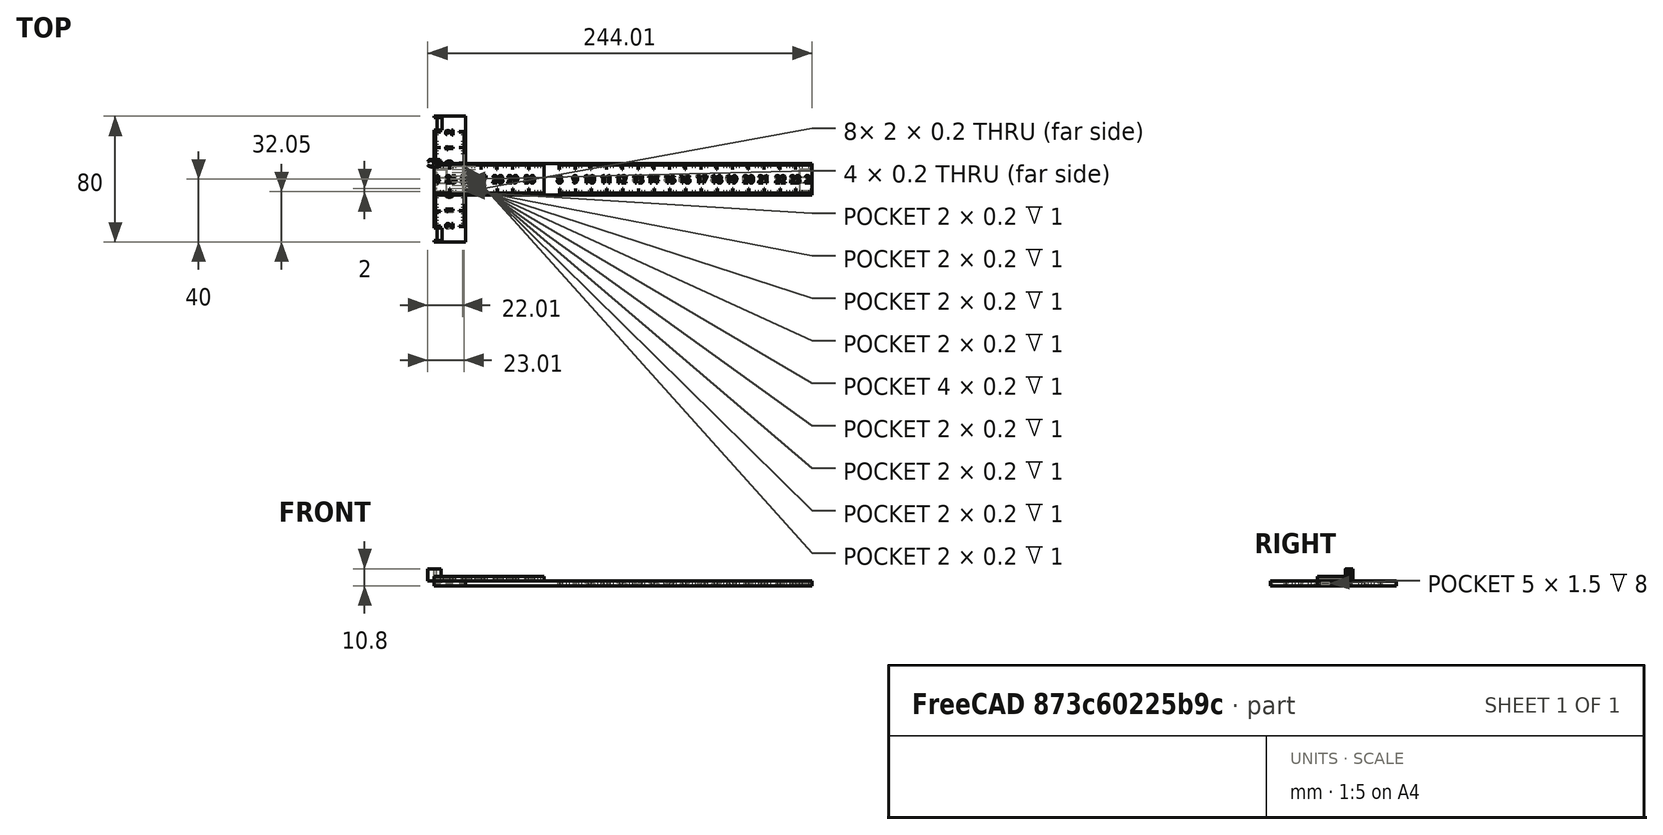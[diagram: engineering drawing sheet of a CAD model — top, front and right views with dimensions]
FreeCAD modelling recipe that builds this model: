
FCSTD DOCUMENT  (FreeCAD 0.20R26155 (Git))
Label: pocket text 30cm 2 sided Bow T Square
License: Creative Commons Attribution
LicenseURL: http://creativecommons.org/licenses/by/4.0/
objects: PartDesign::Pocket×22, Sketcher::SketchObject×20, Part::Part2DObjectPython×6, PartDesign::Pad×4, PartDesign::Body×4, Mesh::Feature×4, PartDesign::Plane×3, Spreadsheet::Sheet×1, PartDesign::Fillet×1
note: 87 computed .brp shape members not serialized (recipe doc carries the construction recipe); baked Part::Feature solids carry a one-line shape summary decoded from their .brp

FEATURE [Sketcher::SketchObject] Sketch  label="ruler"
  FullyConstrained = true
  MapMode = 5
  Support = -> [XY_Plane]
  expr: Constraints[11] = Spreadsheet.longL
  sketch-geometry (8):
    g0: LineSegment StartX=0 StartY=-50 StartZ=0 EndX=20 EndY=-50 EndZ=0
    g1: LineSegment StartX=20 StartY=-50 StartZ=0 EndX=20 EndY=-20 EndZ=0
    g2: LineSegment StartX=20 StartY=-20 StartZ=0 EndX=240 EndY=-20 EndZ=0
    g3: LineSegment StartX=240 StartY=-20 StartZ=0 EndX=240 EndY=0 EndZ=0
    g4: LineSegment StartX=0 StartY=30 StartZ=0 EndX=20 EndY=30 EndZ=0
    g5: LineSegment StartX=20 StartY=30 StartZ=0 EndX=20 EndY=0 EndZ=0
    g6: LineSegment StartX=20 StartY=0 StartZ=0 EndX=240 EndY=0 EndZ=0
    g7: LineSegment StartX=0 StartY=-50 StartZ=0 EndX=0 EndY=30 EndZ=0
  constraints (24):
    c: PointOnObject(g0,g-2)
    c: Horizontal(g0)
    c: Coincident(g0,g1)
    c: Vertical(g1)
    c: Coincident(g1,g2)
    c: Horizontal(g2)
    c: Coincident(g2,g3)
    c: PointOnObject(g3,g-1)
    c: Vertical(g3)
    c: Equal(g3,g0)
    c: DistanceY(g3,g3) = 20
    c: DistanceX(g-1,g3) = 240
    c: DistanceY(g0,g-1) = 50
    c: PointOnObject(g4,g-2)
    c: Horizontal(g4)
    c: Coincident(g4,g5)
    c: Vertical(g5)
    c: Coincident(g5,g6)
    c: Coincident(g6,g3)
    c: Horizontal(g6)
    c: Equal(g4,g0)
    c: Coincident(g7,g0)
    c: Coincident(g7,g4)
    c: DistanceY(g5,g5) = 30
FEATURE [PartDesign::Pad] Pad
  Direction = (1,1,1)
  Length = 3
  Length2 = 100
  Profile = -> Sketch
  Reversed = true
  Type = 0
FEATURE [Sketcher::SketchObject] Sketch001  label="hz cm"
  FullyConstrained = false
  MapMode = 5
  Support = -> [XY_Plane]
  expr: Constraints[9] = Spreadsheet.reticleCmWidth
  expr: Constraints[8] = Spreadsheet.reticleCmHeight
  sketch-geometry (171):
    g0: LineSegment StartX=239.9 StartY=-20 StartZ=0 EndX=239.7 EndY=-20 EndZ=0
    g1: LineSegment StartX=239.7 StartY=-20 StartZ=0 EndX=239.7 EndY=-16 EndZ=0
    g2: LineSegment StartX=239.7 StartY=-16 StartZ=0 EndX=239.9 EndY=-16 EndZ=0
    g3: LineSegment StartX=239.9 StartY=-16 StartZ=0 EndX=239.9 EndY=-20 EndZ=0
    g4: LineSegment StartX=-7.75171 StartY=-20 StartZ=0 EndX=225.791 EndY=-20 EndZ=0
    g5: LineSegment StartX=229.9 StartY=-20 StartZ=0 EndX=229.7 EndY=-20 EndZ=0
    g6: LineSegment StartX=229.7 StartY=-20 StartZ=0 EndX=229.7 EndY=-16 EndZ=0
    g7: LineSegment StartX=229.7 StartY=-16 StartZ=0 EndX=229.9 EndY=-16 EndZ=0
    g8: LineSegment StartX=229.9 StartY=-16 StartZ=0 EndX=229.9 EndY=-20 EndZ=0
    g9: LineSegment StartX=239.9 StartY=-20 StartZ=0 EndX=229.9 EndY=-20 EndZ=0
    g10: LineSegment StartX=219.9 StartY=-20 StartZ=0 EndX=219.7 EndY=-20 EndZ=0
    g11: LineSegment StartX=219.7 StartY=-20 StartZ=0 EndX=219.7 EndY=-16 EndZ=0
    g12: LineSegment StartX=219.7 StartY=-16 StartZ=0 EndX=219.9 EndY=-16 EndZ=0
    g13: LineSegment StartX=219.9 StartY=-16 StartZ=0 EndX=219.9 EndY=-20 EndZ=0
    g14: LineSegment StartX=229.9 StartY=-20 StartZ=0 EndX=219.9 EndY=-20 EndZ=0
    g15: LineSegment StartX=209.9 StartY=-20 StartZ=0 EndX=209.7 EndY=-20 EndZ=0
    g16: LineSegment StartX=209.7 StartY=-20 StartZ=0 EndX=209.7 EndY=-16 EndZ=0
    g17: LineSegment StartX=209.7 StartY=-16 StartZ=0 EndX=209.9 EndY=-16 EndZ=0
    g18: LineSegment StartX=209.9 StartY=-16 StartZ=0 EndX=209.9 EndY=-20 EndZ=0
    g19: LineSegment StartX=219.9 StartY=-20 StartZ=0 EndX=209.9 EndY=-20 EndZ=0
    g20: LineSegment StartX=199.9 StartY=-20 StartZ=0 EndX=199.7 EndY=-20 EndZ=0
    g21: LineSegment StartX=199.7 StartY=-20 StartZ=0 EndX=199.7 EndY=-16 EndZ=0
    g22: LineSegment StartX=199.7 StartY=-16 StartZ=0 EndX=199.9 EndY=-16 EndZ=0
    g23: LineSegment StartX=199.9 StartY=-16 StartZ=0 EndX=199.9 EndY=-20 EndZ=0
    g24: LineSegment StartX=209.9 StartY=-20 StartZ=0 EndX=199.9 EndY=-20 EndZ=0
    g25: LineSegment StartX=189.9 StartY=-20 StartZ=0 EndX=189.7 EndY=-20 EndZ=0
    g26: LineSegment StartX=189.7 StartY=-20 StartZ=0 EndX=189.7 EndY=-16 EndZ=0
    g27: LineSegment StartX=189.7 StartY=-16 StartZ=0 EndX=189.9 EndY=-16 EndZ=0
    g28: LineSegment StartX=189.9 StartY=-16 StartZ=0 EndX=189.9 EndY=-20 EndZ=0
    g29: LineSegment StartX=199.9 StartY=-20 StartZ=0 EndX=189.9 EndY=-20 EndZ=0
    g30: LineSegment StartX=179.9 StartY=-20 StartZ=0 EndX=179.7 EndY=-20 EndZ=0
    g31: LineSegment StartX=179.7 StartY=-20 StartZ=0 EndX=179.7 EndY=-16 EndZ=0
    g32: LineSegment StartX=179.7 StartY=-16 StartZ=0 EndX=179.9 EndY=-16 EndZ=0
    g33: LineSegment StartX=179.9 StartY=-16 StartZ=0 EndX=179.9 EndY=-20 EndZ=0
    g34: LineSegment StartX=189.9 StartY=-20 StartZ=0 EndX=179.9 EndY=-20 EndZ=0
    g35: LineSegment StartX=169.9 StartY=-20 StartZ=0 EndX=169.7 EndY=-20 EndZ=0
    g36: LineSegment StartX=169.7 StartY=-20 StartZ=0 EndX=169.7 EndY=-16 EndZ=0
    g37: LineSegment StartX=169.7 StartY=-16 StartZ=0 EndX=169.9 EndY=-16 EndZ=0
    g38: LineSegment StartX=169.9 StartY=-16 StartZ=0 EndX=169.9 EndY=-20 EndZ=0
    g39: LineSegment StartX=179.9 StartY=-20 StartZ=0 EndX=169.9 EndY=-20 EndZ=0
    g40: LineSegment StartX=159.9 StartY=-20 StartZ=0 EndX=159.7 EndY=-20 EndZ=0
    g41: LineSegment StartX=159.7 StartY=-20 StartZ=0 EndX=159.7 EndY=-16 EndZ=0
    g42: LineSegment StartX=159.7 StartY=-16 StartZ=0 EndX=159.9 EndY=-16 EndZ=0
    g43: LineSegment StartX=159.9 StartY=-16 StartZ=0 EndX=159.9 EndY=-20 EndZ=0
    g44: LineSegment StartX=169.9 StartY=-20 StartZ=0 EndX=159.9 EndY=-20 EndZ=0
    g45: LineSegment StartX=149.9 StartY=-20 StartZ=0 EndX=149.7 EndY=-20 EndZ=0
    g46: LineSegment StartX=149.7 StartY=-20 StartZ=0 EndX=149.7 EndY=-16 EndZ=0
    g47: LineSegment StartX=149.7 StartY=-16 StartZ=0 EndX=149.9 EndY=-16 EndZ=0
    g48: LineSegment StartX=149.9 StartY=-16 StartZ=0 EndX=149.9 EndY=-20 EndZ=0
    g49: LineSegment StartX=159.9 StartY=-20 StartZ=0 EndX=149.9 EndY=-20 EndZ=0
    g50: LineSegment StartX=139.9 StartY=-20 StartZ=0 EndX=139.7 EndY=-20 EndZ=0
    g51: LineSegment StartX=139.7 StartY=-20 StartZ=0 EndX=139.7 EndY=-16 EndZ=0
    g52: LineSegment StartX=139.7 StartY=-16 StartZ=0 EndX=139.9 EndY=-16 EndZ=0
    g53: LineSegment StartX=139.9 StartY=-16 StartZ=0 EndX=139.9 EndY=-20 EndZ=0
    g54: LineSegment StartX=149.9 StartY=-20 StartZ=0 EndX=139.9 EndY=-20 EndZ=0
    g55: LineSegment StartX=129.9 StartY=-20 StartZ=0 EndX=129.7 EndY=-20 EndZ=0
    g56: LineSegment StartX=129.7 StartY=-20 StartZ=0 EndX=129.7 EndY=-16 EndZ=0
    g57: LineSegment StartX=129.7 StartY=-16 StartZ=0 EndX=129.9 EndY=-16 EndZ=0
    g58: LineSegment StartX=129.9 StartY=-16 StartZ=0 EndX=129.9 EndY=-20 EndZ=0
    g59: LineSegment StartX=139.9 StartY=-20 StartZ=0 EndX=129.9 EndY=-20 EndZ=0
    g60: LineSegment StartX=119.9 StartY=-20 StartZ=0 EndX=119.7 EndY=-20 EndZ=0
    g61: LineSegment StartX=119.7 StartY=-20 StartZ=0 EndX=119.7 EndY=-16 EndZ=0
    g62: LineSegment StartX=119.7 StartY=-16 StartZ=0 EndX=119.9 EndY=-16 EndZ=0
    g63: LineSegment StartX=119.9 StartY=-16 StartZ=0 EndX=119.9 EndY=-20 EndZ=0
    g64: LineSegment StartX=129.9 StartY=-20 StartZ=0 EndX=119.9 EndY=-20 EndZ=0
    g65: LineSegment StartX=109.9 StartY=-20 StartZ=0 EndX=109.7 EndY=-20 EndZ=0
    g66: LineSegment StartX=109.7 StartY=-20 StartZ=0 EndX=109.7 EndY=-16 EndZ=0
    g67: LineSegment StartX=109.7 StartY=-16 StartZ=0 EndX=109.9 EndY=-16 EndZ=0
    g68: LineSegment StartX=109.9 StartY=-16 StartZ=0 EndX=109.9 EndY=-20 EndZ=0
    g69: LineSegment StartX=119.9 StartY=-20 StartZ=0 EndX=109.9 EndY=-20 EndZ=0
    g70: LineSegment StartX=99.9 StartY=-20 StartZ=0 EndX=99.7 EndY=-20 EndZ=0
    g71: LineSegment StartX=99.7 StartY=-20 StartZ=0 EndX=99.7 EndY=-16 EndZ=0
    g72: LineSegment StartX=99.7 StartY=-16 StartZ=0 EndX=99.9 EndY=-16 EndZ=0
    g73: LineSegment StartX=99.9 StartY=-16 StartZ=0 EndX=99.9 EndY=-20 EndZ=0
    g74: LineSegment StartX=109.9 StartY=-20 StartZ=0 EndX=99.9 EndY=-20 EndZ=0
    g75: LineSegment StartX=89.9 StartY=-20 StartZ=0 EndX=89.7 EndY=-20 EndZ=0
    g76: LineSegment StartX=89.7 StartY=-20 StartZ=0 EndX=89.7 EndY=-16 EndZ=0
    g77: LineSegment StartX=89.7 StartY=-16 StartZ=0 EndX=89.9 EndY=-16 EndZ=0
    g78: LineSegment StartX=89.9 StartY=-16 StartZ=0 EndX=89.9 EndY=-20 EndZ=0
    g79: LineSegment StartX=99.9 StartY=-20 StartZ=0 EndX=89.9 EndY=-20 EndZ=0
    g80: LineSegment StartX=79.9 StartY=-20 StartZ=0 EndX=79.7 EndY=-20 EndZ=0
    g81: LineSegment StartX=79.7 StartY=-20 StartZ=0 EndX=79.7 EndY=-16 EndZ=0
    g82: LineSegment StartX=79.7 StartY=-16 StartZ=0 EndX=79.9 EndY=-16 EndZ=0
    g83: LineSegment StartX=79.9 StartY=-16 StartZ=0 EndX=79.9 EndY=-20 EndZ=0
    g84: LineSegment StartX=89.9 StartY=-20 StartZ=0 EndX=79.9 EndY=-20 EndZ=0
    g85: LineSegment StartX=79.9 StartY=-20 StartZ=0 EndX=69.9 EndY=-20 EndZ=0
    g86: LineSegment StartX=239.7 StartY=-4 StartZ=0 EndX=239.9 EndY=-4 EndZ=0
    g87: LineSegment StartX=239.9 StartY=-4 StartZ=0 EndX=239.9 EndY=0 EndZ=0
    g88: LineSegment StartX=239.9 StartY=0 StartZ=0 EndX=239.7 EndY=0 EndZ=0
    g89: LineSegment StartX=239.7 StartY=0 StartZ=0 EndX=239.7 EndY=-4 EndZ=0
    g90: LineSegment StartX=229.7 StartY=-4 StartZ=0 EndX=229.5 EndY=-4 EndZ=0
    g91: LineSegment StartX=229.5 StartY=-4 StartZ=0 EndX=229.5 EndY=1.3e-15 EndZ=0
    g92: LineSegment StartX=229.5 StartY=1.3e-15 StartZ=0 EndX=229.7 EndY=1.3e-15 EndZ=0
    g93: LineSegment StartX=229.7 StartY=1.3e-15 StartZ=0 EndX=229.7 EndY=-4 EndZ=0
    g94: LineSegment StartX=239.7 StartY=-4 StartZ=0 EndX=229.7 EndY=-4 EndZ=0
    g95: LineSegment StartX=219.7 StartY=-4 StartZ=0 EndX=219.5 EndY=-4 EndZ=0
    g96: LineSegment StartX=219.5 StartY=-4 StartZ=0 EndX=219.5 EndY=2.2e-15 EndZ=0
    g97: LineSegment StartX=219.5 StartY=2.2e-15 StartZ=0 EndX=219.7 EndY=2.2e-15 EndZ=0
    g98: LineSegment StartX=219.7 StartY=2.2e-15 StartZ=0 EndX=219.7 EndY=-4 EndZ=0
    g99: LineSegment StartX=229.7 StartY=-4 StartZ=0 EndX=219.7 EndY=-4 EndZ=0
    g100: LineSegment StartX=209.7 StartY=-4 StartZ=0 EndX=209.5 EndY=-4 EndZ=0
    g101: LineSegment StartX=209.5 StartY=-4 StartZ=0 EndX=209.5 EndY=3.6e-15 EndZ=0
    g102: LineSegment StartX=209.5 StartY=3.6e-15 StartZ=0 EndX=209.7 EndY=3.6e-15 EndZ=0
    g103: LineSegment StartX=209.7 StartY=3.6e-15 StartZ=0 EndX=209.7 EndY=-4 EndZ=0
    g104: LineSegment StartX=219.7 StartY=-4 StartZ=0 EndX=209.7 EndY=-4 EndZ=0
    g105: LineSegment StartX=199.7 StartY=-4 StartZ=0 EndX=199.5 EndY=-4 EndZ=0
    g106: LineSegment StartX=199.5 StartY=-4 StartZ=0 EndX=199.5 EndY=4.9e-15 EndZ=0
    g107: LineSegment StartX=199.5 StartY=4.9e-15 StartZ=0 EndX=199.7 EndY=4.9e-15 EndZ=0
    g108: LineSegment StartX=199.7 StartY=4.9e-15 StartZ=0 EndX=199.7 EndY=-4 EndZ=0
    g109: LineSegment StartX=209.7 StartY=-4 StartZ=0 EndX=199.7 EndY=-4 EndZ=0
    g110: LineSegment StartX=189.7 StartY=-4 StartZ=0 EndX=189.5 EndY=-4 EndZ=0
    g111: LineSegment StartX=189.5 StartY=-4 StartZ=0 EndX=189.5 EndY=6.2e-15 EndZ=0
    g112: LineSegment StartX=189.5 StartY=6.2e-15 StartZ=0 EndX=189.7 EndY=6.2e-15 EndZ=0
    g113: LineSegment StartX=189.7 StartY=6.2e-15 StartZ=0 EndX=189.7 EndY=-4 EndZ=0
    g114: LineSegment StartX=199.7 StartY=-4 StartZ=0 EndX=189.7 EndY=-4 EndZ=0
    g115: LineSegment StartX=179.7 StartY=-4 StartZ=0 EndX=179.5 EndY=-4 EndZ=0
    g116: LineSegment StartX=179.5 StartY=-4 StartZ=0 EndX=179.5 EndY=7.5e-15 EndZ=0
    g117: LineSegment StartX=179.5 StartY=7.5e-15 StartZ=0 EndX=179.7 EndY=7.5e-15 EndZ=0
    g118: LineSegment StartX=179.7 StartY=7.5e-15 StartZ=0 EndX=179.7 EndY=-4 EndZ=0
    g119: LineSegment StartX=189.7 StartY=-4 StartZ=0 EndX=179.7 EndY=-4 EndZ=0
    g120: LineSegment StartX=169.7 StartY=-4 StartZ=0 EndX=169.5 EndY=-4 EndZ=0
    g121: LineSegment StartX=169.5 StartY=-4 StartZ=0 EndX=169.5 EndY=8.4e-15 EndZ=0
    g122: LineSegment StartX=169.5 StartY=8.4e-15 StartZ=0 EndX=169.7 EndY=8.4e-15 EndZ=0
    g123: LineSegment StartX=169.7 StartY=8.4e-15 StartZ=0 EndX=169.7 EndY=-4 EndZ=0
    g124: LineSegment StartX=179.7 StartY=-4 StartZ=0 EndX=169.7 EndY=-4 EndZ=0
    g125: LineSegment StartX=159.7 StartY=-4 StartZ=0 EndX=159.5 EndY=-4 EndZ=0
    g126: LineSegment StartX=159.5 StartY=-4 StartZ=0 EndX=159.5 EndY=9.8e-15 EndZ=0
    g127: LineSegment StartX=159.5 StartY=9.8e-15 StartZ=0 EndX=159.7 EndY=9.8e-15 EndZ=0
    g128: LineSegment StartX=159.7 StartY=9.8e-15 StartZ=0 EndX=159.7 EndY=-4 EndZ=0
    g129: LineSegment StartX=169.7 StartY=-4 StartZ=0 EndX=159.7 EndY=-4 EndZ=0
    g130: LineSegment StartX=149.7 StartY=-4 StartZ=0 EndX=149.5 EndY=-4 EndZ=0
    g131: LineSegment StartX=149.5 StartY=-4 StartZ=0 EndX=149.5 EndY=1.11e-14 EndZ=0
    g132: LineSegment StartX=149.5 StartY=1.11e-14 StartZ=0 EndX=149.7 EndY=1.11e-14 EndZ=0
    g133: LineSegment StartX=149.7 StartY=1.11e-14 StartZ=0 EndX=149.7 EndY=-4 EndZ=0
    g134: LineSegment StartX=159.7 StartY=-4 StartZ=0 EndX=149.7 EndY=-4 EndZ=0
    g135: LineSegment StartX=139.7 StartY=-4 StartZ=0 EndX=139.5 EndY=-4 EndZ=0
    g136: LineSegment StartX=139.5 StartY=-4 StartZ=0 EndX=139.5 EndY=1.24e-14 EndZ=0
    g137: LineSegment StartX=139.5 StartY=1.24e-14 StartZ=0 EndX=139.7 EndY=1.24e-14 EndZ=0
    g138: LineSegment StartX=139.7 StartY=1.24e-14 StartZ=0 EndX=139.7 EndY=-4 EndZ=0
    g139: LineSegment StartX=149.7 StartY=-4 StartZ=0 EndX=139.7 EndY=-4 EndZ=0
    g140: LineSegment StartX=129.7 StartY=-4 StartZ=0 EndX=129.5 EndY=-4 EndZ=0
    g141: LineSegment StartX=129.5 StartY=-4 StartZ=0 EndX=129.5 EndY=1.33e-14 EndZ=0
    g142: LineSegment StartX=129.5 StartY=1.33e-14 StartZ=0 EndX=129.7 EndY=1.33e-14 EndZ=0
    g143: LineSegment StartX=129.7 StartY=1.33e-14 StartZ=0 EndX=129.7 EndY=-4 EndZ=0
    g144: LineSegment StartX=139.7 StartY=-4 StartZ=0 EndX=129.7 EndY=-4 EndZ=0
    g145: LineSegment StartX=119.7 StartY=-4 StartZ=0 EndX=119.5 EndY=-4 EndZ=0
    g146: LineSegment StartX=119.5 StartY=-4 StartZ=0 EndX=119.5 EndY=1.47e-14 EndZ=0
    g147: LineSegment StartX=119.5 StartY=1.47e-14 StartZ=0 EndX=119.7 EndY=1.47e-14 EndZ=0
    g148: LineSegment StartX=119.7 StartY=1.47e-14 StartZ=0 EndX=119.7 EndY=-4 EndZ=0
    g149: LineSegment StartX=129.7 StartY=-4 StartZ=0 EndX=119.7 EndY=-4 EndZ=0
    g150: LineSegment StartX=109.7 StartY=-4 StartZ=0 EndX=109.5 EndY=-4 EndZ=0
    g151: LineSegment StartX=109.5 StartY=-4 StartZ=0 EndX=109.5 EndY=1.6e-14 EndZ=0
    g152: LineSegment StartX=109.5 StartY=1.6e-14 StartZ=0 EndX=109.7 EndY=1.6e-14 EndZ=0
    g153: LineSegment StartX=109.7 StartY=1.6e-14 StartZ=0 EndX=109.7 EndY=-4 EndZ=0
    g154: LineSegment StartX=119.7 StartY=-4 StartZ=0 EndX=109.7 EndY=-4 EndZ=0
    g155: LineSegment StartX=99.7 StartY=-4 StartZ=0 EndX=99.5 EndY=-4 EndZ=0
    g156: LineSegment StartX=99.5 StartY=-4 StartZ=0 EndX=99.5 EndY=1.69e-14 EndZ=0
    g157: LineSegment StartX=99.5 StartY=1.69e-14 StartZ=0 EndX=99.7 EndY=1.69e-14 EndZ=0
    g158: LineSegment StartX=99.7 StartY=1.69e-14 StartZ=0 EndX=99.7 EndY=-4 EndZ=0
    g159: LineSegment StartX=109.7 StartY=-4 StartZ=0 EndX=99.7 EndY=-4 EndZ=0
    g160: LineSegment StartX=89.7 StartY=-4 StartZ=0 EndX=89.5 EndY=-4 EndZ=0
    g161: LineSegment StartX=89.5 StartY=-4 StartZ=0 EndX=89.5 EndY=1.82e-14 EndZ=0
    g162: LineSegment StartX=89.5 StartY=1.82e-14 StartZ=0 EndX=89.7 EndY=1.82e-14 EndZ=0
    g163: LineSegment StartX=89.7 StartY=1.82e-14 StartZ=0 EndX=89.7 EndY=-4 EndZ=0
    g164: LineSegment StartX=99.7 StartY=-4 StartZ=0 EndX=89.7 EndY=-4 EndZ=0
    g165: LineSegment StartX=79.7 StartY=-4 StartZ=0 EndX=79.5 EndY=-4 EndZ=0
    g166: LineSegment StartX=79.5 StartY=-4 StartZ=0 EndX=79.5 EndY=1.95e-14 EndZ=0
    g167: LineSegment StartX=79.5 StartY=1.95e-14 StartZ=0 EndX=79.7 EndY=1.95e-14 EndZ=0
    g168: LineSegment StartX=79.7 StartY=1.95e-14 StartZ=0 EndX=79.7 EndY=-4 EndZ=0
    g169: LineSegment StartX=89.7 StartY=-4 StartZ=0 EndX=79.7 EndY=-4 EndZ=0
    g170: LineSegment StartX=79.7 StartY=-4 StartZ=0 EndX=69.7 EndY=-4 EndZ=0
  constraints (480):
    c: Coincident(g0,g1)
    c: Coincident(g1,g2)
    c: Coincident(g2,g3)
    c: Coincident(g3,g0)
    c: Horizontal(g0)
    c: Horizontal(g2)
    c: Vertical(g1)
    c: Vertical(g3)
    c: DistanceY(g3,g3) = 4
    c: DistanceX(g2,g2) = 0.2
    c: Horizontal(g4)
    c: DistanceY(g4,g-1) = 20
    c: PointOnObject(g0,g4)
    c: Coincident(g5,g6)
    c: Coincident(g6,g7)
    c: Coincident(g7,g8)
    c: Coincident(g8,g5)
    c: Horizontal(g5)
    c: Horizontal(g7)
    c: Vertical(g6)
    c: Vertical(g8)
    c: Equal(g3,g8) = 4
    c: Equal(g2,g7) = 0.35
    c: Coincident(g0,g9)
    c: Coincident(g5,g9)
    c: Distance(g9) = 10
    c: Angle(g9) = 3.14159
    c: Coincident(g10,g11)
    c: Coincident(g11,g12)
    c: Coincident(g12,g13)
    c: Coincident(g13,g10)
    c: Horizontal(g10)
    c: Horizontal(g12)
    c: Vertical(g11)
    c: Vertical(g13)
    c: Equal(g3,g13) = 4
    c: Equal(g2,g12) = 0.35
    c: Coincident(g5,g14)
    c: Coincident(g10,g14)
    c: Equal(g9,g14)
    c: Parallel(g14,g9)
    c: Coincident(g15,g16)
    c: Coincident(g16,g17)
    c: Coincident(g17,g18)
    c: Coincident(g18,g15)
    c: Horizontal(g15)
    c: Horizontal(g17)
    c: Vertical(g16)
    c: Vertical(g18)
    c: Equal(g3,g18) = 4
    c: Equal(g2,g17) = 0.35
    c: Coincident(g10,g19)
    c: Coincident(g15,g19)
    c: Equal(g9,g19)
    c: Parallel(g19,g9)
    c: Coincident(g20,g21)
    c: Coincident(g21,g22)
    c: Coincident(g22,g23)
    c: Coincident(g23,g20)
    c: Horizontal(g20)
    c: Horizontal(g22)
    c: Vertical(g21)
    c: Vertical(g23)
    c: Equal(g3,g23) = 4
    c: Equal(g2,g22) = 0.35
    c: Coincident(g15,g24)
    c: Coincident(g20,g24)
    c: Equal(g9,g24)
    c: Parallel(g24,g9)
    c: Coincident(g25,g26)
    c: Coincident(g26,g27)
    c: Coincident(g27,g28)
    c: Coincident(g28,g25)
    c: Horizontal(g25)
    c: Horizontal(g27)
    c: Vertical(g26)
    c: Vertical(g28)
    c: Equal(g3,g28) = 4
    c: Equal(g2,g27) = 0.35
    c: Coincident(g20,g29)
    c: Coincident(g25,g29)
    c: Equal(g9,g29)
    c: Parallel(g29,g9)
    c: Coincident(g30,g31)
    c: Coincident(g31,g32)
    c: Coincident(g32,g33)
    c: Coincident(g33,g30)
    c: Horizontal(g30)
    c: Horizontal(g32)
    c: Vertical(g31)
    c: Vertical(g33)
    c: Equal(g3,g33) = 4
    c: Equal(g2,g32) = 0.35
    c: Coincident(g25,g34)
    c: Coincident(g30,g34)
    c: Equal(g9,g34)
    c: Parallel(g34,g9)
    c: Coincident(g35,g36)
    c: Coincident(g36,g37)
    c: Coincident(g37,g38)
    c: Coincident(g38,g35)
    c: Horizontal(g35)
    c: Horizontal(g37)
    c: Vertical(g36)
    c: Vertical(g38)
    c: Equal(g3,g38) = 4
    c: Equal(g2,g37) = 0.35
    c: Coincident(g30,g39)
    c: Coincident(g35,g39)
    c: Equal(g9,g39)
    c: Parallel(g39,g9)
    c: Coincident(g40,g41)
    c: Coincident(g41,g42)
    c: Coincident(g42,g43)
    c: Coincident(g43,g40)
    c: Horizontal(g40)
    c: Horizontal(g42)
    c: Vertical(g41)
    c: Vertical(g43)
    c: Equal(g3,g43) = 4
    c: Equal(g2,g42) = 0.35
    c: Coincident(g35,g44)
    c: Coincident(g40,g44)
    c: Equal(g9,g44)
    c: Parallel(g44,g9)
    c: Coincident(g45,g46)
    c: Coincident(g46,g47)
    c: Coincident(g47,g48)
    c: Coincident(g48,g45)
    c: Horizontal(g45)
    c: Horizontal(g47)
    c: Vertical(g46)
    c: Vertical(g48)
    c: Equal(g3,g48) = 4
    c: Equal(g2,g47) = 0.35
    c: Coincident(g40,g49)
    c: Coincident(g45,g49)
    c: Equal(g9,g49)
    c: Parallel(g49,g9)
    c: Coincident(g50,g51)
    c: Coincident(g51,g52)
    c: Coincident(g52,g53)
    c: Coincident(g53,g50)
    c: Horizontal(g50)
    c: Horizontal(g52)
    c: Vertical(g51)
    c: Vertical(g53)
    c: Equal(g3,g53) = 4
    c: Equal(g2,g52) = 0.35
    c: Coincident(g45,g54)
    c: Coincident(g50,g54)
    c: Equal(g9,g54)
    c: Parallel(g54,g9)
    c: Coincident(g55,g56)
    c: Coincident(g56,g57)
    c: Coincident(g57,g58)
    c: Coincident(g58,g55)
    c: Horizontal(g55)
    c: Horizontal(g57)
    c: Vertical(g56)
    c: Vertical(g58)
    c: Equal(g3,g58) = 4
    c: Equal(g2,g57) = 0.35
    c: Coincident(g50,g59)
    c: Coincident(g55,g59)
    c: Equal(g9,g59)
    c: Parallel(g59,g9)
    c: Coincident(g60,g61)
    c: Coincident(g61,g62)
    c: Coincident(g62,g63)
    c: Coincident(g63,g60)
    c: Horizontal(g60)
    c: Horizontal(g62)
    c: Vertical(g61)
    c: Vertical(g63)
    c: Equal(g3,g63) = 4
    c: Equal(g2,g62) = 0.35
    c: Coincident(g55,g64)
    c: Coincident(g60,g64)
    c: Equal(g9,g64)
    c: Parallel(g64,g9)
    c: Coincident(g65,g66)
    c: Coincident(g66,g67)
    c: Coincident(g67,g68)
    c: Coincident(g68,g65)
    c: Horizontal(g65)
    c: Horizontal(g67)
    c: Vertical(g66)
    c: Vertical(g68)
    c: Equal(g3,g68) = 4
    c: Equal(g2,g67) = 0.35
    c: Coincident(g60,g69)
    c: Coincident(g65,g69)
    c: Equal(g9,g69)
    c: Parallel(g69,g9)
    c: Coincident(g70,g71)
    c: Coincident(g71,g72)
    c: Coincident(g72,g73)
    c: Coincident(g73,g70)
    c: Horizontal(g70)
    c: Horizontal(g72)
    c: Vertical(g71)
    c: Vertical(g73)
    c: Equal(g3,g73) = 4
    c: Equal(g2,g72) = 0.35
    c: Coincident(g65,g74)
    c: Coincident(g70,g74)
    c: Equal(g9,g74)
    c: Parallel(g74,g9)
    c: Coincident(g75,g76)
    c: Coincident(g76,g77)
    c: Coincident(g77,g78)
    c: Coincident(g78,g75)
    c: Horizontal(g75)
    c: Horizontal(g77)
    c: Vertical(g76)
    c: Vertical(g78)
    c: Equal(g3,g78) = 4
    c: Equal(g2,g77) = 0.35
    c: Coincident(g70,g79)
    c: Coincident(g75,g79)
    c: Equal(g9,g79)
    c: Parallel(g79,g9)
    c: Coincident(g80,g81)
    c: Coincident(g81,g82)
    c: Coincident(g82,g83)
    c: Coincident(g83,g80)
    c: Horizontal(g80)
    c: Horizontal(g82)
    c: Vertical(g81)
    c: Vertical(g83)
    c: Equal(g3,g83) = 4
    c: Equal(g2,g82) = 0.35
    c: Coincident(g75,g84)
    c: Coincident(g80,g84)
    c: Equal(g9,g84)
    c: Parallel(g84,g9)
    c: Coincident(g80,g85)
    c: Equal(g9,g85)
    c: Parallel(g85,g9)
    c: Coincident(g86,g87)
    c: Coincident(g87,g88)
    c: Coincident(g88,g89)
    c: Coincident(g89,g86)
    c: Horizontal(g86)
    c: Horizontal(g88)
    c: Vertical(g87)
    c: Vertical(g89)
    c: Equal(g3,g89) = 4
    c: Equal(g2,g88) = 0.35
    c: Coincident(g90,g91)
    c: Coincident(g91,g92)
    c: Coincident(g92,g93)
    c: Coincident(g93,g90)
    c: Horizontal(g90)
    c: Horizontal(g92)
    c: Vertical(g91)
    c: Vertical(g93)
    c: Equal(g3,g93) = 4
    c: Equal(g2,g92) = 0.35
    c: Coincident(g86,g94)
    c: Coincident(g90,g94)
    c: Equal(g9,g94)
    c: Parallel(g94,g9)
    c: Coincident(g95,g96)
    c: Coincident(g96,g97)
    c: Coincident(g97,g98)
    c: Coincident(g98,g95)
    c: Horizontal(g95)
    c: Horizontal(g97)
    c: Vertical(g96)
    c: Vertical(g98)
    c: Equal(g3,g98) = 4
    c: Equal(g2,g97) = 0.35
    c: Coincident(g90,g99)
    c: Coincident(g95,g99)
    c: Equal(g9,g99)
    c: Parallel(g99,g9)
    c: Coincident(g100,g101)
    c: Coincident(g101,g102)
    c: Coincident(g102,g103)
    c: Coincident(g103,g100)
    c: Horizontal(g100)
    c: Horizontal(g102)
    c: Vertical(g101)
    c: Vertical(g103)
    c: Equal(g3,g103) = 4
    c: Equal(g2,g102) = 0.35
    c: Coincident(g95,g104)
    c: Coincident(g100,g104)
    c: Equal(g9,g104)
    c: Parallel(g104,g9)
    c: Coincident(g105,g106)
    c: Coincident(g106,g107)
    c: Coincident(g107,g108)
    c: Coincident(g108,g105)
    c: Horizontal(g105)
    c: Horizontal(g107)
    c: Vertical(g106)
    c: Vertical(g108)
    c: Equal(g3,g108) = 4
    c: Equal(g2,g107) = 0.35
    c: Coincident(g100,g109)
    c: Coincident(g105,g109)
    c: Equal(g9,g109)
    c: Parallel(g109,g9)
    c: Coincident(g110,g111)
    c: Coincident(g111,g112)
    c: Coincident(g112,g113)
    c: Coincident(g113,g110)
    c: Horizontal(g110)
    c: Horizontal(g112)
    c: Vertical(g111)
    c: Vertical(g113)
    c: Equal(g3,g113) = 4
    c: Equal(g2,g112) = 0.35
    c: Coincident(g105,g114)
    c: Coincident(g110,g114)
    c: Equal(g9,g114)
    c: Parallel(g114,g9)
    c: Coincident(g115,g116)
    c: Coincident(g116,g117)
    c: Coincident(g117,g118)
    c: Coincident(g118,g115)
    c: Horizontal(g115)
    c: Horizontal(g117)
    c: Vertical(g116)
    c: Vertical(g118)
    c: Equal(g3,g118) = 4
    c: Equal(g2,g117) = 0.35
    c: Coincident(g110,g119)
    c: Coincident(g115,g119)
    c: Equal(g9,g119)
    c: Parallel(g119,g9)
    c: Coincident(g120,g121)
    c: Coincident(g121,g122)
    c: Coincident(g122,g123)
    c: Coincident(g123,g120)
    c: Horizontal(g120)
    c: Horizontal(g122)
    c: Vertical(g121)
    c: Vertical(g123)
    c: Equal(g3,g123) = 4
    c: Equal(g2,g122) = 0.35
    c: Coincident(g115,g124)
    c: Coincident(g120,g124)
    c: Equal(g9,g124)
    c: Parallel(g124,g9)
    c: Coincident(g125,g126)
    c: Coincident(g126,g127)
    c: Coincident(g127,g128)
    c: Coincident(g128,g125)
    c: Horizontal(g125)
    c: Horizontal(g127)
    c: Vertical(g126)
    c: Vertical(g128)
    c: Equal(g3,g128) = 4
    c: Equal(g2,g127) = 0.35
    c: Coincident(g120,g129)
    c: Coincident(g125,g129)
    c: Equal(g9,g129)
    c: Parallel(g129,g9)
    c: Coincident(g130,g131)
    c: Coincident(g131,g132)
    c: Coincident(g132,g133)
    c: Coincident(g133,g130)
    c: Horizontal(g130)
    c: Horizontal(g132)
    c: Vertical(g131)
    c: Vertical(g133)
    c: Equal(g3,g133) = 4
    c: Equal(g2,g132) = 0.35
    c: Coincident(g125,g134)
    c: Coincident(g130,g134)
    c: Equal(g9,g134)
    c: Parallel(g134,g9)
    c: Coincident(g135,g136)
    c: Coincident(g136,g137)
    c: Coincident(g137,g138)
    c: Coincident(g138,g135)
    c: Horizontal(g135)
    c: Horizontal(g137)
    c: Vertical(g136)
    c: Vertical(g138)
    c: Equal(g3,g138) = 4
    c: Equal(g2,g137) = 0.35
    c: Coincident(g130,g139)
    c: Coincident(g135,g139)
    c: Equal(g9,g139)
    c: Parallel(g139,g9)
    c: Coincident(g140,g141)
    c: Coincident(g141,g142)
    c: Coincident(g142,g143)
    c: Coincident(g143,g140)
    c: Horizontal(g140)
    c: Horizontal(g142)
    c: Vertical(g141)
    c: Vertical(g143)
    c: Equal(g3,g143) = 4
    c: Equal(g2,g142) = 0.35
    c: Coincident(g135,g144)
    c: Coincident(g140,g144)
    c: Equal(g9,g144)
    c: Parallel(g144,g9)
    c: Coincident(g145,g146)
    c: Coincident(g146,g147)
    c: Coincident(g147,g148)
    c: Coincident(g148,g145)
    c: Horizontal(g145)
    c: Horizontal(g147)
    c: Vertical(g146)
    c: Vertical(g148)
    c: Equal(g3,g148) = 4
    c: Equal(g2,g147) = 0.35
    c: Coincident(g140,g149)
    c: Coincident(g145,g149)
    c: Equal(g9,g149)
    c: Parallel(g149,g9)
    c: Coincident(g150,g151)
    c: Coincident(g151,g152)
    c: Coincident(g152,g153)
    c: Coincident(g153,g150)
    c: Horizontal(g150)
    c: Horizontal(g152)
    c: Vertical(g151)
    c: Vertical(g153)
    c: Equal(g3,g153) = 4
    c: Equal(g2,g152) = 0.35
    c: Coincident(g145,g154)
    c: Coincident(g150,g154)
    c: Equal(g9,g154)
    c: Parallel(g154,g9)
    c: Coincident(g155,g156)
    c: Coincident(g156,g157)
    c: Coincident(g157,g158)
    c: Coincident(g158,g155)
    c: Horizontal(g155)
    c: Horizontal(g157)
    c: Vertical(g156)
    c: Vertical(g158)
    c: Equal(g3,g158) = 4
    c: Equal(g2,g157) = 0.35
    c: Coincident(g150,g159)
    c: Coincident(g155,g159)
    c: Equal(g9,g159)
    c: Parallel(g159,g9)
    c: Coincident(g160,g161)
    c: Coincident(g161,g162)
    c: Coincident(g162,g163)
    c: Coincident(g163,g160)
    c: Horizontal(g160)
    c: Horizontal(g162)
    c: Vertical(g161)
    c: Vertical(g163)
    c: Equal(g3,g163) = 4
    c: Equal(g2,g162) = 0.35
    c: Coincident(g155,g164)
    c: Coincident(g160,g164)
    c: Equal(g9,g164)
    c: Parallel(g164,g9)
    c: Coincident(g165,g166)
    c: Coincident(g166,g167)
    c: Coincident(g167,g168)
    c: Coincident(g168,g165)
    c: Horizontal(g165)
    c: Horizontal(g167)
    c: Vertical(g166)
    c: Vertical(g168)
    c: Equal(g3,g168) = 4
    c: Equal(g2,g167) = 0.35
    c: Coincident(g160,g169)
    c: Coincident(g165,g169)
    c: Equal(g9,g169)
    c: Parallel(g169,g9)
    c: Coincident(g165,g170)
    c: Equal(g9,g170)
    c: Parallel(g170,g9)
    c: DistanceY(g-1,g87) = 0
    c: Vertical(g86,g2)
    c: DistanceX(g-1,g167) = 79.7
FEATURE [Spreadsheet::Sheet] Spreadsheet
  cells = A4=reticleCmWidth; B4(reticleCmWidth)=0.2; A5=reticleCmHeight; B5(reticleCmHeight)=4; A8=longL; B8(longL)=240; A9=shortL; B9(shortL)=120; A11=rulerThickness; B11=2; A13=clipWidth; B13(clipWidth)=3; A14=clipHeight; B14(clipHeight)=8; A15=clipIndent; B15(clipIndent)=2
FEATURE [PartDesign::Pocket] Pocket
  BaseFeature = -> Pad
  Length = 1
  Length2 = 100
  Profile = -> Sketch001
  Type = 0
FEATURE [Sketcher::SketchObject] Sketch002  label="vt cm"
  FullyConstrained = true
  MapMode = 5
  Support = -> [XY_Plane]
  expr: Constraints[7] = Spreadsheet.reticleCmHeight
  expr: Constraints[9] = Spreadsheet.reticleCmWidth
  sketch-geometry (57):
    g0: LineSegment StartX=-25 StartY=-20 StartZ=0 EndX=275 EndY=-20 EndZ=0
    g1: LineSegment StartX=0 StartY=-20.1 StartZ=0 EndX=4 EndY=-20.1 EndZ=0
    g2: LineSegment StartX=4 StartY=-20.1 StartZ=0 EndX=4 EndY=-19.9 EndZ=0
    g3: LineSegment StartX=4 StartY=-19.9 StartZ=0 EndX=0 EndY=-19.9 EndZ=0
    g4: LineSegment StartX=0 StartY=-19.9 StartZ=0 EndX=0 EndY=-20.1 EndZ=0
    g5: LineSegment StartX=16 StartY=-20.1 StartZ=0 EndX=20 EndY=-20.1 EndZ=0
    g6: LineSegment StartX=20 StartY=-20.1 StartZ=0 EndX=20 EndY=-19.9 EndZ=0
    g7: LineSegment StartX=20 StartY=-19.9 StartZ=0 EndX=16 EndY=-19.9 EndZ=0
    g8: LineSegment StartX=16 StartY=-19.9 StartZ=0 EndX=16 EndY=-20.1 EndZ=0
    g9: LineSegment StartX=0 StartY=-30.3 StartZ=0 EndX=4 EndY=-30.3 EndZ=0
    g10: LineSegment StartX=4 StartY=-30.3 StartZ=0 EndX=4 EndY=-30.5 EndZ=0
    g11: LineSegment StartX=4 StartY=-30.5 StartZ=0 EndX=0 EndY=-30.5 EndZ=0
    g12: LineSegment StartX=0 StartY=-30.5 StartZ=0 EndX=0 EndY=-30.3 EndZ=0
    g13: LineSegment StartX=16 StartY=-30.3 StartZ=0 EndX=20 EndY=-30.3 EndZ=0
    g14: LineSegment StartX=20 StartY=-30.3 StartZ=0 EndX=20 EndY=-30.1 EndZ=0
    g15: LineSegment StartX=20 StartY=-30.1 StartZ=0 EndX=16 EndY=-30.1 EndZ=0
    g16: LineSegment StartX=16 StartY=-30.1 StartZ=0 EndX=16 EndY=-30.3 EndZ=0
    g17: LineSegment StartX=0 StartY=-40.1 StartZ=0 EndX=4 EndY=-40.1 EndZ=0
    g18: LineSegment StartX=4 StartY=-40.1 StartZ=0 EndX=4 EndY=-39.9 EndZ=0
    g19: LineSegment StartX=4 StartY=-39.9 StartZ=0 EndX=0 EndY=-39.9 EndZ=0
    g20: LineSegment StartX=0 StartY=-39.9 StartZ=0 EndX=0 EndY=-40.1 EndZ=0
    g21: LineSegment StartX=16 StartY=-40.1 StartZ=0 EndX=20 EndY=-40.1 EndZ=0
    g22: LineSegment StartX=20 StartY=-40.1 StartZ=0 EndX=20 EndY=-39.9 EndZ=0
    g23: LineSegment StartX=20 StartY=-39.9 StartZ=0 EndX=16 EndY=-39.9 EndZ=0
    g24: LineSegment StartX=16 StartY=-39.9 StartZ=0 EndX=16 EndY=-40.1 EndZ=0
    g25: LineSegment StartX=16 StartY=10.1 StartZ=0 EndX=20 EndY=10.1 EndZ=0
    g26: LineSegment StartX=20 StartY=10.1 StartZ=0 EndX=20 EndY=9.9 EndZ=0
    g27: LineSegment StartX=20 StartY=9.9 StartZ=0 EndX=16 EndY=9.9 EndZ=0
    g28: LineSegment StartX=16 StartY=9.9 StartZ=0 EndX=16 EndY=10.1 EndZ=0
    g29: LineSegment StartX=0 StartY=-0.1 StartZ=0 EndX=4 EndY=-0.1 EndZ=0
    g30: LineSegment StartX=4 StartY=-0.1 StartZ=0 EndX=4 EndY=0.1 EndZ=0
    g31: LineSegment StartX=4 StartY=0.1 StartZ=0 EndX=0 EndY=0.1 EndZ=0
    g32: LineSegment StartX=0 StartY=0.1 StartZ=0 EndX=0 EndY=-0.1 EndZ=0
    g33: LineSegment StartX=16 StartY=-0.1 StartZ=0 EndX=20 EndY=-0.1 EndZ=0
    g34: LineSegment StartX=20 StartY=-0.1 StartZ=0 EndX=20 EndY=0.1 EndZ=0
    g35: LineSegment StartX=20 StartY=0.1 StartZ=0 EndX=16 EndY=0.1 EndZ=0
    g36: LineSegment StartX=16 StartY=0.1 StartZ=0 EndX=16 EndY=-0.1 EndZ=0
    g37: LineSegment StartX=0 StartY=-9.9 StartZ=0 EndX=4 EndY=-9.9 EndZ=0
    g38: LineSegment StartX=4 StartY=-9.9 StartZ=0 EndX=4 EndY=-10.1 EndZ=0
    g39: LineSegment StartX=4 StartY=-10.1 StartZ=0 EndX=0 EndY=-10.1 EndZ=0
    g40: LineSegment StartX=0 StartY=-10.1 StartZ=0 EndX=0 EndY=-9.9 EndZ=0
    g41: LineSegment StartX=16 StartY=-9.9 StartZ=0 EndX=20 EndY=-9.9 EndZ=0
    g42: LineSegment StartX=20 StartY=-9.9 StartZ=0 EndX=20 EndY=-10.1 EndZ=0
    g43: LineSegment StartX=20 StartY=-10.1 StartZ=0 EndX=16 EndY=-10.1 EndZ=0
    g44: LineSegment StartX=16 StartY=-10.1 StartZ=0 EndX=16 EndY=-9.9 EndZ=0
    g45: LineSegment StartX=16 StartY=20.1 StartZ=0 EndX=20 EndY=20.1 EndZ=0
    g46: LineSegment StartX=20 StartY=20.1 StartZ=0 EndX=20 EndY=19.9 EndZ=0
    g47: LineSegment StartX=20 StartY=19.9 StartZ=0 EndX=16 EndY=19.9 EndZ=0
    g48: LineSegment StartX=16 StartY=19.9 StartZ=0 EndX=16 EndY=20.1 EndZ=0
    g49: LineSegment StartX=0 StartY=9.9 StartZ=0 EndX=4 EndY=9.9 EndZ=0
    g50: LineSegment StartX=4 StartY=9.9 StartZ=0 EndX=4 EndY=10.1 EndZ=0
    g51: LineSegment StartX=4 StartY=10.1 StartZ=0 EndX=0 EndY=10.1 EndZ=0
    g52: LineSegment StartX=0 StartY=10.1 StartZ=0 EndX=0 EndY=9.9 EndZ=0
    g53: LineSegment StartX=0 StartY=19.9 StartZ=0 EndX=4 EndY=19.9 EndZ=0
    g54: LineSegment StartX=4 StartY=19.9 StartZ=0 EndX=4 EndY=20.1 EndZ=0
    g55: LineSegment StartX=4 StartY=20.1 StartZ=0 EndX=0 EndY=20.1 EndZ=0
    g56: LineSegment StartX=0 StartY=20.1 StartZ=0 EndX=0 EndY=19.9 EndZ=0
  constraints (171):
    c: Horizontal(g0)
    c: DistanceY(g0,g-1) = 20
    c: Coincident(g1,g2)
    c: Coincident(g2,g3)
    c: Horizontal(g1)
    c: Horizontal(g3)
    c: PointOnObject(g1,g-2)
    c: DistanceX(g3,g3) = 4
    c: Symmetric(g2,g1,g0)
    c: DistanceY(g2,g2) = 0.2
    c: Vertical(g1,g3)
    c: Coincident(g4,g3)
    c: Coincident(g4,g1)
    c: DistanceX(g0,g-1) = 25
    c: DistanceX(g0,g0) = 300
    c: Coincident(g5,g6)
    c: Coincident(g6,g7)
    c: Horizontal(g5)
    c: Horizontal(g7)
    c: Equal(g3,g7) = 4
    c: Equal(g2,g6) = 0.2
    c: Vertical(g5,g7)
    c: Coincident(g8,g7)
    c: Coincident(g8,g5)
    c: DistanceX(g3,g6) = 20
    c: Horizontal(g1,g5)
    c: Vertical(g6)
    c: Coincident(g9,g10)
    c: Coincident(g10,g11)
    c: Horizontal(g9)
    c: Horizontal(g11)
    c: Equal(g3,g11) = 4
    c: Equal(g2,g10) = 0.2
    c: Vertical(g9,g11)
    c: Coincident(g12,g11)
    c: Coincident(g12,g9)
    c: Coincident(g13,g14)
    c: Coincident(g14,g15)
    c: Horizontal(g13)
    c: Horizontal(g15)
    c: Equal(g11,g15) = 4
    c: Equal(g10,g14) = 0.2
    c: Vertical(g13,g15)
    c: Coincident(g16,g15)
    c: Coincident(g16,g13)
    c: DistanceX(g11,g14) = 20
    c: Horizontal(g9,g13)
    c: Vertical(g14)
    c: Vertical(g9,g1)
    c: Vertical(g10)
    c: DistanceY(g15,g5) = 10
    c: Coincident(g17,g18)
    c: Coincident(g18,g19)
    c: Horizontal(g17)
    c: Horizontal(g19)
    c: Equal(g3,g19) = 4
    c: Equal(g2,g18) = 0.2
    c: Vertical(g17,g19)
    c: Coincident(g20,g19)
    c: Coincident(g20,g17)
    c: Coincident(g21,g22)
    c: Coincident(g22,g23)
    c: Horizontal(g21)
    c: Horizontal(g23)
    c: Equal(g19,g23) = 4
    c: Equal(g18,g22) = 0.2
    c: Vertical(g21,g23)
    c: Coincident(g24,g23)
    c: Coincident(g24,g21)
    c: DistanceX(g19,g22) = 20
    c: Horizontal(g17,g21)
    c: Vertical(g22)
    c: Vertical(g17,g11)
    c: DistanceY(g21,g15) = 10
    c: Vertical(g18)
    c: Coincident(g25,g26)
    c: Coincident(g26,g27)
    c: Horizontal(g25)
    c: Horizontal(g27)
    c: Vertical(g25,g27)
    c: Coincident(g28,g27)
    c: Coincident(g28,g25)
    c: Vertical(g26)
    c: Coincident(g29,g30)
    c: Coincident(g30,g31)
    c: Horizontal(g29)
    c: Horizontal(g31)
    c: Vertical(g29,g31)
    c: Coincident(g32,g31)
    c: Coincident(g32,g29)
    c: Coincident(g33,g34)
    c: Coincident(g34,g35)
    c: Horizontal(g33)
    c: Horizontal(g35)
    c: Equal(g31,g35) = 4
    c: Equal(g30,g34) = 0.2
    c: Vertical(g33,g35)
    c: Coincident(g36,g35)
    c: Coincident(g36,g33)
    c: DistanceX(g31,g34) = 20
    c: Horizontal(g29,g33)
    c: Vertical(g34)
    c: Coincident(g37,g38)
    c: Coincident(g38,g39)
    c: Horizontal(g37)
    c: Horizontal(g39)
    c: Equal(g31,g39) = 4
    c: Equal(g30,g38) = 0.2
    c: Vertical(g37,g39)
    c: Coincident(g40,g39)
    c: Coincident(g40,g37)
    c: Coincident(g41,g42)
    c: Coincident(g42,g43)
    c: Horizontal(g41)
    c: Horizontal(g43)
    c: Equal(g39,g43) = 4
    c: Equal(g38,g42) = 0.2
    c: Vertical(g41,g43)
    c: Coincident(g44,g43)
    c: Coincident(g44,g41)
    c: DistanceX(g39,g42) = 20
    c: Horizontal(g37,g41)
    c: Vertical(g42)
    c: Vertical(g37,g29)
    c: Vertical(g38)
    c: DistanceY(g43,g33) = 10
    c: DistanceY(g33,g27) = 10
    c: Vertical(g30)
    c: Vertical(g3,g39)
    c: Equal(g7,g43)
    c: Equal(g8,g44)
    c: DistanceY(g5,g43) = 10
    c: Coincident(g45,g46)
    c: Coincident(g46,g47)
    c: Horizontal(g45)
    c: Horizontal(g47)
    c: Vertical(g45,g47)
    c: Coincident(g48,g47)
    c: Coincident(g48,g45)
    c: Vertical(g46)
    c: DistanceY(g27,g47) = 10
    c: Coincident(g49,g50)
    c: Coincident(g50,g51)
    c: Horizontal(g49)
    c: Horizontal(g51)
    c: Vertical(g49,g51)
    c: Coincident(g52,g51)
    c: Coincident(g52,g49)
    c: Vertical(g50)
    c: PointOnObject(g52,g-2)
    c: Horizontal(g49,g27)
    c: Equal(g30,g50)
    c: Equal(g36,g28)
    c: Vertical(g34,g26)
    c: Vertical(g46,g25)
    c: Equal(g28,g48)
    c: Vertical(g47,g25)
    c: Vertical(g30,g49)
    c: Vertical(g35,g27)
    c: Coincident(g53,g54)
    c: Coincident(g54,g55)
    c: Horizontal(g53)
    c: Horizontal(g55)
    c: Vertical(g53,g55)
    c: Coincident(g56,g55)
    c: Coincident(g56,g53)
    c: Vertical(g54)
    c: PointOnObject(g56,g-2)
    c: Equal(g50,g54)
    c: Vertical(g50,g53)
    c: Horizontal(g45,g54)
FEATURE [PartDesign::Pocket] Pocket001
  BaseFeature = -> Pocket
  Length = 1
  Length2 = 100
  Profile = -> Sketch002
  Type = 0
FEATURE [Sketcher::SketchObject] Sketch003  label="hz mm"
  FullyConstrained = true
  MapMode = 5
  Support = -> [XY_Plane]
  expr: Constraints[13] = Spreadsheet.reticleCmHeight / 2
  expr: Constraints[14] = Spreadsheet.reticleCmWidth
  sketch-geometry (513):
    g0: LineSegment StartX=-30 StartY=-20 StartZ=0 EndX=270 EndY=-20 EndZ=0
    g1: LineSegment StartX=238 StartY=0 StartZ=0 EndX=237.8 EndY=0 EndZ=0
    g2: LineSegment StartX=237.8 StartY=0 StartZ=0 EndX=237.8 EndY=-2 EndZ=0
    g3: LineSegment StartX=237.8 StartY=-2 StartZ=0 EndX=238 EndY=-2 EndZ=0
    g4: LineSegment StartX=238 StartY=-2 StartZ=0 EndX=238 EndY=0 EndZ=0
    g5: LineSegment StartX=236 StartY=0 StartZ=0 EndX=235.8 EndY=0 EndZ=0
    g6: LineSegment StartX=235.8 StartY=0 StartZ=0 EndX=235.8 EndY=-2 EndZ=0
    g7: LineSegment StartX=235.8 StartY=-2 StartZ=0 EndX=236 EndY=-2 EndZ=0
    g8: LineSegment StartX=236 StartY=-2 StartZ=0 EndX=236 EndY=0 EndZ=0
    g9: LineSegment StartX=234 StartY=0 StartZ=0 EndX=233.8 EndY=0 EndZ=0
    g10: LineSegment StartX=233.8 StartY=0 StartZ=0 EndX=233.8 EndY=-2 EndZ=0
    g11: LineSegment StartX=233.8 StartY=-2 StartZ=0 EndX=234 EndY=-2 EndZ=0
    g12: LineSegment StartX=234 StartY=-2 StartZ=0 EndX=234 EndY=0 EndZ=0
    g13: LineSegment StartX=231.8 StartY=0 StartZ=0 EndX=232 EndY=0 EndZ=0
    g14: LineSegment StartX=232 StartY=0 StartZ=0 EndX=232 EndY=-2 EndZ=0
    g15: LineSegment StartX=232 StartY=-2 StartZ=0 EndX=231.8 EndY=-2 EndZ=0
    g16: LineSegment StartX=231.8 StartY=-2 StartZ=0 EndX=231.8 EndY=0 EndZ=0
    g17: LineSegment StartX=227.8 StartY=0 StartZ=0 EndX=228 EndY=0 EndZ=0
    g18: LineSegment StartX=228 StartY=0 StartZ=0 EndX=228 EndY=-2 EndZ=0
    g19: LineSegment StartX=228 StartY=-2 StartZ=0 EndX=227.8 EndY=-2 EndZ=0
    g20: LineSegment StartX=227.8 StartY=-2 StartZ=0 EndX=227.8 EndY=0 EndZ=0
    g21: LineSegment StartX=226 StartY=0 StartZ=0 EndX=225.8 EndY=0 EndZ=0
    g22: LineSegment StartX=225.8 StartY=0 StartZ=0 EndX=225.8 EndY=-2 EndZ=0
    g23: LineSegment StartX=225.8 StartY=-2 StartZ=0 EndX=226 EndY=-2 EndZ=0
    g24: LineSegment StartX=226 StartY=-2 StartZ=0 EndX=226 EndY=0 EndZ=0
    g25: LineSegment StartX=224 StartY=0 StartZ=0 EndX=223.8 EndY=0 EndZ=0
    g26: LineSegment StartX=223.8 StartY=0 StartZ=0 EndX=223.8 EndY=-2 EndZ=0
    g27: LineSegment StartX=223.8 StartY=-2 StartZ=0 EndX=224 EndY=-2 EndZ=0
    g28: LineSegment StartX=224 StartY=-2 StartZ=0 EndX=224 EndY=0 EndZ=0
    g29: LineSegment StartX=221.8 StartY=0 StartZ=0 EndX=222 EndY=0 EndZ=0
    g30: LineSegment StartX=222 StartY=0 StartZ=0 EndX=222 EndY=-2 EndZ=0
    g31: LineSegment StartX=222 StartY=-2 StartZ=0 EndX=221.8 EndY=-2 EndZ=0
    g32: LineSegment StartX=221.8 StartY=-2 StartZ=0 EndX=221.8 EndY=0 EndZ=0
    g33: LineSegment StartX=218 StartY=0 StartZ=0 EndX=217.8 EndY=0 EndZ=0
    g34: LineSegment StartX=217.8 StartY=0 StartZ=0 EndX=217.8 EndY=-2 EndZ=0
    g35: LineSegment StartX=217.8 StartY=-2 StartZ=0 EndX=218 EndY=-2 EndZ=0
    g36: LineSegment StartX=218 StartY=-2 StartZ=0 EndX=218 EndY=0 EndZ=0
    g37: LineSegment StartX=216 StartY=0 StartZ=0 EndX=215.8 EndY=0 EndZ=0
    g38: LineSegment StartX=215.8 StartY=0 StartZ=0 EndX=215.8 EndY=-2 EndZ=0
    g39: LineSegment StartX=215.8 StartY=-2 StartZ=0 EndX=216 EndY=-2 EndZ=0
    g40: LineSegment StartX=216 StartY=-2 StartZ=0 EndX=216 EndY=0 EndZ=0
    g41: LineSegment StartX=214 StartY=0 StartZ=0 EndX=213.8 EndY=0 EndZ=0
    g42: LineSegment StartX=213.8 StartY=0 StartZ=0 EndX=213.8 EndY=-2 EndZ=0
    g43: LineSegment StartX=213.8 StartY=-2 StartZ=0 EndX=214 EndY=-2 EndZ=0
    g44: LineSegment StartX=214 StartY=-2 StartZ=0 EndX=214 EndY=0 EndZ=0
    g45: LineSegment StartX=211.8 StartY=0 StartZ=0 EndX=212 EndY=0 EndZ=0
    g46: LineSegment StartX=212 StartY=0 StartZ=0 EndX=212 EndY=-2 EndZ=0
    g47: LineSegment StartX=212 StartY=-2 StartZ=0 EndX=211.8 EndY=-2 EndZ=0
    g48: LineSegment StartX=211.8 StartY=-2 StartZ=0 EndX=211.8 EndY=0 EndZ=0
    g49: LineSegment StartX=208 StartY=0 StartZ=0 EndX=207.8 EndY=0 EndZ=0
    g50: LineSegment StartX=207.8 StartY=0 StartZ=0 EndX=207.8 EndY=-2 EndZ=0
    g51: LineSegment StartX=207.8 StartY=-2 StartZ=0 EndX=208 EndY=-2 EndZ=0
    g52: LineSegment StartX=208 StartY=-2 StartZ=0 EndX=208 EndY=0 EndZ=0
    g53: LineSegment StartX=206 StartY=0 StartZ=0 EndX=205.8 EndY=0 EndZ=0
    g54: LineSegment StartX=205.8 StartY=0 StartZ=0 EndX=205.8 EndY=-2 EndZ=0
    g55: LineSegment StartX=205.8 StartY=-2 StartZ=0 EndX=206 EndY=-2 EndZ=0
    g56: LineSegment StartX=206 StartY=-2 StartZ=0 EndX=206 EndY=0 EndZ=0
    g57: LineSegment StartX=204 StartY=0 StartZ=0 EndX=203.8 EndY=0 EndZ=0
    g58: LineSegment StartX=203.8 StartY=0 StartZ=0 EndX=203.8 EndY=-2 EndZ=0
    g59: LineSegment StartX=203.8 StartY=-2 StartZ=0 EndX=204 EndY=-2 EndZ=0
    g60: LineSegment StartX=204 StartY=-2 StartZ=0 EndX=204 EndY=0 EndZ=0
    g61: LineSegment StartX=201.8 StartY=0 StartZ=0 EndX=202 EndY=0 EndZ=0
    g62: LineSegment StartX=202 StartY=0 StartZ=0 EndX=202 EndY=-2 EndZ=0
    g63: LineSegment StartX=202 StartY=-2 StartZ=0 EndX=201.8 EndY=-2 EndZ=0
    g64: LineSegment StartX=201.8 StartY=-2 StartZ=0 EndX=201.8 EndY=0 EndZ=0
    g65: LineSegment StartX=197.8 StartY=0 StartZ=0 EndX=198 EndY=0 EndZ=0
    g66: LineSegment StartX=198 StartY=0 StartZ=0 EndX=198 EndY=-2 EndZ=0
    g67: LineSegment StartX=198 StartY=-2 StartZ=0 EndX=197.8 EndY=-2 EndZ=0
    g68: LineSegment StartX=197.8 StartY=-2 StartZ=0 EndX=197.8 EndY=0 EndZ=0
    g69: LineSegment StartX=196 StartY=0 StartZ=0 EndX=195.8 EndY=0 EndZ=0
    g70: LineSegment StartX=195.8 StartY=0 StartZ=0 EndX=195.8 EndY=-2 EndZ=0
    g71: LineSegment StartX=195.8 StartY=-2 StartZ=0 EndX=196 EndY=-2 EndZ=0
    g72: LineSegment StartX=196 StartY=-2 StartZ=0 EndX=196 EndY=0 EndZ=0
    g73: LineSegment StartX=194 StartY=0 StartZ=0 EndX=193.8 EndY=0 EndZ=0
    g74: LineSegment StartX=193.8 StartY=0 StartZ=0 EndX=193.8 EndY=-2 EndZ=0
    g75: LineSegment StartX=193.8 StartY=-2 StartZ=0 EndX=194 EndY=-2 EndZ=0
    g76: LineSegment StartX=194 StartY=-2 StartZ=0 EndX=194 EndY=0 EndZ=0
    g77: LineSegment StartX=191.8 StartY=0 StartZ=0 EndX=192 EndY=0 EndZ=0
    g78: LineSegment StartX=192 StartY=0 StartZ=0 EndX=192 EndY=-2 EndZ=0
    g79: LineSegment StartX=192 StartY=-2 StartZ=0 EndX=191.8 EndY=-2 EndZ=0
    g80: LineSegment StartX=191.8 StartY=-2 StartZ=0 EndX=191.8 EndY=0 EndZ=0
    g81: LineSegment StartX=188 StartY=0 StartZ=0 EndX=187.8 EndY=0 EndZ=0
    g82: LineSegment StartX=187.8 StartY=0 StartZ=0 EndX=187.8 EndY=-2 EndZ=0
    g83: LineSegment StartX=187.8 StartY=-2 StartZ=0 EndX=188 EndY=-2 EndZ=0
    g84: LineSegment StartX=188 StartY=-2 StartZ=0 EndX=188 EndY=0 EndZ=0
    g85: LineSegment StartX=186 StartY=0 StartZ=0 EndX=185.8 EndY=0 EndZ=0
    g86: LineSegment StartX=185.8 StartY=0 StartZ=0 EndX=185.8 EndY=-2 EndZ=0
    g87: LineSegment StartX=185.8 StartY=-2 StartZ=0 EndX=186 EndY=-2 EndZ=0
    g88: LineSegment StartX=186 StartY=-2 StartZ=0 EndX=186 EndY=0 EndZ=0
    g89: LineSegment StartX=184 StartY=0 StartZ=0 EndX=183.8 EndY=0 EndZ=0
    g90: LineSegment StartX=183.8 StartY=0 StartZ=0 EndX=183.8 EndY=-2 EndZ=0
    g91: LineSegment StartX=183.8 StartY=-2 StartZ=0 EndX=184 EndY=-2 EndZ=0
    g92: LineSegment StartX=184 StartY=-2 StartZ=0 EndX=184 EndY=0 EndZ=0
    g93: LineSegment StartX=181.8 StartY=0 StartZ=0 EndX=182 EndY=0 EndZ=0
    g94: LineSegment StartX=182 StartY=0 StartZ=0 EndX=182 EndY=-2 EndZ=0
    g95: LineSegment StartX=182 StartY=-2 StartZ=0 EndX=181.8 EndY=-2 EndZ=0
    g96: LineSegment StartX=181.8 StartY=-2 StartZ=0 EndX=181.8 EndY=0 EndZ=0
    g97: LineSegment StartX=177.8 StartY=0 StartZ=0 EndX=178 EndY=0 EndZ=0
    g98: LineSegment StartX=178 StartY=0 StartZ=0 EndX=178 EndY=-2 EndZ=0
    g99: LineSegment StartX=178 StartY=-2 StartZ=0 EndX=177.8 EndY=-2 EndZ=0
    g100: LineSegment StartX=177.8 StartY=-2 StartZ=0 EndX=177.8 EndY=0 EndZ=0
    g101: LineSegment StartX=176 StartY=0 StartZ=0 EndX=175.8 EndY=0 EndZ=0
    g102: LineSegment StartX=175.8 StartY=0 StartZ=0 EndX=175.8 EndY=-2 EndZ=0
    g103: LineSegment StartX=175.8 StartY=-2 StartZ=0 EndX=176 EndY=-2 EndZ=0
    g104: LineSegment StartX=176 StartY=-2 StartZ=0 EndX=176 EndY=0 EndZ=0
    g105: LineSegment StartX=174 StartY=0 StartZ=0 EndX=173.8 EndY=0 EndZ=0
    g106: LineSegment StartX=173.8 StartY=0 StartZ=0 EndX=173.8 EndY=-2 EndZ=0
    g107: LineSegment StartX=173.8 StartY=-2 StartZ=0 EndX=174 EndY=-2 EndZ=0
    g108: LineSegment StartX=174 StartY=-2 StartZ=0 EndX=174 EndY=0 EndZ=0
    g109: LineSegment StartX=171.8 StartY=0 StartZ=0 EndX=172 EndY=0 EndZ=0
    g110: LineSegment StartX=172 StartY=0 StartZ=0 EndX=172 EndY=-2 EndZ=0
    g111: LineSegment StartX=172 StartY=-2 StartZ=0 EndX=171.8 EndY=-2 EndZ=0
    g112: LineSegment StartX=171.8 StartY=-2 StartZ=0 EndX=171.8 EndY=0 EndZ=0
    g113: LineSegment StartX=167.8 StartY=0 StartZ=0 EndX=168 EndY=0 EndZ=0
    g114: LineSegment StartX=168 StartY=0 StartZ=0 EndX=168 EndY=-2 EndZ=0
    g115: LineSegment StartX=168 StartY=-2 StartZ=0 EndX=167.8 EndY=-2 EndZ=0
    g116: LineSegment StartX=167.8 StartY=-2 StartZ=0 EndX=167.8 EndY=0 EndZ=0
    g117: LineSegment StartX=166 StartY=0 StartZ=0 EndX=165.8 EndY=0 EndZ=0
    g118: LineSegment StartX=165.8 StartY=0 StartZ=0 EndX=165.8 EndY=-2 EndZ=0
    g119: LineSegment StartX=165.8 StartY=-2 StartZ=0 EndX=166 EndY=-2 EndZ=0
    g120: LineSegment StartX=166 StartY=-2 StartZ=0 EndX=166 EndY=0 EndZ=0
    g121: LineSegment StartX=164 StartY=0 StartZ=0 EndX=163.8 EndY=0 EndZ=0
    g122: LineSegment StartX=163.8 StartY=0 StartZ=0 EndX=163.8 EndY=-2 EndZ=0
    g123: LineSegment StartX=163.8 StartY=-2 StartZ=0 EndX=164 EndY=-2 EndZ=0
    g124: LineSegment StartX=164 StartY=-2 StartZ=0 EndX=164 EndY=0 EndZ=0
    g125: LineSegment StartX=161.8 StartY=0 StartZ=0 EndX=162 EndY=0 EndZ=0
    g126: LineSegment StartX=162 StartY=0 StartZ=0 EndX=162 EndY=-2 EndZ=0
    g127: LineSegment StartX=162 StartY=-2 StartZ=0 EndX=161.8 EndY=-2 EndZ=0
    g128: LineSegment StartX=161.8 StartY=-2 StartZ=0 EndX=161.8 EndY=0 EndZ=0
    g129: LineSegment StartX=158 StartY=0 StartZ=0 EndX=157.8 EndY=0 EndZ=0
    g130: LineSegment StartX=157.8 StartY=0 StartZ=0 EndX=157.8 EndY=-2 EndZ=0
    g131: LineSegment StartX=157.8 StartY=-2 StartZ=0 EndX=158 EndY=-2 EndZ=0
    g132: LineSegment StartX=158 StartY=-2 StartZ=0 EndX=158 EndY=0 EndZ=0
    g133: LineSegment StartX=156 StartY=0 StartZ=0 EndX=155.8 EndY=0 EndZ=0
    g134: LineSegment StartX=155.8 StartY=0 StartZ=0 EndX=155.8 EndY=-2 EndZ=0
    g135: LineSegment StartX=155.8 StartY=-2 StartZ=0 EndX=156 EndY=-2 EndZ=0
    g136: LineSegment StartX=156 StartY=-2 StartZ=0 EndX=156 EndY=0 EndZ=0
    g137: LineSegment StartX=154 StartY=0 StartZ=0 EndX=153.8 EndY=0 EndZ=0
    g138: LineSegment StartX=153.8 StartY=0 StartZ=0 EndX=153.8 EndY=-2 EndZ=0
    g139: LineSegment StartX=153.8 StartY=-2 StartZ=0 EndX=154 EndY=-2 EndZ=0
    g140: LineSegment StartX=154 StartY=-2 StartZ=0 EndX=154 EndY=0 EndZ=0
    g141: LineSegment StartX=151.8 StartY=0 StartZ=0 EndX=152 EndY=0 EndZ=0
    g142: LineSegment StartX=152 StartY=0 StartZ=0 EndX=152 EndY=-2 EndZ=0
    g143: LineSegment StartX=152 StartY=-2 StartZ=0 EndX=151.8 EndY=-2 EndZ=0
    g144: LineSegment StartX=151.8 StartY=-2 StartZ=0 EndX=151.8 EndY=0 EndZ=0
    g145: LineSegment StartX=148 StartY=0 StartZ=0 EndX=147.8 EndY=0 EndZ=0
    g146: LineSegment StartX=147.8 StartY=0 StartZ=0 EndX=147.8 EndY=-2 EndZ=0
    g147: LineSegment StartX=147.8 StartY=-2 StartZ=0 EndX=148 EndY=-2 EndZ=0
    g148: LineSegment StartX=148 StartY=-2 StartZ=0 EndX=148 EndY=0 EndZ=0
    g149: LineSegment StartX=146 StartY=0 StartZ=0 EndX=145.8 EndY=0 EndZ=0
    g150: LineSegment StartX=145.8 StartY=0 StartZ=0 EndX=145.8 EndY=-2 EndZ=0
    g151: LineSegment StartX=145.8 StartY=-2 StartZ=0 EndX=146 EndY=-2 EndZ=0
    g152: LineSegment StartX=146 StartY=-2 StartZ=0 EndX=146 EndY=0 EndZ=0
    g153: LineSegment StartX=144 StartY=0 StartZ=0 EndX=143.8 EndY=0 EndZ=0
    g154: LineSegment StartX=143.8 StartY=0 StartZ=0 EndX=143.8 EndY=-2 EndZ=0
    g155: LineSegment StartX=143.8 StartY=-2 StartZ=0 EndX=144 EndY=-2 EndZ=0
    g156: LineSegment StartX=144 StartY=-2 StartZ=0 EndX=144 EndY=0 EndZ=0
    g157: LineSegment StartX=141.8 StartY=0 StartZ=0 EndX=142 EndY=0 EndZ=0
    g158: LineSegment StartX=142 StartY=0 StartZ=0 EndX=142 EndY=-2 EndZ=0
    g159: LineSegment StartX=142 StartY=-2 StartZ=0 EndX=141.8 EndY=-2 EndZ=0
    g160: LineSegment StartX=141.8 StartY=-2 StartZ=0 EndX=141.8 EndY=0 EndZ=0
    g161: LineSegment StartX=137.8 StartY=0 StartZ=0 EndX=138 EndY=0 EndZ=0
    g162: LineSegment StartX=138 StartY=0 StartZ=0 EndX=138 EndY=-2 EndZ=0
    g163: LineSegment StartX=138 StartY=-2 StartZ=0 EndX=137.8 EndY=-2 EndZ=0
    g164: LineSegment StartX=137.8 StartY=-2 StartZ=0 EndX=137.8 EndY=0 EndZ=0
    g165: LineSegment StartX=136 StartY=0 StartZ=0 EndX=135.8 EndY=0 EndZ=0
    g166: LineSegment StartX=135.8 StartY=0 StartZ=0 EndX=135.8 EndY=-2 EndZ=0
    g167: LineSegment StartX=135.8 StartY=-2 StartZ=0 EndX=136 EndY=-2 EndZ=0
    g168: LineSegment StartX=136 StartY=-2 StartZ=0 EndX=136 EndY=0 EndZ=0
    g169: LineSegment StartX=134 StartY=0 StartZ=0 EndX=133.8 EndY=0 EndZ=0
    g170: LineSegment StartX=133.8 StartY=0 StartZ=0 EndX=133.8 EndY=-2 EndZ=0
    g171: LineSegment StartX=133.8 StartY=-2 StartZ=0 EndX=134 EndY=-2 EndZ=0
    g172: LineSegment StartX=134 StartY=-2 StartZ=0 EndX=134 EndY=0 EndZ=0
    g173: LineSegment StartX=131.8 StartY=0 StartZ=0 EndX=132 EndY=0 EndZ=0
    g174: LineSegment StartX=132 StartY=0 StartZ=0 EndX=132 EndY=-2 EndZ=0
    g175: LineSegment StartX=132 StartY=-2 StartZ=0 EndX=131.8 EndY=-2 EndZ=0
    g176: LineSegment StartX=131.8 StartY=-2 StartZ=0 EndX=131.8 EndY=0 EndZ=0
    g177: LineSegment StartX=128 StartY=0 StartZ=0 EndX=127.8 EndY=0 EndZ=0
    g178: LineSegment StartX=127.8 StartY=0 StartZ=0 EndX=127.8 EndY=-2 EndZ=0
    g179: LineSegment StartX=127.8 StartY=-2 StartZ=0 EndX=128 EndY=-2 EndZ=0
    g180: LineSegment StartX=128 StartY=-2 StartZ=0 EndX=128 EndY=0 EndZ=0
    g181: LineSegment StartX=126 StartY=0 StartZ=0 EndX=125.8 EndY=0 EndZ=0
    g182: LineSegment StartX=125.8 StartY=0 StartZ=0 EndX=125.8 EndY=-2 EndZ=0
    g183: LineSegment StartX=125.8 StartY=-2 StartZ=0 EndX=126 EndY=-2 EndZ=0
    g184: LineSegment StartX=126 StartY=-2 StartZ=0 EndX=126 EndY=0 EndZ=0
    g185: LineSegment StartX=124 StartY=0 StartZ=0 EndX=123.8 EndY=0 EndZ=0
    g186: LineSegment StartX=123.8 StartY=0 StartZ=0 EndX=123.8 EndY=-2 EndZ=0
    g187: LineSegment StartX=123.8 StartY=-2 StartZ=0 EndX=124 EndY=-2 EndZ=0
    g188: LineSegment StartX=124 StartY=-2 StartZ=0 EndX=124 EndY=0 EndZ=0
    g189: LineSegment StartX=122 StartY=0 StartZ=0 EndX=121.8 EndY=0 EndZ=0
    g190: LineSegment StartX=121.8 StartY=0 StartZ=0 EndX=121.8 EndY=-2 EndZ=0
    g191: LineSegment StartX=121.8 StartY=-2 StartZ=0 EndX=122 EndY=-2 EndZ=0
    g192: LineSegment StartX=122 StartY=-2 StartZ=0 EndX=122 EndY=0 EndZ=0
    g193: LineSegment StartX=118 StartY=0 StartZ=0 EndX=117.8 EndY=0 EndZ=0
    g194: LineSegment StartX=117.8 StartY=0 StartZ=0 EndX=117.8 EndY=-2 EndZ=0
    g195: LineSegment StartX=117.8 StartY=-2 StartZ=0 EndX=118 EndY=-2 EndZ=0
    g196: LineSegment StartX=118 StartY=-2 StartZ=0 EndX=118 EndY=0 EndZ=0
    g197: LineSegment StartX=116 StartY=0 StartZ=0 EndX=115.8 EndY=0 EndZ=0
    g198: LineSegment StartX=115.8 StartY=0 StartZ=0 EndX=115.8 EndY=-2 EndZ=0
    g199: LineSegment StartX=115.8 StartY=-2 StartZ=0 EndX=116 EndY=-2 EndZ=0
    g200: LineSegment StartX=116 StartY=-2 StartZ=0 EndX=116 EndY=0 EndZ=0
    g201: LineSegment StartX=114 StartY=0 StartZ=0 EndX=113.8 EndY=0 EndZ=0
    g202: LineSegment StartX=113.8 StartY=0 StartZ=0 EndX=113.8 EndY=-2 EndZ=0
    g203: LineSegment StartX=113.8 StartY=-2 StartZ=0 EndX=114 EndY=-2 EndZ=0
    g204: LineSegment StartX=114 StartY=-2 StartZ=0 EndX=114 EndY=0 EndZ=0
    g205: LineSegment StartX=112 StartY=0 StartZ=0 EndX=111.8 EndY=0 EndZ=0
    g206: LineSegment StartX=111.8 StartY=0 StartZ=0 EndX=111.8 EndY=-2 EndZ=0
    g207: LineSegment StartX=111.8 StartY=-2 StartZ=0 EndX=112 EndY=-2 EndZ=0
    g208: LineSegment StartX=112 StartY=-2 StartZ=0 EndX=112 EndY=0 EndZ=0
    g209: LineSegment StartX=107.8 StartY=0 StartZ=0 EndX=107.6 EndY=0 EndZ=0
    g210: LineSegment StartX=107.6 StartY=0 StartZ=0 EndX=107.6 EndY=-2 EndZ=0
    g211: LineSegment StartX=107.6 StartY=-2 StartZ=0 EndX=107.8 EndY=-2 EndZ=0
    g212: LineSegment StartX=107.8 StartY=-2 StartZ=0 EndX=107.8 EndY=0 EndZ=0
    g213: LineSegment StartX=106 StartY=0 StartZ=0 EndX=105.8 EndY=0 EndZ=0
    g214: LineSegment StartX=105.8 StartY=0 StartZ=0 EndX=105.8 EndY=-2 EndZ=0
    g215: LineSegment StartX=105.8 StartY=-2 StartZ=0 EndX=106 EndY=-2 EndZ=0
    g216: LineSegment StartX=106 StartY=-2 StartZ=0 EndX=106 EndY=0 EndZ=0
    g217: LineSegment StartX=104 StartY=0 StartZ=0 EndX=103.8 EndY=0 EndZ=0
    g218: LineSegment StartX=103.8 StartY=0 StartZ=0 EndX=103.8 EndY=-2 EndZ=0
    g219: LineSegment StartX=103.8 StartY=-2 StartZ=0 EndX=104 EndY=-2 EndZ=0
    g220: LineSegment StartX=104 StartY=-2 StartZ=0 EndX=104 EndY=0 EndZ=0
    g221: LineSegment StartX=101.8 StartY=0 StartZ=0 EndX=102 EndY=0 EndZ=0
    g222: LineSegment StartX=102 StartY=0 StartZ=0 EndX=102 EndY=-2 EndZ=0
    g223: LineSegment StartX=102 StartY=-2 StartZ=0 EndX=101.8 EndY=-2 EndZ=0
    g224: LineSegment StartX=101.8 StartY=-2 StartZ=0 EndX=101.8 EndY=0 EndZ=0
    g225: LineSegment StartX=98 StartY=0 StartZ=0 EndX=97.8 EndY=0 EndZ=0
    g226: LineSegment StartX=97.8 StartY=0 StartZ=0 EndX=97.8 EndY=-2 EndZ=0
    g227: LineSegment StartX=97.8 StartY=-2 StartZ=0 EndX=98 EndY=-2 EndZ=0
    g228: LineSegment StartX=98 StartY=-2 StartZ=0 EndX=98 EndY=0 EndZ=0
    g229: LineSegment StartX=96 StartY=0 StartZ=0 EndX=95.8 EndY=0 EndZ=0
    g230: LineSegment StartX=95.8 StartY=0 StartZ=0 EndX=95.8 EndY=-2 EndZ=0
    g231: LineSegment StartX=95.8 StartY=-2 StartZ=0 EndX=96 EndY=-2 EndZ=0
    g232: LineSegment StartX=96 StartY=-2 StartZ=0 EndX=96 EndY=0 EndZ=0
    g233: LineSegment StartX=94 StartY=0 StartZ=0 EndX=93.8 EndY=0 EndZ=0
    g234: LineSegment StartX=93.8 StartY=0 StartZ=0 EndX=93.8 EndY=-2 EndZ=0
    g235: LineSegment StartX=93.8 StartY=-2 StartZ=0 EndX=94 EndY=-2 EndZ=0
    g236: LineSegment StartX=94 StartY=-2 StartZ=0 EndX=94 EndY=0 EndZ=0
    g237: LineSegment StartX=92 StartY=0 StartZ=0 EndX=91.8 EndY=0 EndZ=0
    g238: LineSegment StartX=91.8 StartY=0 StartZ=0 EndX=91.8 EndY=-2 EndZ=0
    g239: LineSegment StartX=91.8 StartY=-2 StartZ=0 EndX=92 EndY=-2 EndZ=0
    g240: LineSegment StartX=92 StartY=-2 StartZ=0 EndX=92 EndY=0 EndZ=0
    g241: LineSegment StartX=88 StartY=0 StartZ=0 EndX=87.8 EndY=0 EndZ=0
    g242: LineSegment StartX=87.8 StartY=0 StartZ=0 EndX=87.8 EndY=-2 EndZ=0
    g243: LineSegment StartX=87.8 StartY=-2 StartZ=0 EndX=88 EndY=-2 EndZ=0
    g244: LineSegment StartX=88 StartY=-2 StartZ=0 EndX=88 EndY=0 EndZ=0
    g245: LineSegment StartX=86 StartY=0 StartZ=0 EndX=85.8 EndY=0 EndZ=0
    g246: LineSegment StartX=85.8 StartY=0 StartZ=0 EndX=85.8 EndY=-2 EndZ=0
    g247: LineSegment StartX=85.8 StartY=-2 StartZ=0 EndX=86 EndY=-2 EndZ=0
    g248: LineSegment StartX=86 StartY=-2 StartZ=0 EndX=86 EndY=0 EndZ=0
    g249: LineSegment StartX=84 StartY=0 StartZ=0 EndX=83.8 EndY=0 EndZ=0
    g250: LineSegment StartX=83.8 StartY=0 StartZ=0 EndX=83.8 EndY=-2 EndZ=0
    g251: LineSegment StartX=83.8 StartY=-2 StartZ=0 EndX=84 EndY=-2 EndZ=0
    g252: LineSegment StartX=84 StartY=-2 StartZ=0 EndX=84 EndY=0 EndZ=0
    g253: LineSegment StartX=81.6 StartY=0 StartZ=0 EndX=81.8 EndY=0 EndZ=0
    g254: LineSegment StartX=81.8 StartY=0 StartZ=0 EndX=81.8 EndY=-2 EndZ=0
    g255: LineSegment StartX=81.8 StartY=-2 StartZ=0 EndX=81.6 EndY=-2 EndZ=0
    g256: LineSegment StartX=81.6 StartY=-2 StartZ=0 EndX=81.6 EndY=0 EndZ=0
    g257: LineSegment StartX=238 StartY=-18 StartZ=0 EndX=237.8 EndY=-18 EndZ=0
    g258: LineSegment StartX=237.8 StartY=-18 StartZ=0 EndX=237.8 EndY=-20 EndZ=0
    g259: LineSegment StartX=237.8 StartY=-20 StartZ=0 EndX=238 EndY=-20 EndZ=0
    g260: LineSegment StartX=238 StartY=-20 StartZ=0 EndX=238 EndY=-18 EndZ=0
    g261: LineSegment StartX=236 StartY=-18 StartZ=0 EndX=235.8 EndY=-18 EndZ=0
    g262: LineSegment StartX=235.8 StartY=-18 StartZ=0 EndX=235.8 EndY=-20 EndZ=0
    g263: LineSegment StartX=235.8 StartY=-20 StartZ=0 EndX=236 EndY=-20 EndZ=0
    g264: LineSegment StartX=236 StartY=-20 StartZ=0 EndX=236 EndY=-18 EndZ=0
    g265: LineSegment StartX=234 StartY=-18 StartZ=0 EndX=233.8 EndY=-18 EndZ=0
    g266: LineSegment StartX=233.8 StartY=-18 StartZ=0 EndX=233.8 EndY=-20 EndZ=0
    g267: LineSegment StartX=233.8 StartY=-20 StartZ=0 EndX=234 EndY=-20 EndZ=0
    g268: LineSegment StartX=234 StartY=-20 StartZ=0 EndX=234 EndY=-18 EndZ=0
    g269: LineSegment StartX=231.8 StartY=-18 StartZ=0 EndX=232 EndY=-18 EndZ=0
    g270: LineSegment StartX=232 StartY=-18 StartZ=0 EndX=232 EndY=-20 EndZ=0
    g271: LineSegment StartX=232 StartY=-20 StartZ=0 EndX=231.8 EndY=-20 EndZ=0
    g272: LineSegment StartX=231.8 StartY=-20 StartZ=0 EndX=231.8 EndY=-18 EndZ=0
    g273: LineSegment StartX=227.8 StartY=-18 StartZ=0 EndX=228 EndY=-18 EndZ=0
    g274: LineSegment StartX=228 StartY=-18 StartZ=0 EndX=228 EndY=-20 EndZ=0
    g275: LineSegment StartX=228 StartY=-20 StartZ=0 EndX=227.8 EndY=-20 EndZ=0
    g276: LineSegment StartX=227.8 StartY=-20 StartZ=0 EndX=227.8 EndY=-18 EndZ=0
    g277: LineSegment StartX=226 StartY=-18 StartZ=0 EndX=225.8 EndY=-18 EndZ=0
    g278: LineSegment StartX=225.8 StartY=-18 StartZ=0 EndX=225.8 EndY=-20 EndZ=0
    g279: LineSegment StartX=225.8 StartY=-20 StartZ=0 EndX=226 EndY=-20 EndZ=0
    g280: LineSegment StartX=226 StartY=-20 StartZ=0 EndX=226 EndY=-18 EndZ=0
    g281: LineSegment StartX=224 StartY=-18 StartZ=0 EndX=223.8 EndY=-18 EndZ=0
    g282: LineSegment StartX=223.8 StartY=-18 StartZ=0 EndX=223.8 EndY=-20 EndZ=0
    g283: LineSegment StartX=223.8 StartY=-20 StartZ=0 EndX=224 EndY=-20 EndZ=0
    g284: LineSegment StartX=224 StartY=-20 StartZ=0 EndX=224 EndY=-18 EndZ=0
    g285: LineSegment StartX=221.8 StartY=-18 StartZ=0 EndX=222 EndY=-18 EndZ=0
    g286: LineSegment StartX=222 StartY=-18 StartZ=0 EndX=222 EndY=-20 EndZ=0
    g287: LineSegment StartX=222 StartY=-20 StartZ=0 EndX=221.8 EndY=-20 EndZ=0
    g288: LineSegment StartX=221.8 StartY=-20 StartZ=0 EndX=221.8 EndY=-18 EndZ=0
    g289: LineSegment StartX=218 StartY=-18 StartZ=0 EndX=217.8 EndY=-18 EndZ=0
    g290: LineSegment StartX=217.8 StartY=-18 StartZ=0 EndX=217.8 EndY=-20 EndZ=0
    g291: LineSegment StartX=217.8 StartY=-20 StartZ=0 EndX=218 EndY=-20 EndZ=0
    g292: LineSegment StartX=218 StartY=-20 StartZ=0 EndX=218 EndY=-18 EndZ=0
    g293: LineSegment StartX=216 StartY=-18 StartZ=0 EndX=215.8 EndY=-18 EndZ=0
    g294: LineSegment StartX=215.8 StartY=-18 StartZ=0 EndX=215.8 EndY=-20 EndZ=0
    g295: LineSegment StartX=215.8 StartY=-20 StartZ=0 EndX=216 EndY=-20 EndZ=0
    g296: LineSegment StartX=216 StartY=-20 StartZ=0 EndX=216 EndY=-18 EndZ=0
    g297: LineSegment StartX=214 StartY=-18 StartZ=0 EndX=213.8 EndY=-18 EndZ=0
    g298: LineSegment StartX=213.8 StartY=-18 StartZ=0 EndX=213.8 EndY=-20 EndZ=0
    g299: LineSegment StartX=213.8 StartY=-20 StartZ=0 EndX=214 EndY=-20 EndZ=0
    g300: LineSegment StartX=214 StartY=-20 StartZ=0 EndX=214 EndY=-18 EndZ=0
    g301: LineSegment StartX=211.8 StartY=-18 StartZ=0 EndX=212 EndY=-18 EndZ=0
    g302: LineSegment StartX=212 StartY=-18 StartZ=0 EndX=212 EndY=-20 EndZ=0
    g303: LineSegment StartX=212 StartY=-20 StartZ=0 EndX=211.8 EndY=-20 EndZ=0
    g304: LineSegment StartX=211.8 StartY=-20 StartZ=0 EndX=211.8 EndY=-18 EndZ=0
    g305: LineSegment StartX=208 StartY=-18 StartZ=0 EndX=207.8 EndY=-18 EndZ=0
    g306: LineSegment StartX=207.8 StartY=-18 StartZ=0 EndX=207.8 EndY=-20 EndZ=0
    g307: LineSegment StartX=207.8 StartY=-20 StartZ=0 EndX=208 EndY=-20 EndZ=0
    g308: LineSegment StartX=208 StartY=-20 StartZ=0 EndX=208 EndY=-18 EndZ=0
    g309: LineSegment StartX=206 StartY=-18 StartZ=0 EndX=205.8 EndY=-18 EndZ=0
    g310: LineSegment StartX=205.8 StartY=-18 StartZ=0 EndX=205.8 EndY=-20 EndZ=0
    g311: LineSegment StartX=205.8 StartY=-20 StartZ=0 EndX=206 EndY=-20 EndZ=0
    g312: LineSegment StartX=206 StartY=-20 StartZ=0 EndX=206 EndY=-18 EndZ=0
    g313: LineSegment StartX=204 StartY=-18 StartZ=0 EndX=203.8 EndY=-18 EndZ=0
    g314: LineSegment StartX=203.8 StartY=-18 StartZ=0 EndX=203.8 EndY=-20 EndZ=0
    g315: LineSegment StartX=203.8 StartY=-20 StartZ=0 EndX=204 EndY=-20 EndZ=0
    g316: LineSegment StartX=204 StartY=-20 StartZ=0 EndX=204 EndY=-18 EndZ=0
    g317: LineSegment StartX=201.8 StartY=-18 StartZ=0 EndX=202 EndY=-18 EndZ=0
    g318: LineSegment StartX=202 StartY=-18 StartZ=0 EndX=202 EndY=-20 EndZ=0
    g319: LineSegment StartX=202 StartY=-20 StartZ=0 EndX=201.8 EndY=-20 EndZ=0
    g320: LineSegment StartX=201.8 StartY=-20 StartZ=0 EndX=201.8 EndY=-18 EndZ=0
    g321: LineSegment StartX=197.8 StartY=-18 StartZ=0 EndX=198 EndY=-18 EndZ=0
    g322: LineSegment StartX=198 StartY=-18 StartZ=0 EndX=198 EndY=-20 EndZ=0
    g323: LineSegment StartX=198 StartY=-20 StartZ=0 EndX=197.8 EndY=-20 EndZ=0
    g324: LineSegment StartX=197.8 StartY=-20 StartZ=0 EndX=197.8 EndY=-18 EndZ=0
    g325: LineSegment StartX=196 StartY=-18 StartZ=0 EndX=195.8 EndY=-18 EndZ=0
    g326: LineSegment StartX=195.8 StartY=-18 StartZ=0 EndX=195.8 EndY=-20 EndZ=0
    g327: LineSegment StartX=195.8 StartY=-20 StartZ=0 EndX=196 EndY=-20 EndZ=0
    g328: LineSegment StartX=196 StartY=-20 StartZ=0 EndX=196 EndY=-18 EndZ=0
    g329: LineSegment StartX=194 StartY=-18 StartZ=0 EndX=193.8 EndY=-18 EndZ=0
    g330: LineSegment StartX=193.8 StartY=-18 StartZ=0 EndX=193.8 EndY=-20 EndZ=0
    g331: LineSegment StartX=193.8 StartY=-20 StartZ=0 EndX=194 EndY=-20 EndZ=0
    g332: LineSegment StartX=194 StartY=-20 StartZ=0 EndX=194 EndY=-18 EndZ=0
    g333: LineSegment StartX=191.8 StartY=-18 StartZ=0 EndX=192 EndY=-18 EndZ=0
    g334: LineSegment StartX=192 StartY=-18 StartZ=0 EndX=192 EndY=-20 EndZ=0
    g335: LineSegment StartX=192 StartY=-20 StartZ=0 EndX=191.8 EndY=-20 EndZ=0
    g336: LineSegment StartX=191.8 StartY=-20 StartZ=0 EndX=191.8 EndY=-18 EndZ=0
    g337: LineSegment StartX=188 StartY=-18 StartZ=0 EndX=187.8 EndY=-18 EndZ=0
    g338: LineSegment StartX=187.8 StartY=-18 StartZ=0 EndX=187.8 EndY=-20 EndZ=0
    g339: LineSegment StartX=187.8 StartY=-20 StartZ=0 EndX=188 EndY=-20 EndZ=0
    g340: LineSegment StartX=188 StartY=-20 StartZ=0 EndX=188 EndY=-18 EndZ=0
    g341: LineSegment StartX=186 StartY=-18 StartZ=0 EndX=185.8 EndY=-18 EndZ=0
    g342: LineSegment StartX=185.8 StartY=-18 StartZ=0 EndX=185.8 EndY=-20 EndZ=0
    g343: LineSegment StartX=185.8 StartY=-20 StartZ=0 EndX=186 EndY=-20 EndZ=0
    g344: LineSegment StartX=186 StartY=-20 StartZ=0 EndX=186 EndY=-18 EndZ=0
    g345: LineSegment StartX=184 StartY=-18 StartZ=0 EndX=183.8 EndY=-18 EndZ=0
    g346: LineSegment StartX=183.8 StartY=-18 StartZ=0 EndX=183.8 EndY=-20 EndZ=0
    g347: LineSegment StartX=183.8 StartY=-20 StartZ=0 EndX=184 EndY=-20 EndZ=0
    g348: LineSegment StartX=184 StartY=-20 StartZ=0 EndX=184 EndY=-18 EndZ=0
    g349: LineSegment StartX=181.8 StartY=-18 StartZ=0 EndX=182 EndY=-18 EndZ=0
    g350: LineSegment StartX=182 StartY=-18 StartZ=0 EndX=182 EndY=-20 EndZ=0
    g351: LineSegment StartX=182 StartY=-20 StartZ=0 EndX=181.8 EndY=-20 EndZ=0
    g352: LineSegment StartX=181.8 StartY=-20 StartZ=0 EndX=181.8 EndY=-18 EndZ=0
    g353: LineSegment StartX=177.8 StartY=-18 StartZ=0 EndX=178 EndY=-18 EndZ=0
    g354: LineSegment StartX=178 StartY=-18 StartZ=0 EndX=178 EndY=-20 EndZ=0
    g355: LineSegment StartX=178 StartY=-20 StartZ=0 EndX=177.8 EndY=-20 EndZ=0
    g356: LineSegment StartX=177.8 StartY=-20 StartZ=0 EndX=177.8 EndY=-18 EndZ=0
    g357: LineSegment StartX=176 StartY=-18 StartZ=0 EndX=175.8 EndY=-18 EndZ=0
    g358: LineSegment StartX=175.8 StartY=-18 StartZ=0 EndX=175.8 EndY=-20 EndZ=0
    g359: LineSegment StartX=175.8 StartY=-20 StartZ=0 EndX=176 EndY=-20 EndZ=0
    g360: LineSegment StartX=176 StartY=-20 StartZ=0 EndX=176 EndY=-18 EndZ=0
    g361: LineSegment StartX=174 StartY=-18 StartZ=0 EndX=173.8 EndY=-18 EndZ=0
    g362: LineSegment StartX=173.8 StartY=-18 StartZ=0 EndX=173.8 EndY=-20 EndZ=0
    g363: LineSegment StartX=173.8 StartY=-20 StartZ=0 EndX=174 EndY=-20 EndZ=0
    g364: LineSegment StartX=174 StartY=-20 StartZ=0 EndX=174 EndY=-18 EndZ=0
    g365: LineSegment StartX=171.8 StartY=-18 StartZ=0 EndX=172 EndY=-18 EndZ=0
    g366: LineSegment StartX=172 StartY=-18 StartZ=0 EndX=172 EndY=-20 EndZ=0
    g367: LineSegment StartX=172 StartY=-20 StartZ=0 EndX=171.8 EndY=-20 EndZ=0
    g368: LineSegment StartX=171.8 StartY=-20 StartZ=0 EndX=171.8 EndY=-18 EndZ=0
    g369: LineSegment StartX=167.8 StartY=-18 StartZ=0 EndX=168 EndY=-18 EndZ=0
    g370: LineSegment StartX=168 StartY=-18 StartZ=0 EndX=168 EndY=-20 EndZ=0
    g371: LineSegment StartX=168 StartY=-20 StartZ=0 EndX=167.8 EndY=-20 EndZ=0
    g372: LineSegment StartX=167.8 StartY=-20 StartZ=0 EndX=167.8 EndY=-18 EndZ=0
    g373: LineSegment StartX=166 StartY=-18 StartZ=0 EndX=165.8 EndY=-18 EndZ=0
    g374: LineSegment StartX=165.8 StartY=-18 StartZ=0 EndX=165.8 EndY=-20 EndZ=0
    g375: LineSegment StartX=165.8 StartY=-20 StartZ=0 EndX=166 EndY=-20 EndZ=0
    g376: LineSegment StartX=166 StartY=-20 StartZ=0 EndX=166 EndY=-18 EndZ=0
    g377: LineSegment StartX=164 StartY=-18 StartZ=0 EndX=163.8 EndY=-18 EndZ=0
    g378: LineSegment StartX=163.8 StartY=-18 StartZ=0 EndX=163.8 EndY=-20 EndZ=0
    g379: LineSegment StartX=163.8 StartY=-20 StartZ=0 EndX=164 EndY=-20 EndZ=0
    g380: LineSegment StartX=164 StartY=-20 StartZ=0 EndX=164 EndY=-18 EndZ=0
    g381: LineSegment StartX=161.8 StartY=-18 StartZ=0 EndX=162 EndY=-18 EndZ=0
    g382: LineSegment StartX=162 StartY=-18 StartZ=0 EndX=162 EndY=-20 EndZ=0
    g383: LineSegment StartX=162 StartY=-20 StartZ=0 EndX=161.8 EndY=-20 EndZ=0
    g384: LineSegment StartX=161.8 StartY=-20 StartZ=0 EndX=161.8 EndY=-18 EndZ=0
    g385: LineSegment StartX=158 StartY=-18 StartZ=0 EndX=157.8 EndY=-18 EndZ=0
    g386: LineSegment StartX=157.8 StartY=-18 StartZ=0 EndX=157.8 EndY=-20 EndZ=0
    g387: LineSegment StartX=157.8 StartY=-20 StartZ=0 EndX=158 EndY=-20 EndZ=0
    g388: LineSegment StartX=158 StartY=-20 StartZ=0 EndX=158 EndY=-18 EndZ=0
    g389: LineSegment StartX=156 StartY=-18 StartZ=0 EndX=155.8 EndY=-18 EndZ=0
    g390: LineSegment StartX=155.8 StartY=-18 StartZ=0 EndX=155.8 EndY=-20 EndZ=0
    g391: LineSegment StartX=155.8 StartY=-20 StartZ=0 EndX=156 EndY=-20 EndZ=0
    g392: LineSegment StartX=156 StartY=-20 StartZ=0 EndX=156 EndY=-18 EndZ=0
    g393: LineSegment StartX=154 StartY=-18 StartZ=0 EndX=153.8 EndY=-18 EndZ=0
    g394: LineSegment StartX=153.8 StartY=-18 StartZ=0 EndX=153.8 EndY=-20 EndZ=0
    g395: LineSegment StartX=153.8 StartY=-20 StartZ=0 EndX=154 EndY=-20 EndZ=0
    g396: LineSegment StartX=154 StartY=-20 StartZ=0 EndX=154 EndY=-18 EndZ=0
    g397: LineSegment StartX=151.8 StartY=-18 StartZ=0 EndX=152 EndY=-18 EndZ=0
    g398: LineSegment StartX=152 StartY=-18 StartZ=0 EndX=152 EndY=-20 EndZ=0
    g399: LineSegment StartX=152 StartY=-20 StartZ=0 EndX=151.8 EndY=-20 EndZ=0
    ... +113 more geometry lines
  constraints (1540):
    c: Horizontal(g0)
    c: DistanceY(g0,g-1) = 20
    c: DistanceX(g0,g0) = 300
    c: DistanceX(g0,g-1) = 30
    c: Coincident(g1,g2)
    c: Coincident(g2,g3)
    c: Coincident(g3,g4)
    c: Coincident(g4,g1)
    c: Horizontal(g1)
    c: Horizontal(g3)
    c: Vertical(g2)
    c: Vertical(g4)
    c: PointOnObject(g1,g-1)
    c: DistanceY(g4,g4) = 2
    c: DistanceX(g3,g3) = 0.2
    c: Coincident(g5,g6)
    c: Coincident(g6,g7)
    c: Coincident(g7,g8)
    c: Coincident(g8,g5)
    c: Horizontal(g5)
    c: Horizontal(g7)
    c: Vertical(g6)
    c: Vertical(g8)
    c: Equal(g4,g8) = 2
    c: Equal(g3,g7) = 0.2
    c: Coincident(g9,g10)
    c: Coincident(g10,g11)
    c: Coincident(g11,g12)
    c: Coincident(g12,g9)
    c: Horizontal(g9)
    c: Horizontal(g11)
    c: Vertical(g10)
    c: Vertical(g12)
    c: Equal(g8,g12) = 2
    c: Equal(g7,g11) = 0.2
    c: DistanceX(g9,g5) = 2
    c: Coincident(g13,g14)
    c: Coincident(g14,g15)
    c: Coincident(g15,g16)
    c: Coincident(g16,g13)
    c: Horizontal(g13)
    c: Horizontal(g15)
    c: Vertical(g14)
    c: Vertical(g16)
    c: Equal(g11,g15)
    c: Equal(g10,g14)
    c: Horizontal(g1,g5)
    c: Horizontal(g5,g9)
    c: Horizontal(g9,g13)
    c: Coincident(g17,g18)
    c: Coincident(g18,g19)
    c: Coincident(g19,g20)
    c: Coincident(g20,g17)
    c: Horizontal(g17)
    c: Horizontal(g19)
    c: Vertical(g18)
    c: Vertical(g20)
    c: Equal(g4,g20) = 2
    c: Equal(g3,g19) = 0.2
    c: Coincident(g21,g22)
    c: Coincident(g22,g23)
    c: Coincident(g23,g24)
    c: Coincident(g24,g21)
    c: Horizontal(g21)
    c: Horizontal(g23)
    c: Vertical(g22)
    c: Vertical(g24)
    c: Equal(g20,g24) = 2
    c: Equal(g19,g23) = 0.2
    c: Coincident(g25,g26)
    c: Coincident(g26,g27)
    c: Coincident(g27,g28)
    c: Coincident(g28,g25)
    c: Horizontal(g25)
    c: Horizontal(g27)
    c: Vertical(g26)
    c: Vertical(g28)
    c: Equal(g24,g28) = 2
    c: Equal(g23,g27) = 0.2
    c: DistanceX(g25,g21) = 2
    c: Coincident(g29,g30)
    c: Coincident(g30,g31)
    c: Coincident(g31,g32)
    c: Coincident(g32,g29)
    c: Horizontal(g29)
    c: Horizontal(g31)
    c: Vertical(g30)
    c: Vertical(g32)
    c: Equal(g27,g31)
    c: Equal(g26,g30)
    c: Horizontal(g17,g21)
    c: Horizontal(g21,g25)
    c: Horizontal(g25,g29)
    c: PointOnObject(g17,g-1)
    c: Coincident(g33,g34)
    c: Coincident(g34,g35)
    c: Coincident(g35,g36)
    c: Coincident(g36,g33)
    c: Horizontal(g33)
    c: Horizontal(g35)
    c: Vertical(g34)
    c: Vertical(g36)
    c: Coincident(g37,g38)
    c: Coincident(g38,g39)
    c: Coincident(g39,g40)
    c: Coincident(g40,g37)
    c: Horizontal(g37)
    c: Horizontal(g39)
    c: Vertical(g38)
    c: Vertical(g40)
    c: Equal(g36,g40) = 2
    c: Equal(g35,g39) = 0.2
    c: Coincident(g41,g42)
    c: Coincident(g42,g43)
    c: Coincident(g43,g44)
    c: Coincident(g44,g41)
    c: Horizontal(g41)
    c: Horizontal(g43)
    c: Vertical(g42)
    c: Vertical(g44)
    c: Equal(g40,g44) = 2
    c: Equal(g39,g43) = 0.2
    c: DistanceX(g41,g37) = 2
    c: Coincident(g45,g46)
    c: Coincident(g46,g47)
    c: Coincident(g47,g48)
    c: Coincident(g48,g45)
    c: Horizontal(g45)
    c: Horizontal(g47)
    c: Vertical(g46)
    c: Vertical(g48)
    c: Equal(g43,g47)
    c: Equal(g42,g46)
    c: Horizontal(g33,g37)
    c: Horizontal(g37,g41)
    c: Horizontal(g41,g45)
    c: PointOnObject(g33,g-1)
    c: Coincident(g49,g50)
    c: Coincident(g50,g51)
    c: Coincident(g51,g52)
    c: Coincident(g52,g49)
    c: Horizontal(g49)
    c: Horizontal(g51)
    c: Vertical(g50)
    c: Vertical(g52)
    c: Equal(g4,g52) = 2
    c: Equal(g3,g51) = 0.2
    c: Coincident(g53,g54)
    c: Coincident(g54,g55)
    c: Coincident(g55,g56)
    c: Coincident(g56,g53)
    c: Horizontal(g53)
    c: Horizontal(g55)
    c: Vertical(g54)
    c: Vertical(g56)
    c: Equal(g52,g56) = 2
    c: Equal(g51,g55) = 0.2
    c: Coincident(g57,g58)
    c: Coincident(g58,g59)
    c: Coincident(g59,g60)
    c: Coincident(g60,g57)
    c: Horizontal(g57)
    c: Horizontal(g59)
    c: Vertical(g58)
    c: Vertical(g60)
    c: Equal(g56,g60) = 2
    c: Equal(g55,g59) = 0.2
    c: DistanceX(g57,g53) = 2
    c: Coincident(g61,g62)
    c: Coincident(g62,g63)
    c: Coincident(g63,g64)
    c: Coincident(g64,g61)
    c: Horizontal(g61)
    c: Horizontal(g63)
    c: Vertical(g62)
    c: Vertical(g64)
    c: Equal(g59,g63)
    c: Equal(g58,g62)
    c: Horizontal(g49,g53)
    c: Horizontal(g53,g57)
    c: Horizontal(g57,g61)
    c: Coincident(g65,g66)
    c: Coincident(g66,g67)
    c: Coincident(g67,g68)
    c: Coincident(g68,g65)
    c: Horizontal(g65)
    c: Horizontal(g67)
    c: Vertical(g66)
    c: Vertical(g68)
    c: Equal(g52,g68) = 2
    c: Equal(g51,g67) = 0.2
    c: Coincident(g69,g70)
    c: Coincident(g70,g71)
    c: Coincident(g71,g72)
    c: Coincident(g72,g69)
    c: Horizontal(g69)
    c: Horizontal(g71)
    c: Vertical(g70)
    c: Vertical(g72)
    c: Equal(g68,g72) = 2
    c: Equal(g67,g71) = 0.2
    c: Coincident(g73,g74)
    c: Coincident(g74,g75)
    c: Coincident(g75,g76)
    c: Coincident(g76,g73)
    c: Horizontal(g73)
    c: Horizontal(g75)
    c: Vertical(g74)
    c: Vertical(g76)
    c: Equal(g72,g76) = 2
    c: Equal(g71,g75) = 0.2
    c: DistanceX(g73,g69) = 2
    c: Coincident(g77,g78)
    c: Coincident(g78,g79)
    c: Coincident(g79,g80)
    c: Coincident(g80,g77)
    c: Horizontal(g77)
    c: Horizontal(g79)
    c: Vertical(g78)
    c: Vertical(g80)
    c: Equal(g75,g79)
    c: Equal(g74,g78)
    c: Horizontal(g65,g69)
    c: Horizontal(g69,g73)
    c: Horizontal(g73,g77)
    c: Coincident(g81,g82)
    c: Coincident(g82,g83)
    c: Coincident(g83,g84)
    c: Coincident(g84,g81)
    c: Horizontal(g81)
    c: Horizontal(g83)
    c: Vertical(g82)
    c: Vertical(g84)
    c: Coincident(g85,g86)
    c: Coincident(g86,g87)
    c: Coincident(g87,g88)
    c: Coincident(g88,g85)
    c: Horizontal(g85)
    c: Horizontal(g87)
    c: Vertical(g86)
    c: Vertical(g88)
    c: Equal(g84,g88) = 2
    c: Equal(g83,g87) = 0.2
    c: Coincident(g89,g90)
    c: Coincident(g90,g91)
    c: Coincident(g91,g92)
    c: Coincident(g92,g89)
    c: Horizontal(g89)
    c: Horizontal(g91)
    c: Vertical(g90)
    c: Vertical(g92)
    c: Equal(g88,g92) = 2
    c: Equal(g87,g91) = 0.2
    c: DistanceX(g89,g85) = 2
    c: Coincident(g93,g94)
    c: Coincident(g94,g95)
    c: Coincident(g95,g96)
    c: Coincident(g96,g93)
    c: Horizontal(g93)
    c: Horizontal(g95)
    c: Vertical(g94)
    c: Vertical(g96)
    c: Equal(g91,g95)
    c: Equal(g90,g94)
    c: Horizontal(g81,g85)
    c: Horizontal(g85,g89)
    c: Horizontal(g89,g93)
    c: PointOnObject(g49,g-1)
    c: PointOnObject(g65,g-1)
    c: DistanceX(g53,g49) = 2
    c: DistanceX(g69,g65) = 2
    c: PointOnObject(g81,g-1)
    c: DistanceX(g37,g33) = 2
    c: DistanceX(g21,g17) = 2
    c: DistanceX(g5,g1) = 2
    c: Coincident(g97,g98)
    c: Coincident(g98,g99)
    c: Coincident(g99,g100)
    c: Coincident(g100,g97)
    c: Horizontal(g97)
    c: Horizontal(g99)
    c: Vertical(g98)
    c: Vertical(g100)
    c: Equal(g4,g100) = 2
    c: Equal(g3,g99) = 0.2
    c: Coincident(g101,g102)
    c: Coincident(g102,g103)
    c: Coincident(g103,g104)
    c: Coincident(g104,g101)
    c: Horizontal(g101)
    c: Horizontal(g103)
    c: Vertical(g102)
    c: Vertical(g104)
    c: Equal(g100,g104) = 2
    c: Equal(g99,g103) = 0.2
    c: Coincident(g105,g106)
    c: Coincident(g106,g107)
    c: Coincident(g107,g108)
    c: Coincident(g108,g105)
    c: Horizontal(g105)
    c: Horizontal(g107)
    c: Vertical(g106)
    c: Vertical(g108)
    c: Equal(g104,g108) = 2
    c: Equal(g103,g107) = 0.2
    c: DistanceX(g105,g101) = 2
    c: Coincident(g109,g110)
    c: Coincident(g110,g111)
    c: Coincident(g111,g112)
    c: Coincident(g112,g109)
    c: Horizontal(g109)
    c: Horizontal(g111)
    c: Vertical(g110)
    c: Vertical(g112)
    c: Equal(g107,g111)
    c: Equal(g106,g110)
    c: Horizontal(g97,g101)
    c: Horizontal(g101,g105)
    c: Horizontal(g105,g109)
    c: Coincident(g113,g114)
    c: Coincident(g114,g115)
    c: Coincident(g115,g116)
    c: Coincident(g116,g113)
    c: Horizontal(g113)
    c: Horizontal(g115)
    c: Vertical(g114)
    c: Vertical(g116)
    c: Equal(g100,g116) = 2
    c: Equal(g99,g115) = 0.2
    c: Coincident(g117,g118)
    c: Coincident(g118,g119)
    c: Coincident(g119,g120)
    c: Coincident(g120,g117)
    c: Horizontal(g117)
    c: Horizontal(g119)
    c: Vertical(g118)
    c: Vertical(g120)
    c: Equal(g116,g120) = 2
    c: Equal(g115,g119) = 0.2
    c: Coincident(g121,g122)
    c: Coincident(g122,g123)
    c: Coincident(g123,g124)
    c: Coincident(g124,g121)
    c: Horizontal(g121)
    c: Horizontal(g123)
    c: Vertical(g122)
    c: Vertical(g124)
    c: Equal(g120,g124) = 2
    c: Equal(g119,g123) = 0.2
    c: DistanceX(g121,g117) = 2
    c: Coincident(g125,g126)
    c: Coincident(g126,g127)
    c: Coincident(g127,g128)
    c: Coincident(g128,g125)
    c: Horizontal(g125)
    c: Horizontal(g127)
    c: Vertical(g126)
    c: Vertical(g128)
    c: Equal(g123,g127)
    c: Equal(g122,g126)
    c: Horizontal(g113,g117)
    c: Horizontal(g117,g121)
    c: Horizontal(g121,g125)
    c: Coincident(g129,g130)
    c: Coincident(g130,g131)
    c: Coincident(g131,g132)
    c: Coincident(g132,g129)
    c: Horizontal(g129)
    c: Horizontal(g131)
    c: Vertical(g130)
    c: Vertical(g132)
    c: Coincident(g133,g134)
    c: Coincident(g134,g135)
    c: Coincident(g135,g136)
    c: Coincident(g136,g133)
    c: Horizontal(g133)
    c: Horizontal(g135)
    c: Vertical(g134)
    c: Vertical(g136)
    c: Equal(g132,g136) = 2
    c: Equal(g131,g135) = 0.2
    c: Coincident(g137,g138)
    c: Coincident(g138,g139)
    c: Coincident(g139,g140)
    c: Coincident(g140,g137)
    c: Horizontal(g137)
    c: Horizontal(g139)
    c: Vertical(g138)
    c: Vertical(g140)
    c: Equal(g136,g140) = 2
    c: Equal(g135,g139) = 0.2
    c: DistanceX(g137,g133) = 2
    c: Coincident(g141,g142)
    c: Coincident(g142,g143)
    c: Coincident(g143,g144)
    c: Coincident(g144,g141)
    c: Horizontal(g141)
    c: Horizontal(g143)
    c: Vertical(g142)
    c: Vertical(g144)
    c: Equal(g139,g143)
    c: Equal(g138,g142)
    c: Horizontal(g129,g133)
    c: Horizontal(g133,g137)
    c: Horizontal(g137,g141)
    c: Coincident(g145,g146)
    c: Coincident(g146,g147)
    c: Coincident(g147,g148)
    c: Coincident(g148,g145)
    c: Horizontal(g145)
    c: Horizontal(g147)
    c: Vertical(g146)
    c: Vertical(g148)
    c: Equal(g100,g148) = 2
    c: Equal(g99,g147) = 0.2
    c: Coincident(g149,g150)
    c: Coincident(g150,g151)
    c: Coincident(g151,g152)
    c: Coincident(g152,g149)
    c: Horizontal(g149)
    c: Horizontal(g151)
    c: Vertical(g150)
    c: Vertical(g152)
    c: Equal(g148,g152) = 2
    c: Equal(g147,g151) = 0.2
    c: Coincident(g153,g154)
    c: Coincident(g154,g155)
    c: Coincident(g155,g156)
    c: Coincident(g156,g153)
    c: Horizontal(g153)
    c: Horizontal(g155)
    c: Vertical(g154)
    c: Vertical(g156)
    c: Equal(g152,g156) = 2
    c: Equal(g151,g155) = 0.2
    c: DistanceX(g153,g149) = 2
    c: Coincident(g157,g158)
    c: Coincident(g158,g159)
    c: Coincident(g159,g160)
    c: Coincident(g160,g157)
    c: Horizontal(g157)
    c: Horizontal(g159)
    c: Vertical(g158)
    c: Vertical(g160)
    c: Equal(g155,g159)
    c: Equal(g154,g158)
    c: Horizontal(g145,g149)
    c: Horizontal(g149,g153)
    c: Horizontal(g153,g157)
    c: Coincident(g161,g162)
    c: Coincident(g162,g163)
    c: Coincident(g163,g164)
    c: Coincident(g164,g161)
    c: Horizontal(g161)
    c: Horizontal(g163)
    c: Vertical(g162)
    c: Vertical(g164)
    c: Equal(g148,g164) = 2
    c: Equal(g147,g163) = 0.2
    c: Coincident(g165,g166)
    c: Coincident(g166,g167)
    c: Coincident(g167,g168)
    c: Coincident(g168,g165)
    c: Horizontal(g165)
    c: Horizontal(g167)
    c: Vertical(g166)
    c: Vertical(g168)
    c: Equal(g164,g168) = 2
    c: Equal(g163,g167) = 0.2
    c: Coincident(g169,g170)
    c: Coincident(g170,g171)
    c: Coincident(g171,g172)
    c: Coincident(g172,g169)
    c: Horizontal(g169)
    c: Horizontal(g171)
    c: Vertical(g170)
    c: Vertical(g172)
    c: Equal(g168,g172) = 2
    c: Equal(g167,g171) = 0.2
    c: DistanceX(g169,g165) = 2
    c: Coincident(g173,g174)
    c: Coincident(g174,g175)
    c: Coincident(g175,g176)
    c: Coincident(g176,g173)
    c: Horizontal(g173)
    c: Horizontal(g175)
    c: Vertical(g174)
    c: Vertical(g176)
    c: Equal(g171,g175)
    c: Equal(g170,g174)
    c: Horizontal(g161,g165)
    c: Horizontal(g165,g169)
    c: Horizontal(g169,g173)
    c: Coincident(g177,g178)
    c: Coincident(g178,g179)
    c: Coincident(g179,g180)
    c: Coincident(g180,g177)
    c: Horizontal(g177)
    c: Horizontal(g179)
    c: Vertical(g178)
    c: Vertical(g180)
    c: Coincident(g181,g182)
    c: Coincident(g182,g183)
    c: Coincident(g183,g184)
    c: Coincident(g184,g181)
    c: Horizontal(g181)
    c: Horizontal(g183)
    c: Vertical(g182)
    c: Vertical(g184)
    c: Equal(g180,g184) = 2
    c: Equal(g179,g183) = 0.2
    c: Coincident(g185,g186)
    c: Coincident(g186,g187)
    c: Coincident(g187,g188)
    c: Coincident(g188,g185)
    c: Horizontal(g185)
    c: Horizontal(g187)
    c: Vertical(g186)
    c: Vertical(g188)
    c: Equal(g184,g188) = 2
    c: Equal(g183,g187) = 0.2
    c: DistanceX(g185,g181) = 2
    c: Coincident(g189,g190)
    c: Coincident(g190,g191)
    c: Coincident(g191,g192)
    c: Coincident(g192,g189)
    c: Horizontal(g189)
    c: Horizontal(g191)
    c: Vertical(g190)
    c: Vertical(g192)
    c: Equal(g187,g191)
    c: Equal(g186,g190)
    c: Horizontal(g177,g181)
    c: Horizontal(g181,g185)
    c: Horizontal(g185,g189)
    c: DistanceX(g149,g145) = 2
    c: DistanceX(g165,g161) = 2
    c: DistanceX(g133,g129) = 2
    c: DistanceX(g117,g113) = 2
    c: DistanceX(g17,g13) = 4
    c: DistanceX(g13,g9) = 2
    c: DistanceX(g33,g29) = 4
    c: DistanceX(g49,g45) = 4
    c: DistanceX(g45,g41) = 2
    c: DistanceX(g61,g57) = 2
    c: DistanceX(g65,g61) = 4
    c: DistanceX(g77,g73) = 2
    c: DistanceX(g85,g81) = 2
    c: DistanceX(g81,g77) = 4
    c: DistanceX(g93,g89) = 2
    c: PointOnObject(g97,g-1)
    c: DistanceX(g97,g93) = 4
    c: DistanceX(g101,g97) = 2
    c: DistanceX(g109,g105) = 2
    c: DistanceX(g113,g109) = 4
    c: PointOnObject(g113,g-1)
    c: PointOnObject(g129,g-1)
    c: DistanceX(g125,g121) = 2
    c: DistanceX(g129,g125) = 4
    c: PointOnObject(g145,g-1)
    c: DistanceX(g141,g137) = 2
    c: DistanceX(g145,g141) = 4
    c: PointOnObject(g161,g-1)
    c: DistanceX(g157,g153) = 2
    c: DistanceX(g161,g157) = 4
    c: PointOnObject(g177,g-1)
    c: DistanceX(g173,g169) = 2
    c: DistanceX(g177,g173) = 4
    c: DistanceX(g181,g177) = 2
    c: DistanceX(g29,g25) = 2
    c: DistanceX(g189,g185) = 2
    c: Equal(g31,g35)
    c: Equal(g30,g36)
    c: Equal(g79,g83)
    c: Equal(g78,g84)
    c: Equal(g126,g132)
    c: Equal(g127,g131)
    c: Equal(g175,g179)
    c: Equal(g174,g180)
    c: Coincident(g193,g194)
    c: Coincident(g194,g195)
    c: Coincident(g195,g196)
    c: Coincident(g196,g193)
    c: Horizontal(g193)
    c: Horizontal(g195)
    c: Vertical(g194)
    c: Vertical(g196)
    c: Coincident(g197,g198)
    c: Coincident(g198,g199)
    c: Coincident(g199,g200)
    c: Coincident(g200,g197)
    c: Horizontal(g197)
    c: Horizontal(g199)
    c: Vertical(g198)
    c: Vertical(g200)
    c: Equal(g196,g200) = 2
    c: Equal(g195,g199) = 0.2
    c: Coincident(g201,g202)
    c: Coincident(g202,g203)
    c: Coincident(g203,g204)
    c: Coincident(g204,g201)
    c: Horizontal(g201)
    c: Horizontal(g203)
    c: Vertical(g202)
    c: Vertical(g204)
    c: Equal(g200,g204) = 2
    c: Equal(g199,g203) = 0.2
    c: DistanceX(g201,g197) = 2
    c: Coincident(g205,g206)
    c: Coincident(g206,g207)
    c: Coincident(g207,g208)
    c: Coincident(g208,g205)
    c: Horizontal(g205)
    c: Horizontal(g207)
    c: Vertical(g206)
    c: Vertical(g208)
    c: Equal(g203,g207)
    c: Equal(g202,g206)
    c: Horizontal(g193,g197)
    c: Horizontal(g197,g201)
    c: Horizontal(g201,g205)
    c: DistanceX(g197,g193) = 2
    c: DistanceX(g205,g201) = 2
    c: Equal(g191,g195)
    c: Equal(g192,g196)
    c: DistanceX(g193,g189) = 4
    c: Horizontal(g193,g189)
    c: Coincident(g209,g210)
    c: Coincident(g210,g211)
    c: Coincident(g211,g212)
    c: Coincident(g212,g209)
    c: Horizontal(g209)
    c: Horizontal(g211)
    c: Vertical(g210)
    c: Vertical(g212)
    c: Coincident(g213,g214)
    c: Coincident(g214,g215)
    c: Coincident(g215,g216)
    c: Coincident(g216,g213)
    c: Horizontal(g213)
    c: Horizontal(g215)
    c: Vertical(g214)
    c: Vertical(g216)
    c: Equal(g212,g216) = 2
    c: Equal(g211,g215) = 0.2
    c: Coincident(g217,g218)
    c: Coincident(g218,g219)
    c: Coincident(g219,g220)
    c: Coincident(g220,g217)
    c: Horizontal(g217)
    c: Horizontal(g219)
    c: Vertical(g218)
    c: Vertical(g220)
    c: Equal(g216,g220) = 2
    c: Equal(g215,g219) = 0.2
    c: DistanceX(g217,g213) = 2
    c: Coincident(g221,g222)
    c: Coincident(g222,g223)
    c: Coincident(g223,g224)
    c: Coincident(g224,g221)
    c: Horizontal(g221)
    c: Horizontal(g223)
    c: Vertical(g222)
    c: Vertical(g224)
    c: Equal(g219,g223)
    c: Equal(g218,g222)
    c: Horizontal(g209,g213)
    c: Horizontal(g213,g217)
    c: Horizontal(g217,g221)
    c: Coincident(g225,g226)
    c: Coincident(g226,g227)
    c: Coincident(g227,g228)
    c: Coincident(g228,g225)
    c: Horizontal(g225)
    c: Horizontal(g227)
    c: Vertical(g226)
    c: Vertical(g228)
    c: Coincident(g229,g230)
    c: Coincident(g230,g231)
    c: Coincident(g231,g232)
    c: Coincident(g232,g229)
    c: Horizontal(g229)
    c: Horizontal(g231)
    c: Vertical(g230)
    c: Vertical(g232)
    c: Equal(g228,g232) = 2
    c: Equal(g227,g231) = 0.2
    c: Coincident(g233,g234)
    c: Coincident(g234,g235)
    c: Coincident(g235,g236)
    c: Coincident(g236,g233)
    c: Horizontal(g233)
    c: Horizontal(g235)
    c: Vertical(g234)
    c: Vertical(g236)
    c: Equal(g232,g236) = 2
    c: Equal(g231,g235) = 0.2
    c: DistanceX(g233,g229) = 2
    c: Coincident(g237,g238)
    c: Coincident(g238,g239)
    c: Coincident(g239,g240)
    c: Coincident(g240,g237)
    c: Horizontal(g237)
    c: Horizontal(g239)
    c: Vertical(g238)
    c: Vertical(g240)
    c: Equal(g235,g239)
    c: Equal(g234,g238)
    c: Horizontal(g225,g229)
    c: Horizontal(g229,g233)
    c: Horizontal(g233,g237)
    c: DistanceX(g213,g209) = 2
    c: DistanceX(g221,g217) = 2
    c: DistanceX(g225,g221) = 4
    c: DistanceX(g229,g225) = 2
    c: DistanceX(g237,g233) = 2
    c: Equal(g223,g227)
    c: Equal(g222,g228)
    c: Coincident(g241,g242)
    c: Coincident(g242,g243)
    c: Coincident(g243,g244)
    c: Coincident(g244,g241)
    c: Horizontal(g241)
    c: Horizontal(g243)
    c: Vertical(g242)
    c: Vertical(g244)
    c: Coincident(g245,g246)
    c: Coincident(g246,g247)
    c: Coincident(g247,g248)
    c: Coincident(g248,g245)
    c: Horizontal(g245)
    c: Horizontal(g247)
    c: Vertical(g246)
    c: Vertical(g248)
    c: Equal(g244,g248) = 2
    c: Equal(g243,g247) = 0.2
    c: Coincident(g249,g250)
    c: Coincident(g250,g251)
    c: Coincident(g251,g252)
    c: Coincident(g252,g249)
    c: Horizontal(g249)
    c: Horizontal(g251)
    c: Vertical(g250)
    c: Vertical(g252)
    c: Equal(g248,g252) = 2
    c: Equal(g247,g251) = 0.2
    c: DistanceX(g249,g245) = 2
    c: Coincident(g253,g254)
    c: Coincident(g254,g255)
    c: Coincident(g255,g256)
    c: Coincident(g256,g253)
    c: Horizontal(g253)
    c: Horizontal(g255)
    c: Vertical(g254)
    c: Vertical(g256)
    c: Equal(g251,g255)
    c: Equal(g250,g254)
    c: Horizontal(g241,g245)
    c: Horizontal(g245,g249)
    c: Horizontal(g249,g253)
    c: DistanceX(g245,g241) = 2
    c: DistanceX(g253,g249) = 2
    c: Equal(g239,g243)
    c: Equal(g240,g244)
    c: DistanceX(g241,g237) = 4
    c: Horizontal(g241,g237)
    c: Horizontal(g221,g225)
    c: Equal(g208,g210)
    c: Equal(g207,g211)
    c: Horizontal(g209,g205)
    c: DistanceX(g209,g205) = 4
    c: DistanceX(g-1,g254) = 81.8
    c: Coincident(g257,g258)
    c: Coincident(g258,g259)
    c: Coincident(g259,g260)
    c: Coincident(g260,g257)
    c: Horizontal(g257)
    c: Horizontal(g259)
    c: Vertical(g258)
    c: Vertical(g260)
    c: Equal(g4,g260) = 2
    c: Equal(g3,g259) = 0.2
    c: Coincident(g261,g262)
    c: Coincident(g262,g263)
    c: Coincident(g263,g264)
    c: Coincident(g264,g261)
    c: Horizontal(g261)
    c: Horizontal(g263)
    c: Vertical(g262)
    c: Vertical(g264)
    c: Equal(g260,g264) = 2
    c: Equal(g259,g263) = 0.2
    c: Coincident(g265,g266)
    c: Coincident(g266,g267)
    c: Coincident(g267,g268)
    c: Coincident(g268,g265)
    c: Horizontal(g265)
    c: Horizontal(g267)
    c: Vertical(g266)
    c: Vertical(g268)
    c: Equal(g264,g268) = 2
    c: Equal(g263,g267) = 0.2
    c: DistanceX(g265,g261) = 2
    c: Coincident(g269,g270)
    c: Coincident(g270,g271)
    c: Coincident(g271,g272)
    c: Coincident(g272,g269)
    c: Horizontal(g269)
    c: Horizontal(g271)
    c: Vertical(g270)
    c: Vertical(g272)
    c: Equal(g267,g271)
    c: Equal(g266,g270)
    c: Horizontal(g257,g261)
    c: Horizontal(g261,g265)
    c: Horizontal(g265,g269)
    c: Coincident(g273,g274)
    c: Coincident(g274,g275)
    c: Coincident(g275,g276)
    c: Coincident(g276,g273)
    c: Horizontal(g273)
    c: Horizontal(g275)
    c: Vertical(g274)
    c: Vertical(g276)
    c: Equal(g260,g276) = 2
    c: Equal(g259,g275) = 0.2
    c: Coincident(g277,g278)
    c: Coincident(g278,g279)
    c: Coincident(g279,g280)
    c: Coincident(g280,g277)
    c: Horizontal(g277)
    c: Horizontal(g279)
    c: Vertical(g278)
    c: Vertical(g280)
    c: Equal(g276,g280) = 2
    c: Equal(g275,g279) = 0.2
    c: Coincident(g281,g282)
    c: Coincident(g282,g283)
    c: Coincident(g283,g284)
    c: Coincident(g284,g281)
    c: Horizontal(g281)
    c: Horizontal(g283)
    c: Vertical(g282)
    c: Vertical(g284)
    c: Equal(g280,g284) = 2
    c: Equal(g279,g283) = 0.2
    c: DistanceX(g281,g277) = 2
    c: Coincident(g285,g286)
    c: Coincident(g286,g287)
    c: Coincident(g287,g288)
    c: Coincident(g288,g285)
    c: Horizontal(g285)
    c: Horizontal(g287)
    c: Vertical(g286)
    c: Vertical(g288)
    c: Equal(g283,g287)
    c: Equal(g282,g286)
    c: Horizontal(g273,g277)
    c: Horizontal(g277,g281)
    c: Horizontal(g281,g285)
    c: Coincident(g289,g290)
    c: Coincident(g290,g291)
    c: Coincident(g291,g292)
    c: Coincident(g292,g289)
    c: Horizontal(g289)
    c: Horizontal(g291)
    c: Vertical(g290)
    c: Vertical(g292)
    c: Coincident(g293,g294)
    c: Coincident(g294,g295)
    c: Coincident(g295,g296)
    c: Coincident(g296,g293)
    c: Horizontal(g293)
    c: Horizontal(g295)
    c: Vertical(g294)
    c: Vertical(g296)
    c: Equal(g292,g296) = 2
    c: Equal(g291,g295) = 0.2
    c: Coincident(g297,g298)
    c: Coincident(g298,g299)
    c: Coincident(g299,g300)
    c: Coincident(g300,g297)
    c: Horizontal(g297)
    c: Horizontal(g299)
    c: Vertical(g298)
    c: Vertical(g300)
    c: Equal(g296,g300) = 2
    c: Equal(g295,g299) = 0.2
    c: DistanceX(g297,g293) = 2
    c: Coincident(g301,g302)
    c: Coincident(g302,g303)
    c: Coincident(g303,g304)
    c: Coincident(g304,g301)
    c: Horizontal(g301)
    c: Horizontal(g303)
    c: Vertical(g302)
    c: Vertical(g304)
    c: Equal(g299,g303)
    c: Equal(g298,g302)
    c: Horizontal(g289,g293)
    c: Horizontal(g293,g297)
    c: Horizontal(g297,g301)
    c: Coincident(g305,g306)
    c: Coincident(g306,g307)
    c: Coincident(g307,g308)
    c: Coincident(g308,g305)
    c: Horizontal(g305)
    c: Horizontal(g307)
    c: Vertical(g306)
    c: Vertical(g308)
    c: Equal(g260,g308) = 2
    c: Equal(g259,g307) = 0.2
    c: Coincident(g309,g310)
    c: Coincident(g310,g311)
    c: Coincident(g311,g312)
    c: Coincident(g312,g309)
    c: Horizontal(g309)
    c: Horizontal(g311)
    c: Vertical(g310)
    c: Vertical(g312)
    c: Equal(g308,g312) = 2
    c: Equal(g307,g311) = 0.2
    c: Coincident(g313,g314)
    c: Coincident(g314,g315)
    c: Coincident(g315,g316)
    c: Coincident(g316,g313)
    c: Horizontal(g313)
    c: Horizontal(g315)
    c: Vertical(g314)
    c: Vertical(g316)
    c: Equal(g312,g316) = 2
    c: Equal(g311,g315) = 0.2
    c: DistanceX(g313,g309) = 2
    c: Coincident(g317,g318)
    c: Coincident(g318,g319)
    c: Coincident(g319,g320)
    c: Coincident(g320,g317)
    c: Horizontal(g317)
    c: Horizontal(g319)
    c: Vertical(g318)
    c: Vertical(g320)
    c: Equal(g315,g319)
    c: Equal(g314,g318)
    c: Horizontal(g305,g309)
    c: Horizontal(g309,g313)
    c: Horizontal(g313,g317)
    c: Coincident(g321,g322)
    c: Coincident(g322,g323)
    c: Coincident(g323,g324)
    c: Coincident(g324,g321)
    c: Horizontal(g321)
    c: Horizontal(g323)
    c: Vertical(g322)
    c: Vertical(g324)
    c: Equal(g308,g324) = 2
    c: Equal(g307,g323) = 0.2
    c: Coincident(g325,g326)
    c: Coincident(g326,g327)
    c: Coincident(g327,g328)
    c: Coincident(g328,g325)
    c: Horizontal(g325)
    c: Horizontal(g327)
    c: Vertical(g326)
    c: Vertical(g328)
    c: Equal(g324,g328) = 2
    c: Equal(g323,g327) = 0.2
    c: Coincident(g329,g330)
    c: Coincident(g330,g331)
    c: Coincident(g331,g332)
    c: Coincident(g332,g329)
    c: Horizontal(g329)
    c: Horizontal(g331)
    c: Vertical(g330)
    c: Vertical(g332)
    c: Equal(g328,g332) = 2
    c: Equal(g327,g331) = 0.2
    c: DistanceX(g329,g325) = 2
    c: Coincident(g333,g334)
    c: Coincident(g334,g335)
    c: Coincident(g335,g336)
    c: Coincident(g336,g333)
    c: Horizontal(g333)
    c: Horizontal(g335)
    c: Vertical(g334)
    c: Vertical(g336)
    c: Equal(g331,g335)
    c: Equal(g330,g334)
    c: Horizontal(g321,g325)
    c: Horizontal(g325,g329)
    c: Horizontal(g329,g333)
    c: Coincident(g337,g338)
    c: Coincident(g338,g339)
    c: Coincident(g339,g340)
    c: Coincident(g340,g337)
    c: Horizontal(g337)
    c: Horizontal(g339)
    c: Vertical(g338)
    c: Vertical(g340)
    c: Coincident(g341,g342)
    c: Coincident(g342,g343)
    c: Coincident(g343,g344)
    c: Coincident(g344,g341)
    c: Horizontal(g341)
    c: Horizontal(g343)
    c: Vertical(g342)
    c: Vertical(g344)
    c: Equal(g340,g344) = 2
    c: Equal(g339,g343) = 0.2
    c: Coincident(g345,g346)
    c: Coincident(g346,g347)
    c: Coincident(g347,g348)
    c: Coincident(g348,g345)
    c: Horizontal(g345)
    c: Horizontal(g347)
    c: Vertical(g346)
    c: Vertical(g348)
    c: Equal(g344,g348) = 2
    c: Equal(g343,g347) = 0.2
    c: DistanceX(g345,g341) = 2
    c: Coincident(g349,g350)
    c: Coincident(g350,g351)
    c: Coincident(g351,g352)
    c: Coincident(g352,g349)
    c: Horizontal(g349)
    c: Horizontal(g351)
    c: Vertical(g350)
    c: Vertical(g352)
    c: Equal(g347,g351)
    c: Equal(g346,g350)
    c: Horizontal(g337,g341)
    c: Horizontal(g341,g345)
    c: Horizontal(g345,g349)
    c: DistanceX(g309,g305) = 2
    c: DistanceX(g325,g321) = 2
    c: DistanceX(g293,g289) = 2
    c: DistanceX(g277,g273) = 2
    c: DistanceX(g261,g257) = 2
    c: Coincident(g353,g354)
    c: Coincident(g354,g355)
    c: Coincident(g355,g356)
    c: Coincident(g356,g353)
    c: Horizontal(g353)
    c: Horizontal(g355)
    c: Vertical(g354)
    c: Vertical(g356)
    c: Equal(g260,g356) = 2
    c: Equal(g259,g355) = 0.2
    c: Coincident(g357,g358)
    c: Coincident(g358,g359)
    c: Coincident(g359,g360)
    c: Coincident(g360,g357)
    c: Horizontal(g357)
    c: Horizontal(g359)
    c: Vertical(g358)
    c: Vertical(g360)
    c: Equal(g356,g360) = 2
    c: Equal(g355,g359) = 0.2
    c: Coincident(g361,g362)
    c: Coincident(g362,g363)
    c: Coincident(g363,g364)
    c: Coincident(g364,g361)
    c: Horizontal(g361)
    c: Horizontal(g363)
    c: Vertical(g362)
    c: Vertical(g364)
    c: Equal(g360,g364) = 2
    c: Equal(g359,g363) = 0.2
    c: DistanceX(g361,g357) = 2
    c: Coincident(g365,g366)
    c: Coincident(g366,g367)
    c: Coincident(g367,g368)
    c: Coincident(g368,g365)
    c: Horizontal(g365)
    c: Horizontal(g367)
    c: Vertical(g366)
    c: Vertical(g368)
    c: Equal(g363,g367)
    c: Equal(g362,g366)
    c: Horizontal(g353,g357)
    c: Horizontal(g357,g361)
    c: Horizontal(g361,g365)
    c: Coincident(g369,g370)
    c: Coincident(g370,g371)
    c: Coincident(g371,g372)
    c: Coincident(g372,g369)
    c: Horizontal(g369)
    c: Horizontal(g371)
    c: Vertical(g370)
    c: Vertical(g372)
    c: Equal(g356,g372) = 2
    c: Equal(g355,g371) = 0.2
    c: Coincident(g373,g374)
    c: Coincident(g374,g375)
    c: Coincident(g375,g376)
    c: Coincident(g376,g373)
    c: Horizontal(g373)
    c: Horizontal(g375)
    c: Vertical(g374)
    c: Vertical(g376)
    c: Equal(g372,g376) = 2
    c: Equal(g371,g375) = 0.2
    c: Coincident(g377,g378)
    c: Coincident(g378,g379)
    c: Coincident(g379,g380)
    c: Coincident(g380,g377)
    c: Horizontal(g377)
    c: Horizontal(g379)
    c: Vertical(g378)
    c: Vertical(g380)
    c: Equal(g376,g380) = 2
    c: Equal(g375,g379) = 0.2
    c: DistanceX(g377,g373) = 2
    c: Coincident(g381,g382)
    c: Coincident(g382,g383)
    c: Coincident(g383,g384)
    c: Coincident(g384,g381)
    c: Horizontal(g381)
    c: Horizontal(g383)
    c: Vertical(g382)
    c: Vertical(g384)
    c: Equal(g379,g383)
    c: Equal(g378,g382)
    c: Horizontal(g369,g373)
    c: Horizontal(g373,g377)
    c: Horizontal(g377,g381)
    c: Coincident(g385,g386)
    c: Coincident(g386,g387)
    c: Coincident(g387,g388)
    c: Coincident(g388,g385)
    c: Horizontal(g385)
    c: Horizontal(g387)
    c: Vertical(g386)
    c: Vertical(g388)
    c: Coincident(g389,g390)
    c: Coincident(g390,g391)
    c: Coincident(g391,g392)
    c: Coincident(g392,g389)
    c: Horizontal(g389)
    c: Horizontal(g391)
    c: Vertical(g390)
    c: Vertical(g392)
    c: Equal(g388,g392) = 2
    c: Equal(g387,g391) = 0.2
    c: Coincident(g393,g394)
    c: Coincident(g394,g395)
    c: Coincident(g395,g396)
    c: Coincident(g396,g393)
    c: Horizontal(g393)
    c: Horizontal(g395)
    c: Vertical(g394)
    c: Vertical(g396)
    c: Equal(g392,g396) = 2
    c: Equal(g391,g395) = 0.2
    c: DistanceX(g393,g389) = 2
    c: Coincident(g397,g398)
    c: Coincident(g398,g399)
    c: Coincident(g399,g400)
    c: Coincident(g400,g397)
    c: Horizontal(g397)
    c: Horizontal(g399)
    c: Vertical(g398)
    c: Vertical(g400)
    c: Equal(g395,g399)
    c: Equal(g394,g398)
    c: Horizontal(g385,g389)
    c: Horizontal(g389,g393)
    c: Horizontal(g393,g397)
    c: Coincident(g401,g402)
    c: Coincident(g402,g403)
    c: Coincident(g403,g404)
    c: Coincident(g404,g401)
    c: Horizontal(g401)
    c: Horizontal(g403)
    c: Vertical(g402)
    c: Vertical(g404)
    c: Equal(g356,g404) = 2
    c: Equal(g355,g403) = 0.2
    c: Coincident(g405,g406)
    c: Coincident(g406,g407)
    c: Coincident(g407,g408)
    c: Coincident(g408,g405)
    c: Horizontal(g405)
    c: Horizontal(g407)
    c: Vertical(g406)
    c: Vertical(g408)
    c: Equal(g404,g408) = 2
    c: Equal(g403,g407) = 0.2
    c: Coincident(g409,g410)
    c: Coincident(g410,g411)
    c: Coincident(g411,g412)
    c: Coincident(g412,g409)
    c: Horizontal(g409)
    c: Horizontal(g411)
    c: Vertical(g410)
    c: Vertical(g412)
    c: Equal(g408,g412) = 2
    c: Equal(g407,g411) = 0.2
    c: DistanceX(g409,g405) = 2
    c: Coincident(g413,g414)
    c: Coincident(g414,g415)
    c: Coincident(g415,g416)
    c: Coincident(g416,g413)
    c: Horizontal(g413)
    c: Horizontal(g415)
    c: Vertical(g414)
    c: Vertical(g416)
    c: Equal(g411,g415)
    c: Equal(g410,g414)
    c: Horizontal(g401,g405)
    c: Horizontal(g405,g409)
    c: Horizontal(g409,g413)
    c: Coincident(g417,g418)
    c: Coincident(g418,g419)
    c: Coincident(g419,g420)
    c: Coincident(g420,g417)
    c: Horizontal(g417)
    c: Horizontal(g419)
    c: Vertical(g418)
    c: Vertical(g420)
    c: Equal(g404,g420) = 2
    c: Equal(g403,g419) = 0.2
    c: Coincident(g421,g422)
    c: Coincident(g422,g423)
    c: Coincident(g423,g424)
    c: Coincident(g424,g421)
    c: Horizontal(g421)
    c: Horizontal(g423)
    c: Vertical(g422)
    c: Vertical(g424)
    c: Equal(g420,g424) = 2
    c: Equal(g419,g423) = 0.2
    c: Coincident(g425,g426)
    c: Coincident(g426,g427)
    c: Coincident(g427,g428)
    c: Coincident(g428,g425)
    c: Horizontal(g425)
    c: Horizontal(g427)
    c: Vertical(g426)
    c: Vertical(g428)
    c: Equal(g424,g428) = 2
    c: Equal(g423,g427) = 0.2
    c: DistanceX(g425,g421) = 2
    c: Coincident(g429,g430)
    c: Coincident(g430,g431)
    c: Coincident(g431,g432)
    c: Coincident(g432,g429)
    c: Horizontal(g429)
    c: Horizontal(g431)
    c: Vertical(g430)
    c: Vertical(g432)
    c: Equal(g427,g431)
    c: Equal(g426,g430)
    c: Horizontal(g417,g421)
    c: Horizontal(g421,g425)
    c: Horizontal(g425,g429)
    c: Coincident(g433,g434)
    c: Coincident(g434,g435)
    c: Coincident(g435,g436)
    c: Coincident(g436,g433)
    c: Horizontal(g433)
    c: Horizontal(g435)
    c: Vertical(g434)
    c: Vertical(g436)
    c: Coincident(g437,g438)
    c: Coincident(g438,g439)
    c: Coincident(g439,g440)
    c: Coincident(g440,g437)
    c: Horizontal(g437)
    c: Horizontal(g439)
    c: Vertical(g438)
    c: Vertical(g440)
    c: Equal(g436,g440) = 2
    c: Equal(g435,g439) = 0.2
    c: Coincident(g441,g442)
    c: Coincident(g442,g443)
    c: Coincident(g443,g444)
    c: Coincident(g444,g441)
    c: Horizontal(g441)
    c: Horizontal(g443)
    c: Vertical(g442)
    c: Vertical(g444)
    c: Equal(g440,g444) = 2
    c: Equal(g439,g443) = 0.2
    c: DistanceX(g441,g437) = 2
    c: Coincident(g445,g446)
    c: Coincident(g446,g447)
    c: Coincident(g447,g448)
    c: Coincident(g448,g445)
    c: Horizontal(g445)
    c: Horizontal(g447)
    c: Vertical(g446)
    c: Vertical(g448)
    c: Equal(g443,g447)
    c: Equal(g442,g446)
    c: Horizontal(g433,g437)
    c: Horizontal(g437,g441)
    c: Horizontal(g441,g445)
    c: DistanceX(g405,g401) = 2
    c: DistanceX(g421,g417) = 2
    c: DistanceX(g389,g385) = 2
    c: DistanceX(g373,g369) = 2
    c: DistanceX(g273,g269) = 4
    c: DistanceX(g269,g265) = 2
    c: DistanceX(g289,g285) = 4
    c: DistanceX(g305,g301) = 4
    c: DistanceX(g301,g297) = 2
    c: DistanceX(g317,g313) = 2
    c: DistanceX(g321,g317) = 4
    c: DistanceX(g333,g329) = 2
    c: DistanceX(g341,g337) = 2
    c: DistanceX(g337,g333) = 4
    c: DistanceX(g349,g345) = 2
    c: DistanceX(g353,g349) = 4
    c: DistanceX(g357,g353) = 2
    c: DistanceX(g365,g361) = 2
    c: DistanceX(g369,g365) = 4
    c: DistanceX(g381,g377) = 2
    c: DistanceX(g385,g381) = 4
    c: DistanceX(g397,g393) = 2
    c: DistanceX(g401,g397) = 4
    c: DistanceX(g413,g409) = 2
    c: DistanceX(g417,g413) = 4
    c: DistanceX(g429,g425) = 2
    c: DistanceX(g433,g429) = 4
    c: DistanceX(g437,g433) = 2
    c: DistanceX(g285,g281) = 2
    c: DistanceX(g445,g441) = 2
    c: Equal(g287,g291)
    c: Equal(g286,g292)
    c: Equal(g335,g339)
    c: Equal(g334,g340)
    c: Equal(g382,g388)
    c: Equal(g383,g387)
    c: Equal(g431,g435)
    c: Equal(g430,g436)
    c: Coincident(g449,g450)
    c: Coincident(g450,g451)
    c: Coincident(g451,g452)
    c: Coincident(g452,g449)
    c: Horizontal(g449)
    c: Horizontal(g451)
    c: Vertical(g450)
    c: Vertical(g452)
    c: Coincident(g453,g454)
    c: Coincident(g454,g455)
    c: Coincident(g455,g456)
    c: Coincident(g456,g453)
    c: Horizontal(g453)
    c: Horizontal(g455)
    c: Vertical(g454)
    c: Vertical(g456)
    c: Equal(g452,g456) = 2
    c: Equal(g451,g455) = 0.2
    c: Coincident(g457,g458)
    c: Coincident(g458,g459)
    c: Coincident(g459,g460)
    c: Coincident(g460,g457)
    c: Horizontal(g457)
    c: Horizontal(g459)
    c: Vertical(g458)
    c: Vertical(g460)
    c: Equal(g456,g460) = 2
    c: Equal(g455,g459) = 0.2
    c: DistanceX(g457,g453) = 2
    c: Coincident(g461,g462)
    c: Coincident(g462,g463)
    c: Coincident(g463,g464)
    c: Coincident(g464,g461)
    c: Horizontal(g461)
    c: Horizontal(g463)
    c: Vertical(g462)
    c: Vertical(g464)
    c: Equal(g459,g463)
    c: Equal(g458,g462)
    c: Horizontal(g449,g453)
    c: Horizontal(g453,g457)
    c: Horizontal(g457,g461)
    c: DistanceX(g453,g449) = 2
    c: DistanceX(g461,g457) = 2
    c: Equal(g447,g451)
    c: Equal(g448,g452)
    c: DistanceX(g449,g445) = 4
    c: Horizontal(g449,g445)
    c: Coincident(g465,g466)
    c: Coincident(g466,g467)
    c: Coincident(g467,g468)
    c: Coincident(g468,g465)
    c: Horizontal(g465)
    c: Horizontal(g467)
    c: Vertical(g466)
    c: Vertical(g468)
    c: Coincident(g469,g470)
    c: Coincident(g470,g471)
    c: Coincident(g471,g472)
    c: Coincident(g472,g469)
    c: Horizontal(g469)
    c: Horizontal(g471)
    c: Vertical(g470)
    c: Vertical(g472)
    c: Equal(g468,g472) = 2
    c: Equal(g467,g471) = 0.2
    c: Coincident(g473,g474)
    c: Coincident(g474,g475)
    c: Coincident(g475,g476)
    c: Coincident(g476,g473)
    c: Horizontal(g473)
    c: Horizontal(g475)
    c: Vertical(g474)
    c: Vertical(g476)
    c: Equal(g472,g476) = 2
    c: Equal(g471,g475) = 0.2
    c: DistanceX(g473,g469) = 2
    c: Coincident(g477,g478)
    c: Coincident(g478,g479)
    c: Coincident(g479,g480)
    c: Coincident(g480,g477)
    c: Horizontal(g477)
    c: Horizontal(g479)
    c: Vertical(g478)
    c: Vertical(g480)
    c: Equal(g475,g479)
    c: Equal(g474,g478)
    c: Horizontal(g465,g469)
    c: Horizontal(g469,g473)
    c: Horizontal(g473,g477)
    c: Coincident(g481,g482)
    c: Coincident(g482,g483)
    c: Coincident(g483,g484)
    c: Coincident(g484,g481)
    c: Horizontal(g481)
    c: Horizontal(g483)
    c: Vertical(g482)
    c: Vertical(g484)
    c: Coincident(g485,g486)
    c: Coincident(g486,g487)
    c: Coincident(g487,g488)
    c: Coincident(g488,g485)
    c: Horizontal(g485)
    c: Horizontal(g487)
    c: Vertical(g486)
    c: Vertical(g488)
    c: Equal(g484,g488) = 2
    c: Equal(g483,g487) = 0.2
    c: Coincident(g489,g490)
    c: Coincident(g490,g491)
    c: Coincident(g491,g492)
    c: Coincident(g492,g489)
    c: Horizontal(g489)
    c: Horizontal(g491)
    c: Vertical(g490)
    c: Vertical(g492)
    c: Equal(g488,g492) = 2
    c: Equal(g487,g491) = 0.2
    c: DistanceX(g489,g485) = 2
    c: Coincident(g493,g494)
    c: Coincident(g494,g495)
    c: Coincident(g495,g496)
    c: Coincident(g496,g493)
    c: Horizontal(g493)
    c: Horizontal(g495)
    c: Vertical(g494)
    c: Vertical(g496)
    c: Equal(g491,g495)
    c: Equal(g490,g494)
    c: Horizontal(g481,g485)
    c: Horizontal(g485,g489)
    c: Horizontal(g489,g493)
    c: DistanceX(g469,g465) = 2
    c: DistanceX(g477,g473) = 2
    c: DistanceX(g481,g477) = 4
    c: DistanceX(g485,g481) = 2
    c: DistanceX(g493,g489) = 2
    c: Equal(g479,g483)
    c: Equal(g478,g484)
    c: Coincident(g497,g498)
    c: Coincident(g498,g499)
    c: Coincident(g499,g500)
    c: Coincident(g500,g497)
    c: Horizontal(g497)
    c: Horizontal(g499)
    c: Vertical(g498)
    c: Vertical(g500)
    c: Coincident(g501,g502)
    c: Coincident(g502,g503)
    c: Coincident(g503,g504)
    c: Coincident(g504,g501)
    c: Horizontal(g501)
    c: Horizontal(g503)
    c: Vertical(g502)
    c: Vertical(g504)
    c: Equal(g500,g504) = 2
    c: Equal(g499,g503) = 0.2
    c: Coincident(g505,g506)
    c: Coincident(g506,g507)
    c: Coincident(g507,g508)
    c: Coincident(g508,g505)
    c: Horizontal(g505)
    c: Horizontal(g507)
    c: Vertical(g506)
    c: Vertical(g508)
    c: Equal(g504,g508) = 2
    c: Equal(g503,g507) = 0.2
    c: DistanceX(g505,g501) = 2
    c: Coincident(g509,g510)
    c: Coincident(g510,g511)
    c: Coincident(g511,g512)
    c: Coincident(g512,g509)
    c: Horizontal(g509)
    c: Horizontal(g511)
    c: Vertical(g510)
    c: Vertical(g512)
    c: Equal(g507,g511)
    c: Equal(g506,g510)
    c: Horizontal(g497,g501)
    c: Horizontal(g501,g505)
    c: Horizontal(g505,g509)
    c: DistanceX(g501,g497) = 2
    c: DistanceX(g509,g505) = 2
    c: Equal(g495,g499)
    c: Equal(g496,g500)
    c: DistanceX(g497,g493) = 4
    c: Horizontal(g497,g493)
    c: Horizontal(g477,g481)
    c: Equal(g464,g466)
    c: Equal(g463,g467)
    c: Horizontal(g465,g461)
    c: DistanceX(g465,g461) = 4
    c: PointOnObject(g512,g0)
    c: PointOnObject(g431,g0)
    c: PointOnObject(g415,g0)
    c: PointOnObject(g399,g0)
    c: PointOnObject(g383,g0)
    c: PointOnObject(g367,g0)
    c: PointOnObject(g351,g0)
    c: PointOnObject(g335,g0)
    c: PointOnObject(g319,g0)
    c: PointOnObject(g303,g0)
    c: PointOnObject(g287,g0)
    c: PointOnObject(g271,g0)
    c: Vertical(g255,g509)
FEATURE [PartDesign::Pocket] Pocket002
  BaseFeature = -> Pocket001
  Length = 1
  Length2 = 100
  Profile = -> Sketch003
  Type = 0
FEATURE [Sketcher::SketchObject] Sketch004  label="vt mm"
  FullyConstrained = true
  MapMode = 5
  Support = -> [XY_Plane]
  expr: Constraints[8] = Spreadsheet.reticleCmWidth
  expr: Constraints[9] = Spreadsheet.reticleCmHeight / 2
  sketch-geometry (192):
    g0: LineSegment StartX=0 StartY=1.95 StartZ=0 EndX=2 EndY=1.95 EndZ=0
    g1: LineSegment StartX=2 StartY=1.95 StartZ=0 EndX=2 EndY=2.15 EndZ=0
    g2: LineSegment StartX=2 StartY=2.15 StartZ=0 EndX=0 EndY=2.15 EndZ=0
    g3: LineSegment StartX=0 StartY=2.15 StartZ=0 EndX=0 EndY=1.95 EndZ=0
    g4: LineSegment StartX=0 StartY=3.95 StartZ=0 EndX=2 EndY=3.95 EndZ=0
    g5: LineSegment StartX=2 StartY=3.95 StartZ=0 EndX=2 EndY=4.15 EndZ=0
    g6: LineSegment StartX=2 StartY=4.15 StartZ=0 EndX=0 EndY=4.15 EndZ=0
    g7: LineSegment StartX=0 StartY=4.15 StartZ=0 EndX=0 EndY=3.95 EndZ=0
    g8: LineSegment StartX=0 StartY=6.15 StartZ=0 EndX=2 EndY=6.15 EndZ=0
    g9: LineSegment StartX=2 StartY=6.15 StartZ=0 EndX=2 EndY=5.95 EndZ=0
    g10: LineSegment StartX=2 StartY=5.95 StartZ=0 EndX=0 EndY=5.95 EndZ=0
    g11: LineSegment StartX=0 StartY=5.95 StartZ=0 EndX=0 EndY=6.15 EndZ=0
    g12: LineSegment StartX=0 StartY=7.95 StartZ=0 EndX=2 EndY=7.95 EndZ=0
    g13: LineSegment StartX=2 StartY=7.95 StartZ=0 EndX=2 EndY=8.15 EndZ=0
    g14: LineSegment StartX=2 StartY=8.15 StartZ=0 EndX=0 EndY=8.15 EndZ=0
    g15: LineSegment StartX=0 StartY=8.15 StartZ=0 EndX=0 EndY=7.95 EndZ=0
    g16: LineSegment StartX=18 StartY=1.95 StartZ=0 EndX=20 EndY=1.95 EndZ=0
    g17: LineSegment StartX=20 StartY=1.95 StartZ=0 EndX=20 EndY=2.15 EndZ=0
    g18: LineSegment StartX=20 StartY=2.15 StartZ=0 EndX=18 EndY=2.15 EndZ=0
    g19: LineSegment StartX=18 StartY=2.15 StartZ=0 EndX=18 EndY=1.95 EndZ=0
    g20: LineSegment StartX=18 StartY=3.95 StartZ=0 EndX=20 EndY=3.95 EndZ=0
    g21: LineSegment StartX=20 StartY=3.95 StartZ=0 EndX=20 EndY=4.15 EndZ=0
    g22: LineSegment StartX=20 StartY=4.15 StartZ=0 EndX=18 EndY=4.15 EndZ=0
    g23: LineSegment StartX=18 StartY=4.15 StartZ=0 EndX=18 EndY=3.95 EndZ=0
    g24: LineSegment StartX=18 StartY=6.15 StartZ=0 EndX=20 EndY=6.15 EndZ=0
    g25: LineSegment StartX=20 StartY=6.15 StartZ=0 EndX=20 EndY=5.95 EndZ=0
    g26: LineSegment StartX=20 StartY=5.95 StartZ=0 EndX=18 EndY=5.95 EndZ=0
    g27: LineSegment StartX=18 StartY=5.95 StartZ=0 EndX=18 EndY=6.15 EndZ=0
    g28: LineSegment StartX=18 StartY=7.95 StartZ=0 EndX=20 EndY=7.95 EndZ=0
    g29: LineSegment StartX=20 StartY=7.95 StartZ=0 EndX=20 EndY=8.15 EndZ=0
    g30: LineSegment StartX=20 StartY=8.15 StartZ=0 EndX=18 EndY=8.15 EndZ=0
    g31: LineSegment StartX=18 StartY=8.15 StartZ=0 EndX=18 EndY=7.95 EndZ=0
    g32: LineSegment StartX=0 StartY=-8.05 StartZ=0 EndX=2 EndY=-8.05 EndZ=0
    g33: LineSegment StartX=2 StartY=-8.05 StartZ=0 EndX=2 EndY=-7.85 EndZ=0
    g34: LineSegment StartX=2 StartY=-7.85 StartZ=0 EndX=0 EndY=-7.85 EndZ=0
    g35: LineSegment StartX=0 StartY=-7.85 StartZ=0 EndX=0 EndY=-8.05 EndZ=0
    g36: LineSegment StartX=0 StartY=-6.05 StartZ=0 EndX=2 EndY=-6.05 EndZ=0
    g37: LineSegment StartX=2 StartY=-6.05 StartZ=0 EndX=2 EndY=-5.85 EndZ=0
    g38: LineSegment StartX=2 StartY=-5.85 StartZ=0 EndX=0 EndY=-5.85 EndZ=0
    g39: LineSegment StartX=0 StartY=-5.85 StartZ=0 EndX=0 EndY=-6.05 EndZ=0
    g40: LineSegment StartX=0 StartY=-3.85 StartZ=0 EndX=2 EndY=-3.85 EndZ=0
    g41: LineSegment StartX=2 StartY=-3.85 StartZ=0 EndX=2 EndY=-4.05 EndZ=0
    g42: LineSegment StartX=2 StartY=-4.05 StartZ=0 EndX=0 EndY=-4.05 EndZ=0
    g43: LineSegment StartX=0 StartY=-4.05 StartZ=0 EndX=0 EndY=-3.85 EndZ=0
    g44: LineSegment StartX=0 StartY=-2.05 StartZ=0 EndX=2 EndY=-2.05 EndZ=0
    g45: LineSegment StartX=2 StartY=-2.05 StartZ=0 EndX=2 EndY=-1.85 EndZ=0
    g46: LineSegment StartX=2 StartY=-1.85 StartZ=0 EndX=0 EndY=-1.85 EndZ=0
    g47: LineSegment StartX=0 StartY=-1.85 StartZ=0 EndX=0 EndY=-2.05 EndZ=0
    g48: LineSegment StartX=18 StartY=-8.05 StartZ=0 EndX=20 EndY=-8.05 EndZ=0
    g49: LineSegment StartX=20 StartY=-8.05 StartZ=0 EndX=20 EndY=-7.85 EndZ=0
    g50: LineSegment StartX=20 StartY=-7.85 StartZ=0 EndX=18 EndY=-7.85 EndZ=0
    g51: LineSegment StartX=18 StartY=-7.85 StartZ=0 EndX=18 EndY=-8.05 EndZ=0
    g52: LineSegment StartX=18 StartY=-6.05 StartZ=0 EndX=20 EndY=-6.05 EndZ=0
    g53: LineSegment StartX=20 StartY=-6.05 StartZ=0 EndX=20 EndY=-5.85 EndZ=0
    g54: LineSegment StartX=20 StartY=-5.85 StartZ=0 EndX=18 EndY=-5.85 EndZ=0
    g55: LineSegment StartX=18 StartY=-5.85 StartZ=0 EndX=18 EndY=-6.05 EndZ=0
    g56: LineSegment StartX=18 StartY=-3.85 StartZ=0 EndX=20 EndY=-3.85 EndZ=0
    g57: LineSegment StartX=20 StartY=-3.85 StartZ=0 EndX=20 EndY=-4.05 EndZ=0
    g58: LineSegment StartX=20 StartY=-4.05 StartZ=0 EndX=18 EndY=-4.05 EndZ=0
    g59: LineSegment StartX=18 StartY=-4.05 StartZ=0 EndX=18 EndY=-3.85 EndZ=0
    g60: LineSegment StartX=18 StartY=-2.05 StartZ=0 EndX=20 EndY=-2.05 EndZ=0
    g61: LineSegment StartX=20 StartY=-2.05 StartZ=0 EndX=20 EndY=-1.85 EndZ=0
    g62: LineSegment StartX=20 StartY=-1.85 StartZ=0 EndX=18 EndY=-1.85 EndZ=0
    g63: LineSegment StartX=18 StartY=-1.85 StartZ=0 EndX=18 EndY=-2.05 EndZ=0
    g64: LineSegment StartX=0 StartY=-18.05 StartZ=0 EndX=2 EndY=-18.05 EndZ=0
    g65: LineSegment StartX=2 StartY=-18.05 StartZ=0 EndX=2 EndY=-17.85 EndZ=0
    g66: LineSegment StartX=2 StartY=-17.85 StartZ=0 EndX=0 EndY=-17.85 EndZ=0
    g67: LineSegment StartX=0 StartY=-17.85 StartZ=0 EndX=0 EndY=-18.05 EndZ=0
    g68: LineSegment StartX=0 StartY=-16.05 StartZ=0 EndX=2 EndY=-16.05 EndZ=0
    g69: LineSegment StartX=2 StartY=-16.05 StartZ=0 EndX=2 EndY=-15.85 EndZ=0
    g70: LineSegment StartX=2 StartY=-15.85 StartZ=0 EndX=0 EndY=-15.85 EndZ=0
    g71: LineSegment StartX=0 StartY=-15.85 StartZ=0 EndX=0 EndY=-16.05 EndZ=0
    g72: LineSegment StartX=0 StartY=-13.85 StartZ=0 EndX=2 EndY=-13.85 EndZ=0
    g73: LineSegment StartX=2 StartY=-13.85 StartZ=0 EndX=2 EndY=-14.05 EndZ=0
    g74: LineSegment StartX=2 StartY=-14.05 StartZ=0 EndX=0 EndY=-14.05 EndZ=0
    g75: LineSegment StartX=0 StartY=-14.05 StartZ=0 EndX=0 EndY=-13.85 EndZ=0
    g76: LineSegment StartX=0 StartY=-12.05 StartZ=0 EndX=2 EndY=-12.05 EndZ=0
    g77: LineSegment StartX=2 StartY=-12.05 StartZ=0 EndX=2 EndY=-11.85 EndZ=0
    g78: LineSegment StartX=2 StartY=-11.85 StartZ=0 EndX=0 EndY=-11.85 EndZ=0
    g79: LineSegment StartX=0 StartY=-11.85 StartZ=0 EndX=0 EndY=-12.05 EndZ=0
    g80: LineSegment StartX=18 StartY=-18.05 StartZ=0 EndX=20 EndY=-18.05 EndZ=0
    g81: LineSegment StartX=20 StartY=-18.05 StartZ=0 EndX=20 EndY=-17.85 EndZ=0
    g82: LineSegment StartX=20 StartY=-17.85 StartZ=0 EndX=18 EndY=-17.85 EndZ=0
    g83: LineSegment StartX=18 StartY=-17.85 StartZ=0 EndX=18 EndY=-18.05 EndZ=0
    g84: LineSegment StartX=18 StartY=-16.05 StartZ=0 EndX=20 EndY=-16.05 EndZ=0
    g85: LineSegment StartX=20 StartY=-16.05 StartZ=0 EndX=20 EndY=-15.85 EndZ=0
    g86: LineSegment StartX=20 StartY=-15.85 StartZ=0 EndX=18 EndY=-15.85 EndZ=0
    g87: LineSegment StartX=18 StartY=-15.85 StartZ=0 EndX=18 EndY=-16.05 EndZ=0
    g88: LineSegment StartX=18 StartY=-13.85 StartZ=0 EndX=20 EndY=-13.85 EndZ=0
    g89: LineSegment StartX=20 StartY=-13.85 StartZ=0 EndX=20 EndY=-14.05 EndZ=0
    g90: LineSegment StartX=20 StartY=-14.05 StartZ=0 EndX=18 EndY=-14.05 EndZ=0
    g91: LineSegment StartX=18 StartY=-14.05 StartZ=0 EndX=18 EndY=-13.85 EndZ=0
    g92: LineSegment StartX=18 StartY=-12.05 StartZ=0 EndX=20 EndY=-12.05 EndZ=0
    g93: LineSegment StartX=20 StartY=-12.05 StartZ=0 EndX=20 EndY=-11.85 EndZ=0
    g94: LineSegment StartX=20 StartY=-11.85 StartZ=0 EndX=18 EndY=-11.85 EndZ=0
    g95: LineSegment StartX=18 StartY=-11.85 StartZ=0 EndX=18 EndY=-12.05 EndZ=0
    g96: LineSegment StartX=0 StartY=-28.05 StartZ=0 EndX=2 EndY=-28.05 EndZ=0
    g97: LineSegment StartX=2 StartY=-28.05 StartZ=0 EndX=2 EndY=-27.85 EndZ=0
    g98: LineSegment StartX=2 StartY=-27.85 StartZ=0 EndX=0 EndY=-27.85 EndZ=0
    g99: LineSegment StartX=0 StartY=-27.85 StartZ=0 EndX=0 EndY=-28.05 EndZ=0
    g100: LineSegment StartX=0 StartY=-26.05 StartZ=0 EndX=2 EndY=-26.05 EndZ=0
    g101: LineSegment StartX=2 StartY=-26.05 StartZ=0 EndX=2 EndY=-25.85 EndZ=0
    g102: LineSegment StartX=2 StartY=-25.85 StartZ=0 EndX=0 EndY=-25.85 EndZ=0
    g103: LineSegment StartX=0 StartY=-25.85 StartZ=0 EndX=0 EndY=-26.05 EndZ=0
    g104: LineSegment StartX=0 StartY=-23.85 StartZ=0 EndX=2 EndY=-23.85 EndZ=0
    g105: LineSegment StartX=2 StartY=-23.85 StartZ=0 EndX=2 EndY=-24.05 EndZ=0
    g106: LineSegment StartX=2 StartY=-24.05 StartZ=0 EndX=0 EndY=-24.05 EndZ=0
    g107: LineSegment StartX=0 StartY=-24.05 StartZ=0 EndX=0 EndY=-23.85 EndZ=0
    g108: LineSegment StartX=0 StartY=-22.05 StartZ=0 EndX=2 EndY=-22.05 EndZ=0
    g109: LineSegment StartX=2 StartY=-22.05 StartZ=0 EndX=2 EndY=-21.85 EndZ=0
    g110: LineSegment StartX=2 StartY=-21.85 StartZ=0 EndX=0 EndY=-21.85 EndZ=0
    g111: LineSegment StartX=0 StartY=-21.85 StartZ=0 EndX=0 EndY=-22.05 EndZ=0
    g112: LineSegment StartX=18 StartY=-28.05 StartZ=0 EndX=20 EndY=-28.05 EndZ=0
    g113: LineSegment StartX=20 StartY=-28.05 StartZ=0 EndX=20 EndY=-27.85 EndZ=0
    g114: LineSegment StartX=20 StartY=-27.85 StartZ=0 EndX=18 EndY=-27.85 EndZ=0
    g115: LineSegment StartX=18 StartY=-27.85 StartZ=0 EndX=18 EndY=-28.05 EndZ=0
    g116: LineSegment StartX=18 StartY=-26.05 StartZ=0 EndX=20 EndY=-26.05 EndZ=0
    g117: LineSegment StartX=20 StartY=-26.05 StartZ=0 EndX=20 EndY=-25.85 EndZ=0
    g118: LineSegment StartX=20 StartY=-25.85 StartZ=0 EndX=18 EndY=-25.85 EndZ=0
    g119: LineSegment StartX=18 StartY=-25.85 StartZ=0 EndX=18 EndY=-26.05 EndZ=0
    g120: LineSegment StartX=18 StartY=-23.85 StartZ=0 EndX=20 EndY=-23.85 EndZ=0
    g121: LineSegment StartX=20 StartY=-23.85 StartZ=0 EndX=20 EndY=-24.05 EndZ=0
    g122: LineSegment StartX=20 StartY=-24.05 StartZ=0 EndX=18 EndY=-24.05 EndZ=0
    g123: LineSegment StartX=18 StartY=-24.05 StartZ=0 EndX=18 EndY=-23.85 EndZ=0
    g124: LineSegment StartX=18 StartY=-22.05 StartZ=0 EndX=20 EndY=-22.05 EndZ=0
    g125: LineSegment StartX=20 StartY=-22.05 StartZ=0 EndX=20 EndY=-21.85 EndZ=0
    g126: LineSegment StartX=20 StartY=-21.85 StartZ=0 EndX=18 EndY=-21.85 EndZ=0
    g127: LineSegment StartX=18 StartY=-21.85 StartZ=0 EndX=18 EndY=-22.05 EndZ=0
    g128: LineSegment StartX=0 StartY=-38.05 StartZ=0 EndX=2 EndY=-38.05 EndZ=0
    g129: LineSegment StartX=2 StartY=-38.05 StartZ=0 EndX=2 EndY=-38.25 EndZ=0
    g130: LineSegment StartX=2 StartY=-38.25 StartZ=0 EndX=0 EndY=-38.25 EndZ=0
    g131: LineSegment StartX=0 StartY=-38.25 StartZ=0 EndX=0 EndY=-38.05 EndZ=0
    g132: LineSegment StartX=0 StartY=-36.05 StartZ=0 EndX=2 EndY=-36.05 EndZ=0
    g133: LineSegment StartX=2 StartY=-36.05 StartZ=0 EndX=2 EndY=-36.25 EndZ=0
    g134: LineSegment StartX=2 StartY=-36.25 StartZ=0 EndX=0 EndY=-36.25 EndZ=0
    g135: LineSegment StartX=0 StartY=-36.25 StartZ=0 EndX=0 EndY=-36.05 EndZ=0
    g136: LineSegment StartX=0 StartY=-34.25 StartZ=0 EndX=2 EndY=-34.25 EndZ=0
    g137: LineSegment StartX=2 StartY=-34.25 StartZ=0 EndX=2 EndY=-34.05 EndZ=0
    g138: LineSegment StartX=2 StartY=-34.05 StartZ=0 EndX=0 EndY=-34.05 EndZ=0
    g139: LineSegment StartX=0 StartY=-34.05 StartZ=0 EndX=0 EndY=-34.25 EndZ=0
    g140: LineSegment StartX=0 StartY=-32.05 StartZ=0 EndX=2 EndY=-32.05 EndZ=0
    g141: LineSegment StartX=2 StartY=-32.05 StartZ=0 EndX=2 EndY=-31.85 EndZ=0
    g142: LineSegment StartX=2 StartY=-31.85 StartZ=0 EndX=0 EndY=-31.85 EndZ=0
    g143: LineSegment StartX=0 StartY=-31.85 StartZ=0 EndX=0 EndY=-32.05 EndZ=0
    g144: LineSegment StartX=18 StartY=-38.05 StartZ=0 EndX=20 EndY=-38.05 EndZ=0
    g145: LineSegment StartX=20 StartY=-38.05 StartZ=0 EndX=20 EndY=-38.25 EndZ=0
    g146: LineSegment StartX=20 StartY=-38.25 StartZ=0 EndX=18 EndY=-38.25 EndZ=0
    g147: LineSegment StartX=18 StartY=-38.25 StartZ=0 EndX=18 EndY=-38.05 EndZ=0
    g148: LineSegment StartX=18 StartY=-36.05 StartZ=0 EndX=20 EndY=-36.05 EndZ=0
    g149: LineSegment StartX=20 StartY=-36.05 StartZ=0 EndX=20 EndY=-36.25 EndZ=0
    g150: LineSegment StartX=20 StartY=-36.25 StartZ=0 EndX=18 EndY=-36.25 EndZ=0
    g151: LineSegment StartX=18 StartY=-36.25 StartZ=0 EndX=18 EndY=-36.05 EndZ=0
    g152: LineSegment StartX=18 StartY=-34.25 StartZ=0 EndX=20 EndY=-34.25 EndZ=0
    g153: LineSegment StartX=20 StartY=-34.25 StartZ=0 EndX=20 EndY=-34.05 EndZ=0
    g154: LineSegment StartX=20 StartY=-34.05 StartZ=0 EndX=18 EndY=-34.05 EndZ=0
    g155: LineSegment StartX=18 StartY=-34.05 StartZ=0 EndX=18 EndY=-34.25 EndZ=0
    g156: LineSegment StartX=18 StartY=-32.05 StartZ=0 EndX=20 EndY=-32.05 EndZ=0
    g157: LineSegment StartX=20 StartY=-32.05 StartZ=0 EndX=20 EndY=-31.85 EndZ=0
    g158: LineSegment StartX=20 StartY=-31.85 StartZ=0 EndX=18 EndY=-31.85 EndZ=0
    g159: LineSegment StartX=18 StartY=-31.85 StartZ=0 EndX=18 EndY=-32.05 EndZ=0
    g160: LineSegment StartX=0 StartY=11.95 StartZ=0 EndX=2 EndY=11.95 EndZ=0
    g161: LineSegment StartX=2 StartY=11.95 StartZ=0 EndX=2 EndY=12.15 EndZ=0
    g162: LineSegment StartX=2 StartY=12.15 StartZ=0 EndX=0 EndY=12.15 EndZ=0
    g163: LineSegment StartX=0 StartY=12.15 StartZ=0 EndX=0 EndY=11.95 EndZ=0
    g164: LineSegment StartX=0 StartY=13.95 StartZ=0 EndX=2 EndY=13.95 EndZ=0
    g165: LineSegment StartX=2 StartY=13.95 StartZ=0 EndX=2 EndY=14.15 EndZ=0
    g166: LineSegment StartX=2 StartY=14.15 StartZ=0 EndX=0 EndY=14.15 EndZ=0
    g167: LineSegment StartX=0 StartY=14.15 StartZ=0 EndX=0 EndY=13.95 EndZ=0
    g168: LineSegment StartX=0 StartY=16.15 StartZ=0 EndX=2 EndY=16.15 EndZ=0
    g169: LineSegment StartX=2 StartY=16.15 StartZ=0 EndX=2 EndY=15.95 EndZ=0
    g170: LineSegment StartX=2 StartY=15.95 StartZ=0 EndX=0 EndY=15.95 EndZ=0
    g171: LineSegment StartX=0 StartY=15.95 StartZ=0 EndX=0 EndY=16.15 EndZ=0
    g172: LineSegment StartX=0 StartY=17.95 StartZ=0 EndX=2 EndY=17.95 EndZ=0
    g173: LineSegment StartX=2 StartY=17.95 StartZ=0 EndX=2 EndY=18.15 EndZ=0
    g174: LineSegment StartX=2 StartY=18.15 StartZ=0 EndX=0 EndY=18.15 EndZ=0
    g175: LineSegment StartX=0 StartY=18.15 StartZ=0 EndX=0 EndY=17.95 EndZ=0
    g176: LineSegment StartX=18 StartY=11.95 StartZ=0 EndX=20 EndY=11.95 EndZ=0
    g177: LineSegment StartX=20 StartY=11.95 StartZ=0 EndX=20 EndY=12.15 EndZ=0
    g178: LineSegment StartX=20 StartY=12.15 StartZ=0 EndX=18 EndY=12.15 EndZ=0
    g179: LineSegment StartX=18 StartY=12.15 StartZ=0 EndX=18 EndY=11.95 EndZ=0
    g180: LineSegment StartX=18 StartY=13.95 StartZ=0 EndX=20 EndY=13.95 EndZ=0
    g181: LineSegment StartX=20 StartY=13.95 StartZ=0 EndX=20 EndY=14.15 EndZ=0
    g182: LineSegment StartX=20 StartY=14.15 StartZ=0 EndX=18 EndY=14.15 EndZ=0
    g183: LineSegment StartX=18 StartY=14.15 StartZ=0 EndX=18 EndY=13.95 EndZ=0
    g184: LineSegment StartX=18 StartY=16.15 StartZ=0 EndX=20 EndY=16.15 EndZ=0
    g185: LineSegment StartX=20 StartY=16.15 StartZ=0 EndX=20 EndY=15.95 EndZ=0
    g186: LineSegment StartX=20 StartY=15.95 StartZ=0 EndX=18 EndY=15.95 EndZ=0
    g187: LineSegment StartX=18 StartY=15.95 StartZ=0 EndX=18 EndY=16.15 EndZ=0
    g188: LineSegment StartX=18 StartY=17.95 StartZ=0 EndX=20 EndY=17.95 EndZ=0
    g189: LineSegment StartX=20 StartY=17.95 StartZ=0 EndX=20 EndY=18.15 EndZ=0
    g190: LineSegment StartX=20 StartY=18.15 StartZ=0 EndX=18 EndY=18.15 EndZ=0
    g191: LineSegment StartX=18 StartY=18.15 StartZ=0 EndX=18 EndY=17.95 EndZ=0
  constraints (576):
    c: Coincident(g1,g2)
    c: Coincident(g2,g3)
    c: Coincident(g3,g0)
    c: Horizontal(g0)
    c: Horizontal(g2)
    c: Vertical(g1)
    c: Vertical(g3)
    c: PointOnObject(g0,g-2)
    c: DistanceY(g1,g1) = 0.2
    c: DistanceX(g0,g0) = 2
    c: Coincident(g4,g5)
    c: Coincident(g5,g6)
    c: Coincident(g6,g7)
    c: Coincident(g7,g4)
    c: Horizontal(g4)
    c: Horizontal(g6)
    c: Vertical(g5)
    c: Vertical(g7)
    c: PointOnObject(g4,g-2)
    c: Coincident(g8,g9)
    c: Coincident(g9,g10)
    c: Coincident(g10,g11)
    c: Coincident(g11,g8)
    c: Horizontal(g8)
    c: Horizontal(g10)
    c: Vertical(g9)
    c: Vertical(g11)
    c: PointOnObject(g8,g-2)
    c: Coincident(g12,g13)
    c: Coincident(g13,g14)
    c: Coincident(g14,g15)
    c: Coincident(g15,g12)
    c: Horizontal(g12)
    c: Horizontal(g14)
    c: Vertical(g13)
    c: Vertical(g15)
    c: PointOnObject(g12,g-2)
    c: Equal(g14,g10)
    c: Equal(g10,g4)
    c: Equal(g4,g0)
    c: Equal(g1,g5)
    c: Equal(g5,g9)
    c: Equal(g9,g13)
    c: DistanceY(g4,g9) = 2
    c: Coincident(g16,g17)
    c: Coincident(g17,g18)
    c: Coincident(g18,g19)
    c: Coincident(g19,g16)
    c: Horizontal(g16)
    c: Horizontal(g18)
    c: Vertical(g17)
    c: Vertical(g19)
    c: Equal(g1,g17) = 0.2
    c: Equal(g0,g16) = 2
    c: Coincident(g20,g21)
    c: Coincident(g21,g22)
    c: Coincident(g22,g23)
    c: Coincident(g23,g20)
    c: Horizontal(g20)
    c: Horizontal(g22)
    c: Vertical(g21)
    c: Vertical(g23)
    c: Coincident(g24,g25)
    c: Coincident(g25,g26)
    c: Coincident(g26,g27)
    c: Coincident(g27,g24)
    c: Horizontal(g24)
    c: Horizontal(g26)
    c: Vertical(g25)
    c: Vertical(g27)
    c: Coincident(g28,g29)
    c: Coincident(g29,g30)
    c: Coincident(g30,g31)
    c: Coincident(g31,g28)
    c: Horizontal(g28)
    c: Horizontal(g30)
    c: Vertical(g29)
    c: Vertical(g31)
    c: Equal(g30,g26)
    c: Equal(g26,g20)
    c: Equal(g20,g16)
    c: Equal(g17,g21)
    c: Equal(g21,g25)
    c: Equal(g25,g29)
    c: DistanceY(g16,g20) = 2
    c: DistanceY(g20,g25) = 2
    c: DistanceX(g14,g29) = 20
    c: Vertical(g28,g24)
    c: Vertical(g25,g21)
    c: Vertical(g20,g17)
    c: Horizontal(g12,g28)
    c: Coincident(g32,g33)
    c: Coincident(g33,g34)
    c: Coincident(g34,g35)
    c: Coincident(g35,g32)
    c: Horizontal(g32)
    c: Horizontal(g34)
    c: Vertical(g33)
    c: Vertical(g35)
    c: Equal(g1,g33) = 0.2
    c: Equal(g0,g32) = 2
    c: Coincident(g36,g37)
    c: Coincident(g37,g38)
    c: Coincident(g38,g39)
    c: Coincident(g39,g36)
    c: Horizontal(g36)
    c: Horizontal(g38)
    c: Vertical(g37)
    c: Vertical(g39)
    c: Coincident(g40,g41)
    c: Coincident(g41,g42)
    c: Coincident(g42,g43)
    c: Coincident(g43,g40)
    c: Horizontal(g40)
    c: Horizontal(g42)
    c: Vertical(g41)
    c: Vertical(g43)
    c: Coincident(g44,g45)
    c: Coincident(g45,g46)
    c: Coincident(g46,g47)
    c: Coincident(g47,g44)
    c: Horizontal(g44)
    c: Horizontal(g46)
    c: Vertical(g45)
    c: Vertical(g47)
    c: Equal(g46,g42)
    c: Equal(g42,g36)
    c: Equal(g36,g32)
    c: Equal(g33,g37)
    c: Equal(g37,g41)
    c: Equal(g41,g45)
    c: DistanceY(g32,g36) = 2
    c: DistanceY(g36,g41) = 2
    c: Coincident(g48,g49)
    c: Coincident(g49,g50)
    c: Coincident(g50,g51)
    c: Coincident(g51,g48)
    c: Horizontal(g48)
    c: Horizontal(g50)
    c: Vertical(g49)
    c: Vertical(g51)
    c: Equal(g33,g49) = 0.2
    c: Equal(g32,g48) = 2
    c: Coincident(g52,g53)
    c: Coincident(g53,g54)
    c: Coincident(g54,g55)
    c: Coincident(g55,g52)
    c: Horizontal(g52)
    c: Horizontal(g54)
    c: Vertical(g53)
    c: Vertical(g55)
    c: Coincident(g56,g57)
    c: Coincident(g57,g58)
    c: Coincident(g58,g59)
    c: Coincident(g59,g56)
    c: Horizontal(g56)
    c: Horizontal(g58)
    c: Vertical(g57)
    c: Vertical(g59)
    c: Coincident(g60,g61)
    c: Coincident(g61,g62)
    c: Coincident(g62,g63)
    c: Coincident(g63,g60)
    c: Horizontal(g60)
    c: Horizontal(g62)
    c: Vertical(g61)
    c: Vertical(g63)
    c: Equal(g62,g58)
    c: Equal(g58,g52)
    c: Equal(g52,g48)
    c: Equal(g49,g53)
    c: Equal(g53,g57)
    c: Equal(g57,g61)
    c: DistanceY(g48,g52) = 2
    c: DistanceY(g52,g57) = 2
    c: DistanceX(g46,g61) = 20
    c: Vertical(g60,g56)
    c: Vertical(g57,g53)
    c: Vertical(g52,g49)
    c: Horizontal(g44,g60)
    c: DistanceY(g0,g4) = 2
    c: DistanceY(g44,g0) = 4
    c: DistanceY(g41,g44) = 2
    c: Coincident(g1,g0)
    c: DistanceY(g58,g60) = 2
    c: DistanceY(g26,g28) = 2
    c: DistanceY(g9,g12) = 2
    c: Vertical(g0,g46)
    c: Vertical(g40,g44)
    c: Vertical(g38,g42)
    c: Vertical(g34,g36)
    c: Coincident(g65,g66)
    c: Coincident(g66,g67)
    c: Coincident(g67,g64)
    c: Horizontal(g64)
    c: Horizontal(g66)
    c: Vertical(g65)
    c: Vertical(g67)
    c: Equal(g1,g65) = 0.2
    c: Equal(g0,g64) = 2
    c: Coincident(g68,g69)
    c: Coincident(g69,g70)
    c: Coincident(g70,g71)
    c: Coincident(g71,g68)
    c: Horizontal(g68)
    c: Horizontal(g70)
    c: Vertical(g69)
    c: Vertical(g71)
    c: Coincident(g72,g73)
    c: Coincident(g73,g74)
    c: Coincident(g74,g75)
    c: Coincident(g75,g72)
    c: Horizontal(g72)
    c: Horizontal(g74)
    c: Vertical(g73)
    c: Vertical(g75)
    c: Coincident(g76,g77)
    c: Coincident(g77,g78)
    c: Coincident(g78,g79)
    c: Coincident(g79,g76)
    c: Horizontal(g76)
    c: Horizontal(g78)
    c: Vertical(g77)
    c: Vertical(g79)
    c: Equal(g78,g74)
    c: Equal(g74,g68)
    c: Equal(g68,g64)
    c: Equal(g65,g69)
    c: Equal(g69,g73)
    c: Equal(g73,g77)
    c: DistanceY(g68,g73) = 2
    c: Coincident(g80,g81)
    c: Coincident(g81,g82)
    c: Coincident(g82,g83)
    c: Coincident(g83,g80)
    c: Horizontal(g80)
    c: Horizontal(g82)
    c: Vertical(g81)
    c: Vertical(g83)
    c: Equal(g65,g81) = 0.2
    c: Equal(g64,g80) = 2
    c: Coincident(g84,g85)
    c: Coincident(g85,g86)
    c: Coincident(g86,g87)
    c: Coincident(g87,g84)
    c: Horizontal(g84)
    c: Horizontal(g86)
    c: Vertical(g85)
    c: Vertical(g87)
    c: Coincident(g88,g89)
    c: Coincident(g89,g90)
    c: Coincident(g90,g91)
    c: Coincident(g91,g88)
    c: Horizontal(g88)
    c: Horizontal(g90)
    c: Vertical(g89)
    c: Vertical(g91)
    c: Coincident(g92,g93)
    c: Coincident(g93,g94)
    c: Coincident(g94,g95)
    c: Coincident(g95,g92)
    c: Horizontal(g92)
    c: Horizontal(g94)
    c: Vertical(g93)
    c: Vertical(g95)
    c: Equal(g94,g90)
    c: Equal(g90,g84)
    c: Equal(g84,g80)
    c: Equal(g81,g85)
    c: Equal(g85,g89)
    c: Equal(g89,g93)
    c: DistanceY(g80,g84) = 2
    c: DistanceY(g84,g89) = 2
    c: DistanceX(g78,g93) = 20
    c: Vertical(g92,g88)
    c: Vertical(g89,g85)
    c: Vertical(g84,g81)
    c: Horizontal(g76,g92)
    c: Coincident(g96,g97)
    c: Coincident(g97,g98)
    c: Coincident(g98,g99)
    c: Coincident(g99,g96)
    c: Horizontal(g96)
    c: Horizontal(g98)
    c: Vertical(g97)
    c: Vertical(g99)
    c: Equal(g65,g97) = 0.2
    c: Equal(g64,g96) = 2
    c: Coincident(g100,g101)
    c: Coincident(g101,g102)
    c: Coincident(g102,g103)
    c: Coincident(g103,g100)
    c: Horizontal(g100)
    c: Horizontal(g102)
    c: Vertical(g101)
    c: Vertical(g103)
    c: Coincident(g104,g105)
    c: Coincident(g105,g106)
    c: Coincident(g106,g107)
    c: Coincident(g107,g104)
    c: Horizontal(g104)
    c: Horizontal(g106)
    c: Vertical(g105)
    c: Vertical(g107)
    c: Coincident(g108,g109)
    c: Coincident(g109,g110)
    c: Coincident(g110,g111)
    c: Coincident(g111,g108)
    c: Horizontal(g108)
    c: Horizontal(g110)
    c: Vertical(g109)
    c: Vertical(g111)
    c: Equal(g110,g106)
    c: Equal(g106,g100)
    c: Equal(g100,g96)
    c: Equal(g97,g101)
    c: Equal(g101,g105)
    c: Equal(g105,g109)
    c: DistanceY(g96,g100) = 2
    c: DistanceY(g100,g105) = 2
    c: Coincident(g112,g113)
    c: Coincident(g113,g114)
    c: Coincident(g114,g115)
    c: Coincident(g115,g112)
    c: Horizontal(g112)
    c: Horizontal(g114)
    c: Vertical(g113)
    c: Vertical(g115)
    c: Equal(g97,g113) = 0.2
    c: Equal(g96,g112) = 2
    c: Coincident(g116,g117)
    c: Coincident(g117,g118)
    c: Coincident(g118,g119)
    c: Coincident(g119,g116)
    c: Horizontal(g116)
    c: Horizontal(g118)
    c: Vertical(g117)
    c: Vertical(g119)
    c: Coincident(g120,g121)
    c: Coincident(g121,g122)
    c: Coincident(g122,g123)
    c: Coincident(g123,g120)
    c: Horizontal(g120)
    c: Horizontal(g122)
    c: Vertical(g121)
    c: Vertical(g123)
    c: Coincident(g124,g125)
    c: Coincident(g125,g126)
    c: Coincident(g126,g127)
    c: Coincident(g127,g124)
    c: Horizontal(g124)
    c: Horizontal(g126)
    c: Vertical(g125)
    c: Vertical(g127)
    c: Equal(g126,g122)
    c: Equal(g122,g116)
    c: Equal(g116,g112)
    c: Equal(g113,g117)
    c: Equal(g117,g121)
    c: Equal(g121,g125)
    c: DistanceY(g112,g116) = 2
    c: DistanceY(g116,g121) = 2
    c: DistanceX(g110,g125) = 20
    c: Vertical(g124,g120)
    c: Vertical(g121,g117)
    c: Vertical(g116,g113)
    c: Horizontal(g108,g124)
    c: DistanceY(g64,g68) = 2
    c: DistanceY(g108,g64) = 4
    c: DistanceY(g105,g108) = 2
    c: Coincident(g65,g64)
    c: DistanceY(g122,g124) = 2
    c: DistanceY(g90,g92) = 2
    c: DistanceY(g73,g76) = 2
    c: Vertical(g64,g110)
    c: Vertical(g104,g108)
    c: Vertical(g102,g106)
    c: Vertical(g98,g100)
    c: Vertical(g78,g32)
    c: DistanceY(g76,g32) = 4
    c: Vertical(g76,g72)
    c: Vertical(g70,g74)
    c: Vertical(g66,g68)
    c: Coincident(g129,g130)
    c: Coincident(g130,g131)
    c: Coincident(g131,g128)
    c: Horizontal(g128)
    c: Horizontal(g130)
    c: Vertical(g129)
    c: Vertical(g131)
    c: Coincident(g132,g133)
    c: Coincident(g133,g134)
    c: Coincident(g134,g135)
    c: Coincident(g135,g132)
    c: Horizontal(g132)
    c: Horizontal(g134)
    c: Vertical(g133)
    c: Vertical(g135)
    c: Coincident(g136,g137)
    c: Coincident(g137,g138)
    c: Coincident(g138,g139)
    c: Coincident(g139,g136)
    c: Horizontal(g136)
    c: Horizontal(g138)
    c: Vertical(g137)
    c: Vertical(g139)
    c: Coincident(g140,g141)
    c: Coincident(g141,g142)
    c: Coincident(g142,g143)
    c: Coincident(g143,g140)
    c: Horizontal(g140)
    c: Horizontal(g142)
    c: Vertical(g141)
    c: Vertical(g143)
    c: Equal(g142,g138)
    c: Equal(g138,g132)
    c: Equal(g132,g128)
    c: Equal(g129,g133)
    c: Equal(g133,g137)
    c: Equal(g137,g141)
    c: DistanceY(g132,g137) = 2
    c: Coincident(g144,g145)
    c: Coincident(g145,g146)
    c: Coincident(g146,g147)
    c: Coincident(g147,g144)
    c: Horizontal(g144)
    c: Horizontal(g146)
    c: Vertical(g145)
    c: Vertical(g147)
    c: Equal(g129,g145) = 0.2
    c: Equal(g128,g144) = 2
    c: Coincident(g148,g149)
    c: Coincident(g149,g150)
    c: Coincident(g150,g151)
    c: Coincident(g151,g148)
    c: Horizontal(g148)
    c: Horizontal(g150)
    c: Vertical(g149)
    c: Vertical(g151)
    c: Coincident(g152,g153)
    c: Coincident(g153,g154)
    c: Coincident(g154,g155)
    c: Coincident(g155,g152)
    c: Horizontal(g152)
    c: Horizontal(g154)
    c: Vertical(g153)
    c: Vertical(g155)
    c: Coincident(g156,g157)
    c: Coincident(g157,g158)
    c: Coincident(g158,g159)
    c: Coincident(g159,g156)
    c: Horizontal(g156)
    c: Horizontal(g158)
    c: Vertical(g157)
    c: Vertical(g159)
    c: Equal(g158,g154)
    c: Equal(g154,g148)
    c: Equal(g148,g144)
    c: Equal(g145,g149)
    c: Equal(g149,g153)
    c: Equal(g153,g157)
    c: DistanceY(g144,g148) = 2
    c: DistanceY(g148,g153) = 2
    c: DistanceX(g142,g157) = 20
    c: Vertical(g156,g152)
    c: Vertical(g153,g149)
    c: Vertical(g148,g145)
    c: Horizontal(g140,g156)
    c: DistanceY(g128,g132) = 2
    c: Coincident(g129,g128)
    c: DistanceY(g154,g156) = 2
    c: DistanceY(g137,g140) = 2
    c: Vertical(g140,g136)
    c: Vertical(g134,g138)
    c: Vertical(g130,g132)
    c: Vertical(g96,g142)
    c: DistanceY(g140,g96) = 4
    c: Equal(g97,g137)
    c: DistanceY(g0) = 1.95
    c: Equal(g114,g158)
    c: Coincident(g161,g162)
    c: Coincident(g162,g163)
    c: Coincident(g163,g160)
    c: Horizontal(g160)
    c: Horizontal(g162)
    c: Vertical(g161)
    c: Vertical(g163)
    c: Equal(g1,g161) = 0.2
    c: Equal(g0,g160) = 2
    c: Coincident(g164,g165)
    c: Coincident(g165,g166)
    c: Coincident(g166,g167)
    c: Coincident(g167,g164)
    c: Horizontal(g164)
    c: Horizontal(g166)
    c: Vertical(g165)
    c: Vertical(g167)
    c: Coincident(g168,g169)
    c: Coincident(g169,g170)
    c: Coincident(g170,g171)
    c: Coincident(g171,g168)
    c: Horizontal(g168)
    c: Horizontal(g170)
    c: Vertical(g169)
    c: Vertical(g171)
    c: Coincident(g172,g173)
    c: Coincident(g173,g174)
    c: Coincident(g174,g175)
    c: Coincident(g175,g172)
    c: Horizontal(g172)
    c: Horizontal(g174)
    c: Vertical(g173)
    c: Vertical(g175)
    c: Equal(g174,g170)
    c: Equal(g170,g164)
    c: Equal(g164,g160)
    c: Equal(g161,g165)
    c: Equal(g165,g169)
    c: Equal(g169,g173)
    c: DistanceY(g164,g169) = 2
    c: Coincident(g176,g177)
    c: Coincident(g177,g178)
    c: Coincident(g178,g179)
    c: Coincident(g179,g176)
    c: Horizontal(g176)
    c: Horizontal(g178)
    c: Vertical(g177)
    c: Vertical(g179)
    c: Equal(g161,g177) = 0.2
    c: Equal(g160,g176) = 2
    c: Coincident(g180,g181)
    c: Coincident(g181,g182)
    c: Coincident(g182,g183)
    c: Coincident(g183,g180)
    c: Horizontal(g180)
    c: Horizontal(g182)
    c: Vertical(g181)
    c: Vertical(g183)
    c: Coincident(g184,g185)
    c: Coincident(g185,g186)
    c: Coincident(g186,g187)
    c: Coincident(g187,g184)
    c: Horizontal(g184)
    c: Horizontal(g186)
    c: Vertical(g185)
    c: Vertical(g187)
    c: Coincident(g188,g189)
    c: Coincident(g189,g190)
    c: Coincident(g190,g191)
    c: Coincident(g191,g188)
    c: Horizontal(g188)
    c: Horizontal(g190)
    c: Vertical(g189)
    c: Vertical(g191)
    c: Equal(g190,g186)
    c: Equal(g186,g180)
    c: Equal(g180,g176)
    c: Equal(g177,g181)
    c: Equal(g181,g185)
    c: Equal(g185,g189)
    c: DistanceY(g176,g180) = 2
    c: DistanceY(g180,g185) = 2
    c: DistanceX(g174,g189) = 20
    c: Vertical(g188,g184)
    c: Vertical(g185,g181)
    c: Vertical(g180,g177)
    c: Horizontal(g172,g188)
    c: DistanceY(g160,g164) = 2
    c: Coincident(g161,g160)
    c: DistanceY(g186,g188) = 2
    c: DistanceY(g169,g172) = 2
    c: DistanceY(g28,g176) = 4
    c: PointOnObject(g172,g-2)
    c: PointOnObject(g160,g-2)
    c: Vertical(g164,g162)
    c: Vertical(g170,g166)
FEATURE [PartDesign::Pocket] Pocket003
  BaseFeature = -> Pocket002
  Length = 1
  Length2 = 100
  Profile = -> Sketch004
  Type = 0
FEATURE [Part::Part2DObjectPython] ShapeString  # Draft 2D object (typed FeaturePython)
  FontFile = <path> Squares/AdobeGothicStd-Bold.otf
  Placement = pos=(78,-12.5,0) rot=(0,0,1;0rad)
  Size = 4
  String = 8     9   10   11  12   13  14   15  16   17  18  19   20  21   22  23  2
  Tracking = 0
FEATURE [Part::Part2DObjectPython] ShapeString001  # Draft 2D object (typed FeaturePython)
  FontFile = <path> Squares/AdobeGothicStd-Bold.otf
  Placement = pos=(12,-51.5,0) rot=(0,0,1;1.5708rad)
  Size = 4
  String =         2     1     0     1     0     1     2  
  Tracking = 0
FEATURE [Sketcher::SketchObject] Sketch005
  FullyConstrained = false
  MapMode = 5
  Support = -> [XY_Plane001]
  sketch-geometry (12):
    g0: LineSegment StartX=1.45986 StartY=1.15 StartZ=0 EndX=1.45986 EndY=-1.15 EndZ=0
    g1: LineSegment StartX=1.45986 StartY=-1.15 StartZ=0 EndX=4.45986 EndY=-1.15 EndZ=0
    g2: LineSegment StartX=2.45546 StartY=-2.2306 StartZ=0 EndX=-2.07111 EndY=-2.2306 EndZ=0
    g3: LineSegment StartX=-2.16518 StartY=2.56591 StartZ=0 EndX=2.36139 EndY=2.56591 EndZ=0
    g4: ArcOfCircle CenterX=-2.16518 CenterY=0.61751 CenterZ=0 NormalX=0 NormalY=0 NormalZ=1 AngleXU=0 Radius=1.9484 StartAngle=1.5708 EndAngle=2.81098
    g5: ArcOfCircle CenterX=-2.07111 CenterY=0.172701 CenterZ=0 NormalX=0 NormalY=0 NormalZ=1 AngleXU=0 Radius=2.40331 StartAngle=3.7751 EndAngle=4.71239
    g6: ArcOfCircle CenterX=2.45546 CenterY=0.168658 CenterZ=0 NormalX=0 NormalY=0 NormalZ=1 AngleXU=0 Radius=2.39926 StartAngle=4.71239 EndAngle=5.70129
    g7: ArcOfCircle CenterX=2.36139 CenterY=0.302922 CenterZ=0 NormalX=0 NormalY=0 NormalZ=1 AngleXU=0 Radius=2.26299 StartAngle=0.383662 EndAngle=1.5708
    g8: ArcOfCircle CenterX=-1.96654 CenterY=-0.00298329 CenterZ=0 NormalX=0 NormalY=0 NormalZ=1 AngleXU=0 Radius=1.69596 StartAngle=3.96768 EndAngle=8.59348
    g9: LineSegment StartX=-3.10948 StartY=1.25 StartZ=0 EndX=-4.00807 EndY=1.25 EndZ=0
    g10: LineSegment StartX=-3.11598 StartY=-1.25 StartZ=0 EndX=-4.00807 EndY=-1.25 EndZ=0
    g11: LineSegment StartX=1.45986 StartY=1.15 StartZ=0 EndX=4.45986 EndY=1.15 EndZ=0
  constraints (25):
    c: Coincident(g0,g1)
    c: Horizontal(g1)
    c: Horizontal(g2)
    c: Horizontal(g3)
    c: Tangent(g3,g4) = 1.5708
    c: Tangent(g2,g5) = 1.5708
    c: Equal(g3,g2)
    c: DistanceY(g0,g0) = 2.3
    c: DistanceY(g5,g4) = 2.5
    c: Tangent(g2,g6) = 1.5708
    c: Tangent(g3,g7) = 1.5708
    c: Horizontal(g4,g8)
    c: Horizontal(g8,g5)
    c: Coincident(g9,g8)
    c: Coincident(g9,g4)
    c: Coincident(g10,g8)
    c: Coincident(g10,g5)
    c: Symmetric(g4,g5,g-1)
    c: Coincident(g11,g0)
    c: Horizontal(g11)
    c: Symmetric(g0,g0,g-1)
    c: Coincident(g11,g7)
    c: Coincident(g1,g6)
    c: Equal(g11,g1)
    c: DistanceX(g11,g11) = 3
FEATURE [Sketcher::SketchObject] Sketch006  label="clip mount"
  FullyConstrained = true
  MapMode = 5
  Support = -> [XY_Plane]
  expr: Constraints[9] = Spreadsheet.clipIndent + Spreadsheet.clipWidth
  expr: Constraints[10] = Spreadsheet.clipHeight
  sketch-geometry (8):
    g0: LineSegment StartX=0 StartY=-41 StartZ=0 EndX=5 EndY=-41 EndZ=0
    g1: LineSegment StartX=5 StartY=-41 StartZ=0 EndX=5 EndY=-49 EndZ=0
    g2: LineSegment StartX=5 StartY=-49 StartZ=0 EndX=0 EndY=-49 EndZ=0
    g3: LineSegment StartX=0 StartY=-49 StartZ=0 EndX=0 EndY=-41 EndZ=0
    g4: LineSegment StartX=0 StartY=29 StartZ=0 EndX=5 EndY=29 EndZ=0
    g5: LineSegment StartX=5 StartY=29 StartZ=0 EndX=5 EndY=21 EndZ=0
    g6: LineSegment StartX=5 StartY=21 StartZ=0 EndX=0 EndY=21 EndZ=0
    g7: LineSegment StartX=0 StartY=21 StartZ=0 EndX=0 EndY=29 EndZ=0
  constraints (24):
    c: Coincident(g0,g1)
    c: Coincident(g1,g2)
    c: Coincident(g2,g3)
    c: Coincident(g3,g0)
    c: Horizontal(g0)
    c: Horizontal(g2)
    c: Vertical(g1)
    c: Vertical(g3)
    c: PointOnObject(g0,g-2)
    c: DistanceX(g2,g2) = 5
    c: DistanceY(g1,g1) = 8
    c: DistanceY(g0,g-1) = 41
    c: Coincident(g4,g5)
    c: Coincident(g5,g6)
    c: Coincident(g6,g7)
    c: Coincident(g7,g4)
    c: Horizontal(g4)
    c: Horizontal(g6)
    c: Vertical(g5)
    c: Vertical(g7)
    c: PointOnObject(g4,g-2)
    c: Equal(g2,g4)
    c: Equal(g1,g5)
    c: DistanceY(g4,g-1) = -29
FEATURE [PartDesign::Pocket] Pocket004
  BaseFeature = -> Pocket003
  Length = 1
  Length2 = 100
  Profile = -> Sketch006
  Type = 0
FEATURE [PartDesign::Pad] Pad001  label="Clip"
  Direction = (1,1,1)
  Length = 7.8
  Length2 = 100
  Profile = -> Sketch005
  Type = 0
FEATURE [PartDesign::Body] Body001  label="String Clip"
  Group = -> [Sketch005,Pad001]
  Origin = -> Origin001
  Tip = -> Pad001
FEATURE [Sketcher::SketchObject] Sketch007
  FullyConstrained = true
  MapMode = 5
  Support = -> [XY_Plane]
  expr: Constraints[9] = Spreadsheet.clipIndent
  expr: Constraints[8] = Spreadsheet.clipHeight
  sketch-geometry (8):
    g0: LineSegment StartX=0 StartY=-41 StartZ=0 EndX=2 EndY=-41 EndZ=0
    g1: LineSegment StartX=2 StartY=-41 StartZ=0 EndX=2 EndY=-49 EndZ=0
    g2: LineSegment StartX=2 StartY=-49 StartZ=0 EndX=0 EndY=-49 EndZ=0
    g3: LineSegment StartX=0 StartY=-49 StartZ=0 EndX=0 EndY=-41 EndZ=0
    g4: LineSegment StartX=0 StartY=29 StartZ=0 EndX=2 EndY=29 EndZ=0
    g5: LineSegment StartX=2 StartY=29 StartZ=0 EndX=2 EndY=21 EndZ=0
    g6: LineSegment StartX=2 StartY=21 StartZ=0 EndX=0 EndY=21 EndZ=0
    g7: LineSegment StartX=0 StartY=21 StartZ=0 EndX=0 EndY=29 EndZ=0
  constraints (24):
    c: Coincident(g0,g1)
    c: Coincident(g1,g2)
    c: Coincident(g2,g3)
    c: Coincident(g3,g0)
    c: Horizontal(g0)
    c: Horizontal(g2)
    c: Vertical(g1)
    c: Vertical(g3)
    c: DistanceY(g3,g3) = 8
    c: DistanceX(g0,g0) = 2
    c: Coincident(g4,g5)
    c: Coincident(g5,g6)
    c: Coincident(g6,g7)
    c: Coincident(g7,g4)
    c: Horizontal(g4)
    c: Horizontal(g6)
    c: Vertical(g5)
    c: Vertical(g7)
    c: Equal(g4,g2)
    c: Equal(g3,g7)
    c: Vertical(g2,g4)
    c: PointOnObject(g0,g-2)
    c: DistanceY(g0,g-1) = 41
    c: DistanceY(g4,g-1) = -29
FEATURE [PartDesign::Pocket] Pocket005
  BaseFeature = -> Pocket004
  Length = 5
  Length2 = 100
  Profile = -> Sketch007
  Type = 1
FEATURE [PartDesign::Plane] DatumPlane
  AttachmentOffset = pos=(0,0,-3) rot=(0,0,1;0rad)
  Length = 294.12
  MapMode = 2
  Placement = pos=(0,0,-3) rot=(0,0,1;0rad)
  ResizeMode = 0
  Support = -> [XY_Plane]
  Width = 109.12
FEATURE [Sketcher::SketchObject] Sketch008  label="hz cm001"
  FullyConstrained = false
  MapMode = 5
  Placement = pos=(0,0,-3) rot=(0,0,1;0rad)
  Support = -> [DatumPlane]
  expr: Constraints[8] = Spreadsheet.reticleCmHeight
  expr: Constraints[9] = Spreadsheet.reticleCmWidth
  sketch-geometry (171):
    g0: LineSegment StartX=239.9 StartY=-20 StartZ=0 EndX=239.7 EndY=-20 EndZ=0
    g1: LineSegment StartX=239.7 StartY=-20 StartZ=0 EndX=239.7 EndY=-16 EndZ=0
    g2: LineSegment StartX=239.7 StartY=-16 StartZ=0 EndX=239.9 EndY=-16 EndZ=0
    g3: LineSegment StartX=239.9 StartY=-16 StartZ=0 EndX=239.9 EndY=-20 EndZ=0
    g4: LineSegment StartX=-7.75171 StartY=-20 StartZ=0 EndX=225.791 EndY=-20 EndZ=0
    g5: LineSegment StartX=229.9 StartY=-20 StartZ=0 EndX=229.7 EndY=-20 EndZ=0
    g6: LineSegment StartX=229.7 StartY=-20 StartZ=0 EndX=229.7 EndY=-16 EndZ=0
    g7: LineSegment StartX=229.7 StartY=-16 StartZ=0 EndX=229.9 EndY=-16 EndZ=0
    g8: LineSegment StartX=229.9 StartY=-16 StartZ=0 EndX=229.9 EndY=-20 EndZ=0
    g9: LineSegment StartX=239.9 StartY=-20 StartZ=0 EndX=229.9 EndY=-20 EndZ=0
    g10: LineSegment StartX=219.9 StartY=-20 StartZ=0 EndX=219.7 EndY=-20 EndZ=0
    g11: LineSegment StartX=219.7 StartY=-20 StartZ=0 EndX=219.7 EndY=-16 EndZ=0
    g12: LineSegment StartX=219.7 StartY=-16 StartZ=0 EndX=219.9 EndY=-16 EndZ=0
    g13: LineSegment StartX=219.9 StartY=-16 StartZ=0 EndX=219.9 EndY=-20 EndZ=0
    g14: LineSegment StartX=229.9 StartY=-20 StartZ=0 EndX=219.9 EndY=-20 EndZ=0
    g15: LineSegment StartX=209.9 StartY=-20 StartZ=0 EndX=209.7 EndY=-20 EndZ=0
    g16: LineSegment StartX=209.7 StartY=-20 StartZ=0 EndX=209.7 EndY=-16 EndZ=0
    g17: LineSegment StartX=209.7 StartY=-16 StartZ=0 EndX=209.9 EndY=-16 EndZ=0
    g18: LineSegment StartX=209.9 StartY=-16 StartZ=0 EndX=209.9 EndY=-20 EndZ=0
    g19: LineSegment StartX=219.9 StartY=-20 StartZ=0 EndX=209.9 EndY=-20 EndZ=0
    g20: LineSegment StartX=199.9 StartY=-20 StartZ=0 EndX=199.7 EndY=-20 EndZ=0
    g21: LineSegment StartX=199.7 StartY=-20 StartZ=0 EndX=199.7 EndY=-16 EndZ=0
    g22: LineSegment StartX=199.7 StartY=-16 StartZ=0 EndX=199.9 EndY=-16 EndZ=0
    g23: LineSegment StartX=199.9 StartY=-16 StartZ=0 EndX=199.9 EndY=-20 EndZ=0
    g24: LineSegment StartX=209.9 StartY=-20 StartZ=0 EndX=199.9 EndY=-20 EndZ=0
    g25: LineSegment StartX=189.9 StartY=-20 StartZ=0 EndX=189.7 EndY=-20 EndZ=0
    g26: LineSegment StartX=189.7 StartY=-20 StartZ=0 EndX=189.7 EndY=-16 EndZ=0
    g27: LineSegment StartX=189.7 StartY=-16 StartZ=0 EndX=189.9 EndY=-16 EndZ=0
    g28: LineSegment StartX=189.9 StartY=-16 StartZ=0 EndX=189.9 EndY=-20 EndZ=0
    g29: LineSegment StartX=199.9 StartY=-20 StartZ=0 EndX=189.9 EndY=-20 EndZ=0
    g30: LineSegment StartX=179.9 StartY=-20 StartZ=0 EndX=179.7 EndY=-20 EndZ=0
    g31: LineSegment StartX=179.7 StartY=-20 StartZ=0 EndX=179.7 EndY=-16 EndZ=0
    g32: LineSegment StartX=179.7 StartY=-16 StartZ=0 EndX=179.9 EndY=-16 EndZ=0
    g33: LineSegment StartX=179.9 StartY=-16 StartZ=0 EndX=179.9 EndY=-20 EndZ=0
    g34: LineSegment StartX=189.9 StartY=-20 StartZ=0 EndX=179.9 EndY=-20 EndZ=0
    g35: LineSegment StartX=169.9 StartY=-20 StartZ=0 EndX=169.7 EndY=-20 EndZ=0
    g36: LineSegment StartX=169.7 StartY=-20 StartZ=0 EndX=169.7 EndY=-16 EndZ=0
    g37: LineSegment StartX=169.7 StartY=-16 StartZ=0 EndX=169.9 EndY=-16 EndZ=0
    g38: LineSegment StartX=169.9 StartY=-16 StartZ=0 EndX=169.9 EndY=-20 EndZ=0
    g39: LineSegment StartX=179.9 StartY=-20 StartZ=0 EndX=169.9 EndY=-20 EndZ=0
    g40: LineSegment StartX=159.9 StartY=-20 StartZ=0 EndX=159.7 EndY=-20 EndZ=0
    g41: LineSegment StartX=159.7 StartY=-20 StartZ=0 EndX=159.7 EndY=-16 EndZ=0
    g42: LineSegment StartX=159.7 StartY=-16 StartZ=0 EndX=159.9 EndY=-16 EndZ=0
    g43: LineSegment StartX=159.9 StartY=-16 StartZ=0 EndX=159.9 EndY=-20 EndZ=0
    g44: LineSegment StartX=169.9 StartY=-20 StartZ=0 EndX=159.9 EndY=-20 EndZ=0
    g45: LineSegment StartX=149.9 StartY=-20 StartZ=0 EndX=149.7 EndY=-20 EndZ=0
    g46: LineSegment StartX=149.7 StartY=-20 StartZ=0 EndX=149.7 EndY=-16 EndZ=0
    g47: LineSegment StartX=149.7 StartY=-16 StartZ=0 EndX=149.9 EndY=-16 EndZ=0
    g48: LineSegment StartX=149.9 StartY=-16 StartZ=0 EndX=149.9 EndY=-20 EndZ=0
    g49: LineSegment StartX=159.9 StartY=-20 StartZ=0 EndX=149.9 EndY=-20 EndZ=0
    g50: LineSegment StartX=139.9 StartY=-20 StartZ=0 EndX=139.7 EndY=-20 EndZ=0
    g51: LineSegment StartX=139.7 StartY=-20 StartZ=0 EndX=139.7 EndY=-16 EndZ=0
    g52: LineSegment StartX=139.7 StartY=-16 StartZ=0 EndX=139.9 EndY=-16 EndZ=0
    g53: LineSegment StartX=139.9 StartY=-16 StartZ=0 EndX=139.9 EndY=-20 EndZ=0
    g54: LineSegment StartX=149.9 StartY=-20 StartZ=0 EndX=139.9 EndY=-20 EndZ=0
    g55: LineSegment StartX=129.9 StartY=-20 StartZ=0 EndX=129.7 EndY=-20 EndZ=0
    g56: LineSegment StartX=129.7 StartY=-20 StartZ=0 EndX=129.7 EndY=-16 EndZ=0
    g57: LineSegment StartX=129.7 StartY=-16 StartZ=0 EndX=129.9 EndY=-16 EndZ=0
    g58: LineSegment StartX=129.9 StartY=-16 StartZ=0 EndX=129.9 EndY=-20 EndZ=0
    g59: LineSegment StartX=139.9 StartY=-20 StartZ=0 EndX=129.9 EndY=-20 EndZ=0
    g60: LineSegment StartX=119.9 StartY=-20 StartZ=0 EndX=119.7 EndY=-20 EndZ=0
    g61: LineSegment StartX=119.7 StartY=-20 StartZ=0 EndX=119.7 EndY=-16 EndZ=0
    g62: LineSegment StartX=119.7 StartY=-16 StartZ=0 EndX=119.9 EndY=-16 EndZ=0
    g63: LineSegment StartX=119.9 StartY=-16 StartZ=0 EndX=119.9 EndY=-20 EndZ=0
    g64: LineSegment StartX=129.9 StartY=-20 StartZ=0 EndX=119.9 EndY=-20 EndZ=0
    g65: LineSegment StartX=109.9 StartY=-20 StartZ=0 EndX=109.7 EndY=-20 EndZ=0
    g66: LineSegment StartX=109.7 StartY=-20 StartZ=0 EndX=109.7 EndY=-16 EndZ=0
    g67: LineSegment StartX=109.7 StartY=-16 StartZ=0 EndX=109.9 EndY=-16 EndZ=0
    g68: LineSegment StartX=109.9 StartY=-16 StartZ=0 EndX=109.9 EndY=-20 EndZ=0
    g69: LineSegment StartX=119.9 StartY=-20 StartZ=0 EndX=109.9 EndY=-20 EndZ=0
    g70: LineSegment StartX=99.9 StartY=-20 StartZ=0 EndX=99.7 EndY=-20 EndZ=0
    g71: LineSegment StartX=99.7 StartY=-20 StartZ=0 EndX=99.7 EndY=-16 EndZ=0
    g72: LineSegment StartX=99.7 StartY=-16 StartZ=0 EndX=99.9 EndY=-16 EndZ=0
    g73: LineSegment StartX=99.9 StartY=-16 StartZ=0 EndX=99.9 EndY=-20 EndZ=0
    g74: LineSegment StartX=109.9 StartY=-20 StartZ=0 EndX=99.9 EndY=-20 EndZ=0
    g75: LineSegment StartX=89.9 StartY=-20 StartZ=0 EndX=89.7 EndY=-20 EndZ=0
    g76: LineSegment StartX=89.7 StartY=-20 StartZ=0 EndX=89.7 EndY=-16 EndZ=0
    g77: LineSegment StartX=89.7 StartY=-16 StartZ=0 EndX=89.9 EndY=-16 EndZ=0
    g78: LineSegment StartX=89.9 StartY=-16 StartZ=0 EndX=89.9 EndY=-20 EndZ=0
    g79: LineSegment StartX=99.9 StartY=-20 StartZ=0 EndX=89.9 EndY=-20 EndZ=0
    g80: LineSegment StartX=79.9 StartY=-20 StartZ=0 EndX=79.7 EndY=-20 EndZ=0
    g81: LineSegment StartX=79.7 StartY=-20 StartZ=0 EndX=79.7 EndY=-16 EndZ=0
    g82: LineSegment StartX=79.7 StartY=-16 StartZ=0 EndX=79.9 EndY=-16 EndZ=0
    g83: LineSegment StartX=79.9 StartY=-16 StartZ=0 EndX=79.9 EndY=-20 EndZ=0
    g84: LineSegment StartX=89.9 StartY=-20 StartZ=0 EndX=79.9 EndY=-20 EndZ=0
    g85: LineSegment StartX=79.9 StartY=-20 StartZ=0 EndX=69.9 EndY=-20 EndZ=0
    g86: LineSegment StartX=239.7 StartY=-4 StartZ=0 EndX=239.9 EndY=-4 EndZ=0
    g87: LineSegment StartX=239.9 StartY=-4 StartZ=0 EndX=239.9 EndY=0 EndZ=0
    g88: LineSegment StartX=239.9 StartY=0 StartZ=0 EndX=239.7 EndY=0 EndZ=0
    g89: LineSegment StartX=239.7 StartY=0 StartZ=0 EndX=239.7 EndY=-4 EndZ=0
    g90: LineSegment StartX=229.7 StartY=-4 StartZ=0 EndX=229.5 EndY=-4 EndZ=0
    g91: LineSegment StartX=229.5 StartY=-4 StartZ=0 EndX=229.5 EndY=1.3e-15 EndZ=0
    g92: LineSegment StartX=229.5 StartY=1.3e-15 StartZ=0 EndX=229.7 EndY=1.3e-15 EndZ=0
    g93: LineSegment StartX=229.7 StartY=1.3e-15 StartZ=0 EndX=229.7 EndY=-4 EndZ=0
    g94: LineSegment StartX=239.7 StartY=-4 StartZ=0 EndX=229.7 EndY=-4 EndZ=0
    g95: LineSegment StartX=219.7 StartY=-4 StartZ=0 EndX=219.5 EndY=-4 EndZ=0
    g96: LineSegment StartX=219.5 StartY=-4 StartZ=0 EndX=219.5 EndY=2.2e-15 EndZ=0
    g97: LineSegment StartX=219.5 StartY=2.2e-15 StartZ=0 EndX=219.7 EndY=2.2e-15 EndZ=0
    g98: LineSegment StartX=219.7 StartY=2.2e-15 StartZ=0 EndX=219.7 EndY=-4 EndZ=0
    g99: LineSegment StartX=229.7 StartY=-4 StartZ=0 EndX=219.7 EndY=-4 EndZ=0
    g100: LineSegment StartX=209.7 StartY=-4 StartZ=0 EndX=209.5 EndY=-4 EndZ=0
    g101: LineSegment StartX=209.5 StartY=-4 StartZ=0 EndX=209.5 EndY=3.6e-15 EndZ=0
    g102: LineSegment StartX=209.5 StartY=3.6e-15 StartZ=0 EndX=209.7 EndY=3.6e-15 EndZ=0
    g103: LineSegment StartX=209.7 StartY=3.6e-15 StartZ=0 EndX=209.7 EndY=-4 EndZ=0
    g104: LineSegment StartX=219.7 StartY=-4 StartZ=0 EndX=209.7 EndY=-4 EndZ=0
    g105: LineSegment StartX=199.7 StartY=-4 StartZ=0 EndX=199.5 EndY=-4 EndZ=0
    g106: LineSegment StartX=199.5 StartY=-4 StartZ=0 EndX=199.5 EndY=4.9e-15 EndZ=0
    g107: LineSegment StartX=199.5 StartY=4.9e-15 StartZ=0 EndX=199.7 EndY=4.9e-15 EndZ=0
    g108: LineSegment StartX=199.7 StartY=4.9e-15 StartZ=0 EndX=199.7 EndY=-4 EndZ=0
    g109: LineSegment StartX=209.7 StartY=-4 StartZ=0 EndX=199.7 EndY=-4 EndZ=0
    g110: LineSegment StartX=189.7 StartY=-4 StartZ=0 EndX=189.5 EndY=-4 EndZ=0
    g111: LineSegment StartX=189.5 StartY=-4 StartZ=0 EndX=189.5 EndY=6.2e-15 EndZ=0
    g112: LineSegment StartX=189.5 StartY=6.2e-15 StartZ=0 EndX=189.7 EndY=6.2e-15 EndZ=0
    g113: LineSegment StartX=189.7 StartY=6.2e-15 StartZ=0 EndX=189.7 EndY=-4 EndZ=0
    g114: LineSegment StartX=199.7 StartY=-4 StartZ=0 EndX=189.7 EndY=-4 EndZ=0
    g115: LineSegment StartX=179.7 StartY=-4 StartZ=0 EndX=179.5 EndY=-4 EndZ=0
    g116: LineSegment StartX=179.5 StartY=-4 StartZ=0 EndX=179.5 EndY=7.5e-15 EndZ=0
    g117: LineSegment StartX=179.5 StartY=7.5e-15 StartZ=0 EndX=179.7 EndY=7.5e-15 EndZ=0
    g118: LineSegment StartX=179.7 StartY=7.5e-15 StartZ=0 EndX=179.7 EndY=-4 EndZ=0
    g119: LineSegment StartX=189.7 StartY=-4 StartZ=0 EndX=179.7 EndY=-4 EndZ=0
    g120: LineSegment StartX=169.7 StartY=-4 StartZ=0 EndX=169.5 EndY=-4 EndZ=0
    g121: LineSegment StartX=169.5 StartY=-4 StartZ=0 EndX=169.5 EndY=8.4e-15 EndZ=0
    g122: LineSegment StartX=169.5 StartY=8.4e-15 StartZ=0 EndX=169.7 EndY=8.4e-15 EndZ=0
    g123: LineSegment StartX=169.7 StartY=8.4e-15 StartZ=0 EndX=169.7 EndY=-4 EndZ=0
    g124: LineSegment StartX=179.7 StartY=-4 StartZ=0 EndX=169.7 EndY=-4 EndZ=0
    g125: LineSegment StartX=159.7 StartY=-4 StartZ=0 EndX=159.5 EndY=-4 EndZ=0
    g126: LineSegment StartX=159.5 StartY=-4 StartZ=0 EndX=159.5 EndY=9.8e-15 EndZ=0
    g127: LineSegment StartX=159.5 StartY=9.8e-15 StartZ=0 EndX=159.7 EndY=9.8e-15 EndZ=0
    g128: LineSegment StartX=159.7 StartY=9.8e-15 StartZ=0 EndX=159.7 EndY=-4 EndZ=0
    g129: LineSegment StartX=169.7 StartY=-4 StartZ=0 EndX=159.7 EndY=-4 EndZ=0
    g130: LineSegment StartX=149.7 StartY=-4 StartZ=0 EndX=149.5 EndY=-4 EndZ=0
    g131: LineSegment StartX=149.5 StartY=-4 StartZ=0 EndX=149.5 EndY=1.11e-14 EndZ=0
    g132: LineSegment StartX=149.5 StartY=1.11e-14 StartZ=0 EndX=149.7 EndY=1.11e-14 EndZ=0
    g133: LineSegment StartX=149.7 StartY=1.11e-14 StartZ=0 EndX=149.7 EndY=-4 EndZ=0
    g134: LineSegment StartX=159.7 StartY=-4 StartZ=0 EndX=149.7 EndY=-4 EndZ=0
    g135: LineSegment StartX=139.7 StartY=-4 StartZ=0 EndX=139.5 EndY=-4 EndZ=0
    g136: LineSegment StartX=139.5 StartY=-4 StartZ=0 EndX=139.5 EndY=1.24e-14 EndZ=0
    g137: LineSegment StartX=139.5 StartY=1.24e-14 StartZ=0 EndX=139.7 EndY=1.24e-14 EndZ=0
    g138: LineSegment StartX=139.7 StartY=1.24e-14 StartZ=0 EndX=139.7 EndY=-4 EndZ=0
    g139: LineSegment StartX=149.7 StartY=-4 StartZ=0 EndX=139.7 EndY=-4 EndZ=0
    g140: LineSegment StartX=129.7 StartY=-4 StartZ=0 EndX=129.5 EndY=-4 EndZ=0
    g141: LineSegment StartX=129.5 StartY=-4 StartZ=0 EndX=129.5 EndY=1.33e-14 EndZ=0
    g142: LineSegment StartX=129.5 StartY=1.33e-14 StartZ=0 EndX=129.7 EndY=1.33e-14 EndZ=0
    g143: LineSegment StartX=129.7 StartY=1.33e-14 StartZ=0 EndX=129.7 EndY=-4 EndZ=0
    g144: LineSegment StartX=139.7 StartY=-4 StartZ=0 EndX=129.7 EndY=-4 EndZ=0
    g145: LineSegment StartX=119.7 StartY=-4 StartZ=0 EndX=119.5 EndY=-4 EndZ=0
    g146: LineSegment StartX=119.5 StartY=-4 StartZ=0 EndX=119.5 EndY=1.47e-14 EndZ=0
    g147: LineSegment StartX=119.5 StartY=1.47e-14 StartZ=0 EndX=119.7 EndY=1.47e-14 EndZ=0
    g148: LineSegment StartX=119.7 StartY=1.47e-14 StartZ=0 EndX=119.7 EndY=-4 EndZ=0
    g149: LineSegment StartX=129.7 StartY=-4 StartZ=0 EndX=119.7 EndY=-4 EndZ=0
    g150: LineSegment StartX=109.7 StartY=-4 StartZ=0 EndX=109.5 EndY=-4 EndZ=0
    g151: LineSegment StartX=109.5 StartY=-4 StartZ=0 EndX=109.5 EndY=1.6e-14 EndZ=0
    g152: LineSegment StartX=109.5 StartY=1.6e-14 StartZ=0 EndX=109.7 EndY=1.6e-14 EndZ=0
    g153: LineSegment StartX=109.7 StartY=1.6e-14 StartZ=0 EndX=109.7 EndY=-4 EndZ=0
    g154: LineSegment StartX=119.7 StartY=-4 StartZ=0 EndX=109.7 EndY=-4 EndZ=0
    g155: LineSegment StartX=99.7 StartY=-4 StartZ=0 EndX=99.5 EndY=-4 EndZ=0
    g156: LineSegment StartX=99.5 StartY=-4 StartZ=0 EndX=99.5 EndY=1.69e-14 EndZ=0
    g157: LineSegment StartX=99.5 StartY=1.69e-14 StartZ=0 EndX=99.7 EndY=1.69e-14 EndZ=0
    g158: LineSegment StartX=99.7 StartY=1.69e-14 StartZ=0 EndX=99.7 EndY=-4 EndZ=0
    g159: LineSegment StartX=109.7 StartY=-4 StartZ=0 EndX=99.7 EndY=-4 EndZ=0
    g160: LineSegment StartX=89.7 StartY=-4 StartZ=0 EndX=89.5 EndY=-4 EndZ=0
    g161: LineSegment StartX=89.5 StartY=-4 StartZ=0 EndX=89.5 EndY=1.82e-14 EndZ=0
    g162: LineSegment StartX=89.5 StartY=1.82e-14 StartZ=0 EndX=89.7 EndY=1.82e-14 EndZ=0
    g163: LineSegment StartX=89.7 StartY=1.82e-14 StartZ=0 EndX=89.7 EndY=-4 EndZ=0
    g164: LineSegment StartX=99.7 StartY=-4 StartZ=0 EndX=89.7 EndY=-4 EndZ=0
    g165: LineSegment StartX=79.7 StartY=-4 StartZ=0 EndX=79.5 EndY=-4 EndZ=0
    g166: LineSegment StartX=79.5 StartY=-4 StartZ=0 EndX=79.5 EndY=1.95e-14 EndZ=0
    g167: LineSegment StartX=79.5 StartY=1.95e-14 StartZ=0 EndX=79.7 EndY=1.95e-14 EndZ=0
    g168: LineSegment StartX=79.7 StartY=1.95e-14 StartZ=0 EndX=79.7 EndY=-4 EndZ=0
    g169: LineSegment StartX=89.7 StartY=-4 StartZ=0 EndX=79.7 EndY=-4 EndZ=0
    g170: LineSegment StartX=79.7 StartY=-4 StartZ=0 EndX=69.7 EndY=-4 EndZ=0
  constraints (480):
    c: Coincident(g0,g1)
    c: Coincident(g1,g2)
    c: Coincident(g2,g3)
    c: Coincident(g3,g0)
    c: Horizontal(g0)
    c: Horizontal(g2)
    c: Vertical(g1)
    c: Vertical(g3)
    c: DistanceY(g3,g3) = 4
    c: DistanceX(g2,g2) = 0.2
    c: Horizontal(g4)
    c: DistanceY(g4,g-1) = 20
    c: PointOnObject(g0,g4)
    c: Coincident(g5,g6)
    c: Coincident(g6,g7)
    c: Coincident(g7,g8)
    c: Coincident(g8,g5)
    c: Horizontal(g5)
    c: Horizontal(g7)
    c: Vertical(g6)
    c: Vertical(g8)
    c: Equal(g3,g8) = 4
    c: Equal(g2,g7) = 0.35
    c: Coincident(g0,g9)
    c: Coincident(g5,g9)
    c: Distance(g9) = 10
    c: Angle(g9) = 3.14159
    c: Coincident(g10,g11)
    c: Coincident(g11,g12)
    c: Coincident(g12,g13)
    c: Coincident(g13,g10)
    c: Horizontal(g10)
    c: Horizontal(g12)
    c: Vertical(g11)
    c: Vertical(g13)
    c: Equal(g3,g13) = 4
    c: Equal(g2,g12) = 0.35
    c: Coincident(g5,g14)
    c: Coincident(g10,g14)
    c: Equal(g9,g14)
    c: Parallel(g14,g9)
    c: Coincident(g15,g16)
    c: Coincident(g16,g17)
    c: Coincident(g17,g18)
    c: Coincident(g18,g15)
    c: Horizontal(g15)
    c: Horizontal(g17)
    c: Vertical(g16)
    c: Vertical(g18)
    c: Equal(g3,g18) = 4
    c: Equal(g2,g17) = 0.35
    c: Coincident(g10,g19)
    c: Coincident(g15,g19)
    c: Equal(g9,g19)
    c: Parallel(g19,g9)
    c: Coincident(g20,g21)
    c: Coincident(g21,g22)
    c: Coincident(g22,g23)
    c: Coincident(g23,g20)
    c: Horizontal(g20)
    c: Horizontal(g22)
    c: Vertical(g21)
    c: Vertical(g23)
    c: Equal(g3,g23) = 4
    c: Equal(g2,g22) = 0.35
    c: Coincident(g15,g24)
    c: Coincident(g20,g24)
    c: Equal(g9,g24)
    c: Parallel(g24,g9)
    c: Coincident(g25,g26)
    c: Coincident(g26,g27)
    c: Coincident(g27,g28)
    c: Coincident(g28,g25)
    c: Horizontal(g25)
    c: Horizontal(g27)
    c: Vertical(g26)
    c: Vertical(g28)
    c: Equal(g3,g28) = 4
    c: Equal(g2,g27) = 0.35
    c: Coincident(g20,g29)
    c: Coincident(g25,g29)
    c: Equal(g9,g29)
    c: Parallel(g29,g9)
    c: Coincident(g30,g31)
    c: Coincident(g31,g32)
    c: Coincident(g32,g33)
    c: Coincident(g33,g30)
    c: Horizontal(g30)
    c: Horizontal(g32)
    c: Vertical(g31)
    c: Vertical(g33)
    c: Equal(g3,g33) = 4
    c: Equal(g2,g32) = 0.35
    c: Coincident(g25,g34)
    c: Coincident(g30,g34)
    c: Equal(g9,g34)
    c: Parallel(g34,g9)
    c: Coincident(g35,g36)
    c: Coincident(g36,g37)
    c: Coincident(g37,g38)
    c: Coincident(g38,g35)
    c: Horizontal(g35)
    c: Horizontal(g37)
    c: Vertical(g36)
    c: Vertical(g38)
    c: Equal(g3,g38) = 4
    c: Equal(g2,g37) = 0.35
    c: Coincident(g30,g39)
    c: Coincident(g35,g39)
    c: Equal(g9,g39)
    c: Parallel(g39,g9)
    c: Coincident(g40,g41)
    c: Coincident(g41,g42)
    c: Coincident(g42,g43)
    c: Coincident(g43,g40)
    c: Horizontal(g40)
    c: Horizontal(g42)
    c: Vertical(g41)
    c: Vertical(g43)
    c: Equal(g3,g43) = 4
    c: Equal(g2,g42) = 0.35
    c: Coincident(g35,g44)
    c: Coincident(g40,g44)
    c: Equal(g9,g44)
    c: Parallel(g44,g9)
    c: Coincident(g45,g46)
    c: Coincident(g46,g47)
    c: Coincident(g47,g48)
    c: Coincident(g48,g45)
    c: Horizontal(g45)
    c: Horizontal(g47)
    c: Vertical(g46)
    c: Vertical(g48)
    c: Equal(g3,g48) = 4
    c: Equal(g2,g47) = 0.35
    c: Coincident(g40,g49)
    c: Coincident(g45,g49)
    c: Equal(g9,g49)
    c: Parallel(g49,g9)
    c: Coincident(g50,g51)
    c: Coincident(g51,g52)
    c: Coincident(g52,g53)
    c: Coincident(g53,g50)
    c: Horizontal(g50)
    c: Horizontal(g52)
    c: Vertical(g51)
    c: Vertical(g53)
    c: Equal(g3,g53) = 4
    c: Equal(g2,g52) = 0.35
    c: Coincident(g45,g54)
    c: Coincident(g50,g54)
    c: Equal(g9,g54)
    c: Parallel(g54,g9)
    c: Coincident(g55,g56)
    c: Coincident(g56,g57)
    c: Coincident(g57,g58)
    c: Coincident(g58,g55)
    c: Horizontal(g55)
    c: Horizontal(g57)
    c: Vertical(g56)
    c: Vertical(g58)
    c: Equal(g3,g58) = 4
    c: Equal(g2,g57) = 0.35
    c: Coincident(g50,g59)
    c: Coincident(g55,g59)
    c: Equal(g9,g59)
    c: Parallel(g59,g9)
    c: Coincident(g60,g61)
    c: Coincident(g61,g62)
    c: Coincident(g62,g63)
    c: Coincident(g63,g60)
    c: Horizontal(g60)
    c: Horizontal(g62)
    c: Vertical(g61)
    c: Vertical(g63)
    c: Equal(g3,g63) = 4
    c: Equal(g2,g62) = 0.35
    c: Coincident(g55,g64)
    c: Coincident(g60,g64)
    c: Equal(g9,g64)
    c: Parallel(g64,g9)
    c: Coincident(g65,g66)
    c: Coincident(g66,g67)
    c: Coincident(g67,g68)
    c: Coincident(g68,g65)
    c: Horizontal(g65)
    c: Horizontal(g67)
    c: Vertical(g66)
    c: Vertical(g68)
    c: Equal(g3,g68) = 4
    c: Equal(g2,g67) = 0.35
    c: Coincident(g60,g69)
    c: Coincident(g65,g69)
    c: Equal(g9,g69)
    c: Parallel(g69,g9)
    c: Coincident(g70,g71)
    c: Coincident(g71,g72)
    c: Coincident(g72,g73)
    c: Coincident(g73,g70)
    c: Horizontal(g70)
    c: Horizontal(g72)
    c: Vertical(g71)
    c: Vertical(g73)
    c: Equal(g3,g73) = 4
    c: Equal(g2,g72) = 0.35
    c: Coincident(g65,g74)
    c: Coincident(g70,g74)
    c: Equal(g9,g74)
    c: Parallel(g74,g9)
    c: Coincident(g75,g76)
    c: Coincident(g76,g77)
    c: Coincident(g77,g78)
    c: Coincident(g78,g75)
    c: Horizontal(g75)
    c: Horizontal(g77)
    c: Vertical(g76)
    c: Vertical(g78)
    c: Equal(g3,g78) = 4
    c: Equal(g2,g77) = 0.35
    c: Coincident(g70,g79)
    c: Coincident(g75,g79)
    c: Equal(g9,g79)
    c: Parallel(g79,g9)
    c: Coincident(g80,g81)
    c: Coincident(g81,g82)
    c: Coincident(g82,g83)
    c: Coincident(g83,g80)
    c: Horizontal(g80)
    c: Horizontal(g82)
    c: Vertical(g81)
    c: Vertical(g83)
    c: Equal(g3,g83) = 4
    c: Equal(g2,g82) = 0.35
    c: Coincident(g75,g84)
    c: Coincident(g80,g84)
    c: Equal(g9,g84)
    c: Parallel(g84,g9)
    c: Coincident(g80,g85)
    c: Equal(g9,g85)
    c: Parallel(g85,g9)
    c: Coincident(g86,g87)
    c: Coincident(g87,g88)
    c: Coincident(g88,g89)
    c: Coincident(g89,g86)
    c: Horizontal(g86)
    c: Horizontal(g88)
    c: Vertical(g87)
    c: Vertical(g89)
    c: Equal(g3,g89) = 4
    c: Equal(g2,g88) = 0.35
    c: Coincident(g90,g91)
    c: Coincident(g91,g92)
    c: Coincident(g92,g93)
    c: Coincident(g93,g90)
    c: Horizontal(g90)
    c: Horizontal(g92)
    c: Vertical(g91)
    c: Vertical(g93)
    c: Equal(g3,g93) = 4
    c: Equal(g2,g92) = 0.35
    c: Coincident(g86,g94)
    c: Coincident(g90,g94)
    c: Equal(g9,g94)
    c: Parallel(g94,g9)
    c: Coincident(g95,g96)
    c: Coincident(g96,g97)
    c: Coincident(g97,g98)
    c: Coincident(g98,g95)
    c: Horizontal(g95)
    c: Horizontal(g97)
    c: Vertical(g96)
    c: Vertical(g98)
    c: Equal(g3,g98) = 4
    c: Equal(g2,g97) = 0.35
    c: Coincident(g90,g99)
    c: Coincident(g95,g99)
    c: Equal(g9,g99)
    c: Parallel(g99,g9)
    c: Coincident(g100,g101)
    c: Coincident(g101,g102)
    c: Coincident(g102,g103)
    c: Coincident(g103,g100)
    c: Horizontal(g100)
    c: Horizontal(g102)
    c: Vertical(g101)
    c: Vertical(g103)
    c: Equal(g3,g103) = 4
    c: Equal(g2,g102) = 0.35
    c: Coincident(g95,g104)
    c: Coincident(g100,g104)
    c: Equal(g9,g104)
    c: Parallel(g104,g9)
    c: Coincident(g105,g106)
    c: Coincident(g106,g107)
    c: Coincident(g107,g108)
    c: Coincident(g108,g105)
    c: Horizontal(g105)
    c: Horizontal(g107)
    c: Vertical(g106)
    c: Vertical(g108)
    c: Equal(g3,g108) = 4
    c: Equal(g2,g107) = 0.35
    c: Coincident(g100,g109)
    c: Coincident(g105,g109)
    c: Equal(g9,g109)
    c: Parallel(g109,g9)
    c: Coincident(g110,g111)
    c: Coincident(g111,g112)
    c: Coincident(g112,g113)
    c: Coincident(g113,g110)
    c: Horizontal(g110)
    c: Horizontal(g112)
    c: Vertical(g111)
    c: Vertical(g113)
    c: Equal(g3,g113) = 4
    c: Equal(g2,g112) = 0.35
    c: Coincident(g105,g114)
    c: Coincident(g110,g114)
    c: Equal(g9,g114)
    c: Parallel(g114,g9)
    c: Coincident(g115,g116)
    c: Coincident(g116,g117)
    c: Coincident(g117,g118)
    c: Coincident(g118,g115)
    c: Horizontal(g115)
    c: Horizontal(g117)
    c: Vertical(g116)
    c: Vertical(g118)
    c: Equal(g3,g118) = 4
    c: Equal(g2,g117) = 0.35
    c: Coincident(g110,g119)
    c: Coincident(g115,g119)
    c: Equal(g9,g119)
    c: Parallel(g119,g9)
    c: Coincident(g120,g121)
    c: Coincident(g121,g122)
    c: Coincident(g122,g123)
    c: Coincident(g123,g120)
    c: Horizontal(g120)
    c: Horizontal(g122)
    c: Vertical(g121)
    c: Vertical(g123)
    c: Equal(g3,g123) = 4
    c: Equal(g2,g122) = 0.35
    c: Coincident(g115,g124)
    c: Coincident(g120,g124)
    c: Equal(g9,g124)
    c: Parallel(g124,g9)
    c: Coincident(g125,g126)
    c: Coincident(g126,g127)
    c: Coincident(g127,g128)
    c: Coincident(g128,g125)
    c: Horizontal(g125)
    c: Horizontal(g127)
    c: Vertical(g126)
    c: Vertical(g128)
    c: Equal(g3,g128) = 4
    c: Equal(g2,g127) = 0.35
    c: Coincident(g120,g129)
    c: Coincident(g125,g129)
    c: Equal(g9,g129)
    c: Parallel(g129,g9)
    c: Coincident(g130,g131)
    c: Coincident(g131,g132)
    c: Coincident(g132,g133)
    c: Coincident(g133,g130)
    c: Horizontal(g130)
    c: Horizontal(g132)
    c: Vertical(g131)
    c: Vertical(g133)
    c: Equal(g3,g133) = 4
    c: Equal(g2,g132) = 0.35
    c: Coincident(g125,g134)
    c: Coincident(g130,g134)
    c: Equal(g9,g134)
    c: Parallel(g134,g9)
    c: Coincident(g135,g136)
    c: Coincident(g136,g137)
    c: Coincident(g137,g138)
    c: Coincident(g138,g135)
    c: Horizontal(g135)
    c: Horizontal(g137)
    c: Vertical(g136)
    c: Vertical(g138)
    c: Equal(g3,g138) = 4
    c: Equal(g2,g137) = 0.35
    c: Coincident(g130,g139)
    c: Coincident(g135,g139)
    c: Equal(g9,g139)
    c: Parallel(g139,g9)
    c: Coincident(g140,g141)
    c: Coincident(g141,g142)
    c: Coincident(g142,g143)
    c: Coincident(g143,g140)
    c: Horizontal(g140)
    c: Horizontal(g142)
    c: Vertical(g141)
    c: Vertical(g143)
    c: Equal(g3,g143) = 4
    c: Equal(g2,g142) = 0.35
    c: Coincident(g135,g144)
    c: Coincident(g140,g144)
    c: Equal(g9,g144)
    c: Parallel(g144,g9)
    c: Coincident(g145,g146)
    c: Coincident(g146,g147)
    c: Coincident(g147,g148)
    c: Coincident(g148,g145)
    c: Horizontal(g145)
    c: Horizontal(g147)
    c: Vertical(g146)
    c: Vertical(g148)
    c: Equal(g3,g148) = 4
    c: Equal(g2,g147) = 0.35
    c: Coincident(g140,g149)
    c: Coincident(g145,g149)
    c: Equal(g9,g149)
    c: Parallel(g149,g9)
    c: Coincident(g150,g151)
    c: Coincident(g151,g152)
    c: Coincident(g152,g153)
    c: Coincident(g153,g150)
    c: Horizontal(g150)
    c: Horizontal(g152)
    c: Vertical(g151)
    c: Vertical(g153)
    c: Equal(g3,g153) = 4
    c: Equal(g2,g152) = 0.35
    c: Coincident(g145,g154)
    c: Coincident(g150,g154)
    c: Equal(g9,g154)
    c: Parallel(g154,g9)
    c: Coincident(g155,g156)
    c: Coincident(g156,g157)
    c: Coincident(g157,g158)
    c: Coincident(g158,g155)
    c: Horizontal(g155)
    c: Horizontal(g157)
    c: Vertical(g156)
    c: Vertical(g158)
    c: Equal(g3,g158) = 4
    c: Equal(g2,g157) = 0.35
    c: Coincident(g150,g159)
    c: Coincident(g155,g159)
    c: Equal(g9,g159)
    c: Parallel(g159,g9)
    c: Coincident(g160,g161)
    c: Coincident(g161,g162)
    c: Coincident(g162,g163)
    c: Coincident(g163,g160)
    c: Horizontal(g160)
    c: Horizontal(g162)
    c: Vertical(g161)
    c: Vertical(g163)
    c: Equal(g3,g163) = 4
    c: Equal(g2,g162) = 0.35
    c: Coincident(g155,g164)
    c: Coincident(g160,g164)
    c: Equal(g9,g164)
    c: Parallel(g164,g9)
    c: Coincident(g165,g166)
    c: Coincident(g166,g167)
    c: Coincident(g167,g168)
    c: Coincident(g168,g165)
    c: Horizontal(g165)
    c: Horizontal(g167)
    c: Vertical(g166)
    c: Vertical(g168)
    c: Equal(g3,g168) = 4
    c: Equal(g2,g167) = 0.35
    c: Coincident(g160,g169)
    c: Coincident(g165,g169)
    c: Equal(g9,g169)
    c: Parallel(g169,g9)
    c: Coincident(g165,g170)
    c: Equal(g9,g170)
    c: Parallel(g170,g9)
    c: DistanceY(g-1,g87) = 0
    c: Vertical(g86,g2)
    c: DistanceX(g-1,g167) = 79.7
FEATURE [PartDesign::Pocket] Pocket006
  BaseFeature = -> Pocket005
  Length = 1
  Length2 = 100
  Profile = -> Sketch008
  Reversed = true
  Type = 0
FEATURE [Sketcher::SketchObject] Sketch009  label="hz mm001"
  FullyConstrained = true
  MapMode = 5
  Placement = pos=(0,0,-3) rot=(0,0,1;0rad)
  Support = -> [DatumPlane]
  expr: Constraints[14] = Spreadsheet.reticleCmWidth
  expr: Constraints[13] = Spreadsheet.reticleCmHeight / 2
  sketch-geometry (513):
    g0: LineSegment StartX=-30 StartY=-20 StartZ=0 EndX=270 EndY=-20 EndZ=0
    g1: LineSegment StartX=238 StartY=0 StartZ=0 EndX=237.8 EndY=0 EndZ=0
    g2: LineSegment StartX=237.8 StartY=0 StartZ=0 EndX=237.8 EndY=-2 EndZ=0
    g3: LineSegment StartX=237.8 StartY=-2 StartZ=0 EndX=238 EndY=-2 EndZ=0
    g4: LineSegment StartX=238 StartY=-2 StartZ=0 EndX=238 EndY=0 EndZ=0
    g5: LineSegment StartX=236 StartY=0 StartZ=0 EndX=235.8 EndY=0 EndZ=0
    g6: LineSegment StartX=235.8 StartY=0 StartZ=0 EndX=235.8 EndY=-2 EndZ=0
    g7: LineSegment StartX=235.8 StartY=-2 StartZ=0 EndX=236 EndY=-2 EndZ=0
    g8: LineSegment StartX=236 StartY=-2 StartZ=0 EndX=236 EndY=0 EndZ=0
    g9: LineSegment StartX=234 StartY=0 StartZ=0 EndX=233.8 EndY=0 EndZ=0
    g10: LineSegment StartX=233.8 StartY=0 StartZ=0 EndX=233.8 EndY=-2 EndZ=0
    g11: LineSegment StartX=233.8 StartY=-2 StartZ=0 EndX=234 EndY=-2 EndZ=0
    g12: LineSegment StartX=234 StartY=-2 StartZ=0 EndX=234 EndY=0 EndZ=0
    g13: LineSegment StartX=231.8 StartY=0 StartZ=0 EndX=232 EndY=0 EndZ=0
    g14: LineSegment StartX=232 StartY=0 StartZ=0 EndX=232 EndY=-2 EndZ=0
    g15: LineSegment StartX=232 StartY=-2 StartZ=0 EndX=231.8 EndY=-2 EndZ=0
    g16: LineSegment StartX=231.8 StartY=-2 StartZ=0 EndX=231.8 EndY=0 EndZ=0
    g17: LineSegment StartX=227.8 StartY=0 StartZ=0 EndX=228 EndY=0 EndZ=0
    g18: LineSegment StartX=228 StartY=0 StartZ=0 EndX=228 EndY=-2 EndZ=0
    g19: LineSegment StartX=228 StartY=-2 StartZ=0 EndX=227.8 EndY=-2 EndZ=0
    g20: LineSegment StartX=227.8 StartY=-2 StartZ=0 EndX=227.8 EndY=0 EndZ=0
    g21: LineSegment StartX=226 StartY=0 StartZ=0 EndX=225.8 EndY=0 EndZ=0
    g22: LineSegment StartX=225.8 StartY=0 StartZ=0 EndX=225.8 EndY=-2 EndZ=0
    g23: LineSegment StartX=225.8 StartY=-2 StartZ=0 EndX=226 EndY=-2 EndZ=0
    g24: LineSegment StartX=226 StartY=-2 StartZ=0 EndX=226 EndY=0 EndZ=0
    g25: LineSegment StartX=224 StartY=0 StartZ=0 EndX=223.8 EndY=0 EndZ=0
    g26: LineSegment StartX=223.8 StartY=0 StartZ=0 EndX=223.8 EndY=-2 EndZ=0
    g27: LineSegment StartX=223.8 StartY=-2 StartZ=0 EndX=224 EndY=-2 EndZ=0
    g28: LineSegment StartX=224 StartY=-2 StartZ=0 EndX=224 EndY=0 EndZ=0
    g29: LineSegment StartX=221.8 StartY=0 StartZ=0 EndX=222 EndY=0 EndZ=0
    g30: LineSegment StartX=222 StartY=0 StartZ=0 EndX=222 EndY=-2 EndZ=0
    g31: LineSegment StartX=222 StartY=-2 StartZ=0 EndX=221.8 EndY=-2 EndZ=0
    g32: LineSegment StartX=221.8 StartY=-2 StartZ=0 EndX=221.8 EndY=0 EndZ=0
    g33: LineSegment StartX=218 StartY=0 StartZ=0 EndX=217.8 EndY=0 EndZ=0
    g34: LineSegment StartX=217.8 StartY=0 StartZ=0 EndX=217.8 EndY=-2 EndZ=0
    g35: LineSegment StartX=217.8 StartY=-2 StartZ=0 EndX=218 EndY=-2 EndZ=0
    g36: LineSegment StartX=218 StartY=-2 StartZ=0 EndX=218 EndY=0 EndZ=0
    g37: LineSegment StartX=216 StartY=0 StartZ=0 EndX=215.8 EndY=0 EndZ=0
    g38: LineSegment StartX=215.8 StartY=0 StartZ=0 EndX=215.8 EndY=-2 EndZ=0
    g39: LineSegment StartX=215.8 StartY=-2 StartZ=0 EndX=216 EndY=-2 EndZ=0
    g40: LineSegment StartX=216 StartY=-2 StartZ=0 EndX=216 EndY=0 EndZ=0
    g41: LineSegment StartX=214 StartY=0 StartZ=0 EndX=213.8 EndY=0 EndZ=0
    g42: LineSegment StartX=213.8 StartY=0 StartZ=0 EndX=213.8 EndY=-2 EndZ=0
    g43: LineSegment StartX=213.8 StartY=-2 StartZ=0 EndX=214 EndY=-2 EndZ=0
    g44: LineSegment StartX=214 StartY=-2 StartZ=0 EndX=214 EndY=0 EndZ=0
    g45: LineSegment StartX=211.8 StartY=0 StartZ=0 EndX=212 EndY=0 EndZ=0
    g46: LineSegment StartX=212 StartY=0 StartZ=0 EndX=212 EndY=-2 EndZ=0
    g47: LineSegment StartX=212 StartY=-2 StartZ=0 EndX=211.8 EndY=-2 EndZ=0
    g48: LineSegment StartX=211.8 StartY=-2 StartZ=0 EndX=211.8 EndY=0 EndZ=0
    g49: LineSegment StartX=208 StartY=0 StartZ=0 EndX=207.8 EndY=0 EndZ=0
    g50: LineSegment StartX=207.8 StartY=0 StartZ=0 EndX=207.8 EndY=-2 EndZ=0
    g51: LineSegment StartX=207.8 StartY=-2 StartZ=0 EndX=208 EndY=-2 EndZ=0
    g52: LineSegment StartX=208 StartY=-2 StartZ=0 EndX=208 EndY=0 EndZ=0
    g53: LineSegment StartX=206 StartY=0 StartZ=0 EndX=205.8 EndY=0 EndZ=0
    g54: LineSegment StartX=205.8 StartY=0 StartZ=0 EndX=205.8 EndY=-2 EndZ=0
    g55: LineSegment StartX=205.8 StartY=-2 StartZ=0 EndX=206 EndY=-2 EndZ=0
    g56: LineSegment StartX=206 StartY=-2 StartZ=0 EndX=206 EndY=0 EndZ=0
    g57: LineSegment StartX=204 StartY=0 StartZ=0 EndX=203.8 EndY=0 EndZ=0
    g58: LineSegment StartX=203.8 StartY=0 StartZ=0 EndX=203.8 EndY=-2 EndZ=0
    g59: LineSegment StartX=203.8 StartY=-2 StartZ=0 EndX=204 EndY=-2 EndZ=0
    g60: LineSegment StartX=204 StartY=-2 StartZ=0 EndX=204 EndY=0 EndZ=0
    g61: LineSegment StartX=201.8 StartY=0 StartZ=0 EndX=202 EndY=0 EndZ=0
    g62: LineSegment StartX=202 StartY=0 StartZ=0 EndX=202 EndY=-2 EndZ=0
    g63: LineSegment StartX=202 StartY=-2 StartZ=0 EndX=201.8 EndY=-2 EndZ=0
    g64: LineSegment StartX=201.8 StartY=-2 StartZ=0 EndX=201.8 EndY=0 EndZ=0
    g65: LineSegment StartX=197.8 StartY=0 StartZ=0 EndX=198 EndY=0 EndZ=0
    g66: LineSegment StartX=198 StartY=0 StartZ=0 EndX=198 EndY=-2 EndZ=0
    g67: LineSegment StartX=198 StartY=-2 StartZ=0 EndX=197.8 EndY=-2 EndZ=0
    g68: LineSegment StartX=197.8 StartY=-2 StartZ=0 EndX=197.8 EndY=0 EndZ=0
    g69: LineSegment StartX=196 StartY=0 StartZ=0 EndX=195.8 EndY=0 EndZ=0
    g70: LineSegment StartX=195.8 StartY=0 StartZ=0 EndX=195.8 EndY=-2 EndZ=0
    g71: LineSegment StartX=195.8 StartY=-2 StartZ=0 EndX=196 EndY=-2 EndZ=0
    g72: LineSegment StartX=196 StartY=-2 StartZ=0 EndX=196 EndY=0 EndZ=0
    g73: LineSegment StartX=194 StartY=0 StartZ=0 EndX=193.8 EndY=0 EndZ=0
    g74: LineSegment StartX=193.8 StartY=0 StartZ=0 EndX=193.8 EndY=-2 EndZ=0
    g75: LineSegment StartX=193.8 StartY=-2 StartZ=0 EndX=194 EndY=-2 EndZ=0
    g76: LineSegment StartX=194 StartY=-2 StartZ=0 EndX=194 EndY=0 EndZ=0
    g77: LineSegment StartX=191.8 StartY=0 StartZ=0 EndX=192 EndY=0 EndZ=0
    g78: LineSegment StartX=192 StartY=0 StartZ=0 EndX=192 EndY=-2 EndZ=0
    g79: LineSegment StartX=192 StartY=-2 StartZ=0 EndX=191.8 EndY=-2 EndZ=0
    g80: LineSegment StartX=191.8 StartY=-2 StartZ=0 EndX=191.8 EndY=0 EndZ=0
    g81: LineSegment StartX=188 StartY=0 StartZ=0 EndX=187.8 EndY=0 EndZ=0
    g82: LineSegment StartX=187.8 StartY=0 StartZ=0 EndX=187.8 EndY=-2 EndZ=0
    g83: LineSegment StartX=187.8 StartY=-2 StartZ=0 EndX=188 EndY=-2 EndZ=0
    g84: LineSegment StartX=188 StartY=-2 StartZ=0 EndX=188 EndY=0 EndZ=0
    g85: LineSegment StartX=186 StartY=0 StartZ=0 EndX=185.8 EndY=0 EndZ=0
    g86: LineSegment StartX=185.8 StartY=0 StartZ=0 EndX=185.8 EndY=-2 EndZ=0
    g87: LineSegment StartX=185.8 StartY=-2 StartZ=0 EndX=186 EndY=-2 EndZ=0
    g88: LineSegment StartX=186 StartY=-2 StartZ=0 EndX=186 EndY=0 EndZ=0
    g89: LineSegment StartX=184 StartY=0 StartZ=0 EndX=183.8 EndY=0 EndZ=0
    g90: LineSegment StartX=183.8 StartY=0 StartZ=0 EndX=183.8 EndY=-2 EndZ=0
    g91: LineSegment StartX=183.8 StartY=-2 StartZ=0 EndX=184 EndY=-2 EndZ=0
    g92: LineSegment StartX=184 StartY=-2 StartZ=0 EndX=184 EndY=0 EndZ=0
    g93: LineSegment StartX=181.8 StartY=0 StartZ=0 EndX=182 EndY=0 EndZ=0
    g94: LineSegment StartX=182 StartY=0 StartZ=0 EndX=182 EndY=-2 EndZ=0
    g95: LineSegment StartX=182 StartY=-2 StartZ=0 EndX=181.8 EndY=-2 EndZ=0
    g96: LineSegment StartX=181.8 StartY=-2 StartZ=0 EndX=181.8 EndY=0 EndZ=0
    g97: LineSegment StartX=177.8 StartY=0 StartZ=0 EndX=178 EndY=0 EndZ=0
    g98: LineSegment StartX=178 StartY=0 StartZ=0 EndX=178 EndY=-2 EndZ=0
    g99: LineSegment StartX=178 StartY=-2 StartZ=0 EndX=177.8 EndY=-2 EndZ=0
    g100: LineSegment StartX=177.8 StartY=-2 StartZ=0 EndX=177.8 EndY=0 EndZ=0
    g101: LineSegment StartX=176 StartY=0 StartZ=0 EndX=175.8 EndY=0 EndZ=0
    g102: LineSegment StartX=175.8 StartY=0 StartZ=0 EndX=175.8 EndY=-2 EndZ=0
    g103: LineSegment StartX=175.8 StartY=-2 StartZ=0 EndX=176 EndY=-2 EndZ=0
    g104: LineSegment StartX=176 StartY=-2 StartZ=0 EndX=176 EndY=0 EndZ=0
    g105: LineSegment StartX=174 StartY=0 StartZ=0 EndX=173.8 EndY=0 EndZ=0
    g106: LineSegment StartX=173.8 StartY=0 StartZ=0 EndX=173.8 EndY=-2 EndZ=0
    g107: LineSegment StartX=173.8 StartY=-2 StartZ=0 EndX=174 EndY=-2 EndZ=0
    g108: LineSegment StartX=174 StartY=-2 StartZ=0 EndX=174 EndY=0 EndZ=0
    g109: LineSegment StartX=171.8 StartY=0 StartZ=0 EndX=172 EndY=0 EndZ=0
    g110: LineSegment StartX=172 StartY=0 StartZ=0 EndX=172 EndY=-2 EndZ=0
    g111: LineSegment StartX=172 StartY=-2 StartZ=0 EndX=171.8 EndY=-2 EndZ=0
    g112: LineSegment StartX=171.8 StartY=-2 StartZ=0 EndX=171.8 EndY=0 EndZ=0
    g113: LineSegment StartX=167.8 StartY=0 StartZ=0 EndX=168 EndY=0 EndZ=0
    g114: LineSegment StartX=168 StartY=0 StartZ=0 EndX=168 EndY=-2 EndZ=0
    g115: LineSegment StartX=168 StartY=-2 StartZ=0 EndX=167.8 EndY=-2 EndZ=0
    g116: LineSegment StartX=167.8 StartY=-2 StartZ=0 EndX=167.8 EndY=0 EndZ=0
    g117: LineSegment StartX=166 StartY=0 StartZ=0 EndX=165.8 EndY=0 EndZ=0
    g118: LineSegment StartX=165.8 StartY=0 StartZ=0 EndX=165.8 EndY=-2 EndZ=0
    g119: LineSegment StartX=165.8 StartY=-2 StartZ=0 EndX=166 EndY=-2 EndZ=0
    g120: LineSegment StartX=166 StartY=-2 StartZ=0 EndX=166 EndY=0 EndZ=0
    g121: LineSegment StartX=164 StartY=0 StartZ=0 EndX=163.8 EndY=0 EndZ=0
    g122: LineSegment StartX=163.8 StartY=0 StartZ=0 EndX=163.8 EndY=-2 EndZ=0
    g123: LineSegment StartX=163.8 StartY=-2 StartZ=0 EndX=164 EndY=-2 EndZ=0
    g124: LineSegment StartX=164 StartY=-2 StartZ=0 EndX=164 EndY=0 EndZ=0
    g125: LineSegment StartX=161.8 StartY=0 StartZ=0 EndX=162 EndY=0 EndZ=0
    g126: LineSegment StartX=162 StartY=0 StartZ=0 EndX=162 EndY=-2 EndZ=0
    g127: LineSegment StartX=162 StartY=-2 StartZ=0 EndX=161.8 EndY=-2 EndZ=0
    g128: LineSegment StartX=161.8 StartY=-2 StartZ=0 EndX=161.8 EndY=0 EndZ=0
    g129: LineSegment StartX=158 StartY=0 StartZ=0 EndX=157.8 EndY=0 EndZ=0
    g130: LineSegment StartX=157.8 StartY=0 StartZ=0 EndX=157.8 EndY=-2 EndZ=0
    g131: LineSegment StartX=157.8 StartY=-2 StartZ=0 EndX=158 EndY=-2 EndZ=0
    g132: LineSegment StartX=158 StartY=-2 StartZ=0 EndX=158 EndY=0 EndZ=0
    g133: LineSegment StartX=156 StartY=0 StartZ=0 EndX=155.8 EndY=0 EndZ=0
    g134: LineSegment StartX=155.8 StartY=0 StartZ=0 EndX=155.8 EndY=-2 EndZ=0
    g135: LineSegment StartX=155.8 StartY=-2 StartZ=0 EndX=156 EndY=-2 EndZ=0
    g136: LineSegment StartX=156 StartY=-2 StartZ=0 EndX=156 EndY=0 EndZ=0
    g137: LineSegment StartX=154 StartY=0 StartZ=0 EndX=153.8 EndY=0 EndZ=0
    g138: LineSegment StartX=153.8 StartY=0 StartZ=0 EndX=153.8 EndY=-2 EndZ=0
    g139: LineSegment StartX=153.8 StartY=-2 StartZ=0 EndX=154 EndY=-2 EndZ=0
    g140: LineSegment StartX=154 StartY=-2 StartZ=0 EndX=154 EndY=0 EndZ=0
    g141: LineSegment StartX=151.8 StartY=0 StartZ=0 EndX=152 EndY=0 EndZ=0
    g142: LineSegment StartX=152 StartY=0 StartZ=0 EndX=152 EndY=-2 EndZ=0
    g143: LineSegment StartX=152 StartY=-2 StartZ=0 EndX=151.8 EndY=-2 EndZ=0
    g144: LineSegment StartX=151.8 StartY=-2 StartZ=0 EndX=151.8 EndY=0 EndZ=0
    g145: LineSegment StartX=148 StartY=0 StartZ=0 EndX=147.8 EndY=0 EndZ=0
    g146: LineSegment StartX=147.8 StartY=0 StartZ=0 EndX=147.8 EndY=-2 EndZ=0
    g147: LineSegment StartX=147.8 StartY=-2 StartZ=0 EndX=148 EndY=-2 EndZ=0
    g148: LineSegment StartX=148 StartY=-2 StartZ=0 EndX=148 EndY=0 EndZ=0
    g149: LineSegment StartX=146 StartY=0 StartZ=0 EndX=145.8 EndY=0 EndZ=0
    g150: LineSegment StartX=145.8 StartY=0 StartZ=0 EndX=145.8 EndY=-2 EndZ=0
    g151: LineSegment StartX=145.8 StartY=-2 StartZ=0 EndX=146 EndY=-2 EndZ=0
    g152: LineSegment StartX=146 StartY=-2 StartZ=0 EndX=146 EndY=0 EndZ=0
    g153: LineSegment StartX=144 StartY=0 StartZ=0 EndX=143.8 EndY=0 EndZ=0
    g154: LineSegment StartX=143.8 StartY=0 StartZ=0 EndX=143.8 EndY=-2 EndZ=0
    g155: LineSegment StartX=143.8 StartY=-2 StartZ=0 EndX=144 EndY=-2 EndZ=0
    g156: LineSegment StartX=144 StartY=-2 StartZ=0 EndX=144 EndY=0 EndZ=0
    g157: LineSegment StartX=141.8 StartY=0 StartZ=0 EndX=142 EndY=0 EndZ=0
    g158: LineSegment StartX=142 StartY=0 StartZ=0 EndX=142 EndY=-2 EndZ=0
    g159: LineSegment StartX=142 StartY=-2 StartZ=0 EndX=141.8 EndY=-2 EndZ=0
    g160: LineSegment StartX=141.8 StartY=-2 StartZ=0 EndX=141.8 EndY=0 EndZ=0
    g161: LineSegment StartX=137.8 StartY=0 StartZ=0 EndX=138 EndY=0 EndZ=0
    g162: LineSegment StartX=138 StartY=0 StartZ=0 EndX=138 EndY=-2 EndZ=0
    g163: LineSegment StartX=138 StartY=-2 StartZ=0 EndX=137.8 EndY=-2 EndZ=0
    g164: LineSegment StartX=137.8 StartY=-2 StartZ=0 EndX=137.8 EndY=0 EndZ=0
    g165: LineSegment StartX=136 StartY=0 StartZ=0 EndX=135.8 EndY=0 EndZ=0
    g166: LineSegment StartX=135.8 StartY=0 StartZ=0 EndX=135.8 EndY=-2 EndZ=0
    g167: LineSegment StartX=135.8 StartY=-2 StartZ=0 EndX=136 EndY=-2 EndZ=0
    g168: LineSegment StartX=136 StartY=-2 StartZ=0 EndX=136 EndY=0 EndZ=0
    g169: LineSegment StartX=134 StartY=0 StartZ=0 EndX=133.8 EndY=0 EndZ=0
    g170: LineSegment StartX=133.8 StartY=0 StartZ=0 EndX=133.8 EndY=-2 EndZ=0
    g171: LineSegment StartX=133.8 StartY=-2 StartZ=0 EndX=134 EndY=-2 EndZ=0
    g172: LineSegment StartX=134 StartY=-2 StartZ=0 EndX=134 EndY=0 EndZ=0
    g173: LineSegment StartX=131.8 StartY=0 StartZ=0 EndX=132 EndY=0 EndZ=0
    g174: LineSegment StartX=132 StartY=0 StartZ=0 EndX=132 EndY=-2 EndZ=0
    g175: LineSegment StartX=132 StartY=-2 StartZ=0 EndX=131.8 EndY=-2 EndZ=0
    g176: LineSegment StartX=131.8 StartY=-2 StartZ=0 EndX=131.8 EndY=0 EndZ=0
    g177: LineSegment StartX=128 StartY=0 StartZ=0 EndX=127.8 EndY=0 EndZ=0
    g178: LineSegment StartX=127.8 StartY=0 StartZ=0 EndX=127.8 EndY=-2 EndZ=0
    g179: LineSegment StartX=127.8 StartY=-2 StartZ=0 EndX=128 EndY=-2 EndZ=0
    g180: LineSegment StartX=128 StartY=-2 StartZ=0 EndX=128 EndY=0 EndZ=0
    g181: LineSegment StartX=126 StartY=0 StartZ=0 EndX=125.8 EndY=0 EndZ=0
    g182: LineSegment StartX=125.8 StartY=0 StartZ=0 EndX=125.8 EndY=-2 EndZ=0
    g183: LineSegment StartX=125.8 StartY=-2 StartZ=0 EndX=126 EndY=-2 EndZ=0
    g184: LineSegment StartX=126 StartY=-2 StartZ=0 EndX=126 EndY=0 EndZ=0
    g185: LineSegment StartX=124 StartY=0 StartZ=0 EndX=123.8 EndY=0 EndZ=0
    g186: LineSegment StartX=123.8 StartY=0 StartZ=0 EndX=123.8 EndY=-2 EndZ=0
    g187: LineSegment StartX=123.8 StartY=-2 StartZ=0 EndX=124 EndY=-2 EndZ=0
    g188: LineSegment StartX=124 StartY=-2 StartZ=0 EndX=124 EndY=0 EndZ=0
    g189: LineSegment StartX=122 StartY=0 StartZ=0 EndX=121.8 EndY=0 EndZ=0
    g190: LineSegment StartX=121.8 StartY=0 StartZ=0 EndX=121.8 EndY=-2 EndZ=0
    g191: LineSegment StartX=121.8 StartY=-2 StartZ=0 EndX=122 EndY=-2 EndZ=0
    g192: LineSegment StartX=122 StartY=-2 StartZ=0 EndX=122 EndY=0 EndZ=0
    g193: LineSegment StartX=118 StartY=0 StartZ=0 EndX=117.8 EndY=0 EndZ=0
    g194: LineSegment StartX=117.8 StartY=0 StartZ=0 EndX=117.8 EndY=-2 EndZ=0
    g195: LineSegment StartX=117.8 StartY=-2 StartZ=0 EndX=118 EndY=-2 EndZ=0
    g196: LineSegment StartX=118 StartY=-2 StartZ=0 EndX=118 EndY=0 EndZ=0
    g197: LineSegment StartX=116 StartY=0 StartZ=0 EndX=115.8 EndY=0 EndZ=0
    g198: LineSegment StartX=115.8 StartY=0 StartZ=0 EndX=115.8 EndY=-2 EndZ=0
    g199: LineSegment StartX=115.8 StartY=-2 StartZ=0 EndX=116 EndY=-2 EndZ=0
    g200: LineSegment StartX=116 StartY=-2 StartZ=0 EndX=116 EndY=0 EndZ=0
    g201: LineSegment StartX=114 StartY=0 StartZ=0 EndX=113.8 EndY=0 EndZ=0
    g202: LineSegment StartX=113.8 StartY=0 StartZ=0 EndX=113.8 EndY=-2 EndZ=0
    g203: LineSegment StartX=113.8 StartY=-2 StartZ=0 EndX=114 EndY=-2 EndZ=0
    g204: LineSegment StartX=114 StartY=-2 StartZ=0 EndX=114 EndY=0 EndZ=0
    g205: LineSegment StartX=112 StartY=0 StartZ=0 EndX=111.8 EndY=0 EndZ=0
    g206: LineSegment StartX=111.8 StartY=0 StartZ=0 EndX=111.8 EndY=-2 EndZ=0
    g207: LineSegment StartX=111.8 StartY=-2 StartZ=0 EndX=112 EndY=-2 EndZ=0
    g208: LineSegment StartX=112 StartY=-2 StartZ=0 EndX=112 EndY=0 EndZ=0
    g209: LineSegment StartX=107.8 StartY=0 StartZ=0 EndX=107.6 EndY=0 EndZ=0
    g210: LineSegment StartX=107.6 StartY=0 StartZ=0 EndX=107.6 EndY=-2 EndZ=0
    g211: LineSegment StartX=107.6 StartY=-2 StartZ=0 EndX=107.8 EndY=-2 EndZ=0
    g212: LineSegment StartX=107.8 StartY=-2 StartZ=0 EndX=107.8 EndY=0 EndZ=0
    g213: LineSegment StartX=106 StartY=0 StartZ=0 EndX=105.8 EndY=0 EndZ=0
    g214: LineSegment StartX=105.8 StartY=0 StartZ=0 EndX=105.8 EndY=-2 EndZ=0
    g215: LineSegment StartX=105.8 StartY=-2 StartZ=0 EndX=106 EndY=-2 EndZ=0
    g216: LineSegment StartX=106 StartY=-2 StartZ=0 EndX=106 EndY=0 EndZ=0
    g217: LineSegment StartX=104 StartY=0 StartZ=0 EndX=103.8 EndY=0 EndZ=0
    g218: LineSegment StartX=103.8 StartY=0 StartZ=0 EndX=103.8 EndY=-2 EndZ=0
    g219: LineSegment StartX=103.8 StartY=-2 StartZ=0 EndX=104 EndY=-2 EndZ=0
    g220: LineSegment StartX=104 StartY=-2 StartZ=0 EndX=104 EndY=0 EndZ=0
    g221: LineSegment StartX=101.8 StartY=0 StartZ=0 EndX=102 EndY=0 EndZ=0
    g222: LineSegment StartX=102 StartY=0 StartZ=0 EndX=102 EndY=-2 EndZ=0
    g223: LineSegment StartX=102 StartY=-2 StartZ=0 EndX=101.8 EndY=-2 EndZ=0
    g224: LineSegment StartX=101.8 StartY=-2 StartZ=0 EndX=101.8 EndY=0 EndZ=0
    g225: LineSegment StartX=98 StartY=0 StartZ=0 EndX=97.8 EndY=0 EndZ=0
    g226: LineSegment StartX=97.8 StartY=0 StartZ=0 EndX=97.8 EndY=-2 EndZ=0
    g227: LineSegment StartX=97.8 StartY=-2 StartZ=0 EndX=98 EndY=-2 EndZ=0
    g228: LineSegment StartX=98 StartY=-2 StartZ=0 EndX=98 EndY=0 EndZ=0
    g229: LineSegment StartX=96 StartY=0 StartZ=0 EndX=95.8 EndY=0 EndZ=0
    g230: LineSegment StartX=95.8 StartY=0 StartZ=0 EndX=95.8 EndY=-2 EndZ=0
    g231: LineSegment StartX=95.8 StartY=-2 StartZ=0 EndX=96 EndY=-2 EndZ=0
    g232: LineSegment StartX=96 StartY=-2 StartZ=0 EndX=96 EndY=0 EndZ=0
    g233: LineSegment StartX=94 StartY=0 StartZ=0 EndX=93.8 EndY=0 EndZ=0
    g234: LineSegment StartX=93.8 StartY=0 StartZ=0 EndX=93.8 EndY=-2 EndZ=0
    g235: LineSegment StartX=93.8 StartY=-2 StartZ=0 EndX=94 EndY=-2 EndZ=0
    g236: LineSegment StartX=94 StartY=-2 StartZ=0 EndX=94 EndY=0 EndZ=0
    g237: LineSegment StartX=92 StartY=0 StartZ=0 EndX=91.8 EndY=0 EndZ=0
    g238: LineSegment StartX=91.8 StartY=0 StartZ=0 EndX=91.8 EndY=-2 EndZ=0
    g239: LineSegment StartX=91.8 StartY=-2 StartZ=0 EndX=92 EndY=-2 EndZ=0
    g240: LineSegment StartX=92 StartY=-2 StartZ=0 EndX=92 EndY=0 EndZ=0
    g241: LineSegment StartX=88 StartY=0 StartZ=0 EndX=87.8 EndY=0 EndZ=0
    g242: LineSegment StartX=87.8 StartY=0 StartZ=0 EndX=87.8 EndY=-2 EndZ=0
    g243: LineSegment StartX=87.8 StartY=-2 StartZ=0 EndX=88 EndY=-2 EndZ=0
    g244: LineSegment StartX=88 StartY=-2 StartZ=0 EndX=88 EndY=0 EndZ=0
    g245: LineSegment StartX=86 StartY=0 StartZ=0 EndX=85.8 EndY=0 EndZ=0
    g246: LineSegment StartX=85.8 StartY=0 StartZ=0 EndX=85.8 EndY=-2 EndZ=0
    g247: LineSegment StartX=85.8 StartY=-2 StartZ=0 EndX=86 EndY=-2 EndZ=0
    g248: LineSegment StartX=86 StartY=-2 StartZ=0 EndX=86 EndY=0 EndZ=0
    g249: LineSegment StartX=84 StartY=0 StartZ=0 EndX=83.8 EndY=0 EndZ=0
    g250: LineSegment StartX=83.8 StartY=0 StartZ=0 EndX=83.8 EndY=-2 EndZ=0
    g251: LineSegment StartX=83.8 StartY=-2 StartZ=0 EndX=84 EndY=-2 EndZ=0
    g252: LineSegment StartX=84 StartY=-2 StartZ=0 EndX=84 EndY=0 EndZ=0
    g253: LineSegment StartX=81.6 StartY=0 StartZ=0 EndX=81.8 EndY=0 EndZ=0
    g254: LineSegment StartX=81.8 StartY=0 StartZ=0 EndX=81.8 EndY=-2 EndZ=0
    g255: LineSegment StartX=81.8 StartY=-2 StartZ=0 EndX=81.6 EndY=-2 EndZ=0
    g256: LineSegment StartX=81.6 StartY=-2 StartZ=0 EndX=81.6 EndY=0 EndZ=0
    g257: LineSegment StartX=238 StartY=-18 StartZ=0 EndX=237.8 EndY=-18 EndZ=0
    g258: LineSegment StartX=237.8 StartY=-18 StartZ=0 EndX=237.8 EndY=-20 EndZ=0
    g259: LineSegment StartX=237.8 StartY=-20 StartZ=0 EndX=238 EndY=-20 EndZ=0
    g260: LineSegment StartX=238 StartY=-20 StartZ=0 EndX=238 EndY=-18 EndZ=0
    g261: LineSegment StartX=236 StartY=-18 StartZ=0 EndX=235.8 EndY=-18 EndZ=0
    g262: LineSegment StartX=235.8 StartY=-18 StartZ=0 EndX=235.8 EndY=-20 EndZ=0
    g263: LineSegment StartX=235.8 StartY=-20 StartZ=0 EndX=236 EndY=-20 EndZ=0
    g264: LineSegment StartX=236 StartY=-20 StartZ=0 EndX=236 EndY=-18 EndZ=0
    g265: LineSegment StartX=234 StartY=-18 StartZ=0 EndX=233.8 EndY=-18 EndZ=0
    g266: LineSegment StartX=233.8 StartY=-18 StartZ=0 EndX=233.8 EndY=-20 EndZ=0
    g267: LineSegment StartX=233.8 StartY=-20 StartZ=0 EndX=234 EndY=-20 EndZ=0
    g268: LineSegment StartX=234 StartY=-20 StartZ=0 EndX=234 EndY=-18 EndZ=0
    g269: LineSegment StartX=231.8 StartY=-18 StartZ=0 EndX=232 EndY=-18 EndZ=0
    g270: LineSegment StartX=232 StartY=-18 StartZ=0 EndX=232 EndY=-20 EndZ=0
    g271: LineSegment StartX=232 StartY=-20 StartZ=0 EndX=231.8 EndY=-20 EndZ=0
    g272: LineSegment StartX=231.8 StartY=-20 StartZ=0 EndX=231.8 EndY=-18 EndZ=0
    g273: LineSegment StartX=227.8 StartY=-18 StartZ=0 EndX=228 EndY=-18 EndZ=0
    g274: LineSegment StartX=228 StartY=-18 StartZ=0 EndX=228 EndY=-20 EndZ=0
    g275: LineSegment StartX=228 StartY=-20 StartZ=0 EndX=227.8 EndY=-20 EndZ=0
    g276: LineSegment StartX=227.8 StartY=-20 StartZ=0 EndX=227.8 EndY=-18 EndZ=0
    g277: LineSegment StartX=226 StartY=-18 StartZ=0 EndX=225.8 EndY=-18 EndZ=0
    g278: LineSegment StartX=225.8 StartY=-18 StartZ=0 EndX=225.8 EndY=-20 EndZ=0
    g279: LineSegment StartX=225.8 StartY=-20 StartZ=0 EndX=226 EndY=-20 EndZ=0
    g280: LineSegment StartX=226 StartY=-20 StartZ=0 EndX=226 EndY=-18 EndZ=0
    g281: LineSegment StartX=224 StartY=-18 StartZ=0 EndX=223.8 EndY=-18 EndZ=0
    g282: LineSegment StartX=223.8 StartY=-18 StartZ=0 EndX=223.8 EndY=-20 EndZ=0
    g283: LineSegment StartX=223.8 StartY=-20 StartZ=0 EndX=224 EndY=-20 EndZ=0
    g284: LineSegment StartX=224 StartY=-20 StartZ=0 EndX=224 EndY=-18 EndZ=0
    g285: LineSegment StartX=221.8 StartY=-18 StartZ=0 EndX=222 EndY=-18 EndZ=0
    g286: LineSegment StartX=222 StartY=-18 StartZ=0 EndX=222 EndY=-20 EndZ=0
    g287: LineSegment StartX=222 StartY=-20 StartZ=0 EndX=221.8 EndY=-20 EndZ=0
    g288: LineSegment StartX=221.8 StartY=-20 StartZ=0 EndX=221.8 EndY=-18 EndZ=0
    g289: LineSegment StartX=218 StartY=-18 StartZ=0 EndX=217.8 EndY=-18 EndZ=0
    g290: LineSegment StartX=217.8 StartY=-18 StartZ=0 EndX=217.8 EndY=-20 EndZ=0
    g291: LineSegment StartX=217.8 StartY=-20 StartZ=0 EndX=218 EndY=-20 EndZ=0
    g292: LineSegment StartX=218 StartY=-20 StartZ=0 EndX=218 EndY=-18 EndZ=0
    g293: LineSegment StartX=216 StartY=-18 StartZ=0 EndX=215.8 EndY=-18 EndZ=0
    g294: LineSegment StartX=215.8 StartY=-18 StartZ=0 EndX=215.8 EndY=-20 EndZ=0
    g295: LineSegment StartX=215.8 StartY=-20 StartZ=0 EndX=216 EndY=-20 EndZ=0
    g296: LineSegment StartX=216 StartY=-20 StartZ=0 EndX=216 EndY=-18 EndZ=0
    g297: LineSegment StartX=214 StartY=-18 StartZ=0 EndX=213.8 EndY=-18 EndZ=0
    g298: LineSegment StartX=213.8 StartY=-18 StartZ=0 EndX=213.8 EndY=-20 EndZ=0
    g299: LineSegment StartX=213.8 StartY=-20 StartZ=0 EndX=214 EndY=-20 EndZ=0
    g300: LineSegment StartX=214 StartY=-20 StartZ=0 EndX=214 EndY=-18 EndZ=0
    g301: LineSegment StartX=211.8 StartY=-18 StartZ=0 EndX=212 EndY=-18 EndZ=0
    g302: LineSegment StartX=212 StartY=-18 StartZ=0 EndX=212 EndY=-20 EndZ=0
    g303: LineSegment StartX=212 StartY=-20 StartZ=0 EndX=211.8 EndY=-20 EndZ=0
    g304: LineSegment StartX=211.8 StartY=-20 StartZ=0 EndX=211.8 EndY=-18 EndZ=0
    g305: LineSegment StartX=208 StartY=-18 StartZ=0 EndX=207.8 EndY=-18 EndZ=0
    g306: LineSegment StartX=207.8 StartY=-18 StartZ=0 EndX=207.8 EndY=-20 EndZ=0
    g307: LineSegment StartX=207.8 StartY=-20 StartZ=0 EndX=208 EndY=-20 EndZ=0
    g308: LineSegment StartX=208 StartY=-20 StartZ=0 EndX=208 EndY=-18 EndZ=0
    g309: LineSegment StartX=206 StartY=-18 StartZ=0 EndX=205.8 EndY=-18 EndZ=0
    g310: LineSegment StartX=205.8 StartY=-18 StartZ=0 EndX=205.8 EndY=-20 EndZ=0
    g311: LineSegment StartX=205.8 StartY=-20 StartZ=0 EndX=206 EndY=-20 EndZ=0
    g312: LineSegment StartX=206 StartY=-20 StartZ=0 EndX=206 EndY=-18 EndZ=0
    g313: LineSegment StartX=204 StartY=-18 StartZ=0 EndX=203.8 EndY=-18 EndZ=0
    g314: LineSegment StartX=203.8 StartY=-18 StartZ=0 EndX=203.8 EndY=-20 EndZ=0
    g315: LineSegment StartX=203.8 StartY=-20 StartZ=0 EndX=204 EndY=-20 EndZ=0
    g316: LineSegment StartX=204 StartY=-20 StartZ=0 EndX=204 EndY=-18 EndZ=0
    g317: LineSegment StartX=201.8 StartY=-18 StartZ=0 EndX=202 EndY=-18 EndZ=0
    g318: LineSegment StartX=202 StartY=-18 StartZ=0 EndX=202 EndY=-20 EndZ=0
    g319: LineSegment StartX=202 StartY=-20 StartZ=0 EndX=201.8 EndY=-20 EndZ=0
    g320: LineSegment StartX=201.8 StartY=-20 StartZ=0 EndX=201.8 EndY=-18 EndZ=0
    g321: LineSegment StartX=197.8 StartY=-18 StartZ=0 EndX=198 EndY=-18 EndZ=0
    g322: LineSegment StartX=198 StartY=-18 StartZ=0 EndX=198 EndY=-20 EndZ=0
    g323: LineSegment StartX=198 StartY=-20 StartZ=0 EndX=197.8 EndY=-20 EndZ=0
    g324: LineSegment StartX=197.8 StartY=-20 StartZ=0 EndX=197.8 EndY=-18 EndZ=0
    g325: LineSegment StartX=196 StartY=-18 StartZ=0 EndX=195.8 EndY=-18 EndZ=0
    g326: LineSegment StartX=195.8 StartY=-18 StartZ=0 EndX=195.8 EndY=-20 EndZ=0
    g327: LineSegment StartX=195.8 StartY=-20 StartZ=0 EndX=196 EndY=-20 EndZ=0
    g328: LineSegment StartX=196 StartY=-20 StartZ=0 EndX=196 EndY=-18 EndZ=0
    g329: LineSegment StartX=194 StartY=-18 StartZ=0 EndX=193.8 EndY=-18 EndZ=0
    g330: LineSegment StartX=193.8 StartY=-18 StartZ=0 EndX=193.8 EndY=-20 EndZ=0
    g331: LineSegment StartX=193.8 StartY=-20 StartZ=0 EndX=194 EndY=-20 EndZ=0
    g332: LineSegment StartX=194 StartY=-20 StartZ=0 EndX=194 EndY=-18 EndZ=0
    g333: LineSegment StartX=191.8 StartY=-18 StartZ=0 EndX=192 EndY=-18 EndZ=0
    g334: LineSegment StartX=192 StartY=-18 StartZ=0 EndX=192 EndY=-20 EndZ=0
    g335: LineSegment StartX=192 StartY=-20 StartZ=0 EndX=191.8 EndY=-20 EndZ=0
    g336: LineSegment StartX=191.8 StartY=-20 StartZ=0 EndX=191.8 EndY=-18 EndZ=0
    g337: LineSegment StartX=188 StartY=-18 StartZ=0 EndX=187.8 EndY=-18 EndZ=0
    g338: LineSegment StartX=187.8 StartY=-18 StartZ=0 EndX=187.8 EndY=-20 EndZ=0
    g339: LineSegment StartX=187.8 StartY=-20 StartZ=0 EndX=188 EndY=-20 EndZ=0
    g340: LineSegment StartX=188 StartY=-20 StartZ=0 EndX=188 EndY=-18 EndZ=0
    g341: LineSegment StartX=186 StartY=-18 StartZ=0 EndX=185.8 EndY=-18 EndZ=0
    g342: LineSegment StartX=185.8 StartY=-18 StartZ=0 EndX=185.8 EndY=-20 EndZ=0
    g343: LineSegment StartX=185.8 StartY=-20 StartZ=0 EndX=186 EndY=-20 EndZ=0
    g344: LineSegment StartX=186 StartY=-20 StartZ=0 EndX=186 EndY=-18 EndZ=0
    g345: LineSegment StartX=184 StartY=-18 StartZ=0 EndX=183.8 EndY=-18 EndZ=0
    g346: LineSegment StartX=183.8 StartY=-18 StartZ=0 EndX=183.8 EndY=-20 EndZ=0
    g347: LineSegment StartX=183.8 StartY=-20 StartZ=0 EndX=184 EndY=-20 EndZ=0
    g348: LineSegment StartX=184 StartY=-20 StartZ=0 EndX=184 EndY=-18 EndZ=0
    g349: LineSegment StartX=181.8 StartY=-18 StartZ=0 EndX=182 EndY=-18 EndZ=0
    g350: LineSegment StartX=182 StartY=-18 StartZ=0 EndX=182 EndY=-20 EndZ=0
    g351: LineSegment StartX=182 StartY=-20 StartZ=0 EndX=181.8 EndY=-20 EndZ=0
    g352: LineSegment StartX=181.8 StartY=-20 StartZ=0 EndX=181.8 EndY=-18 EndZ=0
    g353: LineSegment StartX=177.8 StartY=-18 StartZ=0 EndX=178 EndY=-18 EndZ=0
    g354: LineSegment StartX=178 StartY=-18 StartZ=0 EndX=178 EndY=-20 EndZ=0
    g355: LineSegment StartX=178 StartY=-20 StartZ=0 EndX=177.8 EndY=-20 EndZ=0
    g356: LineSegment StartX=177.8 StartY=-20 StartZ=0 EndX=177.8 EndY=-18 EndZ=0
    g357: LineSegment StartX=176 StartY=-18 StartZ=0 EndX=175.8 EndY=-18 EndZ=0
    g358: LineSegment StartX=175.8 StartY=-18 StartZ=0 EndX=175.8 EndY=-20 EndZ=0
    g359: LineSegment StartX=175.8 StartY=-20 StartZ=0 EndX=176 EndY=-20 EndZ=0
    g360: LineSegment StartX=176 StartY=-20 StartZ=0 EndX=176 EndY=-18 EndZ=0
    g361: LineSegment StartX=174 StartY=-18 StartZ=0 EndX=173.8 EndY=-18 EndZ=0
    g362: LineSegment StartX=173.8 StartY=-18 StartZ=0 EndX=173.8 EndY=-20 EndZ=0
    g363: LineSegment StartX=173.8 StartY=-20 StartZ=0 EndX=174 EndY=-20 EndZ=0
    g364: LineSegment StartX=174 StartY=-20 StartZ=0 EndX=174 EndY=-18 EndZ=0
    g365: LineSegment StartX=171.8 StartY=-18 StartZ=0 EndX=172 EndY=-18 EndZ=0
    g366: LineSegment StartX=172 StartY=-18 StartZ=0 EndX=172 EndY=-20 EndZ=0
    g367: LineSegment StartX=172 StartY=-20 StartZ=0 EndX=171.8 EndY=-20 EndZ=0
    g368: LineSegment StartX=171.8 StartY=-20 StartZ=0 EndX=171.8 EndY=-18 EndZ=0
    g369: LineSegment StartX=167.8 StartY=-18 StartZ=0 EndX=168 EndY=-18 EndZ=0
    g370: LineSegment StartX=168 StartY=-18 StartZ=0 EndX=168 EndY=-20 EndZ=0
    g371: LineSegment StartX=168 StartY=-20 StartZ=0 EndX=167.8 EndY=-20 EndZ=0
    g372: LineSegment StartX=167.8 StartY=-20 StartZ=0 EndX=167.8 EndY=-18 EndZ=0
    g373: LineSegment StartX=166 StartY=-18 StartZ=0 EndX=165.8 EndY=-18 EndZ=0
    g374: LineSegment StartX=165.8 StartY=-18 StartZ=0 EndX=165.8 EndY=-20 EndZ=0
    g375: LineSegment StartX=165.8 StartY=-20 StartZ=0 EndX=166 EndY=-20 EndZ=0
    g376: LineSegment StartX=166 StartY=-20 StartZ=0 EndX=166 EndY=-18 EndZ=0
    g377: LineSegment StartX=164 StartY=-18 StartZ=0 EndX=163.8 EndY=-18 EndZ=0
    g378: LineSegment StartX=163.8 StartY=-18 StartZ=0 EndX=163.8 EndY=-20 EndZ=0
    g379: LineSegment StartX=163.8 StartY=-20 StartZ=0 EndX=164 EndY=-20 EndZ=0
    g380: LineSegment StartX=164 StartY=-20 StartZ=0 EndX=164 EndY=-18 EndZ=0
    g381: LineSegment StartX=161.8 StartY=-18 StartZ=0 EndX=162 EndY=-18 EndZ=0
    g382: LineSegment StartX=162 StartY=-18 StartZ=0 EndX=162 EndY=-20 EndZ=0
    g383: LineSegment StartX=162 StartY=-20 StartZ=0 EndX=161.8 EndY=-20 EndZ=0
    g384: LineSegment StartX=161.8 StartY=-20 StartZ=0 EndX=161.8 EndY=-18 EndZ=0
    g385: LineSegment StartX=158 StartY=-18 StartZ=0 EndX=157.8 EndY=-18 EndZ=0
    g386: LineSegment StartX=157.8 StartY=-18 StartZ=0 EndX=157.8 EndY=-20 EndZ=0
    g387: LineSegment StartX=157.8 StartY=-20 StartZ=0 EndX=158 EndY=-20 EndZ=0
    g388: LineSegment StartX=158 StartY=-20 StartZ=0 EndX=158 EndY=-18 EndZ=0
    g389: LineSegment StartX=156 StartY=-18 StartZ=0 EndX=155.8 EndY=-18 EndZ=0
    g390: LineSegment StartX=155.8 StartY=-18 StartZ=0 EndX=155.8 EndY=-20 EndZ=0
    g391: LineSegment StartX=155.8 StartY=-20 StartZ=0 EndX=156 EndY=-20 EndZ=0
    g392: LineSegment StartX=156 StartY=-20 StartZ=0 EndX=156 EndY=-18 EndZ=0
    g393: LineSegment StartX=154 StartY=-18 StartZ=0 EndX=153.8 EndY=-18 EndZ=0
    g394: LineSegment StartX=153.8 StartY=-18 StartZ=0 EndX=153.8 EndY=-20 EndZ=0
    g395: LineSegment StartX=153.8 StartY=-20 StartZ=0 EndX=154 EndY=-20 EndZ=0
    g396: LineSegment StartX=154 StartY=-20 StartZ=0 EndX=154 EndY=-18 EndZ=0
    g397: LineSegment StartX=151.8 StartY=-18 StartZ=0 EndX=152 EndY=-18 EndZ=0
    g398: LineSegment StartX=152 StartY=-18 StartZ=0 EndX=152 EndY=-20 EndZ=0
    g399: LineSegment StartX=152 StartY=-20 StartZ=0 EndX=151.8 EndY=-20 EndZ=0
    ... +113 more geometry lines
  constraints (1540):
    c: Horizontal(g0)
    c: DistanceY(g0,g-1) = 20
    c: DistanceX(g0,g0) = 300
    c: DistanceX(g0,g-1) = 30
    c: Coincident(g1,g2)
    c: Coincident(g2,g3)
    c: Coincident(g3,g4)
    c: Coincident(g4,g1)
    c: Horizontal(g1)
    c: Horizontal(g3)
    c: Vertical(g2)
    c: Vertical(g4)
    c: PointOnObject(g1,g-1)
    c: DistanceY(g4,g4) = 2
    c: DistanceX(g3,g3) = 0.2
    c: Coincident(g5,g6)
    c: Coincident(g6,g7)
    c: Coincident(g7,g8)
    c: Coincident(g8,g5)
    c: Horizontal(g5)
    c: Horizontal(g7)
    c: Vertical(g6)
    c: Vertical(g8)
    c: Equal(g4,g8) = 2
    c: Equal(g3,g7) = 0.2
    c: Coincident(g9,g10)
    c: Coincident(g10,g11)
    c: Coincident(g11,g12)
    c: Coincident(g12,g9)
    c: Horizontal(g9)
    c: Horizontal(g11)
    c: Vertical(g10)
    c: Vertical(g12)
    c: Equal(g8,g12) = 2
    c: Equal(g7,g11) = 0.2
    c: DistanceX(g9,g5) = 2
    c: Coincident(g13,g14)
    c: Coincident(g14,g15)
    c: Coincident(g15,g16)
    c: Coincident(g16,g13)
    c: Horizontal(g13)
    c: Horizontal(g15)
    c: Vertical(g14)
    c: Vertical(g16)
    c: Equal(g11,g15)
    c: Equal(g10,g14)
    c: Horizontal(g1,g5)
    c: Horizontal(g5,g9)
    c: Horizontal(g9,g13)
    c: Coincident(g17,g18)
    c: Coincident(g18,g19)
    c: Coincident(g19,g20)
    c: Coincident(g20,g17)
    c: Horizontal(g17)
    c: Horizontal(g19)
    c: Vertical(g18)
    c: Vertical(g20)
    c: Equal(g4,g20) = 2
    c: Equal(g3,g19) = 0.2
    c: Coincident(g21,g22)
    c: Coincident(g22,g23)
    c: Coincident(g23,g24)
    c: Coincident(g24,g21)
    c: Horizontal(g21)
    c: Horizontal(g23)
    c: Vertical(g22)
    c: Vertical(g24)
    c: Equal(g20,g24) = 2
    c: Equal(g19,g23) = 0.2
    c: Coincident(g25,g26)
    c: Coincident(g26,g27)
    c: Coincident(g27,g28)
    c: Coincident(g28,g25)
    c: Horizontal(g25)
    c: Horizontal(g27)
    c: Vertical(g26)
    c: Vertical(g28)
    c: Equal(g24,g28) = 2
    c: Equal(g23,g27) = 0.2
    c: DistanceX(g25,g21) = 2
    c: Coincident(g29,g30)
    c: Coincident(g30,g31)
    c: Coincident(g31,g32)
    c: Coincident(g32,g29)
    c: Horizontal(g29)
    c: Horizontal(g31)
    c: Vertical(g30)
    c: Vertical(g32)
    c: Equal(g27,g31)
    c: Equal(g26,g30)
    c: Horizontal(g17,g21)
    c: Horizontal(g21,g25)
    c: Horizontal(g25,g29)
    c: PointOnObject(g17,g-1)
    c: Coincident(g33,g34)
    c: Coincident(g34,g35)
    c: Coincident(g35,g36)
    c: Coincident(g36,g33)
    c: Horizontal(g33)
    c: Horizontal(g35)
    c: Vertical(g34)
    c: Vertical(g36)
    c: Coincident(g37,g38)
    c: Coincident(g38,g39)
    c: Coincident(g39,g40)
    c: Coincident(g40,g37)
    c: Horizontal(g37)
    c: Horizontal(g39)
    c: Vertical(g38)
    c: Vertical(g40)
    c: Equal(g36,g40) = 2
    c: Equal(g35,g39) = 0.2
    c: Coincident(g41,g42)
    c: Coincident(g42,g43)
    c: Coincident(g43,g44)
    c: Coincident(g44,g41)
    c: Horizontal(g41)
    c: Horizontal(g43)
    c: Vertical(g42)
    c: Vertical(g44)
    c: Equal(g40,g44) = 2
    c: Equal(g39,g43) = 0.2
    c: DistanceX(g41,g37) = 2
    c: Coincident(g45,g46)
    c: Coincident(g46,g47)
    c: Coincident(g47,g48)
    c: Coincident(g48,g45)
    c: Horizontal(g45)
    c: Horizontal(g47)
    c: Vertical(g46)
    c: Vertical(g48)
    c: Equal(g43,g47)
    c: Equal(g42,g46)
    c: Horizontal(g33,g37)
    c: Horizontal(g37,g41)
    c: Horizontal(g41,g45)
    c: PointOnObject(g33,g-1)
    c: Coincident(g49,g50)
    c: Coincident(g50,g51)
    c: Coincident(g51,g52)
    c: Coincident(g52,g49)
    c: Horizontal(g49)
    c: Horizontal(g51)
    c: Vertical(g50)
    c: Vertical(g52)
    c: Equal(g4,g52) = 2
    c: Equal(g3,g51) = 0.2
    c: Coincident(g53,g54)
    c: Coincident(g54,g55)
    c: Coincident(g55,g56)
    c: Coincident(g56,g53)
    c: Horizontal(g53)
    c: Horizontal(g55)
    c: Vertical(g54)
    c: Vertical(g56)
    c: Equal(g52,g56) = 2
    c: Equal(g51,g55) = 0.2
    c: Coincident(g57,g58)
    c: Coincident(g58,g59)
    c: Coincident(g59,g60)
    c: Coincident(g60,g57)
    c: Horizontal(g57)
    c: Horizontal(g59)
    c: Vertical(g58)
    c: Vertical(g60)
    c: Equal(g56,g60) = 2
    c: Equal(g55,g59) = 0.2
    c: DistanceX(g57,g53) = 2
    c: Coincident(g61,g62)
    c: Coincident(g62,g63)
    c: Coincident(g63,g64)
    c: Coincident(g64,g61)
    c: Horizontal(g61)
    c: Horizontal(g63)
    c: Vertical(g62)
    c: Vertical(g64)
    c: Equal(g59,g63)
    c: Equal(g58,g62)
    c: Horizontal(g49,g53)
    c: Horizontal(g53,g57)
    c: Horizontal(g57,g61)
    c: Coincident(g65,g66)
    c: Coincident(g66,g67)
    c: Coincident(g67,g68)
    c: Coincident(g68,g65)
    c: Horizontal(g65)
    c: Horizontal(g67)
    c: Vertical(g66)
    c: Vertical(g68)
    c: Equal(g52,g68) = 2
    c: Equal(g51,g67) = 0.2
    c: Coincident(g69,g70)
    c: Coincident(g70,g71)
    c: Coincident(g71,g72)
    c: Coincident(g72,g69)
    c: Horizontal(g69)
    c: Horizontal(g71)
    c: Vertical(g70)
    c: Vertical(g72)
    c: Equal(g68,g72) = 2
    c: Equal(g67,g71) = 0.2
    c: Coincident(g73,g74)
    c: Coincident(g74,g75)
    c: Coincident(g75,g76)
    c: Coincident(g76,g73)
    c: Horizontal(g73)
    c: Horizontal(g75)
    c: Vertical(g74)
    c: Vertical(g76)
    c: Equal(g72,g76) = 2
    c: Equal(g71,g75) = 0.2
    c: DistanceX(g73,g69) = 2
    c: Coincident(g77,g78)
    c: Coincident(g78,g79)
    c: Coincident(g79,g80)
    c: Coincident(g80,g77)
    c: Horizontal(g77)
    c: Horizontal(g79)
    c: Vertical(g78)
    c: Vertical(g80)
    c: Equal(g75,g79)
    c: Equal(g74,g78)
    c: Horizontal(g65,g69)
    c: Horizontal(g69,g73)
    c: Horizontal(g73,g77)
    c: Coincident(g81,g82)
    c: Coincident(g82,g83)
    c: Coincident(g83,g84)
    c: Coincident(g84,g81)
    c: Horizontal(g81)
    c: Horizontal(g83)
    c: Vertical(g82)
    c: Vertical(g84)
    c: Coincident(g85,g86)
    c: Coincident(g86,g87)
    c: Coincident(g87,g88)
    c: Coincident(g88,g85)
    c: Horizontal(g85)
    c: Horizontal(g87)
    c: Vertical(g86)
    c: Vertical(g88)
    c: Equal(g84,g88) = 2
    c: Equal(g83,g87) = 0.2
    c: Coincident(g89,g90)
    c: Coincident(g90,g91)
    c: Coincident(g91,g92)
    c: Coincident(g92,g89)
    c: Horizontal(g89)
    c: Horizontal(g91)
    c: Vertical(g90)
    c: Vertical(g92)
    c: Equal(g88,g92) = 2
    c: Equal(g87,g91) = 0.2
    c: DistanceX(g89,g85) = 2
    c: Coincident(g93,g94)
    c: Coincident(g94,g95)
    c: Coincident(g95,g96)
    c: Coincident(g96,g93)
    c: Horizontal(g93)
    c: Horizontal(g95)
    c: Vertical(g94)
    c: Vertical(g96)
    c: Equal(g91,g95)
    c: Equal(g90,g94)
    c: Horizontal(g81,g85)
    c: Horizontal(g85,g89)
    c: Horizontal(g89,g93)
    c: PointOnObject(g49,g-1)
    c: PointOnObject(g65,g-1)
    c: DistanceX(g53,g49) = 2
    c: DistanceX(g69,g65) = 2
    c: PointOnObject(g81,g-1)
    c: DistanceX(g37,g33) = 2
    c: DistanceX(g21,g17) = 2
    c: DistanceX(g5,g1) = 2
    c: Coincident(g97,g98)
    c: Coincident(g98,g99)
    c: Coincident(g99,g100)
    c: Coincident(g100,g97)
    c: Horizontal(g97)
    c: Horizontal(g99)
    c: Vertical(g98)
    c: Vertical(g100)
    c: Equal(g4,g100) = 2
    c: Equal(g3,g99) = 0.2
    c: Coincident(g101,g102)
    c: Coincident(g102,g103)
    c: Coincident(g103,g104)
    c: Coincident(g104,g101)
    c: Horizontal(g101)
    c: Horizontal(g103)
    c: Vertical(g102)
    c: Vertical(g104)
    c: Equal(g100,g104) = 2
    c: Equal(g99,g103) = 0.2
    c: Coincident(g105,g106)
    c: Coincident(g106,g107)
    c: Coincident(g107,g108)
    c: Coincident(g108,g105)
    c: Horizontal(g105)
    c: Horizontal(g107)
    c: Vertical(g106)
    c: Vertical(g108)
    c: Equal(g104,g108) = 2
    c: Equal(g103,g107) = 0.2
    c: DistanceX(g105,g101) = 2
    c: Coincident(g109,g110)
    c: Coincident(g110,g111)
    c: Coincident(g111,g112)
    c: Coincident(g112,g109)
    c: Horizontal(g109)
    c: Horizontal(g111)
    c: Vertical(g110)
    c: Vertical(g112)
    c: Equal(g107,g111)
    c: Equal(g106,g110)
    c: Horizontal(g97,g101)
    c: Horizontal(g101,g105)
    c: Horizontal(g105,g109)
    c: Coincident(g113,g114)
    c: Coincident(g114,g115)
    c: Coincident(g115,g116)
    c: Coincident(g116,g113)
    c: Horizontal(g113)
    c: Horizontal(g115)
    c: Vertical(g114)
    c: Vertical(g116)
    c: Equal(g100,g116) = 2
    c: Equal(g99,g115) = 0.2
    c: Coincident(g117,g118)
    c: Coincident(g118,g119)
    c: Coincident(g119,g120)
    c: Coincident(g120,g117)
    c: Horizontal(g117)
    c: Horizontal(g119)
    c: Vertical(g118)
    c: Vertical(g120)
    c: Equal(g116,g120) = 2
    c: Equal(g115,g119) = 0.2
    c: Coincident(g121,g122)
    c: Coincident(g122,g123)
    c: Coincident(g123,g124)
    c: Coincident(g124,g121)
    c: Horizontal(g121)
    c: Horizontal(g123)
    c: Vertical(g122)
    c: Vertical(g124)
    c: Equal(g120,g124) = 2
    c: Equal(g119,g123) = 0.2
    c: DistanceX(g121,g117) = 2
    c: Coincident(g125,g126)
    c: Coincident(g126,g127)
    c: Coincident(g127,g128)
    c: Coincident(g128,g125)
    c: Horizontal(g125)
    c: Horizontal(g127)
    c: Vertical(g126)
    c: Vertical(g128)
    c: Equal(g123,g127)
    c: Equal(g122,g126)
    c: Horizontal(g113,g117)
    c: Horizontal(g117,g121)
    c: Horizontal(g121,g125)
    c: Coincident(g129,g130)
    c: Coincident(g130,g131)
    c: Coincident(g131,g132)
    c: Coincident(g132,g129)
    c: Horizontal(g129)
    c: Horizontal(g131)
    c: Vertical(g130)
    c: Vertical(g132)
    c: Coincident(g133,g134)
    c: Coincident(g134,g135)
    c: Coincident(g135,g136)
    c: Coincident(g136,g133)
    c: Horizontal(g133)
    c: Horizontal(g135)
    c: Vertical(g134)
    c: Vertical(g136)
    c: Equal(g132,g136) = 2
    c: Equal(g131,g135) = 0.2
    c: Coincident(g137,g138)
    c: Coincident(g138,g139)
    c: Coincident(g139,g140)
    c: Coincident(g140,g137)
    c: Horizontal(g137)
    c: Horizontal(g139)
    c: Vertical(g138)
    c: Vertical(g140)
    c: Equal(g136,g140) = 2
    c: Equal(g135,g139) = 0.2
    c: DistanceX(g137,g133) = 2
    c: Coincident(g141,g142)
    c: Coincident(g142,g143)
    c: Coincident(g143,g144)
    c: Coincident(g144,g141)
    c: Horizontal(g141)
    c: Horizontal(g143)
    c: Vertical(g142)
    c: Vertical(g144)
    c: Equal(g139,g143)
    c: Equal(g138,g142)
    c: Horizontal(g129,g133)
    c: Horizontal(g133,g137)
    c: Horizontal(g137,g141)
    c: Coincident(g145,g146)
    c: Coincident(g146,g147)
    c: Coincident(g147,g148)
    c: Coincident(g148,g145)
    c: Horizontal(g145)
    c: Horizontal(g147)
    c: Vertical(g146)
    c: Vertical(g148)
    c: Equal(g100,g148) = 2
    c: Equal(g99,g147) = 0.2
    c: Coincident(g149,g150)
    c: Coincident(g150,g151)
    c: Coincident(g151,g152)
    c: Coincident(g152,g149)
    c: Horizontal(g149)
    c: Horizontal(g151)
    c: Vertical(g150)
    c: Vertical(g152)
    c: Equal(g148,g152) = 2
    c: Equal(g147,g151) = 0.2
    c: Coincident(g153,g154)
    c: Coincident(g154,g155)
    c: Coincident(g155,g156)
    c: Coincident(g156,g153)
    c: Horizontal(g153)
    c: Horizontal(g155)
    c: Vertical(g154)
    c: Vertical(g156)
    c: Equal(g152,g156) = 2
    c: Equal(g151,g155) = 0.2
    c: DistanceX(g153,g149) = 2
    c: Coincident(g157,g158)
    c: Coincident(g158,g159)
    c: Coincident(g159,g160)
    c: Coincident(g160,g157)
    c: Horizontal(g157)
    c: Horizontal(g159)
    c: Vertical(g158)
    c: Vertical(g160)
    c: Equal(g155,g159)
    c: Equal(g154,g158)
    c: Horizontal(g145,g149)
    c: Horizontal(g149,g153)
    c: Horizontal(g153,g157)
    c: Coincident(g161,g162)
    c: Coincident(g162,g163)
    c: Coincident(g163,g164)
    c: Coincident(g164,g161)
    c: Horizontal(g161)
    c: Horizontal(g163)
    c: Vertical(g162)
    c: Vertical(g164)
    c: Equal(g148,g164) = 2
    c: Equal(g147,g163) = 0.2
    c: Coincident(g165,g166)
    c: Coincident(g166,g167)
    c: Coincident(g167,g168)
    c: Coincident(g168,g165)
    c: Horizontal(g165)
    c: Horizontal(g167)
    c: Vertical(g166)
    c: Vertical(g168)
    c: Equal(g164,g168) = 2
    c: Equal(g163,g167) = 0.2
    c: Coincident(g169,g170)
    c: Coincident(g170,g171)
    c: Coincident(g171,g172)
    c: Coincident(g172,g169)
    c: Horizontal(g169)
    c: Horizontal(g171)
    c: Vertical(g170)
    c: Vertical(g172)
    c: Equal(g168,g172) = 2
    c: Equal(g167,g171) = 0.2
    c: DistanceX(g169,g165) = 2
    c: Coincident(g173,g174)
    c: Coincident(g174,g175)
    c: Coincident(g175,g176)
    c: Coincident(g176,g173)
    c: Horizontal(g173)
    c: Horizontal(g175)
    c: Vertical(g174)
    c: Vertical(g176)
    c: Equal(g171,g175)
    c: Equal(g170,g174)
    c: Horizontal(g161,g165)
    c: Horizontal(g165,g169)
    c: Horizontal(g169,g173)
    c: Coincident(g177,g178)
    c: Coincident(g178,g179)
    c: Coincident(g179,g180)
    c: Coincident(g180,g177)
    c: Horizontal(g177)
    c: Horizontal(g179)
    c: Vertical(g178)
    c: Vertical(g180)
    c: Coincident(g181,g182)
    c: Coincident(g182,g183)
    c: Coincident(g183,g184)
    c: Coincident(g184,g181)
    c: Horizontal(g181)
    c: Horizontal(g183)
    c: Vertical(g182)
    c: Vertical(g184)
    c: Equal(g180,g184) = 2
    c: Equal(g179,g183) = 0.2
    c: Coincident(g185,g186)
    c: Coincident(g186,g187)
    c: Coincident(g187,g188)
    c: Coincident(g188,g185)
    c: Horizontal(g185)
    c: Horizontal(g187)
    c: Vertical(g186)
    c: Vertical(g188)
    c: Equal(g184,g188) = 2
    c: Equal(g183,g187) = 0.2
    c: DistanceX(g185,g181) = 2
    c: Coincident(g189,g190)
    c: Coincident(g190,g191)
    c: Coincident(g191,g192)
    c: Coincident(g192,g189)
    c: Horizontal(g189)
    c: Horizontal(g191)
    c: Vertical(g190)
    c: Vertical(g192)
    c: Equal(g187,g191)
    c: Equal(g186,g190)
    c: Horizontal(g177,g181)
    c: Horizontal(g181,g185)
    c: Horizontal(g185,g189)
    c: DistanceX(g149,g145) = 2
    c: DistanceX(g165,g161) = 2
    c: DistanceX(g133,g129) = 2
    c: DistanceX(g117,g113) = 2
    c: DistanceX(g17,g13) = 4
    c: DistanceX(g13,g9) = 2
    c: DistanceX(g33,g29) = 4
    c: DistanceX(g49,g45) = 4
    c: DistanceX(g45,g41) = 2
    c: DistanceX(g61,g57) = 2
    c: DistanceX(g65,g61) = 4
    c: DistanceX(g77,g73) = 2
    c: DistanceX(g85,g81) = 2
    c: DistanceX(g81,g77) = 4
    c: DistanceX(g93,g89) = 2
    c: PointOnObject(g97,g-1)
    c: DistanceX(g97,g93) = 4
    c: DistanceX(g101,g97) = 2
    c: DistanceX(g109,g105) = 2
    c: DistanceX(g113,g109) = 4
    c: PointOnObject(g113,g-1)
    c: PointOnObject(g129,g-1)
    c: DistanceX(g125,g121) = 2
    c: DistanceX(g129,g125) = 4
    c: PointOnObject(g145,g-1)
    c: DistanceX(g141,g137) = 2
    c: DistanceX(g145,g141) = 4
    c: PointOnObject(g161,g-1)
    c: DistanceX(g157,g153) = 2
    c: DistanceX(g161,g157) = 4
    c: PointOnObject(g177,g-1)
    c: DistanceX(g173,g169) = 2
    c: DistanceX(g177,g173) = 4
    c: DistanceX(g181,g177) = 2
    c: DistanceX(g29,g25) = 2
    c: DistanceX(g189,g185) = 2
    c: Equal(g31,g35)
    c: Equal(g30,g36)
    c: Equal(g79,g83)
    c: Equal(g78,g84)
    c: Equal(g126,g132)
    c: Equal(g127,g131)
    c: Equal(g175,g179)
    c: Equal(g174,g180)
    c: Coincident(g193,g194)
    c: Coincident(g194,g195)
    c: Coincident(g195,g196)
    c: Coincident(g196,g193)
    c: Horizontal(g193)
    c: Horizontal(g195)
    c: Vertical(g194)
    c: Vertical(g196)
    c: Coincident(g197,g198)
    c: Coincident(g198,g199)
    c: Coincident(g199,g200)
    c: Coincident(g200,g197)
    c: Horizontal(g197)
    c: Horizontal(g199)
    c: Vertical(g198)
    c: Vertical(g200)
    c: Equal(g196,g200) = 2
    c: Equal(g195,g199) = 0.2
    c: Coincident(g201,g202)
    c: Coincident(g202,g203)
    c: Coincident(g203,g204)
    c: Coincident(g204,g201)
    c: Horizontal(g201)
    c: Horizontal(g203)
    c: Vertical(g202)
    c: Vertical(g204)
    c: Equal(g200,g204) = 2
    c: Equal(g199,g203) = 0.2
    c: DistanceX(g201,g197) = 2
    c: Coincident(g205,g206)
    c: Coincident(g206,g207)
    c: Coincident(g207,g208)
    c: Coincident(g208,g205)
    c: Horizontal(g205)
    c: Horizontal(g207)
    c: Vertical(g206)
    c: Vertical(g208)
    c: Equal(g203,g207)
    c: Equal(g202,g206)
    c: Horizontal(g193,g197)
    c: Horizontal(g197,g201)
    c: Horizontal(g201,g205)
    c: DistanceX(g197,g193) = 2
    c: DistanceX(g205,g201) = 2
    c: Equal(g191,g195)
    c: Equal(g192,g196)
    c: DistanceX(g193,g189) = 4
    c: Horizontal(g193,g189)
    c: Coincident(g209,g210)
    c: Coincident(g210,g211)
    c: Coincident(g211,g212)
    c: Coincident(g212,g209)
    c: Horizontal(g209)
    c: Horizontal(g211)
    c: Vertical(g210)
    c: Vertical(g212)
    c: Coincident(g213,g214)
    c: Coincident(g214,g215)
    c: Coincident(g215,g216)
    c: Coincident(g216,g213)
    c: Horizontal(g213)
    c: Horizontal(g215)
    c: Vertical(g214)
    c: Vertical(g216)
    c: Equal(g212,g216) = 2
    c: Equal(g211,g215) = 0.2
    c: Coincident(g217,g218)
    c: Coincident(g218,g219)
    c: Coincident(g219,g220)
    c: Coincident(g220,g217)
    c: Horizontal(g217)
    c: Horizontal(g219)
    c: Vertical(g218)
    c: Vertical(g220)
    c: Equal(g216,g220) = 2
    c: Equal(g215,g219) = 0.2
    c: DistanceX(g217,g213) = 2
    c: Coincident(g221,g222)
    c: Coincident(g222,g223)
    c: Coincident(g223,g224)
    c: Coincident(g224,g221)
    c: Horizontal(g221)
    c: Horizontal(g223)
    c: Vertical(g222)
    c: Vertical(g224)
    c: Equal(g219,g223)
    c: Equal(g218,g222)
    c: Horizontal(g209,g213)
    c: Horizontal(g213,g217)
    c: Horizontal(g217,g221)
    c: Coincident(g225,g226)
    c: Coincident(g226,g227)
    c: Coincident(g227,g228)
    c: Coincident(g228,g225)
    c: Horizontal(g225)
    c: Horizontal(g227)
    c: Vertical(g226)
    c: Vertical(g228)
    c: Coincident(g229,g230)
    c: Coincident(g230,g231)
    c: Coincident(g231,g232)
    c: Coincident(g232,g229)
    c: Horizontal(g229)
    c: Horizontal(g231)
    c: Vertical(g230)
    c: Vertical(g232)
    c: Equal(g228,g232) = 2
    c: Equal(g227,g231) = 0.2
    c: Coincident(g233,g234)
    c: Coincident(g234,g235)
    c: Coincident(g235,g236)
    c: Coincident(g236,g233)
    c: Horizontal(g233)
    c: Horizontal(g235)
    c: Vertical(g234)
    c: Vertical(g236)
    c: Equal(g232,g236) = 2
    c: Equal(g231,g235) = 0.2
    c: DistanceX(g233,g229) = 2
    c: Coincident(g237,g238)
    c: Coincident(g238,g239)
    c: Coincident(g239,g240)
    c: Coincident(g240,g237)
    c: Horizontal(g237)
    c: Horizontal(g239)
    c: Vertical(g238)
    c: Vertical(g240)
    c: Equal(g235,g239)
    c: Equal(g234,g238)
    c: Horizontal(g225,g229)
    c: Horizontal(g229,g233)
    c: Horizontal(g233,g237)
    c: DistanceX(g213,g209) = 2
    c: DistanceX(g221,g217) = 2
    c: DistanceX(g225,g221) = 4
    c: DistanceX(g229,g225) = 2
    c: DistanceX(g237,g233) = 2
    c: Equal(g223,g227)
    c: Equal(g222,g228)
    c: Coincident(g241,g242)
    c: Coincident(g242,g243)
    c: Coincident(g243,g244)
    c: Coincident(g244,g241)
    c: Horizontal(g241)
    c: Horizontal(g243)
    c: Vertical(g242)
    c: Vertical(g244)
    c: Coincident(g245,g246)
    c: Coincident(g246,g247)
    c: Coincident(g247,g248)
    c: Coincident(g248,g245)
    c: Horizontal(g245)
    c: Horizontal(g247)
    c: Vertical(g246)
    c: Vertical(g248)
    c: Equal(g244,g248) = 2
    c: Equal(g243,g247) = 0.2
    c: Coincident(g249,g250)
    c: Coincident(g250,g251)
    c: Coincident(g251,g252)
    c: Coincident(g252,g249)
    c: Horizontal(g249)
    c: Horizontal(g251)
    c: Vertical(g250)
    c: Vertical(g252)
    c: Equal(g248,g252) = 2
    c: Equal(g247,g251) = 0.2
    c: DistanceX(g249,g245) = 2
    c: Coincident(g253,g254)
    c: Coincident(g254,g255)
    c: Coincident(g255,g256)
    c: Coincident(g256,g253)
    c: Horizontal(g253)
    c: Horizontal(g255)
    c: Vertical(g254)
    c: Vertical(g256)
    c: Equal(g251,g255)
    c: Equal(g250,g254)
    c: Horizontal(g241,g245)
    c: Horizontal(g245,g249)
    c: Horizontal(g249,g253)
    c: DistanceX(g245,g241) = 2
    c: DistanceX(g253,g249) = 2
    c: Equal(g239,g243)
    c: Equal(g240,g244)
    c: DistanceX(g241,g237) = 4
    c: Horizontal(g241,g237)
    c: Horizontal(g221,g225)
    c: Equal(g208,g210)
    c: Equal(g207,g211)
    c: Horizontal(g209,g205)
    c: DistanceX(g209,g205) = 4
    c: DistanceX(g-1,g254) = 81.8
    c: Coincident(g257,g258)
    c: Coincident(g258,g259)
    c: Coincident(g259,g260)
    c: Coincident(g260,g257)
    c: Horizontal(g257)
    c: Horizontal(g259)
    c: Vertical(g258)
    c: Vertical(g260)
    c: Equal(g4,g260) = 2
    c: Equal(g3,g259) = 0.2
    c: Coincident(g261,g262)
    c: Coincident(g262,g263)
    c: Coincident(g263,g264)
    c: Coincident(g264,g261)
    c: Horizontal(g261)
    c: Horizontal(g263)
    c: Vertical(g262)
    c: Vertical(g264)
    c: Equal(g260,g264) = 2
    c: Equal(g259,g263) = 0.2
    c: Coincident(g265,g266)
    c: Coincident(g266,g267)
    c: Coincident(g267,g268)
    c: Coincident(g268,g265)
    c: Horizontal(g265)
    c: Horizontal(g267)
    c: Vertical(g266)
    c: Vertical(g268)
    c: Equal(g264,g268) = 2
    c: Equal(g263,g267) = 0.2
    c: DistanceX(g265,g261) = 2
    c: Coincident(g269,g270)
    c: Coincident(g270,g271)
    c: Coincident(g271,g272)
    c: Coincident(g272,g269)
    c: Horizontal(g269)
    c: Horizontal(g271)
    c: Vertical(g270)
    c: Vertical(g272)
    c: Equal(g267,g271)
    c: Equal(g266,g270)
    c: Horizontal(g257,g261)
    c: Horizontal(g261,g265)
    c: Horizontal(g265,g269)
    c: Coincident(g273,g274)
    c: Coincident(g274,g275)
    c: Coincident(g275,g276)
    c: Coincident(g276,g273)
    c: Horizontal(g273)
    c: Horizontal(g275)
    c: Vertical(g274)
    c: Vertical(g276)
    c: Equal(g260,g276) = 2
    c: Equal(g259,g275) = 0.2
    c: Coincident(g277,g278)
    c: Coincident(g278,g279)
    c: Coincident(g279,g280)
    c: Coincident(g280,g277)
    c: Horizontal(g277)
    c: Horizontal(g279)
    c: Vertical(g278)
    c: Vertical(g280)
    c: Equal(g276,g280) = 2
    c: Equal(g275,g279) = 0.2
    c: Coincident(g281,g282)
    c: Coincident(g282,g283)
    c: Coincident(g283,g284)
    c: Coincident(g284,g281)
    c: Horizontal(g281)
    c: Horizontal(g283)
    c: Vertical(g282)
    c: Vertical(g284)
    c: Equal(g280,g284) = 2
    c: Equal(g279,g283) = 0.2
    c: DistanceX(g281,g277) = 2
    c: Coincident(g285,g286)
    c: Coincident(g286,g287)
    c: Coincident(g287,g288)
    c: Coincident(g288,g285)
    c: Horizontal(g285)
    c: Horizontal(g287)
    c: Vertical(g286)
    c: Vertical(g288)
    c: Equal(g283,g287)
    c: Equal(g282,g286)
    c: Horizontal(g273,g277)
    c: Horizontal(g277,g281)
    c: Horizontal(g281,g285)
    c: Coincident(g289,g290)
    c: Coincident(g290,g291)
    c: Coincident(g291,g292)
    c: Coincident(g292,g289)
    c: Horizontal(g289)
    c: Horizontal(g291)
    c: Vertical(g290)
    c: Vertical(g292)
    c: Coincident(g293,g294)
    c: Coincident(g294,g295)
    c: Coincident(g295,g296)
    c: Coincident(g296,g293)
    c: Horizontal(g293)
    c: Horizontal(g295)
    c: Vertical(g294)
    c: Vertical(g296)
    c: Equal(g292,g296) = 2
    c: Equal(g291,g295) = 0.2
    c: Coincident(g297,g298)
    c: Coincident(g298,g299)
    c: Coincident(g299,g300)
    c: Coincident(g300,g297)
    c: Horizontal(g297)
    c: Horizontal(g299)
    c: Vertical(g298)
    c: Vertical(g300)
    c: Equal(g296,g300) = 2
    c: Equal(g295,g299) = 0.2
    c: DistanceX(g297,g293) = 2
    c: Coincident(g301,g302)
    c: Coincident(g302,g303)
    c: Coincident(g303,g304)
    c: Coincident(g304,g301)
    c: Horizontal(g301)
    c: Horizontal(g303)
    c: Vertical(g302)
    c: Vertical(g304)
    c: Equal(g299,g303)
    c: Equal(g298,g302)
    c: Horizontal(g289,g293)
    c: Horizontal(g293,g297)
    c: Horizontal(g297,g301)
    c: Coincident(g305,g306)
    c: Coincident(g306,g307)
    c: Coincident(g307,g308)
    c: Coincident(g308,g305)
    c: Horizontal(g305)
    c: Horizontal(g307)
    c: Vertical(g306)
    c: Vertical(g308)
    c: Equal(g260,g308) = 2
    c: Equal(g259,g307) = 0.2
    c: Coincident(g309,g310)
    c: Coincident(g310,g311)
    c: Coincident(g311,g312)
    c: Coincident(g312,g309)
    c: Horizontal(g309)
    c: Horizontal(g311)
    c: Vertical(g310)
    c: Vertical(g312)
    c: Equal(g308,g312) = 2
    c: Equal(g307,g311) = 0.2
    c: Coincident(g313,g314)
    c: Coincident(g314,g315)
    c: Coincident(g315,g316)
    c: Coincident(g316,g313)
    c: Horizontal(g313)
    c: Horizontal(g315)
    c: Vertical(g314)
    c: Vertical(g316)
    c: Equal(g312,g316) = 2
    c: Equal(g311,g315) = 0.2
    c: DistanceX(g313,g309) = 2
    c: Coincident(g317,g318)
    c: Coincident(g318,g319)
    c: Coincident(g319,g320)
    c: Coincident(g320,g317)
    c: Horizontal(g317)
    c: Horizontal(g319)
    c: Vertical(g318)
    c: Vertical(g320)
    c: Equal(g315,g319)
    c: Equal(g314,g318)
    c: Horizontal(g305,g309)
    c: Horizontal(g309,g313)
    c: Horizontal(g313,g317)
    c: Coincident(g321,g322)
    c: Coincident(g322,g323)
    c: Coincident(g323,g324)
    c: Coincident(g324,g321)
    c: Horizontal(g321)
    c: Horizontal(g323)
    c: Vertical(g322)
    c: Vertical(g324)
    c: Equal(g308,g324) = 2
    c: Equal(g307,g323) = 0.2
    c: Coincident(g325,g326)
    c: Coincident(g326,g327)
    c: Coincident(g327,g328)
    c: Coincident(g328,g325)
    c: Horizontal(g325)
    c: Horizontal(g327)
    c: Vertical(g326)
    c: Vertical(g328)
    c: Equal(g324,g328) = 2
    c: Equal(g323,g327) = 0.2
    c: Coincident(g329,g330)
    c: Coincident(g330,g331)
    c: Coincident(g331,g332)
    c: Coincident(g332,g329)
    c: Horizontal(g329)
    c: Horizontal(g331)
    c: Vertical(g330)
    c: Vertical(g332)
    c: Equal(g328,g332) = 2
    c: Equal(g327,g331) = 0.2
    c: DistanceX(g329,g325) = 2
    c: Coincident(g333,g334)
    c: Coincident(g334,g335)
    c: Coincident(g335,g336)
    c: Coincident(g336,g333)
    c: Horizontal(g333)
    c: Horizontal(g335)
    c: Vertical(g334)
    c: Vertical(g336)
    c: Equal(g331,g335)
    c: Equal(g330,g334)
    c: Horizontal(g321,g325)
    c: Horizontal(g325,g329)
    c: Horizontal(g329,g333)
    c: Coincident(g337,g338)
    c: Coincident(g338,g339)
    c: Coincident(g339,g340)
    c: Coincident(g340,g337)
    c: Horizontal(g337)
    c: Horizontal(g339)
    c: Vertical(g338)
    c: Vertical(g340)
    c: Coincident(g341,g342)
    c: Coincident(g342,g343)
    c: Coincident(g343,g344)
    c: Coincident(g344,g341)
    c: Horizontal(g341)
    c: Horizontal(g343)
    c: Vertical(g342)
    c: Vertical(g344)
    c: Equal(g340,g344) = 2
    c: Equal(g339,g343) = 0.2
    c: Coincident(g345,g346)
    c: Coincident(g346,g347)
    c: Coincident(g347,g348)
    c: Coincident(g348,g345)
    c: Horizontal(g345)
    c: Horizontal(g347)
    c: Vertical(g346)
    c: Vertical(g348)
    c: Equal(g344,g348) = 2
    c: Equal(g343,g347) = 0.2
    c: DistanceX(g345,g341) = 2
    c: Coincident(g349,g350)
    c: Coincident(g350,g351)
    c: Coincident(g351,g352)
    c: Coincident(g352,g349)
    c: Horizontal(g349)
    c: Horizontal(g351)
    c: Vertical(g350)
    c: Vertical(g352)
    c: Equal(g347,g351)
    c: Equal(g346,g350)
    c: Horizontal(g337,g341)
    c: Horizontal(g341,g345)
    c: Horizontal(g345,g349)
    c: DistanceX(g309,g305) = 2
    c: DistanceX(g325,g321) = 2
    c: DistanceX(g293,g289) = 2
    c: DistanceX(g277,g273) = 2
    c: DistanceX(g261,g257) = 2
    c: Coincident(g353,g354)
    c: Coincident(g354,g355)
    c: Coincident(g355,g356)
    c: Coincident(g356,g353)
    c: Horizontal(g353)
    c: Horizontal(g355)
    c: Vertical(g354)
    c: Vertical(g356)
    c: Equal(g260,g356) = 2
    c: Equal(g259,g355) = 0.2
    c: Coincident(g357,g358)
    c: Coincident(g358,g359)
    c: Coincident(g359,g360)
    c: Coincident(g360,g357)
    c: Horizontal(g357)
    c: Horizontal(g359)
    c: Vertical(g358)
    c: Vertical(g360)
    c: Equal(g356,g360) = 2
    c: Equal(g355,g359) = 0.2
    c: Coincident(g361,g362)
    c: Coincident(g362,g363)
    c: Coincident(g363,g364)
    c: Coincident(g364,g361)
    c: Horizontal(g361)
    c: Horizontal(g363)
    c: Vertical(g362)
    c: Vertical(g364)
    c: Equal(g360,g364) = 2
    c: Equal(g359,g363) = 0.2
    c: DistanceX(g361,g357) = 2
    c: Coincident(g365,g366)
    c: Coincident(g366,g367)
    c: Coincident(g367,g368)
    c: Coincident(g368,g365)
    c: Horizontal(g365)
    c: Horizontal(g367)
    c: Vertical(g366)
    c: Vertical(g368)
    c: Equal(g363,g367)
    c: Equal(g362,g366)
    c: Horizontal(g353,g357)
    c: Horizontal(g357,g361)
    c: Horizontal(g361,g365)
    c: Coincident(g369,g370)
    c: Coincident(g370,g371)
    c: Coincident(g371,g372)
    c: Coincident(g372,g369)
    c: Horizontal(g369)
    c: Horizontal(g371)
    c: Vertical(g370)
    c: Vertical(g372)
    c: Equal(g356,g372) = 2
    c: Equal(g355,g371) = 0.2
    c: Coincident(g373,g374)
    c: Coincident(g374,g375)
    c: Coincident(g375,g376)
    c: Coincident(g376,g373)
    c: Horizontal(g373)
    c: Horizontal(g375)
    c: Vertical(g374)
    c: Vertical(g376)
    c: Equal(g372,g376) = 2
    c: Equal(g371,g375) = 0.2
    c: Coincident(g377,g378)
    c: Coincident(g378,g379)
    c: Coincident(g379,g380)
    c: Coincident(g380,g377)
    c: Horizontal(g377)
    c: Horizontal(g379)
    c: Vertical(g378)
    c: Vertical(g380)
    c: Equal(g376,g380) = 2
    c: Equal(g375,g379) = 0.2
    c: DistanceX(g377,g373) = 2
    c: Coincident(g381,g382)
    c: Coincident(g382,g383)
    c: Coincident(g383,g384)
    c: Coincident(g384,g381)
    c: Horizontal(g381)
    c: Horizontal(g383)
    c: Vertical(g382)
    c: Vertical(g384)
    c: Equal(g379,g383)
    c: Equal(g378,g382)
    c: Horizontal(g369,g373)
    c: Horizontal(g373,g377)
    c: Horizontal(g377,g381)
    c: Coincident(g385,g386)
    c: Coincident(g386,g387)
    c: Coincident(g387,g388)
    c: Coincident(g388,g385)
    c: Horizontal(g385)
    c: Horizontal(g387)
    c: Vertical(g386)
    c: Vertical(g388)
    c: Coincident(g389,g390)
    c: Coincident(g390,g391)
    c: Coincident(g391,g392)
    c: Coincident(g392,g389)
    c: Horizontal(g389)
    c: Horizontal(g391)
    c: Vertical(g390)
    c: Vertical(g392)
    c: Equal(g388,g392) = 2
    c: Equal(g387,g391) = 0.2
    c: Coincident(g393,g394)
    c: Coincident(g394,g395)
    c: Coincident(g395,g396)
    c: Coincident(g396,g393)
    c: Horizontal(g393)
    c: Horizontal(g395)
    c: Vertical(g394)
    c: Vertical(g396)
    c: Equal(g392,g396) = 2
    c: Equal(g391,g395) = 0.2
    c: DistanceX(g393,g389) = 2
    c: Coincident(g397,g398)
    c: Coincident(g398,g399)
    c: Coincident(g399,g400)
    c: Coincident(g400,g397)
    c: Horizontal(g397)
    c: Horizontal(g399)
    c: Vertical(g398)
    c: Vertical(g400)
    c: Equal(g395,g399)
    c: Equal(g394,g398)
    c: Horizontal(g385,g389)
    c: Horizontal(g389,g393)
    c: Horizontal(g393,g397)
    c: Coincident(g401,g402)
    c: Coincident(g402,g403)
    c: Coincident(g403,g404)
    c: Coincident(g404,g401)
    c: Horizontal(g401)
    c: Horizontal(g403)
    c: Vertical(g402)
    c: Vertical(g404)
    c: Equal(g356,g404) = 2
    c: Equal(g355,g403) = 0.2
    c: Coincident(g405,g406)
    c: Coincident(g406,g407)
    c: Coincident(g407,g408)
    c: Coincident(g408,g405)
    c: Horizontal(g405)
    c: Horizontal(g407)
    c: Vertical(g406)
    c: Vertical(g408)
    c: Equal(g404,g408) = 2
    c: Equal(g403,g407) = 0.2
    c: Coincident(g409,g410)
    c: Coincident(g410,g411)
    c: Coincident(g411,g412)
    c: Coincident(g412,g409)
    c: Horizontal(g409)
    c: Horizontal(g411)
    c: Vertical(g410)
    c: Vertical(g412)
    c: Equal(g408,g412) = 2
    c: Equal(g407,g411) = 0.2
    c: DistanceX(g409,g405) = 2
    c: Coincident(g413,g414)
    c: Coincident(g414,g415)
    c: Coincident(g415,g416)
    c: Coincident(g416,g413)
    c: Horizontal(g413)
    c: Horizontal(g415)
    c: Vertical(g414)
    c: Vertical(g416)
    c: Equal(g411,g415)
    c: Equal(g410,g414)
    c: Horizontal(g401,g405)
    c: Horizontal(g405,g409)
    c: Horizontal(g409,g413)
    c: Coincident(g417,g418)
    c: Coincident(g418,g419)
    c: Coincident(g419,g420)
    c: Coincident(g420,g417)
    c: Horizontal(g417)
    c: Horizontal(g419)
    c: Vertical(g418)
    c: Vertical(g420)
    c: Equal(g404,g420) = 2
    c: Equal(g403,g419) = 0.2
    c: Coincident(g421,g422)
    c: Coincident(g422,g423)
    c: Coincident(g423,g424)
    c: Coincident(g424,g421)
    c: Horizontal(g421)
    c: Horizontal(g423)
    c: Vertical(g422)
    c: Vertical(g424)
    c: Equal(g420,g424) = 2
    c: Equal(g419,g423) = 0.2
    c: Coincident(g425,g426)
    c: Coincident(g426,g427)
    c: Coincident(g427,g428)
    c: Coincident(g428,g425)
    c: Horizontal(g425)
    c: Horizontal(g427)
    c: Vertical(g426)
    c: Vertical(g428)
    c: Equal(g424,g428) = 2
    c: Equal(g423,g427) = 0.2
    c: DistanceX(g425,g421) = 2
    c: Coincident(g429,g430)
    c: Coincident(g430,g431)
    c: Coincident(g431,g432)
    c: Coincident(g432,g429)
    c: Horizontal(g429)
    c: Horizontal(g431)
    c: Vertical(g430)
    c: Vertical(g432)
    c: Equal(g427,g431)
    c: Equal(g426,g430)
    c: Horizontal(g417,g421)
    c: Horizontal(g421,g425)
    c: Horizontal(g425,g429)
    c: Coincident(g433,g434)
    c: Coincident(g434,g435)
    c: Coincident(g435,g436)
    c: Coincident(g436,g433)
    c: Horizontal(g433)
    c: Horizontal(g435)
    c: Vertical(g434)
    c: Vertical(g436)
    c: Coincident(g437,g438)
    c: Coincident(g438,g439)
    c: Coincident(g439,g440)
    c: Coincident(g440,g437)
    c: Horizontal(g437)
    c: Horizontal(g439)
    c: Vertical(g438)
    c: Vertical(g440)
    c: Equal(g436,g440) = 2
    c: Equal(g435,g439) = 0.2
    c: Coincident(g441,g442)
    c: Coincident(g442,g443)
    c: Coincident(g443,g444)
    c: Coincident(g444,g441)
    c: Horizontal(g441)
    c: Horizontal(g443)
    c: Vertical(g442)
    c: Vertical(g444)
    c: Equal(g440,g444) = 2
    c: Equal(g439,g443) = 0.2
    c: DistanceX(g441,g437) = 2
    c: Coincident(g445,g446)
    c: Coincident(g446,g447)
    c: Coincident(g447,g448)
    c: Coincident(g448,g445)
    c: Horizontal(g445)
    c: Horizontal(g447)
    c: Vertical(g446)
    c: Vertical(g448)
    c: Equal(g443,g447)
    c: Equal(g442,g446)
    c: Horizontal(g433,g437)
    c: Horizontal(g437,g441)
    c: Horizontal(g441,g445)
    c: DistanceX(g405,g401) = 2
    c: DistanceX(g421,g417) = 2
    c: DistanceX(g389,g385) = 2
    c: DistanceX(g373,g369) = 2
    c: DistanceX(g273,g269) = 4
    c: DistanceX(g269,g265) = 2
    c: DistanceX(g289,g285) = 4
    c: DistanceX(g305,g301) = 4
    c: DistanceX(g301,g297) = 2
    c: DistanceX(g317,g313) = 2
    c: DistanceX(g321,g317) = 4
    c: DistanceX(g333,g329) = 2
    c: DistanceX(g341,g337) = 2
    c: DistanceX(g337,g333) = 4
    c: DistanceX(g349,g345) = 2
    c: DistanceX(g353,g349) = 4
    c: DistanceX(g357,g353) = 2
    c: DistanceX(g365,g361) = 2
    c: DistanceX(g369,g365) = 4
    c: DistanceX(g381,g377) = 2
    c: DistanceX(g385,g381) = 4
    c: DistanceX(g397,g393) = 2
    c: DistanceX(g401,g397) = 4
    c: DistanceX(g413,g409) = 2
    c: DistanceX(g417,g413) = 4
    c: DistanceX(g429,g425) = 2
    c: DistanceX(g433,g429) = 4
    c: DistanceX(g437,g433) = 2
    c: DistanceX(g285,g281) = 2
    c: DistanceX(g445,g441) = 2
    c: Equal(g287,g291)
    c: Equal(g286,g292)
    c: Equal(g335,g339)
    c: Equal(g334,g340)
    c: Equal(g382,g388)
    c: Equal(g383,g387)
    c: Equal(g431,g435)
    c: Equal(g430,g436)
    c: Coincident(g449,g450)
    c: Coincident(g450,g451)
    c: Coincident(g451,g452)
    c: Coincident(g452,g449)
    c: Horizontal(g449)
    c: Horizontal(g451)
    c: Vertical(g450)
    c: Vertical(g452)
    c: Coincident(g453,g454)
    c: Coincident(g454,g455)
    c: Coincident(g455,g456)
    c: Coincident(g456,g453)
    c: Horizontal(g453)
    c: Horizontal(g455)
    c: Vertical(g454)
    c: Vertical(g456)
    c: Equal(g452,g456) = 2
    c: Equal(g451,g455) = 0.2
    c: Coincident(g457,g458)
    c: Coincident(g458,g459)
    c: Coincident(g459,g460)
    c: Coincident(g460,g457)
    c: Horizontal(g457)
    c: Horizontal(g459)
    c: Vertical(g458)
    c: Vertical(g460)
    c: Equal(g456,g460) = 2
    c: Equal(g455,g459) = 0.2
    c: DistanceX(g457,g453) = 2
    c: Coincident(g461,g462)
    c: Coincident(g462,g463)
    c: Coincident(g463,g464)
    c: Coincident(g464,g461)
    c: Horizontal(g461)
    c: Horizontal(g463)
    c: Vertical(g462)
    c: Vertical(g464)
    c: Equal(g459,g463)
    c: Equal(g458,g462)
    c: Horizontal(g449,g453)
    c: Horizontal(g453,g457)
    c: Horizontal(g457,g461)
    c: DistanceX(g453,g449) = 2
    c: DistanceX(g461,g457) = 2
    c: Equal(g447,g451)
    c: Equal(g448,g452)
    c: DistanceX(g449,g445) = 4
    c: Horizontal(g449,g445)
    c: Coincident(g465,g466)
    c: Coincident(g466,g467)
    c: Coincident(g467,g468)
    c: Coincident(g468,g465)
    c: Horizontal(g465)
    c: Horizontal(g467)
    c: Vertical(g466)
    c: Vertical(g468)
    c: Coincident(g469,g470)
    c: Coincident(g470,g471)
    c: Coincident(g471,g472)
    c: Coincident(g472,g469)
    c: Horizontal(g469)
    c: Horizontal(g471)
    c: Vertical(g470)
    c: Vertical(g472)
    c: Equal(g468,g472) = 2
    c: Equal(g467,g471) = 0.2
    c: Coincident(g473,g474)
    c: Coincident(g474,g475)
    c: Coincident(g475,g476)
    c: Coincident(g476,g473)
    c: Horizontal(g473)
    c: Horizontal(g475)
    c: Vertical(g474)
    c: Vertical(g476)
    c: Equal(g472,g476) = 2
    c: Equal(g471,g475) = 0.2
    c: DistanceX(g473,g469) = 2
    c: Coincident(g477,g478)
    c: Coincident(g478,g479)
    c: Coincident(g479,g480)
    c: Coincident(g480,g477)
    c: Horizontal(g477)
    c: Horizontal(g479)
    c: Vertical(g478)
    c: Vertical(g480)
    c: Equal(g475,g479)
    c: Equal(g474,g478)
    c: Horizontal(g465,g469)
    c: Horizontal(g469,g473)
    c: Horizontal(g473,g477)
    c: Coincident(g481,g482)
    c: Coincident(g482,g483)
    c: Coincident(g483,g484)
    c: Coincident(g484,g481)
    c: Horizontal(g481)
    c: Horizontal(g483)
    c: Vertical(g482)
    c: Vertical(g484)
    c: Coincident(g485,g486)
    c: Coincident(g486,g487)
    c: Coincident(g487,g488)
    c: Coincident(g488,g485)
    c: Horizontal(g485)
    c: Horizontal(g487)
    c: Vertical(g486)
    c: Vertical(g488)
    c: Equal(g484,g488) = 2
    c: Equal(g483,g487) = 0.2
    c: Coincident(g489,g490)
    c: Coincident(g490,g491)
    c: Coincident(g491,g492)
    c: Coincident(g492,g489)
    c: Horizontal(g489)
    c: Horizontal(g491)
    c: Vertical(g490)
    c: Vertical(g492)
    c: Equal(g488,g492) = 2
    c: Equal(g487,g491) = 0.2
    c: DistanceX(g489,g485) = 2
    c: Coincident(g493,g494)
    c: Coincident(g494,g495)
    c: Coincident(g495,g496)
    c: Coincident(g496,g493)
    c: Horizontal(g493)
    c: Horizontal(g495)
    c: Vertical(g494)
    c: Vertical(g496)
    c: Equal(g491,g495)
    c: Equal(g490,g494)
    c: Horizontal(g481,g485)
    c: Horizontal(g485,g489)
    c: Horizontal(g489,g493)
    c: DistanceX(g469,g465) = 2
    c: DistanceX(g477,g473) = 2
    c: DistanceX(g481,g477) = 4
    c: DistanceX(g485,g481) = 2
    c: DistanceX(g493,g489) = 2
    c: Equal(g479,g483)
    c: Equal(g478,g484)
    c: Coincident(g497,g498)
    c: Coincident(g498,g499)
    c: Coincident(g499,g500)
    c: Coincident(g500,g497)
    c: Horizontal(g497)
    c: Horizontal(g499)
    c: Vertical(g498)
    c: Vertical(g500)
    c: Coincident(g501,g502)
    c: Coincident(g502,g503)
    c: Coincident(g503,g504)
    c: Coincident(g504,g501)
    c: Horizontal(g501)
    c: Horizontal(g503)
    c: Vertical(g502)
    c: Vertical(g504)
    c: Equal(g500,g504) = 2
    c: Equal(g499,g503) = 0.2
    c: Coincident(g505,g506)
    c: Coincident(g506,g507)
    c: Coincident(g507,g508)
    c: Coincident(g508,g505)
    c: Horizontal(g505)
    c: Horizontal(g507)
    c: Vertical(g506)
    c: Vertical(g508)
    c: Equal(g504,g508) = 2
    c: Equal(g503,g507) = 0.2
    c: DistanceX(g505,g501) = 2
    c: Coincident(g509,g510)
    c: Coincident(g510,g511)
    c: Coincident(g511,g512)
    c: Coincident(g512,g509)
    c: Horizontal(g509)
    c: Horizontal(g511)
    c: Vertical(g510)
    c: Vertical(g512)
    c: Equal(g507,g511)
    c: Equal(g506,g510)
    c: Horizontal(g497,g501)
    c: Horizontal(g501,g505)
    c: Horizontal(g505,g509)
    c: DistanceX(g501,g497) = 2
    c: DistanceX(g509,g505) = 2
    c: Equal(g495,g499)
    c: Equal(g496,g500)
    c: DistanceX(g497,g493) = 4
    c: Horizontal(g497,g493)
    c: Horizontal(g477,g481)
    c: Equal(g464,g466)
    c: Equal(g463,g467)
    c: Horizontal(g465,g461)
    c: DistanceX(g465,g461) = 4
    c: PointOnObject(g512,g0)
    c: PointOnObject(g431,g0)
    c: PointOnObject(g415,g0)
    c: PointOnObject(g399,g0)
    c: PointOnObject(g383,g0)
    c: PointOnObject(g367,g0)
    c: PointOnObject(g351,g0)
    c: PointOnObject(g335,g0)
    c: PointOnObject(g319,g0)
    c: PointOnObject(g303,g0)
    c: PointOnObject(g287,g0)
    c: PointOnObject(g271,g0)
    c: Vertical(g255,g509)
FEATURE [PartDesign::Pocket] Pocket007
  BaseFeature = -> Pocket006
  Length = 1
  Length2 = 100
  Profile = -> Sketch009
  Reversed = true
  Type = 0
FEATURE [Part::Part2DObjectPython] ShapeString002  # Draft 2D object (typed FeaturePython)
  FontFile = <path> Squares/AdobeGothicStd-Bold.otf
  Placement = pos=(240,-12,-3) rot=(0,1,0;3.14159rad)
  Size = 4
  String = 4   23  22   21  20   19  18  17   16  15  14   13  12   11  10    9     8
  Support = -> [Pad]
  Tracking = 0
FEATURE [Sketcher::SketchObject] Sketch010  label="vt cm001"
  FullyConstrained = true
  MapMode = 5
  Placement = pos=(0,0,-3) rot=(0,0,1;0rad)
  Support = -> [DatumPlane]
  expr: Constraints[9] = Spreadsheet.reticleCmWidth
  expr: Constraints[7] = Spreadsheet.reticleCmHeight
  sketch-geometry (57):
    g0: LineSegment StartX=-25 StartY=-20 StartZ=0 EndX=275 EndY=-20 EndZ=0
    g1: LineSegment StartX=0 StartY=-20.1 StartZ=0 EndX=4 EndY=-20.1 EndZ=0
    g2: LineSegment StartX=4 StartY=-20.1 StartZ=0 EndX=4 EndY=-19.9 EndZ=0
    g3: LineSegment StartX=4 StartY=-19.9 StartZ=0 EndX=0 EndY=-19.9 EndZ=0
    g4: LineSegment StartX=0 StartY=-19.9 StartZ=0 EndX=0 EndY=-20.1 EndZ=0
    g5: LineSegment StartX=16 StartY=-20.1 StartZ=0 EndX=20 EndY=-20.1 EndZ=0
    g6: LineSegment StartX=20 StartY=-20.1 StartZ=0 EndX=20 EndY=-19.9 EndZ=0
    g7: LineSegment StartX=20 StartY=-19.9 StartZ=0 EndX=16 EndY=-19.9 EndZ=0
    g8: LineSegment StartX=16 StartY=-19.9 StartZ=0 EndX=16 EndY=-20.1 EndZ=0
    g9: LineSegment StartX=0 StartY=-30.3 StartZ=0 EndX=4 EndY=-30.3 EndZ=0
    g10: LineSegment StartX=4 StartY=-30.3 StartZ=0 EndX=4 EndY=-30.5 EndZ=0
    g11: LineSegment StartX=4 StartY=-30.5 StartZ=0 EndX=0 EndY=-30.5 EndZ=0
    g12: LineSegment StartX=0 StartY=-30.5 StartZ=0 EndX=0 EndY=-30.3 EndZ=0
    g13: LineSegment StartX=16 StartY=-30.3 StartZ=0 EndX=20 EndY=-30.3 EndZ=0
    g14: LineSegment StartX=20 StartY=-30.3 StartZ=0 EndX=20 EndY=-30.1 EndZ=0
    g15: LineSegment StartX=20 StartY=-30.1 StartZ=0 EndX=16 EndY=-30.1 EndZ=0
    g16: LineSegment StartX=16 StartY=-30.1 StartZ=0 EndX=16 EndY=-30.3 EndZ=0
    g17: LineSegment StartX=0 StartY=-40.1 StartZ=0 EndX=4 EndY=-40.1 EndZ=0
    g18: LineSegment StartX=4 StartY=-40.1 StartZ=0 EndX=4 EndY=-39.9 EndZ=0
    g19: LineSegment StartX=4 StartY=-39.9 StartZ=0 EndX=0 EndY=-39.9 EndZ=0
    g20: LineSegment StartX=0 StartY=-39.9 StartZ=0 EndX=0 EndY=-40.1 EndZ=0
    g21: LineSegment StartX=16 StartY=-40.1 StartZ=0 EndX=20 EndY=-40.1 EndZ=0
    g22: LineSegment StartX=20 StartY=-40.1 StartZ=0 EndX=20 EndY=-39.9 EndZ=0
    g23: LineSegment StartX=20 StartY=-39.9 StartZ=0 EndX=16 EndY=-39.9 EndZ=0
    g24: LineSegment StartX=16 StartY=-39.9 StartZ=0 EndX=16 EndY=-40.1 EndZ=0
    g25: LineSegment StartX=16 StartY=10.1 StartZ=0 EndX=20 EndY=10.1 EndZ=0
    g26: LineSegment StartX=20 StartY=10.1 StartZ=0 EndX=20 EndY=9.9 EndZ=0
    g27: LineSegment StartX=20 StartY=9.9 StartZ=0 EndX=16 EndY=9.9 EndZ=0
    g28: LineSegment StartX=16 StartY=9.9 StartZ=0 EndX=16 EndY=10.1 EndZ=0
    g29: LineSegment StartX=0 StartY=-0.1 StartZ=0 EndX=4 EndY=-0.1 EndZ=0
    g30: LineSegment StartX=4 StartY=-0.1 StartZ=0 EndX=4 EndY=0.1 EndZ=0
    g31: LineSegment StartX=4 StartY=0.1 StartZ=0 EndX=0 EndY=0.1 EndZ=0
    g32: LineSegment StartX=0 StartY=0.1 StartZ=0 EndX=0 EndY=-0.1 EndZ=0
    g33: LineSegment StartX=16 StartY=-0.1 StartZ=0 EndX=20 EndY=-0.1 EndZ=0
    g34: LineSegment StartX=20 StartY=-0.1 StartZ=0 EndX=20 EndY=0.1 EndZ=0
    g35: LineSegment StartX=20 StartY=0.1 StartZ=0 EndX=16 EndY=0.1 EndZ=0
    g36: LineSegment StartX=16 StartY=0.1 StartZ=0 EndX=16 EndY=-0.1 EndZ=0
    g37: LineSegment StartX=0 StartY=-9.9 StartZ=0 EndX=4 EndY=-9.9 EndZ=0
    g38: LineSegment StartX=4 StartY=-9.9 StartZ=0 EndX=4 EndY=-10.1 EndZ=0
    g39: LineSegment StartX=4 StartY=-10.1 StartZ=0 EndX=0 EndY=-10.1 EndZ=0
    g40: LineSegment StartX=0 StartY=-10.1 StartZ=0 EndX=0 EndY=-9.9 EndZ=0
    g41: LineSegment StartX=16 StartY=-9.9 StartZ=0 EndX=20 EndY=-9.9 EndZ=0
    g42: LineSegment StartX=20 StartY=-9.9 StartZ=0 EndX=20 EndY=-10.1 EndZ=0
    g43: LineSegment StartX=20 StartY=-10.1 StartZ=0 EndX=16 EndY=-10.1 EndZ=0
    g44: LineSegment StartX=16 StartY=-10.1 StartZ=0 EndX=16 EndY=-9.9 EndZ=0
    g45: LineSegment StartX=16 StartY=20.1 StartZ=0 EndX=20 EndY=20.1 EndZ=0
    g46: LineSegment StartX=20 StartY=20.1 StartZ=0 EndX=20 EndY=19.9 EndZ=0
    g47: LineSegment StartX=20 StartY=19.9 StartZ=0 EndX=16 EndY=19.9 EndZ=0
    g48: LineSegment StartX=16 StartY=19.9 StartZ=0 EndX=16 EndY=20.1 EndZ=0
    g49: LineSegment StartX=0 StartY=9.9 StartZ=0 EndX=4 EndY=9.9 EndZ=0
    g50: LineSegment StartX=4 StartY=9.9 StartZ=0 EndX=4 EndY=10.1 EndZ=0
    g51: LineSegment StartX=4 StartY=10.1 StartZ=0 EndX=0 EndY=10.1 EndZ=0
    g52: LineSegment StartX=0 StartY=10.1 StartZ=0 EndX=0 EndY=9.9 EndZ=0
    g53: LineSegment StartX=0 StartY=19.9 StartZ=0 EndX=4 EndY=19.9 EndZ=0
    g54: LineSegment StartX=4 StartY=19.9 StartZ=0 EndX=4 EndY=20.1 EndZ=0
    g55: LineSegment StartX=4 StartY=20.1 StartZ=0 EndX=0 EndY=20.1 EndZ=0
    g56: LineSegment StartX=0 StartY=20.1 StartZ=0 EndX=0 EndY=19.9 EndZ=0
  constraints (171):
    c: Horizontal(g0)
    c: DistanceY(g0,g-1) = 20
    c: Coincident(g1,g2)
    c: Coincident(g2,g3)
    c: Horizontal(g1)
    c: Horizontal(g3)
    c: PointOnObject(g1,g-2)
    c: DistanceX(g3,g3) = 4
    c: Symmetric(g2,g1,g0)
    c: DistanceY(g2,g2) = 0.2
    c: Vertical(g1,g3)
    c: Coincident(g4,g3)
    c: Coincident(g4,g1)
    c: DistanceX(g0,g-1) = 25
    c: DistanceX(g0,g0) = 300
    c: Coincident(g5,g6)
    c: Coincident(g6,g7)
    c: Horizontal(g5)
    c: Horizontal(g7)
    c: Equal(g3,g7) = 4
    c: Equal(g2,g6) = 0.2
    c: Vertical(g5,g7)
    c: Coincident(g8,g7)
    c: Coincident(g8,g5)
    c: DistanceX(g3,g6) = 20
    c: Horizontal(g1,g5)
    c: Vertical(g6)
    c: Coincident(g9,g10)
    c: Coincident(g10,g11)
    c: Horizontal(g9)
    c: Horizontal(g11)
    c: Equal(g3,g11) = 4
    c: Equal(g2,g10) = 0.2
    c: Vertical(g9,g11)
    c: Coincident(g12,g11)
    c: Coincident(g12,g9)
    c: Coincident(g13,g14)
    c: Coincident(g14,g15)
    c: Horizontal(g13)
    c: Horizontal(g15)
    c: Equal(g11,g15) = 4
    c: Equal(g10,g14) = 0.2
    c: Vertical(g13,g15)
    c: Coincident(g16,g15)
    c: Coincident(g16,g13)
    c: DistanceX(g11,g14) = 20
    c: Horizontal(g9,g13)
    c: Vertical(g14)
    c: Vertical(g9,g1)
    c: Vertical(g10)
    c: DistanceY(g15,g5) = 10
    c: Coincident(g17,g18)
    c: Coincident(g18,g19)
    c: Horizontal(g17)
    c: Horizontal(g19)
    c: Equal(g3,g19) = 4
    c: Equal(g2,g18) = 0.2
    c: Vertical(g17,g19)
    c: Coincident(g20,g19)
    c: Coincident(g20,g17)
    c: Coincident(g21,g22)
    c: Coincident(g22,g23)
    c: Horizontal(g21)
    c: Horizontal(g23)
    c: Equal(g19,g23) = 4
    c: Equal(g18,g22) = 0.2
    c: Vertical(g21,g23)
    c: Coincident(g24,g23)
    c: Coincident(g24,g21)
    c: DistanceX(g19,g22) = 20
    c: Horizontal(g17,g21)
    c: Vertical(g22)
    c: Vertical(g17,g11)
    c: DistanceY(g21,g15) = 10
    c: Vertical(g18)
    c: Coincident(g25,g26)
    c: Coincident(g26,g27)
    c: Horizontal(g25)
    c: Horizontal(g27)
    c: Vertical(g25,g27)
    c: Coincident(g28,g27)
    c: Coincident(g28,g25)
    c: Vertical(g26)
    c: Coincident(g29,g30)
    c: Coincident(g30,g31)
    c: Horizontal(g29)
    c: Horizontal(g31)
    c: Vertical(g29,g31)
    c: Coincident(g32,g31)
    c: Coincident(g32,g29)
    c: Coincident(g33,g34)
    c: Coincident(g34,g35)
    c: Horizontal(g33)
    c: Horizontal(g35)
    c: Equal(g31,g35) = 4
    c: Equal(g30,g34) = 0.2
    c: Vertical(g33,g35)
    c: Coincident(g36,g35)
    c: Coincident(g36,g33)
    c: DistanceX(g31,g34) = 20
    c: Horizontal(g29,g33)
    c: Vertical(g34)
    c: Coincident(g37,g38)
    c: Coincident(g38,g39)
    c: Horizontal(g37)
    c: Horizontal(g39)
    c: Equal(g31,g39) = 4
    c: Equal(g30,g38) = 0.2
    c: Vertical(g37,g39)
    c: Coincident(g40,g39)
    c: Coincident(g40,g37)
    c: Coincident(g41,g42)
    c: Coincident(g42,g43)
    c: Horizontal(g41)
    c: Horizontal(g43)
    c: Equal(g39,g43) = 4
    c: Equal(g38,g42) = 0.2
    c: Vertical(g41,g43)
    c: Coincident(g44,g43)
    c: Coincident(g44,g41)
    c: DistanceX(g39,g42) = 20
    c: Horizontal(g37,g41)
    c: Vertical(g42)
    c: Vertical(g37,g29)
    c: Vertical(g38)
    c: DistanceY(g43,g33) = 10
    c: DistanceY(g33,g27) = 10
    c: Vertical(g30)
    c: Vertical(g3,g39)
    c: Equal(g7,g43)
    c: Equal(g8,g44)
    c: DistanceY(g5,g43) = 10
    c: Coincident(g45,g46)
    c: Coincident(g46,g47)
    c: Horizontal(g45)
    c: Horizontal(g47)
    c: Vertical(g45,g47)
    c: Coincident(g48,g47)
    c: Coincident(g48,g45)
    c: Vertical(g46)
    c: DistanceY(g27,g47) = 10
    c: Coincident(g49,g50)
    c: Coincident(g50,g51)
    c: Horizontal(g49)
    c: Horizontal(g51)
    c: Vertical(g49,g51)
    c: Coincident(g52,g51)
    c: Coincident(g52,g49)
    c: Vertical(g50)
    c: PointOnObject(g52,g-2)
    c: Horizontal(g49,g27)
    c: Equal(g30,g50)
    c: Equal(g36,g28)
    c: Vertical(g34,g26)
    c: Vertical(g46,g25)
    c: Equal(g28,g48)
    c: Vertical(g47,g25)
    c: Vertical(g30,g49)
    c: Vertical(g35,g27)
    c: Coincident(g53,g54)
    c: Coincident(g54,g55)
    c: Horizontal(g53)
    c: Horizontal(g55)
    c: Vertical(g53,g55)
    c: Coincident(g56,g55)
    c: Coincident(g56,g53)
    c: Vertical(g54)
    c: PointOnObject(g56,g-2)
    c: Equal(g50,g54)
    c: Vertical(g50,g53)
    c: Horizontal(g45,g54)
FEATURE [Sketcher::SketchObject] Sketch011  label="vt mm001"
  FullyConstrained = true
  MapMode = 5
  Placement = pos=(0,0,-3) rot=(0,0,1;0rad)
  Support = -> [DatumPlane]
  expr: Constraints[9] = Spreadsheet.reticleCmHeight / 2
  expr: Constraints[8] = Spreadsheet.reticleCmWidth
  sketch-geometry (192):
    g0: LineSegment StartX=0 StartY=1.95 StartZ=0 EndX=2 EndY=1.95 EndZ=0
    g1: LineSegment StartX=2 StartY=1.95 StartZ=0 EndX=2 EndY=2.15 EndZ=0
    g2: LineSegment StartX=2 StartY=2.15 StartZ=0 EndX=0 EndY=2.15 EndZ=0
    g3: LineSegment StartX=0 StartY=2.15 StartZ=0 EndX=0 EndY=1.95 EndZ=0
    g4: LineSegment StartX=0 StartY=3.95 StartZ=0 EndX=2 EndY=3.95 EndZ=0
    g5: LineSegment StartX=2 StartY=3.95 StartZ=0 EndX=2 EndY=4.15 EndZ=0
    g6: LineSegment StartX=2 StartY=4.15 StartZ=0 EndX=0 EndY=4.15 EndZ=0
    g7: LineSegment StartX=0 StartY=4.15 StartZ=0 EndX=0 EndY=3.95 EndZ=0
    g8: LineSegment StartX=0 StartY=6.15 StartZ=0 EndX=2 EndY=6.15 EndZ=0
    g9: LineSegment StartX=2 StartY=6.15 StartZ=0 EndX=2 EndY=5.95 EndZ=0
    g10: LineSegment StartX=2 StartY=5.95 StartZ=0 EndX=0 EndY=5.95 EndZ=0
    g11: LineSegment StartX=0 StartY=5.95 StartZ=0 EndX=0 EndY=6.15 EndZ=0
    g12: LineSegment StartX=0 StartY=7.95 StartZ=0 EndX=2 EndY=7.95 EndZ=0
    g13: LineSegment StartX=2 StartY=7.95 StartZ=0 EndX=2 EndY=8.15 EndZ=0
    g14: LineSegment StartX=2 StartY=8.15 StartZ=0 EndX=0 EndY=8.15 EndZ=0
    g15: LineSegment StartX=0 StartY=8.15 StartZ=0 EndX=0 EndY=7.95 EndZ=0
    g16: LineSegment StartX=18 StartY=1.95 StartZ=0 EndX=20 EndY=1.95 EndZ=0
    g17: LineSegment StartX=20 StartY=1.95 StartZ=0 EndX=20 EndY=2.15 EndZ=0
    g18: LineSegment StartX=20 StartY=2.15 StartZ=0 EndX=18 EndY=2.15 EndZ=0
    g19: LineSegment StartX=18 StartY=2.15 StartZ=0 EndX=18 EndY=1.95 EndZ=0
    g20: LineSegment StartX=18 StartY=3.95 StartZ=0 EndX=20 EndY=3.95 EndZ=0
    g21: LineSegment StartX=20 StartY=3.95 StartZ=0 EndX=20 EndY=4.15 EndZ=0
    g22: LineSegment StartX=20 StartY=4.15 StartZ=0 EndX=18 EndY=4.15 EndZ=0
    g23: LineSegment StartX=18 StartY=4.15 StartZ=0 EndX=18 EndY=3.95 EndZ=0
    g24: LineSegment StartX=18 StartY=6.15 StartZ=0 EndX=20 EndY=6.15 EndZ=0
    g25: LineSegment StartX=20 StartY=6.15 StartZ=0 EndX=20 EndY=5.95 EndZ=0
    g26: LineSegment StartX=20 StartY=5.95 StartZ=0 EndX=18 EndY=5.95 EndZ=0
    g27: LineSegment StartX=18 StartY=5.95 StartZ=0 EndX=18 EndY=6.15 EndZ=0
    g28: LineSegment StartX=18 StartY=7.95 StartZ=0 EndX=20 EndY=7.95 EndZ=0
    g29: LineSegment StartX=20 StartY=7.95 StartZ=0 EndX=20 EndY=8.15 EndZ=0
    g30: LineSegment StartX=20 StartY=8.15 StartZ=0 EndX=18 EndY=8.15 EndZ=0
    g31: LineSegment StartX=18 StartY=8.15 StartZ=0 EndX=18 EndY=7.95 EndZ=0
    g32: LineSegment StartX=0 StartY=-8.05 StartZ=0 EndX=2 EndY=-8.05 EndZ=0
    g33: LineSegment StartX=2 StartY=-8.05 StartZ=0 EndX=2 EndY=-7.85 EndZ=0
    g34: LineSegment StartX=2 StartY=-7.85 StartZ=0 EndX=0 EndY=-7.85 EndZ=0
    g35: LineSegment StartX=0 StartY=-7.85 StartZ=0 EndX=0 EndY=-8.05 EndZ=0
    g36: LineSegment StartX=0 StartY=-6.05 StartZ=0 EndX=2 EndY=-6.05 EndZ=0
    g37: LineSegment StartX=2 StartY=-6.05 StartZ=0 EndX=2 EndY=-5.85 EndZ=0
    g38: LineSegment StartX=2 StartY=-5.85 StartZ=0 EndX=0 EndY=-5.85 EndZ=0
    g39: LineSegment StartX=0 StartY=-5.85 StartZ=0 EndX=0 EndY=-6.05 EndZ=0
    g40: LineSegment StartX=0 StartY=-3.85 StartZ=0 EndX=2 EndY=-3.85 EndZ=0
    g41: LineSegment StartX=2 StartY=-3.85 StartZ=0 EndX=2 EndY=-4.05 EndZ=0
    g42: LineSegment StartX=2 StartY=-4.05 StartZ=0 EndX=0 EndY=-4.05 EndZ=0
    g43: LineSegment StartX=0 StartY=-4.05 StartZ=0 EndX=0 EndY=-3.85 EndZ=0
    g44: LineSegment StartX=0 StartY=-2.05 StartZ=0 EndX=2 EndY=-2.05 EndZ=0
    g45: LineSegment StartX=2 StartY=-2.05 StartZ=0 EndX=2 EndY=-1.85 EndZ=0
    g46: LineSegment StartX=2 StartY=-1.85 StartZ=0 EndX=0 EndY=-1.85 EndZ=0
    g47: LineSegment StartX=0 StartY=-1.85 StartZ=0 EndX=0 EndY=-2.05 EndZ=0
    g48: LineSegment StartX=18 StartY=-8.05 StartZ=0 EndX=20 EndY=-8.05 EndZ=0
    g49: LineSegment StartX=20 StartY=-8.05 StartZ=0 EndX=20 EndY=-7.85 EndZ=0
    g50: LineSegment StartX=20 StartY=-7.85 StartZ=0 EndX=18 EndY=-7.85 EndZ=0
    g51: LineSegment StartX=18 StartY=-7.85 StartZ=0 EndX=18 EndY=-8.05 EndZ=0
    g52: LineSegment StartX=18 StartY=-6.05 StartZ=0 EndX=20 EndY=-6.05 EndZ=0
    g53: LineSegment StartX=20 StartY=-6.05 StartZ=0 EndX=20 EndY=-5.85 EndZ=0
    g54: LineSegment StartX=20 StartY=-5.85 StartZ=0 EndX=18 EndY=-5.85 EndZ=0
    g55: LineSegment StartX=18 StartY=-5.85 StartZ=0 EndX=18 EndY=-6.05 EndZ=0
    g56: LineSegment StartX=18 StartY=-3.85 StartZ=0 EndX=20 EndY=-3.85 EndZ=0
    g57: LineSegment StartX=20 StartY=-3.85 StartZ=0 EndX=20 EndY=-4.05 EndZ=0
    g58: LineSegment StartX=20 StartY=-4.05 StartZ=0 EndX=18 EndY=-4.05 EndZ=0
    g59: LineSegment StartX=18 StartY=-4.05 StartZ=0 EndX=18 EndY=-3.85 EndZ=0
    g60: LineSegment StartX=18 StartY=-2.05 StartZ=0 EndX=20 EndY=-2.05 EndZ=0
    g61: LineSegment StartX=20 StartY=-2.05 StartZ=0 EndX=20 EndY=-1.85 EndZ=0
    g62: LineSegment StartX=20 StartY=-1.85 StartZ=0 EndX=18 EndY=-1.85 EndZ=0
    g63: LineSegment StartX=18 StartY=-1.85 StartZ=0 EndX=18 EndY=-2.05 EndZ=0
    g64: LineSegment StartX=0 StartY=-18.05 StartZ=0 EndX=2 EndY=-18.05 EndZ=0
    g65: LineSegment StartX=2 StartY=-18.05 StartZ=0 EndX=2 EndY=-17.85 EndZ=0
    g66: LineSegment StartX=2 StartY=-17.85 StartZ=0 EndX=0 EndY=-17.85 EndZ=0
    g67: LineSegment StartX=0 StartY=-17.85 StartZ=0 EndX=0 EndY=-18.05 EndZ=0
    g68: LineSegment StartX=0 StartY=-16.05 StartZ=0 EndX=2 EndY=-16.05 EndZ=0
    g69: LineSegment StartX=2 StartY=-16.05 StartZ=0 EndX=2 EndY=-15.85 EndZ=0
    g70: LineSegment StartX=2 StartY=-15.85 StartZ=0 EndX=0 EndY=-15.85 EndZ=0
    g71: LineSegment StartX=0 StartY=-15.85 StartZ=0 EndX=0 EndY=-16.05 EndZ=0
    g72: LineSegment StartX=0 StartY=-13.85 StartZ=0 EndX=2 EndY=-13.85 EndZ=0
    g73: LineSegment StartX=2 StartY=-13.85 StartZ=0 EndX=2 EndY=-14.05 EndZ=0
    g74: LineSegment StartX=2 StartY=-14.05 StartZ=0 EndX=0 EndY=-14.05 EndZ=0
    g75: LineSegment StartX=0 StartY=-14.05 StartZ=0 EndX=0 EndY=-13.85 EndZ=0
    g76: LineSegment StartX=0 StartY=-12.05 StartZ=0 EndX=2 EndY=-12.05 EndZ=0
    g77: LineSegment StartX=2 StartY=-12.05 StartZ=0 EndX=2 EndY=-11.85 EndZ=0
    g78: LineSegment StartX=2 StartY=-11.85 StartZ=0 EndX=0 EndY=-11.85 EndZ=0
    g79: LineSegment StartX=0 StartY=-11.85 StartZ=0 EndX=0 EndY=-12.05 EndZ=0
    g80: LineSegment StartX=18 StartY=-18.05 StartZ=0 EndX=20 EndY=-18.05 EndZ=0
    g81: LineSegment StartX=20 StartY=-18.05 StartZ=0 EndX=20 EndY=-17.85 EndZ=0
    g82: LineSegment StartX=20 StartY=-17.85 StartZ=0 EndX=18 EndY=-17.85 EndZ=0
    g83: LineSegment StartX=18 StartY=-17.85 StartZ=0 EndX=18 EndY=-18.05 EndZ=0
    g84: LineSegment StartX=18 StartY=-16.05 StartZ=0 EndX=20 EndY=-16.05 EndZ=0
    g85: LineSegment StartX=20 StartY=-16.05 StartZ=0 EndX=20 EndY=-15.85 EndZ=0
    g86: LineSegment StartX=20 StartY=-15.85 StartZ=0 EndX=18 EndY=-15.85 EndZ=0
    g87: LineSegment StartX=18 StartY=-15.85 StartZ=0 EndX=18 EndY=-16.05 EndZ=0
    g88: LineSegment StartX=18 StartY=-13.85 StartZ=0 EndX=20 EndY=-13.85 EndZ=0
    g89: LineSegment StartX=20 StartY=-13.85 StartZ=0 EndX=20 EndY=-14.05 EndZ=0
    g90: LineSegment StartX=20 StartY=-14.05 StartZ=0 EndX=18 EndY=-14.05 EndZ=0
    g91: LineSegment StartX=18 StartY=-14.05 StartZ=0 EndX=18 EndY=-13.85 EndZ=0
    g92: LineSegment StartX=18 StartY=-12.05 StartZ=0 EndX=20 EndY=-12.05 EndZ=0
    g93: LineSegment StartX=20 StartY=-12.05 StartZ=0 EndX=20 EndY=-11.85 EndZ=0
    g94: LineSegment StartX=20 StartY=-11.85 StartZ=0 EndX=18 EndY=-11.85 EndZ=0
    g95: LineSegment StartX=18 StartY=-11.85 StartZ=0 EndX=18 EndY=-12.05 EndZ=0
    g96: LineSegment StartX=0 StartY=-28.05 StartZ=0 EndX=2 EndY=-28.05 EndZ=0
    g97: LineSegment StartX=2 StartY=-28.05 StartZ=0 EndX=2 EndY=-27.85 EndZ=0
    g98: LineSegment StartX=2 StartY=-27.85 StartZ=0 EndX=0 EndY=-27.85 EndZ=0
    g99: LineSegment StartX=0 StartY=-27.85 StartZ=0 EndX=0 EndY=-28.05 EndZ=0
    g100: LineSegment StartX=0 StartY=-26.05 StartZ=0 EndX=2 EndY=-26.05 EndZ=0
    g101: LineSegment StartX=2 StartY=-26.05 StartZ=0 EndX=2 EndY=-25.85 EndZ=0
    g102: LineSegment StartX=2 StartY=-25.85 StartZ=0 EndX=0 EndY=-25.85 EndZ=0
    g103: LineSegment StartX=0 StartY=-25.85 StartZ=0 EndX=0 EndY=-26.05 EndZ=0
    g104: LineSegment StartX=0 StartY=-23.85 StartZ=0 EndX=2 EndY=-23.85 EndZ=0
    g105: LineSegment StartX=2 StartY=-23.85 StartZ=0 EndX=2 EndY=-24.05 EndZ=0
    g106: LineSegment StartX=2 StartY=-24.05 StartZ=0 EndX=0 EndY=-24.05 EndZ=0
    g107: LineSegment StartX=0 StartY=-24.05 StartZ=0 EndX=0 EndY=-23.85 EndZ=0
    g108: LineSegment StartX=0 StartY=-22.05 StartZ=0 EndX=2 EndY=-22.05 EndZ=0
    g109: LineSegment StartX=2 StartY=-22.05 StartZ=0 EndX=2 EndY=-21.85 EndZ=0
    g110: LineSegment StartX=2 StartY=-21.85 StartZ=0 EndX=0 EndY=-21.85 EndZ=0
    g111: LineSegment StartX=0 StartY=-21.85 StartZ=0 EndX=0 EndY=-22.05 EndZ=0
    g112: LineSegment StartX=18 StartY=-28.05 StartZ=0 EndX=20 EndY=-28.05 EndZ=0
    g113: LineSegment StartX=20 StartY=-28.05 StartZ=0 EndX=20 EndY=-27.85 EndZ=0
    g114: LineSegment StartX=20 StartY=-27.85 StartZ=0 EndX=18 EndY=-27.85 EndZ=0
    g115: LineSegment StartX=18 StartY=-27.85 StartZ=0 EndX=18 EndY=-28.05 EndZ=0
    g116: LineSegment StartX=18 StartY=-26.05 StartZ=0 EndX=20 EndY=-26.05 EndZ=0
    g117: LineSegment StartX=20 StartY=-26.05 StartZ=0 EndX=20 EndY=-25.85 EndZ=0
    g118: LineSegment StartX=20 StartY=-25.85 StartZ=0 EndX=18 EndY=-25.85 EndZ=0
    g119: LineSegment StartX=18 StartY=-25.85 StartZ=0 EndX=18 EndY=-26.05 EndZ=0
    g120: LineSegment StartX=18 StartY=-23.85 StartZ=0 EndX=20 EndY=-23.85 EndZ=0
    g121: LineSegment StartX=20 StartY=-23.85 StartZ=0 EndX=20 EndY=-24.05 EndZ=0
    g122: LineSegment StartX=20 StartY=-24.05 StartZ=0 EndX=18 EndY=-24.05 EndZ=0
    g123: LineSegment StartX=18 StartY=-24.05 StartZ=0 EndX=18 EndY=-23.85 EndZ=0
    g124: LineSegment StartX=18 StartY=-22.05 StartZ=0 EndX=20 EndY=-22.05 EndZ=0
    g125: LineSegment StartX=20 StartY=-22.05 StartZ=0 EndX=20 EndY=-21.85 EndZ=0
    g126: LineSegment StartX=20 StartY=-21.85 StartZ=0 EndX=18 EndY=-21.85 EndZ=0
    g127: LineSegment StartX=18 StartY=-21.85 StartZ=0 EndX=18 EndY=-22.05 EndZ=0
    g128: LineSegment StartX=0 StartY=-38.05 StartZ=0 EndX=2 EndY=-38.05 EndZ=0
    g129: LineSegment StartX=2 StartY=-38.05 StartZ=0 EndX=2 EndY=-38.25 EndZ=0
    g130: LineSegment StartX=2 StartY=-38.25 StartZ=0 EndX=0 EndY=-38.25 EndZ=0
    g131: LineSegment StartX=0 StartY=-38.25 StartZ=0 EndX=0 EndY=-38.05 EndZ=0
    g132: LineSegment StartX=0 StartY=-36.05 StartZ=0 EndX=2 EndY=-36.05 EndZ=0
    g133: LineSegment StartX=2 StartY=-36.05 StartZ=0 EndX=2 EndY=-36.25 EndZ=0
    g134: LineSegment StartX=2 StartY=-36.25 StartZ=0 EndX=0 EndY=-36.25 EndZ=0
    g135: LineSegment StartX=0 StartY=-36.25 StartZ=0 EndX=0 EndY=-36.05 EndZ=0
    g136: LineSegment StartX=0 StartY=-34.25 StartZ=0 EndX=2 EndY=-34.25 EndZ=0
    g137: LineSegment StartX=2 StartY=-34.25 StartZ=0 EndX=2 EndY=-34.05 EndZ=0
    g138: LineSegment StartX=2 StartY=-34.05 StartZ=0 EndX=0 EndY=-34.05 EndZ=0
    g139: LineSegment StartX=0 StartY=-34.05 StartZ=0 EndX=0 EndY=-34.25 EndZ=0
    g140: LineSegment StartX=0 StartY=-32.05 StartZ=0 EndX=2 EndY=-32.05 EndZ=0
    g141: LineSegment StartX=2 StartY=-32.05 StartZ=0 EndX=2 EndY=-31.85 EndZ=0
    g142: LineSegment StartX=2 StartY=-31.85 StartZ=0 EndX=0 EndY=-31.85 EndZ=0
    g143: LineSegment StartX=0 StartY=-31.85 StartZ=0 EndX=0 EndY=-32.05 EndZ=0
    g144: LineSegment StartX=18 StartY=-38.05 StartZ=0 EndX=20 EndY=-38.05 EndZ=0
    g145: LineSegment StartX=20 StartY=-38.05 StartZ=0 EndX=20 EndY=-38.25 EndZ=0
    g146: LineSegment StartX=20 StartY=-38.25 StartZ=0 EndX=18 EndY=-38.25 EndZ=0
    g147: LineSegment StartX=18 StartY=-38.25 StartZ=0 EndX=18 EndY=-38.05 EndZ=0
    g148: LineSegment StartX=18 StartY=-36.05 StartZ=0 EndX=20 EndY=-36.05 EndZ=0
    g149: LineSegment StartX=20 StartY=-36.05 StartZ=0 EndX=20 EndY=-36.25 EndZ=0
    g150: LineSegment StartX=20 StartY=-36.25 StartZ=0 EndX=18 EndY=-36.25 EndZ=0
    g151: LineSegment StartX=18 StartY=-36.25 StartZ=0 EndX=18 EndY=-36.05 EndZ=0
    g152: LineSegment StartX=18 StartY=-34.25 StartZ=0 EndX=20 EndY=-34.25 EndZ=0
    g153: LineSegment StartX=20 StartY=-34.25 StartZ=0 EndX=20 EndY=-34.05 EndZ=0
    g154: LineSegment StartX=20 StartY=-34.05 StartZ=0 EndX=18 EndY=-34.05 EndZ=0
    g155: LineSegment StartX=18 StartY=-34.05 StartZ=0 EndX=18 EndY=-34.25 EndZ=0
    g156: LineSegment StartX=18 StartY=-32.05 StartZ=0 EndX=20 EndY=-32.05 EndZ=0
    g157: LineSegment StartX=20 StartY=-32.05 StartZ=0 EndX=20 EndY=-31.85 EndZ=0
    g158: LineSegment StartX=20 StartY=-31.85 StartZ=0 EndX=18 EndY=-31.85 EndZ=0
    g159: LineSegment StartX=18 StartY=-31.85 StartZ=0 EndX=18 EndY=-32.05 EndZ=0
    g160: LineSegment StartX=0 StartY=11.95 StartZ=0 EndX=2 EndY=11.95 EndZ=0
    g161: LineSegment StartX=2 StartY=11.95 StartZ=0 EndX=2 EndY=12.15 EndZ=0
    g162: LineSegment StartX=2 StartY=12.15 StartZ=0 EndX=0 EndY=12.15 EndZ=0
    g163: LineSegment StartX=0 StartY=12.15 StartZ=0 EndX=0 EndY=11.95 EndZ=0
    g164: LineSegment StartX=0 StartY=13.95 StartZ=0 EndX=2 EndY=13.95 EndZ=0
    g165: LineSegment StartX=2 StartY=13.95 StartZ=0 EndX=2 EndY=14.15 EndZ=0
    g166: LineSegment StartX=2 StartY=14.15 StartZ=0 EndX=0 EndY=14.15 EndZ=0
    g167: LineSegment StartX=0 StartY=14.15 StartZ=0 EndX=0 EndY=13.95 EndZ=0
    g168: LineSegment StartX=0 StartY=16.15 StartZ=0 EndX=2 EndY=16.15 EndZ=0
    g169: LineSegment StartX=2 StartY=16.15 StartZ=0 EndX=2 EndY=15.95 EndZ=0
    g170: LineSegment StartX=2 StartY=15.95 StartZ=0 EndX=0 EndY=15.95 EndZ=0
    g171: LineSegment StartX=0 StartY=15.95 StartZ=0 EndX=0 EndY=16.15 EndZ=0
    g172: LineSegment StartX=0 StartY=17.95 StartZ=0 EndX=2 EndY=17.95 EndZ=0
    g173: LineSegment StartX=2 StartY=17.95 StartZ=0 EndX=2 EndY=18.15 EndZ=0
    g174: LineSegment StartX=2 StartY=18.15 StartZ=0 EndX=0 EndY=18.15 EndZ=0
    g175: LineSegment StartX=0 StartY=18.15 StartZ=0 EndX=0 EndY=17.95 EndZ=0
    g176: LineSegment StartX=18 StartY=11.95 StartZ=0 EndX=20 EndY=11.95 EndZ=0
    g177: LineSegment StartX=20 StartY=11.95 StartZ=0 EndX=20 EndY=12.15 EndZ=0
    g178: LineSegment StartX=20 StartY=12.15 StartZ=0 EndX=18 EndY=12.15 EndZ=0
    g179: LineSegment StartX=18 StartY=12.15 StartZ=0 EndX=18 EndY=11.95 EndZ=0
    g180: LineSegment StartX=18 StartY=13.95 StartZ=0 EndX=20 EndY=13.95 EndZ=0
    g181: LineSegment StartX=20 StartY=13.95 StartZ=0 EndX=20 EndY=14.15 EndZ=0
    g182: LineSegment StartX=20 StartY=14.15 StartZ=0 EndX=18 EndY=14.15 EndZ=0
    g183: LineSegment StartX=18 StartY=14.15 StartZ=0 EndX=18 EndY=13.95 EndZ=0
    g184: LineSegment StartX=18 StartY=16.15 StartZ=0 EndX=20 EndY=16.15 EndZ=0
    g185: LineSegment StartX=20 StartY=16.15 StartZ=0 EndX=20 EndY=15.95 EndZ=0
    g186: LineSegment StartX=20 StartY=15.95 StartZ=0 EndX=18 EndY=15.95 EndZ=0
    g187: LineSegment StartX=18 StartY=15.95 StartZ=0 EndX=18 EndY=16.15 EndZ=0
    g188: LineSegment StartX=18 StartY=17.95 StartZ=0 EndX=20 EndY=17.95 EndZ=0
    g189: LineSegment StartX=20 StartY=17.95 StartZ=0 EndX=20 EndY=18.15 EndZ=0
    g190: LineSegment StartX=20 StartY=18.15 StartZ=0 EndX=18 EndY=18.15 EndZ=0
    g191: LineSegment StartX=18 StartY=18.15 StartZ=0 EndX=18 EndY=17.95 EndZ=0
  constraints (576):
    c: Coincident(g1,g2)
    c: Coincident(g2,g3)
    c: Coincident(g3,g0)
    c: Horizontal(g0)
    c: Horizontal(g2)
    c: Vertical(g1)
    c: Vertical(g3)
    c: PointOnObject(g0,g-2)
    c: DistanceY(g1,g1) = 0.2
    c: DistanceX(g0,g0) = 2
    c: Coincident(g4,g5)
    c: Coincident(g5,g6)
    c: Coincident(g6,g7)
    c: Coincident(g7,g4)
    c: Horizontal(g4)
    c: Horizontal(g6)
    c: Vertical(g5)
    c: Vertical(g7)
    c: PointOnObject(g4,g-2)
    c: Coincident(g8,g9)
    c: Coincident(g9,g10)
    c: Coincident(g10,g11)
    c: Coincident(g11,g8)
    c: Horizontal(g8)
    c: Horizontal(g10)
    c: Vertical(g9)
    c: Vertical(g11)
    c: PointOnObject(g8,g-2)
    c: Coincident(g12,g13)
    c: Coincident(g13,g14)
    c: Coincident(g14,g15)
    c: Coincident(g15,g12)
    c: Horizontal(g12)
    c: Horizontal(g14)
    c: Vertical(g13)
    c: Vertical(g15)
    c: PointOnObject(g12,g-2)
    c: Equal(g14,g10)
    c: Equal(g10,g4)
    c: Equal(g4,g0)
    c: Equal(g1,g5)
    c: Equal(g5,g9)
    c: Equal(g9,g13)
    c: DistanceY(g4,g9) = 2
    c: Coincident(g16,g17)
    c: Coincident(g17,g18)
    c: Coincident(g18,g19)
    c: Coincident(g19,g16)
    c: Horizontal(g16)
    c: Horizontal(g18)
    c: Vertical(g17)
    c: Vertical(g19)
    c: Equal(g1,g17) = 0.2
    c: Equal(g0,g16) = 2
    c: Coincident(g20,g21)
    c: Coincident(g21,g22)
    c: Coincident(g22,g23)
    c: Coincident(g23,g20)
    c: Horizontal(g20)
    c: Horizontal(g22)
    c: Vertical(g21)
    c: Vertical(g23)
    c: Coincident(g24,g25)
    c: Coincident(g25,g26)
    c: Coincident(g26,g27)
    c: Coincident(g27,g24)
    c: Horizontal(g24)
    c: Horizontal(g26)
    c: Vertical(g25)
    c: Vertical(g27)
    c: Coincident(g28,g29)
    c: Coincident(g29,g30)
    c: Coincident(g30,g31)
    c: Coincident(g31,g28)
    c: Horizontal(g28)
    c: Horizontal(g30)
    c: Vertical(g29)
    c: Vertical(g31)
    c: Equal(g30,g26)
    c: Equal(g26,g20)
    c: Equal(g20,g16)
    c: Equal(g17,g21)
    c: Equal(g21,g25)
    c: Equal(g25,g29)
    c: DistanceY(g16,g20) = 2
    c: DistanceY(g20,g25) = 2
    c: DistanceX(g14,g29) = 20
    c: Vertical(g28,g24)
    c: Vertical(g25,g21)
    c: Vertical(g20,g17)
    c: Horizontal(g12,g28)
    c: Coincident(g32,g33)
    c: Coincident(g33,g34)
    c: Coincident(g34,g35)
    c: Coincident(g35,g32)
    c: Horizontal(g32)
    c: Horizontal(g34)
    c: Vertical(g33)
    c: Vertical(g35)
    c: Equal(g1,g33) = 0.2
    c: Equal(g0,g32) = 2
    c: Coincident(g36,g37)
    c: Coincident(g37,g38)
    c: Coincident(g38,g39)
    c: Coincident(g39,g36)
    c: Horizontal(g36)
    c: Horizontal(g38)
    c: Vertical(g37)
    c: Vertical(g39)
    c: Coincident(g40,g41)
    c: Coincident(g41,g42)
    c: Coincident(g42,g43)
    c: Coincident(g43,g40)
    c: Horizontal(g40)
    c: Horizontal(g42)
    c: Vertical(g41)
    c: Vertical(g43)
    c: Coincident(g44,g45)
    c: Coincident(g45,g46)
    c: Coincident(g46,g47)
    c: Coincident(g47,g44)
    c: Horizontal(g44)
    c: Horizontal(g46)
    c: Vertical(g45)
    c: Vertical(g47)
    c: Equal(g46,g42)
    c: Equal(g42,g36)
    c: Equal(g36,g32)
    c: Equal(g33,g37)
    c: Equal(g37,g41)
    c: Equal(g41,g45)
    c: DistanceY(g32,g36) = 2
    c: DistanceY(g36,g41) = 2
    c: Coincident(g48,g49)
    c: Coincident(g49,g50)
    c: Coincident(g50,g51)
    c: Coincident(g51,g48)
    c: Horizontal(g48)
    c: Horizontal(g50)
    c: Vertical(g49)
    c: Vertical(g51)
    c: Equal(g33,g49) = 0.2
    c: Equal(g32,g48) = 2
    c: Coincident(g52,g53)
    c: Coincident(g53,g54)
    c: Coincident(g54,g55)
    c: Coincident(g55,g52)
    c: Horizontal(g52)
    c: Horizontal(g54)
    c: Vertical(g53)
    c: Vertical(g55)
    c: Coincident(g56,g57)
    c: Coincident(g57,g58)
    c: Coincident(g58,g59)
    c: Coincident(g59,g56)
    c: Horizontal(g56)
    c: Horizontal(g58)
    c: Vertical(g57)
    c: Vertical(g59)
    c: Coincident(g60,g61)
    c: Coincident(g61,g62)
    c: Coincident(g62,g63)
    c: Coincident(g63,g60)
    c: Horizontal(g60)
    c: Horizontal(g62)
    c: Vertical(g61)
    c: Vertical(g63)
    c: Equal(g62,g58)
    c: Equal(g58,g52)
    c: Equal(g52,g48)
    c: Equal(g49,g53)
    c: Equal(g53,g57)
    c: Equal(g57,g61)
    c: DistanceY(g48,g52) = 2
    c: DistanceY(g52,g57) = 2
    c: DistanceX(g46,g61) = 20
    c: Vertical(g60,g56)
    c: Vertical(g57,g53)
    c: Vertical(g52,g49)
    c: Horizontal(g44,g60)
    c: DistanceY(g0,g4) = 2
    c: DistanceY(g44,g0) = 4
    c: DistanceY(g41,g44) = 2
    c: Coincident(g1,g0)
    c: DistanceY(g58,g60) = 2
    c: DistanceY(g26,g28) = 2
    c: DistanceY(g9,g12) = 2
    c: Vertical(g0,g46)
    c: Vertical(g40,g44)
    c: Vertical(g38,g42)
    c: Vertical(g34,g36)
    c: Coincident(g65,g66)
    c: Coincident(g66,g67)
    c: Coincident(g67,g64)
    c: Horizontal(g64)
    c: Horizontal(g66)
    c: Vertical(g65)
    c: Vertical(g67)
    c: Equal(g1,g65) = 0.2
    c: Equal(g0,g64) = 2
    c: Coincident(g68,g69)
    c: Coincident(g69,g70)
    c: Coincident(g70,g71)
    c: Coincident(g71,g68)
    c: Horizontal(g68)
    c: Horizontal(g70)
    c: Vertical(g69)
    c: Vertical(g71)
    c: Coincident(g72,g73)
    c: Coincident(g73,g74)
    c: Coincident(g74,g75)
    c: Coincident(g75,g72)
    c: Horizontal(g72)
    c: Horizontal(g74)
    c: Vertical(g73)
    c: Vertical(g75)
    c: Coincident(g76,g77)
    c: Coincident(g77,g78)
    c: Coincident(g78,g79)
    c: Coincident(g79,g76)
    c: Horizontal(g76)
    c: Horizontal(g78)
    c: Vertical(g77)
    c: Vertical(g79)
    c: Equal(g78,g74)
    c: Equal(g74,g68)
    c: Equal(g68,g64)
    c: Equal(g65,g69)
    c: Equal(g69,g73)
    c: Equal(g73,g77)
    c: DistanceY(g68,g73) = 2
    c: Coincident(g80,g81)
    c: Coincident(g81,g82)
    c: Coincident(g82,g83)
    c: Coincident(g83,g80)
    c: Horizontal(g80)
    c: Horizontal(g82)
    c: Vertical(g81)
    c: Vertical(g83)
    c: Equal(g65,g81) = 0.2
    c: Equal(g64,g80) = 2
    c: Coincident(g84,g85)
    c: Coincident(g85,g86)
    c: Coincident(g86,g87)
    c: Coincident(g87,g84)
    c: Horizontal(g84)
    c: Horizontal(g86)
    c: Vertical(g85)
    c: Vertical(g87)
    c: Coincident(g88,g89)
    c: Coincident(g89,g90)
    c: Coincident(g90,g91)
    c: Coincident(g91,g88)
    c: Horizontal(g88)
    c: Horizontal(g90)
    c: Vertical(g89)
    c: Vertical(g91)
    c: Coincident(g92,g93)
    c: Coincident(g93,g94)
    c: Coincident(g94,g95)
    c: Coincident(g95,g92)
    c: Horizontal(g92)
    c: Horizontal(g94)
    c: Vertical(g93)
    c: Vertical(g95)
    c: Equal(g94,g90)
    c: Equal(g90,g84)
    c: Equal(g84,g80)
    c: Equal(g81,g85)
    c: Equal(g85,g89)
    c: Equal(g89,g93)
    c: DistanceY(g80,g84) = 2
    c: DistanceY(g84,g89) = 2
    c: DistanceX(g78,g93) = 20
    c: Vertical(g92,g88)
    c: Vertical(g89,g85)
    c: Vertical(g84,g81)
    c: Horizontal(g76,g92)
    c: Coincident(g96,g97)
    c: Coincident(g97,g98)
    c: Coincident(g98,g99)
    c: Coincident(g99,g96)
    c: Horizontal(g96)
    c: Horizontal(g98)
    c: Vertical(g97)
    c: Vertical(g99)
    c: Equal(g65,g97) = 0.2
    c: Equal(g64,g96) = 2
    c: Coincident(g100,g101)
    c: Coincident(g101,g102)
    c: Coincident(g102,g103)
    c: Coincident(g103,g100)
    c: Horizontal(g100)
    c: Horizontal(g102)
    c: Vertical(g101)
    c: Vertical(g103)
    c: Coincident(g104,g105)
    c: Coincident(g105,g106)
    c: Coincident(g106,g107)
    c: Coincident(g107,g104)
    c: Horizontal(g104)
    c: Horizontal(g106)
    c: Vertical(g105)
    c: Vertical(g107)
    c: Coincident(g108,g109)
    c: Coincident(g109,g110)
    c: Coincident(g110,g111)
    c: Coincident(g111,g108)
    c: Horizontal(g108)
    c: Horizontal(g110)
    c: Vertical(g109)
    c: Vertical(g111)
    c: Equal(g110,g106)
    c: Equal(g106,g100)
    c: Equal(g100,g96)
    c: Equal(g97,g101)
    c: Equal(g101,g105)
    c: Equal(g105,g109)
    c: DistanceY(g96,g100) = 2
    c: DistanceY(g100,g105) = 2
    c: Coincident(g112,g113)
    c: Coincident(g113,g114)
    c: Coincident(g114,g115)
    c: Coincident(g115,g112)
    c: Horizontal(g112)
    c: Horizontal(g114)
    c: Vertical(g113)
    c: Vertical(g115)
    c: Equal(g97,g113) = 0.2
    c: Equal(g96,g112) = 2
    c: Coincident(g116,g117)
    c: Coincident(g117,g118)
    c: Coincident(g118,g119)
    c: Coincident(g119,g116)
    c: Horizontal(g116)
    c: Horizontal(g118)
    c: Vertical(g117)
    c: Vertical(g119)
    c: Coincident(g120,g121)
    c: Coincident(g121,g122)
    c: Coincident(g122,g123)
    c: Coincident(g123,g120)
    c: Horizontal(g120)
    c: Horizontal(g122)
    c: Vertical(g121)
    c: Vertical(g123)
    c: Coincident(g124,g125)
    c: Coincident(g125,g126)
    c: Coincident(g126,g127)
    c: Coincident(g127,g124)
    c: Horizontal(g124)
    c: Horizontal(g126)
    c: Vertical(g125)
    c: Vertical(g127)
    c: Equal(g126,g122)
    c: Equal(g122,g116)
    c: Equal(g116,g112)
    c: Equal(g113,g117)
    c: Equal(g117,g121)
    c: Equal(g121,g125)
    c: DistanceY(g112,g116) = 2
    c: DistanceY(g116,g121) = 2
    c: DistanceX(g110,g125) = 20
    c: Vertical(g124,g120)
    c: Vertical(g121,g117)
    c: Vertical(g116,g113)
    c: Horizontal(g108,g124)
    c: DistanceY(g64,g68) = 2
    c: DistanceY(g108,g64) = 4
    c: DistanceY(g105,g108) = 2
    c: Coincident(g65,g64)
    c: DistanceY(g122,g124) = 2
    c: DistanceY(g90,g92) = 2
    c: DistanceY(g73,g76) = 2
    c: Vertical(g64,g110)
    c: Vertical(g104,g108)
    c: Vertical(g102,g106)
    c: Vertical(g98,g100)
    c: Vertical(g78,g32)
    c: DistanceY(g76,g32) = 4
    c: Vertical(g76,g72)
    c: Vertical(g70,g74)
    c: Vertical(g66,g68)
    c: Coincident(g129,g130)
    c: Coincident(g130,g131)
    c: Coincident(g131,g128)
    c: Horizontal(g128)
    c: Horizontal(g130)
    c: Vertical(g129)
    c: Vertical(g131)
    c: Coincident(g132,g133)
    c: Coincident(g133,g134)
    c: Coincident(g134,g135)
    c: Coincident(g135,g132)
    c: Horizontal(g132)
    c: Horizontal(g134)
    c: Vertical(g133)
    c: Vertical(g135)
    c: Coincident(g136,g137)
    c: Coincident(g137,g138)
    c: Coincident(g138,g139)
    c: Coincident(g139,g136)
    c: Horizontal(g136)
    c: Horizontal(g138)
    c: Vertical(g137)
    c: Vertical(g139)
    c: Coincident(g140,g141)
    c: Coincident(g141,g142)
    c: Coincident(g142,g143)
    c: Coincident(g143,g140)
    c: Horizontal(g140)
    c: Horizontal(g142)
    c: Vertical(g141)
    c: Vertical(g143)
    c: Equal(g142,g138)
    c: Equal(g138,g132)
    c: Equal(g132,g128)
    c: Equal(g129,g133)
    c: Equal(g133,g137)
    c: Equal(g137,g141)
    c: DistanceY(g132,g137) = 2
    c: Coincident(g144,g145)
    c: Coincident(g145,g146)
    c: Coincident(g146,g147)
    c: Coincident(g147,g144)
    c: Horizontal(g144)
    c: Horizontal(g146)
    c: Vertical(g145)
    c: Vertical(g147)
    c: Equal(g129,g145) = 0.2
    c: Equal(g128,g144) = 2
    c: Coincident(g148,g149)
    c: Coincident(g149,g150)
    c: Coincident(g150,g151)
    c: Coincident(g151,g148)
    c: Horizontal(g148)
    c: Horizontal(g150)
    c: Vertical(g149)
    c: Vertical(g151)
    c: Coincident(g152,g153)
    c: Coincident(g153,g154)
    c: Coincident(g154,g155)
    c: Coincident(g155,g152)
    c: Horizontal(g152)
    c: Horizontal(g154)
    c: Vertical(g153)
    c: Vertical(g155)
    c: Coincident(g156,g157)
    c: Coincident(g157,g158)
    c: Coincident(g158,g159)
    c: Coincident(g159,g156)
    c: Horizontal(g156)
    c: Horizontal(g158)
    c: Vertical(g157)
    c: Vertical(g159)
    c: Equal(g158,g154)
    c: Equal(g154,g148)
    c: Equal(g148,g144)
    c: Equal(g145,g149)
    c: Equal(g149,g153)
    c: Equal(g153,g157)
    c: DistanceY(g144,g148) = 2
    c: DistanceY(g148,g153) = 2
    c: DistanceX(g142,g157) = 20
    c: Vertical(g156,g152)
    c: Vertical(g153,g149)
    c: Vertical(g148,g145)
    c: Horizontal(g140,g156)
    c: DistanceY(g128,g132) = 2
    c: Coincident(g129,g128)
    c: DistanceY(g154,g156) = 2
    c: DistanceY(g137,g140) = 2
    c: Vertical(g140,g136)
    c: Vertical(g134,g138)
    c: Vertical(g130,g132)
    c: Vertical(g96,g142)
    c: DistanceY(g140,g96) = 4
    c: Equal(g97,g137)
    c: DistanceY(g0) = 1.95
    c: Equal(g114,g158)
    c: Coincident(g161,g162)
    c: Coincident(g162,g163)
    c: Coincident(g163,g160)
    c: Horizontal(g160)
    c: Horizontal(g162)
    c: Vertical(g161)
    c: Vertical(g163)
    c: Equal(g1,g161) = 0.2
    c: Equal(g0,g160) = 2
    c: Coincident(g164,g165)
    c: Coincident(g165,g166)
    c: Coincident(g166,g167)
    c: Coincident(g167,g164)
    c: Horizontal(g164)
    c: Horizontal(g166)
    c: Vertical(g165)
    c: Vertical(g167)
    c: Coincident(g168,g169)
    c: Coincident(g169,g170)
    c: Coincident(g170,g171)
    c: Coincident(g171,g168)
    c: Horizontal(g168)
    c: Horizontal(g170)
    c: Vertical(g169)
    c: Vertical(g171)
    c: Coincident(g172,g173)
    c: Coincident(g173,g174)
    c: Coincident(g174,g175)
    c: Coincident(g175,g172)
    c: Horizontal(g172)
    c: Horizontal(g174)
    c: Vertical(g173)
    c: Vertical(g175)
    c: Equal(g174,g170)
    c: Equal(g170,g164)
    c: Equal(g164,g160)
    c: Equal(g161,g165)
    c: Equal(g165,g169)
    c: Equal(g169,g173)
    c: DistanceY(g164,g169) = 2
    c: Coincident(g176,g177)
    c: Coincident(g177,g178)
    c: Coincident(g178,g179)
    c: Coincident(g179,g176)
    c: Horizontal(g176)
    c: Horizontal(g178)
    c: Vertical(g177)
    c: Vertical(g179)
    c: Equal(g161,g177) = 0.2
    c: Equal(g160,g176) = 2
    c: Coincident(g180,g181)
    c: Coincident(g181,g182)
    c: Coincident(g182,g183)
    c: Coincident(g183,g180)
    c: Horizontal(g180)
    c: Horizontal(g182)
    c: Vertical(g181)
    c: Vertical(g183)
    c: Coincident(g184,g185)
    c: Coincident(g185,g186)
    c: Coincident(g186,g187)
    c: Coincident(g187,g184)
    c: Horizontal(g184)
    c: Horizontal(g186)
    c: Vertical(g185)
    c: Vertical(g187)
    c: Coincident(g188,g189)
    c: Coincident(g189,g190)
    c: Coincident(g190,g191)
    c: Coincident(g191,g188)
    c: Horizontal(g188)
    c: Horizontal(g190)
    c: Vertical(g189)
    c: Vertical(g191)
    c: Equal(g190,g186)
    c: Equal(g186,g180)
    c: Equal(g180,g176)
    c: Equal(g177,g181)
    c: Equal(g181,g185)
    c: Equal(g185,g189)
    c: DistanceY(g176,g180) = 2
    c: DistanceY(g180,g185) = 2
    c: DistanceX(g174,g189) = 20
    c: Vertical(g188,g184)
    c: Vertical(g185,g181)
    c: Vertical(g180,g177)
    c: Horizontal(g172,g188)
    c: DistanceY(g160,g164) = 2
    c: Coincident(g161,g160)
    c: DistanceY(g186,g188) = 2
    c: DistanceY(g169,g172) = 2
    c: DistanceY(g28,g176) = 4
    c: PointOnObject(g172,g-2)
    c: PointOnObject(g160,g-2)
    c: Vertical(g164,g162)
    c: Vertical(g170,g166)
FEATURE [PartDesign::Pocket] Pocket008
  BaseFeature = -> Pocket007
  Length = 1
  Length2 = 100
  Profile = -> Sketch010
  Reversed = true
  Type = 0
FEATURE [PartDesign::Pocket] Pocket009
  BaseFeature = -> Pocket008
  Length = 1
  Length2 = 100
  Profile = -> Sketch011
  Reversed = true
  Type = 0
FEATURE [Part::Part2DObjectPython] ShapeString003  # Draft 2D object (typed FeaturePython)
  AttachmentOffset = pos=(12,32,0) rot=(0.707107,-0.707107,0;3.14159rad)
  FontFile = <path> Squares/AdobeGothicStd-Bold.otf
  MapMode = 5
  Placement = pos=(12,32,-3) rot=(0.707107,-0.707107,0;3.14159rad)
  Size = 4
  String =         2     1     0      1     0     1     2  
  Support = -> [DatumPlane]
  Tracking = 0
FEATURE [PartDesign::Plane] DatumPlane001
  AttachmentOffset = pos=(0,0,240) rot=(0,0,1;0rad)
  Length = 92.6491
  MapMode = 4
  Placement = pos=(240,0,0) rot=(0.57735,0.57735,0.57735;2.0944rad)
  ResizeMode = 0
  Support = -> [XY_Plane]
  Width = 62.6491
FEATURE [Sketcher::SketchObject] Sketch012
  FullyConstrained = true
  MapMode = 5
  Placement = pos=(240,0,0) rot=(0.57735,0.57735,0.57735;2.0944rad)
  Support = -> [DatumPlane001]
  sketch-geometry (8):
    g0: LineSegment StartX=-9 StartY=-0.75 StartZ=0 EndX=-4 EndY=-0.75 EndZ=0
    g1: LineSegment StartX=-4 StartY=-0.75 StartZ=0 EndX=-4 EndY=-2.25 EndZ=0
    g2: LineSegment StartX=-4 StartY=-2.25 StartZ=0 EndX=-9 EndY=-2.25 EndZ=0
    g3: LineSegment StartX=-9 StartY=-2.25 StartZ=0 EndX=-9 EndY=-0.75 EndZ=0
    g4: LineSegment StartX=-17.5 StartY=-2.25 StartZ=0 EndX=-12.5 EndY=-2.25 EndZ=0
    g5: LineSegment StartX=-12.5 StartY=-2.25 StartZ=0 EndX=-12.5 EndY=-0.75 EndZ=0
    g6: LineSegment StartX=-12.5 StartY=-0.75 StartZ=0 EndX=-17.5 EndY=-0.75 EndZ=0
    g7: LineSegment StartX=-17.5 StartY=-0.75 StartZ=0 EndX=-17.5 EndY=-2.25 EndZ=0
  constraints (24):
    c: Coincident(g0,g1)
    c: Coincident(g1,g2)
    c: Coincident(g2,g3)
    c: Coincident(g3,g0)
    c: Horizontal(g0)
    c: Horizontal(g2)
    c: Vertical(g1)
    c: Vertical(g3)
    c: DistanceY(g1,g1) = 1.5
    c: DistanceX(g0,g0) = 5
    c: DistanceX(g1,g-1) = 4
    c: DistanceY(g0,g-1) = 0.75
    c: Coincident(g4,g5)
    c: Coincident(g5,g6)
    c: Coincident(g6,g7)
    c: Coincident(g7,g4)
    c: Horizontal(g4)
    c: Horizontal(g6)
    c: Vertical(g5)
    c: Vertical(g7)
    c: Equal(g3,g7)
    c: Equal(g4,g0)
    c: Horizontal(g2,g4)
    c: DistanceX(g5,g0) = 3.5
FEATURE [PartDesign::Pocket] Pocket010
  BaseFeature = -> Pocket009
  Length = 8
  Length2 = 100
  Profile = -> Sketch012
  Type = 0
FEATURE [Sketcher::SketchObject] Sketch013
  FullyConstrained = true
  MapMode = 5
  Support = -> [XY_Plane002]
  sketch-geometry (4):
    g0: LineSegment StartX=0 StartY=0 StartZ=0 EndX=70 EndY=0 EndZ=0
    g1: LineSegment StartX=70 StartY=0 StartZ=0 EndX=70 EndY=-20 EndZ=0
    g2: LineSegment StartX=70 StartY=-20 StartZ=0 EndX=0 EndY=-20 EndZ=0
    g3: LineSegment StartX=0 StartY=-20 StartZ=0 EndX=0 EndY=0 EndZ=0
  constraints (11):
    c: Coincident(g0,g1)
    c: Coincident(g1,g2)
    c: Coincident(g2,g3)
    c: Coincident(g3,g0)
    c: Horizontal(g0)
    c: Horizontal(g2)
    c: Vertical(g1)
    c: Vertical(g3)
    c: DistanceX(g0,g0) = 70
    c: DistanceY(g1,g1) = 20
    c: Coincident(g-1,g0)
FEATURE [PartDesign::Pad] Pad002
  Direction = (1,1,1)
  Length = 3
  Length2 = 100
  Profile = -> Sketch013
  Type = 0
FEATURE [Sketcher::SketchObject] Sketch015  label="hz cm002"
  FullyConstrained = true
  MapMode = 5
  Support = -> [XY_Plane002]
  expr: Constraints[8] = Spreadsheet.reticleCmHeight
  expr: Constraints[9] = Spreadsheet.reticleCmWidth
  sketch-geometry (61):
    g0: LineSegment StartX=60.2 StartY=-20 StartZ=0 EndX=60 EndY=-20 EndZ=0
    g1: LineSegment StartX=60 StartY=-20 StartZ=0 EndX=60 EndY=-16 EndZ=0
    g2: LineSegment StartX=60 StartY=-16 StartZ=0 EndX=60.2 EndY=-16 EndZ=0
    g3: LineSegment StartX=60.2 StartY=-16 StartZ=0 EndX=60.2 EndY=-20 EndZ=0
    g4: LineSegment StartX=0 StartY=-20 StartZ=0 EndX=80 EndY=-20 EndZ=0
    g5: LineSegment StartX=50.2 StartY=-20 StartZ=0 EndX=50 EndY=-20 EndZ=0
    g6: LineSegment StartX=50 StartY=-20 StartZ=0 EndX=50 EndY=-16 EndZ=0
    g7: LineSegment StartX=50 StartY=-16 StartZ=0 EndX=50.2 EndY=-16 EndZ=0
    g8: LineSegment StartX=50.2 StartY=-16 StartZ=0 EndX=50.2 EndY=-20 EndZ=0
    g9: LineSegment StartX=60.2 StartY=-20 StartZ=0 EndX=50.2 EndY=-20 EndZ=0
    g10: LineSegment StartX=40.2 StartY=-20 StartZ=0 EndX=40 EndY=-20 EndZ=0
    g11: LineSegment StartX=40 StartY=-20 StartZ=0 EndX=40 EndY=-16 EndZ=0
    g12: LineSegment StartX=40 StartY=-16 StartZ=0 EndX=40.2 EndY=-16 EndZ=0
    g13: LineSegment StartX=40.2 StartY=-16 StartZ=0 EndX=40.2 EndY=-20 EndZ=0
    g14: LineSegment StartX=50.2 StartY=-20 StartZ=0 EndX=40.2 EndY=-20 EndZ=0
    g15: LineSegment StartX=30.2 StartY=-20 StartZ=0 EndX=30 EndY=-20 EndZ=0
    g16: LineSegment StartX=30 StartY=-20 StartZ=0 EndX=30 EndY=-16 EndZ=0
    g17: LineSegment StartX=30 StartY=-16 StartZ=0 EndX=30.2 EndY=-16 EndZ=0
    g18: LineSegment StartX=30.2 StartY=-16 StartZ=0 EndX=30.2 EndY=-20 EndZ=0
    g19: LineSegment StartX=40.2 StartY=-20 StartZ=0 EndX=30.2 EndY=-20 EndZ=0
    g20: LineSegment StartX=20.2 StartY=-20 StartZ=0 EndX=20 EndY=-20 EndZ=0
    g21: LineSegment StartX=20 StartY=-20 StartZ=0 EndX=20 EndY=-16 EndZ=0
    g22: LineSegment StartX=20 StartY=-16 StartZ=0 EndX=20.2 EndY=-16 EndZ=0
    g23: LineSegment StartX=20.2 StartY=-16 StartZ=0 EndX=20.2 EndY=-20 EndZ=0
    g24: LineSegment StartX=30.2 StartY=-20 StartZ=0 EndX=20.2 EndY=-20 EndZ=0
    g25: LineSegment StartX=10.2 StartY=-20 StartZ=0 EndX=10 EndY=-20 EndZ=0
    g26: LineSegment StartX=10 StartY=-20 StartZ=0 EndX=10 EndY=-16 EndZ=0
    g27: LineSegment StartX=10 StartY=-16 StartZ=0 EndX=10.2 EndY=-16 EndZ=0
    g28: LineSegment StartX=10.2 StartY=-16 StartZ=0 EndX=10.2 EndY=-20 EndZ=0
    g29: LineSegment StartX=20.2 StartY=-20 StartZ=0 EndX=10.2 EndY=-20 EndZ=0
    g30: LineSegment StartX=10.2 StartY=-20 StartZ=0 EndX=0.2 EndY=-20 EndZ=0
    g31: LineSegment StartX=60 StartY=-4 StartZ=0 EndX=60.2 EndY=-4 EndZ=0
    g32: LineSegment StartX=60.2 StartY=-4 StartZ=0 EndX=60.2 EndY=0 EndZ=0
    g33: LineSegment StartX=60.2 StartY=0 StartZ=0 EndX=60 EndY=0 EndZ=0
    g34: LineSegment StartX=60 StartY=0 StartZ=0 EndX=60 EndY=-4 EndZ=0
    g35: LineSegment StartX=50 StartY=-4 StartZ=0 EndX=49.8 EndY=-4 EndZ=0
    g36: LineSegment StartX=49.8 StartY=-4 StartZ=0 EndX=49.8 EndY=1.8e-15 EndZ=0
    g37: LineSegment StartX=49.8 StartY=1.5e-15 StartZ=0 EndX=50 EndY=1.5e-15 EndZ=0
    g38: LineSegment StartX=50 StartY=1.5e-15 StartZ=0 EndX=50 EndY=-4 EndZ=0
    g39: LineSegment StartX=60 StartY=-4 StartZ=0 EndX=50 EndY=-4 EndZ=0
    g40: LineSegment StartX=40 StartY=-4 StartZ=0 EndX=39.8 EndY=-4 EndZ=0
    g41: LineSegment StartX=39.8 StartY=-4 StartZ=0 EndX=39.8 EndY=1.8e-15 EndZ=0
    g42: LineSegment StartX=39.8 StartY=1.8e-15 StartZ=0 EndX=40 EndY=1.8e-15 EndZ=0
    g43: LineSegment StartX=40 StartY=1.8e-15 StartZ=0 EndX=40 EndY=-4 EndZ=0
    g44: LineSegment StartX=50 StartY=-4 StartZ=0 EndX=40 EndY=-4 EndZ=0
    g45: LineSegment StartX=30 StartY=-4 StartZ=0 EndX=29.8 EndY=-4 EndZ=0
    g46: LineSegment StartX=29.8 StartY=-4 StartZ=0 EndX=29.8 EndY=3.6e-15 EndZ=0
    g47: LineSegment StartX=29.8 StartY=3.9e-15 StartZ=0 EndX=30 EndY=3.9e-15 EndZ=0
    g48: LineSegment StartX=30 StartY=3.9e-15 StartZ=0 EndX=30 EndY=-4 EndZ=0
    g49: LineSegment StartX=40 StartY=-4 StartZ=0 EndX=30 EndY=-4 EndZ=0
    g50: LineSegment StartX=20 StartY=-4 StartZ=0 EndX=19.8 EndY=-4 EndZ=0
    g51: LineSegment StartX=19.8 StartY=-4 StartZ=0 EndX=19.8 EndY=4.4e-15 EndZ=0
    g52: LineSegment StartX=19.8 StartY=4.5e-15 StartZ=0 EndX=20 EndY=4.5e-15 EndZ=0
    g53: LineSegment StartX=20 StartY=4.5e-15 StartZ=0 EndX=20 EndY=-4 EndZ=0
    g54: LineSegment StartX=30 StartY=-4 StartZ=0 EndX=20 EndY=-4 EndZ=0
    g55: LineSegment StartX=10 StartY=-4 StartZ=0 EndX=9.8 EndY=-4 EndZ=0
    g56: LineSegment StartX=9.8 StartY=-4 StartZ=0 EndX=9.8 EndY=-3.206e-13 EndZ=0
    g57: LineSegment StartX=9.8 StartY=-3.206e-13 StartZ=0 EndX=10 EndY=-3.206e-13 EndZ=0
    g58: LineSegment StartX=10 StartY=-3.206e-13 StartZ=0 EndX=10 EndY=-4 EndZ=0
    g59: LineSegment StartX=20 StartY=-4 StartZ=0 EndX=10 EndY=-4 EndZ=0
    g60: LineSegment StartX=10 StartY=-4 StartZ=0 EndX=0 EndY=-4 EndZ=0
  constraints (174):
    c: Coincident(g0,g1)
    c: Coincident(g1,g2)
    c: Coincident(g2,g3)
    c: Coincident(g3,g0)
    c: Horizontal(g0)
    c: Horizontal(g2)
    c: Vertical(g1)
    c: Vertical(g3)
    c: DistanceY(g3,g3) = 4
    c: DistanceX(g2,g2) = 0.2
    c: Horizontal(g4)
    c: DistanceY(g4,g-1) = 20
    c: PointOnObject(g0,g4)
    c: Coincident(g5,g6)
    c: Coincident(g6,g7)
    c: Coincident(g7,g8)
    c: Coincident(g8,g5)
    c: Horizontal(g5)
    c: Horizontal(g7)
    c: Vertical(g6)
    c: Vertical(g8)
    c: Equal(g3,g8) = 4
    c: Equal(g2,g7) = 0.35
    c: Coincident(g0,g9)
    c: Coincident(g5,g9)
    c: Distance(g9) = 10
    c: Angle(g9) = 3.14159
    c: Coincident(g10,g11)
    c: Coincident(g11,g12)
    c: Coincident(g12,g13)
    c: Coincident(g13,g10)
    c: Horizontal(g10)
    c: Horizontal(g12)
    c: Vertical(g11)
    c: Vertical(g13)
    c: Equal(g3,g13) = 4
    c: Equal(g2,g12) = 0.35
    c: Coincident(g5,g14)
    c: Coincident(g10,g14)
    c: Equal(g9,g14)
    c: Parallel(g14,g9)
    c: Coincident(g15,g16)
    c: Coincident(g16,g17)
    c: Coincident(g17,g18)
    c: Coincident(g18,g15)
    c: Horizontal(g15)
    c: Horizontal(g17)
    c: Vertical(g16)
    c: Vertical(g18)
    c: Equal(g3,g18) = 4
    c: Equal(g2,g17) = 0.35
    c: Coincident(g10,g19)
    c: Coincident(g15,g19)
    c: Equal(g9,g19)
    c: Parallel(g19,g9)
    c: Coincident(g20,g21)
    c: Coincident(g21,g22)
    c: Coincident(g22,g23)
    c: Coincident(g23,g20)
    c: Horizontal(g20)
    c: Horizontal(g22)
    c: Vertical(g21)
    c: Vertical(g23)
    c: Equal(g3,g23) = 4
    c: Equal(g2,g22) = 0.35
    c: Coincident(g15,g24)
    c: Coincident(g20,g24)
    c: Equal(g9,g24)
    c: Parallel(g24,g9)
    c: Coincident(g25,g26)
    c: Coincident(g26,g27)
    c: Coincident(g27,g28)
    c: Coincident(g28,g25)
    c: Horizontal(g25)
    c: Horizontal(g27)
    c: Vertical(g26)
    c: Vertical(g28)
    c: Equal(g3,g28) = 4
    c: Equal(g2,g27) = 0.35
    c: Coincident(g20,g29)
    c: Coincident(g25,g29)
    c: Equal(g9,g29)
    c: Parallel(g29,g9)
    c: Coincident(g25,g30)
    c: Equal(g9,g30)
    c: Parallel(g30,g9)
    c: Coincident(g31,g32)
    c: Coincident(g32,g33)
    c: Coincident(g33,g34)
    c: Coincident(g34,g31)
    c: Horizontal(g31)
    c: Horizontal(g33)
    c: Vertical(g32)
    c: Vertical(g34)
    c: Equal(g3,g34) = 4
    c: Equal(g2,g33) = 0.35
    c: Coincident(g35,g36)
    c: Coincident(g36,g37)
    c: Coincident(g37,g38)
    c: Coincident(g38,g35)
    c: Horizontal(g35)
    c: Horizontal(g37)
    c: Vertical(g36)
    c: Vertical(g38)
    c: Equal(g3,g38) = 4
    c: Equal(g2,g37) = 0.35
    c: Coincident(g31,g39)
    c: Coincident(g35,g39)
    c: Equal(g9,g39)
    c: Parallel(g39,g9)
    c: Coincident(g40,g41)
    c: Coincident(g41,g42)
    c: Coincident(g42,g43)
    c: Coincident(g43,g40)
    c: Horizontal(g40)
    c: Horizontal(g42)
    c: Vertical(g41)
    c: Vertical(g43)
    c: Equal(g3,g43) = 4
    c: Equal(g2,g42) = 0.35
    c: Coincident(g35,g44)
    c: Coincident(g40,g44)
    c: Equal(g9,g44)
    c: Parallel(g44,g9)
    c: Coincident(g45,g46)
    c: Coincident(g46,g47)
    c: Coincident(g47,g48)
    c: Coincident(g48,g45)
    c: Horizontal(g45)
    c: Horizontal(g47)
    c: Vertical(g46)
    c: Vertical(g48)
    c: Equal(g3,g48) = 4
    c: Equal(g2,g47) = 0.35
    c: Coincident(g40,g49)
    c: Coincident(g45,g49)
    c: Equal(g9,g49)
    c: Parallel(g49,g9)
    c: Coincident(g50,g51)
    c: Coincident(g51,g52)
    c: Coincident(g52,g53)
    c: Coincident(g53,g50)
    c: Horizontal(g50)
    c: Horizontal(g52)
    c: Vertical(g51)
    c: Vertical(g53)
    c: Equal(g3,g53) = 4
    c: Equal(g2,g52) = 0.35
    c: Coincident(g45,g54)
    c: Coincident(g50,g54)
    c: Equal(g9,g54)
    c: Parallel(g54,g9)
    c: Coincident(g55,g56)
    c: Coincident(g56,g57)
    c: Coincident(g57,g58)
    c: Coincident(g58,g55)
    c: Horizontal(g55)
    c: Horizontal(g57)
    c: Vertical(g56)
    c: Vertical(g58)
    c: Equal(g3,g58) = 4
    c: Equal(g2,g57) = 0.35
    c: Coincident(g50,g59)
    c: Coincident(g55,g59)
    c: Equal(g9,g59)
    c: Parallel(g59,g9)
    c: Coincident(g55,g60)
    c: Equal(g9,g60)
    c: Parallel(g60,g9)
    c: DistanceY(g-1,g32) = 0
    c: Vertical(g31,g2)
    c: DistanceX(g-1,g56) = 9.8
    c: DistanceX(g4,g4) = 80
    c: PointOnObject(g4,g-2)
FEATURE [PartDesign::Pocket] Pocket011
  BaseFeature = -> Pad002
  Length = 1
  Length2 = 100
  Profile = -> Sketch015
  Reversed = true
  Type = 0
FEATURE [Sketcher::SketchObject] Sketch016  label="hz mm002"
  FullyConstrained = true
  MapMode = 5
  Support = -> [XY_Plane002]
  expr: Constraints[14] = Spreadsheet.reticleCmWidth
  expr: Constraints[13] = Spreadsheet.reticleCmHeight / 2
  sketch-geometry (225):
    g0: LineSegment StartX=-30 StartY=-20 StartZ=0 EndX=70 EndY=-20 EndZ=0
    g1: LineSegment StartX=68 StartY=0 StartZ=0 EndX=67.8 EndY=0 EndZ=0
    g2: LineSegment StartX=67.8 StartY=0 StartZ=0 EndX=67.8 EndY=-2 EndZ=0
    g3: LineSegment StartX=67.8 StartY=-2 StartZ=0 EndX=68 EndY=-2 EndZ=0
    g4: LineSegment StartX=68 StartY=-2 StartZ=0 EndX=68 EndY=0 EndZ=0
    g5: LineSegment StartX=66 StartY=0 StartZ=0 EndX=65.8 EndY=0 EndZ=0
    g6: LineSegment StartX=65.8 StartY=0 StartZ=0 EndX=65.8 EndY=-2 EndZ=0
    g7: LineSegment StartX=65.8 StartY=-2 StartZ=0 EndX=66 EndY=-2 EndZ=0
    g8: LineSegment StartX=66 StartY=-2 StartZ=0 EndX=66 EndY=0 EndZ=0
    g9: LineSegment StartX=64 StartY=0 StartZ=0 EndX=63.8 EndY=0 EndZ=0
    g10: LineSegment StartX=63.8 StartY=0 StartZ=0 EndX=63.8 EndY=-2 EndZ=0
    g11: LineSegment StartX=63.8 StartY=-2 StartZ=0 EndX=64 EndY=-2 EndZ=0
    g12: LineSegment StartX=64 StartY=-2 StartZ=0 EndX=64 EndY=0 EndZ=0
    g13: LineSegment StartX=61.8 StartY=0 StartZ=0 EndX=62 EndY=0 EndZ=0
    g14: LineSegment StartX=62 StartY=0 StartZ=0 EndX=62 EndY=-2 EndZ=0
    g15: LineSegment StartX=62 StartY=-2 StartZ=0 EndX=61.8 EndY=-2 EndZ=0
    g16: LineSegment StartX=61.8 StartY=-2 StartZ=0 EndX=61.8 EndY=0 EndZ=0
    g17: LineSegment StartX=57.8 StartY=0 StartZ=0 EndX=58 EndY=0 EndZ=0
    g18: LineSegment StartX=58 StartY=0 StartZ=0 EndX=58 EndY=-2 EndZ=0
    g19: LineSegment StartX=58 StartY=-2 StartZ=0 EndX=57.8 EndY=-2 EndZ=0
    g20: LineSegment StartX=57.8 StartY=-2 StartZ=0 EndX=57.8 EndY=0 EndZ=0
    g21: LineSegment StartX=56 StartY=0 StartZ=0 EndX=55.8 EndY=0 EndZ=0
    g22: LineSegment StartX=55.8 StartY=0 StartZ=0 EndX=55.8 EndY=-2 EndZ=0
    g23: LineSegment StartX=55.8 StartY=-2 StartZ=0 EndX=56 EndY=-2 EndZ=0
    g24: LineSegment StartX=56 StartY=-2 StartZ=0 EndX=56 EndY=0 EndZ=0
    g25: LineSegment StartX=54 StartY=0 StartZ=0 EndX=53.8 EndY=0 EndZ=0
    g26: LineSegment StartX=53.8 StartY=0 StartZ=0 EndX=53.8 EndY=-2 EndZ=0
    g27: LineSegment StartX=53.8 StartY=-2 StartZ=0 EndX=54 EndY=-2 EndZ=0
    g28: LineSegment StartX=54 StartY=-2 StartZ=0 EndX=54 EndY=0 EndZ=0
    g29: LineSegment StartX=51.8 StartY=0 StartZ=0 EndX=52 EndY=0 EndZ=0
    g30: LineSegment StartX=52 StartY=0 StartZ=0 EndX=52 EndY=-2 EndZ=0
    g31: LineSegment StartX=52 StartY=-2 StartZ=0 EndX=51.8 EndY=-2 EndZ=0
    g32: LineSegment StartX=51.8 StartY=-2 StartZ=0 EndX=51.8 EndY=0 EndZ=0
    g33: LineSegment StartX=48 StartY=0 StartZ=0 EndX=47.8 EndY=0 EndZ=0
    g34: LineSegment StartX=47.8 StartY=0 StartZ=0 EndX=47.8 EndY=-2 EndZ=0
    g35: LineSegment StartX=47.8 StartY=-2 StartZ=0 EndX=48 EndY=-2 EndZ=0
    g36: LineSegment StartX=48 StartY=-2 StartZ=0 EndX=48 EndY=0 EndZ=0
    g37: LineSegment StartX=46 StartY=0 StartZ=0 EndX=45.8 EndY=0 EndZ=0
    g38: LineSegment StartX=45.8 StartY=0 StartZ=0 EndX=45.8 EndY=-2 EndZ=0
    g39: LineSegment StartX=45.8 StartY=-2 StartZ=0 EndX=46 EndY=-2 EndZ=0
    g40: LineSegment StartX=46 StartY=-2 StartZ=0 EndX=46 EndY=0 EndZ=0
    g41: LineSegment StartX=44 StartY=0 StartZ=0 EndX=43.8 EndY=0 EndZ=0
    g42: LineSegment StartX=43.8 StartY=0 StartZ=0 EndX=43.8 EndY=-2 EndZ=0
    g43: LineSegment StartX=43.8 StartY=-2 StartZ=0 EndX=44 EndY=-2 EndZ=0
    g44: LineSegment StartX=44 StartY=-2 StartZ=0 EndX=44 EndY=0 EndZ=0
    g45: LineSegment StartX=41.8 StartY=0 StartZ=0 EndX=42 EndY=0 EndZ=0
    g46: LineSegment StartX=42 StartY=0 StartZ=0 EndX=42 EndY=-2 EndZ=0
    g47: LineSegment StartX=42 StartY=-2 StartZ=0 EndX=41.8 EndY=-2 EndZ=0
    g48: LineSegment StartX=41.8 StartY=-2 StartZ=0 EndX=41.8 EndY=0 EndZ=0
    g49: LineSegment StartX=38 StartY=0 StartZ=0 EndX=37.8 EndY=0 EndZ=0
    g50: LineSegment StartX=37.8 StartY=0 StartZ=0 EndX=37.8 EndY=-2 EndZ=0
    g51: LineSegment StartX=37.8 StartY=-2 StartZ=0 EndX=38 EndY=-2 EndZ=0
    g52: LineSegment StartX=38 StartY=-2 StartZ=0 EndX=38 EndY=0 EndZ=0
    g53: LineSegment StartX=36 StartY=0 StartZ=0 EndX=35.8 EndY=0 EndZ=0
    g54: LineSegment StartX=35.8 StartY=0 StartZ=0 EndX=35.8 EndY=-2 EndZ=0
    g55: LineSegment StartX=35.8 StartY=-2 StartZ=0 EndX=36 EndY=-2 EndZ=0
    g56: LineSegment StartX=36 StartY=-2 StartZ=0 EndX=36 EndY=0 EndZ=0
    g57: LineSegment StartX=34 StartY=0 StartZ=0 EndX=33.8 EndY=0 EndZ=0
    g58: LineSegment StartX=33.8 StartY=0 StartZ=0 EndX=33.8 EndY=-2 EndZ=0
    g59: LineSegment StartX=33.8 StartY=-2 StartZ=0 EndX=34 EndY=-2 EndZ=0
    g60: LineSegment StartX=34 StartY=-2 StartZ=0 EndX=34 EndY=0 EndZ=0
    g61: LineSegment StartX=31.8 StartY=0 StartZ=0 EndX=32 EndY=0 EndZ=0
    g62: LineSegment StartX=32 StartY=0 StartZ=0 EndX=32 EndY=-2 EndZ=0
    g63: LineSegment StartX=32 StartY=-2 StartZ=0 EndX=31.8 EndY=-2 EndZ=0
    g64: LineSegment StartX=31.8 StartY=-2 StartZ=0 EndX=31.8 EndY=0 EndZ=0
    g65: LineSegment StartX=27.8 StartY=0 StartZ=0 EndX=28 EndY=0 EndZ=0
    g66: LineSegment StartX=28 StartY=0 StartZ=0 EndX=28 EndY=-2 EndZ=0
    g67: LineSegment StartX=28 StartY=-2 StartZ=0 EndX=27.8 EndY=-2 EndZ=0
    g68: LineSegment StartX=27.8 StartY=-2 StartZ=0 EndX=27.8 EndY=0 EndZ=0
    g69: LineSegment StartX=26 StartY=0 StartZ=0 EndX=25.8 EndY=0 EndZ=0
    g70: LineSegment StartX=25.8 StartY=0 StartZ=0 EndX=25.8 EndY=-2 EndZ=0
    g71: LineSegment StartX=25.8 StartY=-2 StartZ=0 EndX=26 EndY=-2 EndZ=0
    g72: LineSegment StartX=26 StartY=-2 StartZ=0 EndX=26 EndY=0 EndZ=0
    g73: LineSegment StartX=24 StartY=0 StartZ=0 EndX=23.8 EndY=0 EndZ=0
    g74: LineSegment StartX=23.8 StartY=0 StartZ=0 EndX=23.8 EndY=-2 EndZ=0
    g75: LineSegment StartX=23.8 StartY=-2 StartZ=0 EndX=24 EndY=-2 EndZ=0
    g76: LineSegment StartX=24 StartY=-2 StartZ=0 EndX=24 EndY=0 EndZ=0
    g77: LineSegment StartX=21.8 StartY=0 StartZ=0 EndX=22 EndY=0 EndZ=0
    g78: LineSegment StartX=22 StartY=0 StartZ=0 EndX=22 EndY=-2 EndZ=0
    g79: LineSegment StartX=22 StartY=-2 StartZ=0 EndX=21.8 EndY=-2 EndZ=0
    g80: LineSegment StartX=21.8 StartY=-2 StartZ=0 EndX=21.8 EndY=0 EndZ=0
    g81: LineSegment StartX=18 StartY=0 StartZ=0 EndX=17.8 EndY=0 EndZ=0
    g82: LineSegment StartX=17.8 StartY=0 StartZ=0 EndX=17.8 EndY=-2 EndZ=0
    g83: LineSegment StartX=17.8 StartY=-2 StartZ=0 EndX=18 EndY=-2 EndZ=0
    g84: LineSegment StartX=18 StartY=-2 StartZ=0 EndX=18 EndY=0 EndZ=0
    g85: LineSegment StartX=16 StartY=0 StartZ=0 EndX=15.8 EndY=0 EndZ=0
    g86: LineSegment StartX=15.8 StartY=0 StartZ=0 EndX=15.8 EndY=-2 EndZ=0
    g87: LineSegment StartX=15.8 StartY=-2 StartZ=0 EndX=16 EndY=-2 EndZ=0
    g88: LineSegment StartX=16 StartY=-2 StartZ=0 EndX=16 EndY=0 EndZ=0
    g89: LineSegment StartX=14 StartY=0 StartZ=0 EndX=13.8 EndY=0 EndZ=0
    g90: LineSegment StartX=13.8 StartY=0 StartZ=0 EndX=13.8 EndY=-2 EndZ=0
    g91: LineSegment StartX=13.8 StartY=-2 StartZ=0 EndX=14 EndY=-2 EndZ=0
    g92: LineSegment StartX=14 StartY=-2 StartZ=0 EndX=14 EndY=0 EndZ=0
    g93: LineSegment StartX=11.8 StartY=0 StartZ=0 EndX=12 EndY=0 EndZ=0
    g94: LineSegment StartX=12 StartY=0 StartZ=0 EndX=12 EndY=-2 EndZ=0
    g95: LineSegment StartX=12 StartY=-2 StartZ=0 EndX=11.8 EndY=-2 EndZ=0
    g96: LineSegment StartX=11.8 StartY=-2 StartZ=0 EndX=11.8 EndY=0 EndZ=0
    g97: LineSegment StartX=7.8 StartY=0 StartZ=0 EndX=8 EndY=0 EndZ=0
    g98: LineSegment StartX=8 StartY=0 StartZ=0 EndX=8 EndY=-2 EndZ=0
    g99: LineSegment StartX=8 StartY=-2 StartZ=0 EndX=7.8 EndY=-2 EndZ=0
    g100: LineSegment StartX=7.8 StartY=-2 StartZ=0 EndX=7.8 EndY=0 EndZ=0
    g101: LineSegment StartX=6 StartY=0 StartZ=0 EndX=5.8 EndY=0 EndZ=0
    g102: LineSegment StartX=5.8 StartY=0 StartZ=0 EndX=5.8 EndY=-2 EndZ=0
    g103: LineSegment StartX=5.8 StartY=-2 StartZ=0 EndX=6 EndY=-2 EndZ=0
    g104: LineSegment StartX=6 StartY=-2 StartZ=0 EndX=6 EndY=0 EndZ=0
    g105: LineSegment StartX=4 StartY=0 StartZ=0 EndX=3.8 EndY=0 EndZ=0
    g106: LineSegment StartX=3.8 StartY=0 StartZ=0 EndX=3.8 EndY=-2 EndZ=0
    g107: LineSegment StartX=3.8 StartY=-2 StartZ=0 EndX=4 EndY=-2 EndZ=0
    g108: LineSegment StartX=4 StartY=-2 StartZ=0 EndX=4 EndY=0 EndZ=0
    g109: LineSegment StartX=1.8 StartY=0 StartZ=0 EndX=2 EndY=0 EndZ=0
    g110: LineSegment StartX=2 StartY=0 StartZ=0 EndX=2 EndY=-2 EndZ=0
    g111: LineSegment StartX=2 StartY=-2 StartZ=0 EndX=1.8 EndY=-2 EndZ=0
    g112: LineSegment StartX=1.8 StartY=-2 StartZ=0 EndX=1.8 EndY=0 EndZ=0
    g113: LineSegment StartX=68 StartY=-18 StartZ=0 EndX=67.8 EndY=-18 EndZ=0
    g114: LineSegment StartX=67.8 StartY=-18 StartZ=0 EndX=67.8 EndY=-20 EndZ=0
    g115: LineSegment StartX=67.8 StartY=-20 StartZ=0 EndX=68 EndY=-20 EndZ=0
    g116: LineSegment StartX=68 StartY=-20 StartZ=0 EndX=68 EndY=-18 EndZ=0
    g117: LineSegment StartX=66 StartY=-18 StartZ=0 EndX=65.8 EndY=-18 EndZ=0
    g118: LineSegment StartX=65.8 StartY=-18 StartZ=0 EndX=65.8 EndY=-20 EndZ=0
    g119: LineSegment StartX=65.8 StartY=-20 StartZ=0 EndX=66 EndY=-20 EndZ=0
    g120: LineSegment StartX=66 StartY=-20 StartZ=0 EndX=66 EndY=-18 EndZ=0
    g121: LineSegment StartX=64 StartY=-18 StartZ=0 EndX=63.8 EndY=-18 EndZ=0
    g122: LineSegment StartX=63.8 StartY=-18 StartZ=0 EndX=63.8 EndY=-20 EndZ=0
    g123: LineSegment StartX=63.8 StartY=-20 StartZ=0 EndX=64 EndY=-20 EndZ=0
    g124: LineSegment StartX=64 StartY=-20 StartZ=0 EndX=64 EndY=-18 EndZ=0
    g125: LineSegment StartX=61.8 StartY=-18 StartZ=0 EndX=62 EndY=-18 EndZ=0
    g126: LineSegment StartX=62 StartY=-18 StartZ=0 EndX=62 EndY=-20 EndZ=0
    g127: LineSegment StartX=62 StartY=-20 StartZ=0 EndX=61.8 EndY=-20 EndZ=0
    g128: LineSegment StartX=61.8 StartY=-20 StartZ=0 EndX=61.8 EndY=-18 EndZ=0
    g129: LineSegment StartX=57.8 StartY=-18 StartZ=0 EndX=58 EndY=-18 EndZ=0
    g130: LineSegment StartX=58 StartY=-18 StartZ=0 EndX=58 EndY=-20 EndZ=0
    g131: LineSegment StartX=58 StartY=-20 StartZ=0 EndX=57.8 EndY=-20 EndZ=0
    g132: LineSegment StartX=57.8 StartY=-20 StartZ=0 EndX=57.8 EndY=-18 EndZ=0
    g133: LineSegment StartX=56 StartY=-18 StartZ=0 EndX=55.8 EndY=-18 EndZ=0
    g134: LineSegment StartX=55.8 StartY=-18 StartZ=0 EndX=55.8 EndY=-20 EndZ=0
    g135: LineSegment StartX=55.8 StartY=-20 StartZ=0 EndX=56 EndY=-20 EndZ=0
    g136: LineSegment StartX=56 StartY=-20 StartZ=0 EndX=56 EndY=-18 EndZ=0
    g137: LineSegment StartX=54 StartY=-18 StartZ=0 EndX=53.8 EndY=-18 EndZ=0
    g138: LineSegment StartX=53.8 StartY=-18 StartZ=0 EndX=53.8 EndY=-20 EndZ=0
    g139: LineSegment StartX=53.8 StartY=-20 StartZ=0 EndX=54 EndY=-20 EndZ=0
    g140: LineSegment StartX=54 StartY=-20 StartZ=0 EndX=54 EndY=-18 EndZ=0
    g141: LineSegment StartX=51.8 StartY=-18 StartZ=0 EndX=52 EndY=-18 EndZ=0
    g142: LineSegment StartX=52 StartY=-18 StartZ=0 EndX=52 EndY=-20 EndZ=0
    g143: LineSegment StartX=52 StartY=-20 StartZ=0 EndX=51.8 EndY=-20 EndZ=0
    g144: LineSegment StartX=51.8 StartY=-20 StartZ=0 EndX=51.8 EndY=-18 EndZ=0
    g145: LineSegment StartX=48 StartY=-18 StartZ=0 EndX=47.8 EndY=-18 EndZ=0
    g146: LineSegment StartX=47.8 StartY=-18 StartZ=0 EndX=47.8 EndY=-20 EndZ=0
    g147: LineSegment StartX=47.8 StartY=-20 StartZ=0 EndX=48 EndY=-20 EndZ=0
    g148: LineSegment StartX=48 StartY=-20 StartZ=0 EndX=48 EndY=-18 EndZ=0
    g149: LineSegment StartX=46 StartY=-18 StartZ=0 EndX=45.8 EndY=-18 EndZ=0
    g150: LineSegment StartX=45.8 StartY=-18 StartZ=0 EndX=45.8 EndY=-20 EndZ=0
    g151: LineSegment StartX=45.8 StartY=-20 StartZ=0 EndX=46 EndY=-20 EndZ=0
    g152: LineSegment StartX=46 StartY=-20 StartZ=0 EndX=46 EndY=-18 EndZ=0
    g153: LineSegment StartX=44 StartY=-18 StartZ=0 EndX=43.8 EndY=-18 EndZ=0
    g154: LineSegment StartX=43.8 StartY=-18 StartZ=0 EndX=43.8 EndY=-20 EndZ=0
    g155: LineSegment StartX=43.8 StartY=-20 StartZ=0 EndX=44 EndY=-20 EndZ=0
    g156: LineSegment StartX=44 StartY=-20 StartZ=0 EndX=44 EndY=-18 EndZ=0
    g157: LineSegment StartX=41.8 StartY=-18 StartZ=0 EndX=42 EndY=-18 EndZ=0
    g158: LineSegment StartX=42 StartY=-18 StartZ=0 EndX=42 EndY=-20 EndZ=0
    g159: LineSegment StartX=42 StartY=-20 StartZ=0 EndX=41.8 EndY=-20 EndZ=0
    g160: LineSegment StartX=41.8 StartY=-20 StartZ=0 EndX=41.8 EndY=-18 EndZ=0
    g161: LineSegment StartX=38 StartY=-18 StartZ=0 EndX=37.8 EndY=-18 EndZ=0
    g162: LineSegment StartX=37.8 StartY=-18 StartZ=0 EndX=37.8 EndY=-20 EndZ=0
    g163: LineSegment StartX=37.8 StartY=-20 StartZ=0 EndX=38 EndY=-20 EndZ=0
    g164: LineSegment StartX=38 StartY=-20 StartZ=0 EndX=38 EndY=-18 EndZ=0
    g165: LineSegment StartX=36 StartY=-18 StartZ=0 EndX=35.8 EndY=-18 EndZ=0
    g166: LineSegment StartX=35.8 StartY=-18 StartZ=0 EndX=35.8 EndY=-20 EndZ=0
    g167: LineSegment StartX=35.8 StartY=-20 StartZ=0 EndX=36 EndY=-20 EndZ=0
    g168: LineSegment StartX=36 StartY=-20 StartZ=0 EndX=36 EndY=-18 EndZ=0
    g169: LineSegment StartX=34 StartY=-18 StartZ=0 EndX=33.8 EndY=-18 EndZ=0
    g170: LineSegment StartX=33.8 StartY=-18 StartZ=0 EndX=33.8 EndY=-20 EndZ=0
    g171: LineSegment StartX=33.8 StartY=-20 StartZ=0 EndX=34 EndY=-20 EndZ=0
    g172: LineSegment StartX=34 StartY=-20 StartZ=0 EndX=34 EndY=-18 EndZ=0
    g173: LineSegment StartX=31.8 StartY=-18 StartZ=0 EndX=32 EndY=-18 EndZ=0
    g174: LineSegment StartX=32 StartY=-18 StartZ=0 EndX=32 EndY=-20 EndZ=0
    g175: LineSegment StartX=32 StartY=-20 StartZ=0 EndX=31.8 EndY=-20 EndZ=0
    g176: LineSegment StartX=31.8 StartY=-20 StartZ=0 EndX=31.8 EndY=-18 EndZ=0
    g177: LineSegment StartX=27.8 StartY=-18 StartZ=0 EndX=28 EndY=-18 EndZ=0
    g178: LineSegment StartX=28 StartY=-18 StartZ=0 EndX=28 EndY=-20 EndZ=0
    g179: LineSegment StartX=28 StartY=-20 StartZ=0 EndX=27.8 EndY=-20 EndZ=0
    g180: LineSegment StartX=27.8 StartY=-20 StartZ=0 EndX=27.8 EndY=-18 EndZ=0
    g181: LineSegment StartX=26 StartY=-18 StartZ=0 EndX=25.8 EndY=-18 EndZ=0
    g182: LineSegment StartX=25.8 StartY=-18 StartZ=0 EndX=25.8 EndY=-20 EndZ=0
    g183: LineSegment StartX=25.8 StartY=-20 StartZ=0 EndX=26 EndY=-20 EndZ=0
    g184: LineSegment StartX=26 StartY=-20 StartZ=0 EndX=26 EndY=-18 EndZ=0
    g185: LineSegment StartX=24 StartY=-18 StartZ=0 EndX=23.8 EndY=-18 EndZ=0
    g186: LineSegment StartX=23.8 StartY=-18 StartZ=0 EndX=23.8 EndY=-20 EndZ=0
    g187: LineSegment StartX=23.8 StartY=-20 StartZ=0 EndX=24 EndY=-20 EndZ=0
    g188: LineSegment StartX=24 StartY=-20 StartZ=0 EndX=24 EndY=-18 EndZ=0
    g189: LineSegment StartX=21.8 StartY=-18 StartZ=0 EndX=22 EndY=-18 EndZ=0
    g190: LineSegment StartX=22 StartY=-18 StartZ=0 EndX=22 EndY=-20 EndZ=0
    g191: LineSegment StartX=22 StartY=-20 StartZ=0 EndX=21.8 EndY=-20 EndZ=0
    g192: LineSegment StartX=21.8 StartY=-20 StartZ=0 EndX=21.8 EndY=-18 EndZ=0
    g193: LineSegment StartX=18 StartY=-18 StartZ=0 EndX=17.8 EndY=-18 EndZ=0
    g194: LineSegment StartX=17.8 StartY=-18 StartZ=0 EndX=17.8 EndY=-20 EndZ=0
    g195: LineSegment StartX=17.8 StartY=-20 StartZ=0 EndX=18 EndY=-20 EndZ=0
    g196: LineSegment StartX=18 StartY=-20 StartZ=0 EndX=18 EndY=-18 EndZ=0
    g197: LineSegment StartX=16 StartY=-18 StartZ=0 EndX=15.8 EndY=-18 EndZ=0
    g198: LineSegment StartX=15.8 StartY=-18 StartZ=0 EndX=15.8 EndY=-20 EndZ=0
    g199: LineSegment StartX=15.8 StartY=-20 StartZ=0 EndX=16 EndY=-20 EndZ=0
    g200: LineSegment StartX=16 StartY=-20 StartZ=0 EndX=16 EndY=-18 EndZ=0
    g201: LineSegment StartX=14 StartY=-18 StartZ=0 EndX=13.8 EndY=-18 EndZ=0
    g202: LineSegment StartX=13.8 StartY=-18 StartZ=0 EndX=13.8 EndY=-20 EndZ=0
    g203: LineSegment StartX=13.8 StartY=-20 StartZ=0 EndX=14 EndY=-20 EndZ=0
    g204: LineSegment StartX=14 StartY=-20 StartZ=0 EndX=14 EndY=-18 EndZ=0
    g205: LineSegment StartX=11.8 StartY=-18 StartZ=0 EndX=12 EndY=-18 EndZ=0
    g206: LineSegment StartX=12 StartY=-18 StartZ=0 EndX=12 EndY=-20 EndZ=0
    g207: LineSegment StartX=12 StartY=-20 StartZ=0 EndX=11.8 EndY=-20 EndZ=0
    g208: LineSegment StartX=11.8 StartY=-20 StartZ=0 EndX=11.8 EndY=-18 EndZ=0
    g209: LineSegment StartX=7.8 StartY=-18 StartZ=0 EndX=8 EndY=-18 EndZ=0
    g210: LineSegment StartX=8 StartY=-18 StartZ=0 EndX=8 EndY=-20 EndZ=0
    g211: LineSegment StartX=8 StartY=-20 StartZ=0 EndX=7.8 EndY=-20 EndZ=0
    g212: LineSegment StartX=7.8 StartY=-20 StartZ=0 EndX=7.8 EndY=-18 EndZ=0
    g213: LineSegment StartX=6 StartY=-18 StartZ=0 EndX=5.8 EndY=-18 EndZ=0
    g214: LineSegment StartX=5.8 StartY=-18 StartZ=0 EndX=5.8 EndY=-20 EndZ=0
    g215: LineSegment StartX=5.8 StartY=-20 StartZ=0 EndX=6 EndY=-20 EndZ=0
    g216: LineSegment StartX=6 StartY=-20 StartZ=0 EndX=6 EndY=-18 EndZ=0
    g217: LineSegment StartX=4 StartY=-18 StartZ=0 EndX=3.8 EndY=-18 EndZ=0
    g218: LineSegment StartX=3.8 StartY=-18 StartZ=0 EndX=3.8 EndY=-20 EndZ=0
    g219: LineSegment StartX=3.8 StartY=-20 StartZ=0 EndX=4 EndY=-20 EndZ=0
    g220: LineSegment StartX=4 StartY=-20 StartZ=0 EndX=4 EndY=-18 EndZ=0
    g221: LineSegment StartX=1.8 StartY=-18 StartZ=0 EndX=2 EndY=-18 EndZ=0
    g222: LineSegment StartX=2 StartY=-18 StartZ=0 EndX=2 EndY=-20 EndZ=0
    g223: LineSegment StartX=2 StartY=-20 StartZ=0 EndX=1.8 EndY=-20 EndZ=0
    g224: LineSegment StartX=1.8 StartY=-20 StartZ=0 EndX=1.8 EndY=-18 EndZ=0
  constraints (676):
    c: Horizontal(g0)
    c: DistanceY(g0,g-1) = 20
    c: DistanceX(g0,g0) = 100
    c: DistanceX(g0,g-1) = 30
    c: Coincident(g1,g2)
    c: Coincident(g2,g3)
    c: Coincident(g3,g4)
    c: Coincident(g4,g1)
    c: Horizontal(g1)
    c: Horizontal(g3)
    c: Vertical(g2)
    c: Vertical(g4)
    c: PointOnObject(g1,g-1)
    c: DistanceY(g4,g4) = 2
    c: DistanceX(g3,g3) = 0.2
    c: Coincident(g5,g6)
    c: Coincident(g6,g7)
    c: Coincident(g7,g8)
    c: Coincident(g8,g5)
    c: Horizontal(g5)
    c: Horizontal(g7)
    c: Vertical(g6)
    c: Vertical(g8)
    c: Equal(g4,g8) = 2
    c: Equal(g3,g7) = 0.2
    c: Coincident(g9,g10)
    c: Coincident(g10,g11)
    c: Coincident(g11,g12)
    c: Coincident(g12,g9)
    c: Horizontal(g9)
    c: Horizontal(g11)
    c: Vertical(g10)
    c: Vertical(g12)
    c: Equal(g8,g12) = 2
    c: Equal(g7,g11) = 0.2
    c: DistanceX(g9,g5) = 2
    c: Coincident(g13,g14)
    c: Coincident(g14,g15)
    c: Coincident(g15,g16)
    c: Coincident(g16,g13)
    c: Horizontal(g13)
    c: Horizontal(g15)
    c: Vertical(g14)
    c: Vertical(g16)
    c: Equal(g11,g15)
    c: Equal(g10,g14)
    c: Horizontal(g1,g5)
    c: Horizontal(g5,g9)
    c: Horizontal(g9,g13)
    c: Coincident(g17,g18)
    c: Coincident(g18,g19)
    c: Coincident(g19,g20)
    c: Coincident(g20,g17)
    c: Horizontal(g17)
    c: Horizontal(g19)
    c: Vertical(g18)
    c: Vertical(g20)
    c: Equal(g4,g20) = 2
    c: Equal(g3,g19) = 0.2
    c: Coincident(g21,g22)
    c: Coincident(g22,g23)
    c: Coincident(g23,g24)
    c: Coincident(g24,g21)
    c: Horizontal(g21)
    c: Horizontal(g23)
    c: Vertical(g22)
    c: Vertical(g24)
    c: Equal(g20,g24) = 2
    c: Equal(g19,g23) = 0.2
    c: Coincident(g25,g26)
    c: Coincident(g26,g27)
    c: Coincident(g27,g28)
    c: Coincident(g28,g25)
    c: Horizontal(g25)
    c: Horizontal(g27)
    c: Vertical(g26)
    c: Vertical(g28)
    c: Equal(g24,g28) = 2
    c: Equal(g23,g27) = 0.2
    c: DistanceX(g25,g21) = 2
    c: Coincident(g29,g30)
    c: Coincident(g30,g31)
    c: Coincident(g31,g32)
    c: Coincident(g32,g29)
    c: Horizontal(g29)
    c: Horizontal(g31)
    c: Vertical(g30)
    c: Vertical(g32)
    c: Equal(g27,g31)
    c: Equal(g26,g30)
    c: Horizontal(g17,g21)
    c: Horizontal(g21,g25)
    c: Horizontal(g25,g29)
    c: PointOnObject(g17,g-1)
    c: Coincident(g33,g34)
    c: Coincident(g34,g35)
    c: Coincident(g35,g36)
    c: Coincident(g36,g33)
    c: Horizontal(g33)
    c: Horizontal(g35)
    c: Vertical(g34)
    c: Vertical(g36)
    c: Coincident(g37,g38)
    c: Coincident(g38,g39)
    c: Coincident(g39,g40)
    c: Coincident(g40,g37)
    c: Horizontal(g37)
    c: Horizontal(g39)
    c: Vertical(g38)
    c: Vertical(g40)
    c: Equal(g36,g40) = 2
    c: Equal(g35,g39) = 0.2
    c: Coincident(g41,g42)
    c: Coincident(g42,g43)
    c: Coincident(g43,g44)
    c: Coincident(g44,g41)
    c: Horizontal(g41)
    c: Horizontal(g43)
    c: Vertical(g42)
    c: Vertical(g44)
    c: Equal(g40,g44) = 2
    c: Equal(g39,g43) = 0.2
    c: DistanceX(g41,g37) = 2
    c: Coincident(g45,g46)
    c: Coincident(g46,g47)
    c: Coincident(g47,g48)
    c: Coincident(g48,g45)
    c: Horizontal(g45)
    c: Horizontal(g47)
    c: Vertical(g46)
    c: Vertical(g48)
    c: Equal(g43,g47)
    c: Equal(g42,g46)
    c: Horizontal(g33,g37)
    c: Horizontal(g37,g41)
    c: Horizontal(g41,g45)
    c: PointOnObject(g33,g-1)
    c: Coincident(g49,g50)
    c: Coincident(g50,g51)
    c: Coincident(g51,g52)
    c: Coincident(g52,g49)
    c: Horizontal(g49)
    c: Horizontal(g51)
    c: Vertical(g50)
    c: Vertical(g52)
    c: Equal(g4,g52) = 2
    c: Equal(g3,g51) = 0.2
    c: Coincident(g53,g54)
    c: Coincident(g54,g55)
    c: Coincident(g55,g56)
    c: Coincident(g56,g53)
    c: Horizontal(g53)
    c: Horizontal(g55)
    c: Vertical(g54)
    c: Vertical(g56)
    c: Equal(g52,g56) = 2
    c: Equal(g51,g55) = 0.2
    c: Coincident(g57,g58)
    c: Coincident(g58,g59)
    c: Coincident(g59,g60)
    c: Coincident(g60,g57)
    c: Horizontal(g57)
    c: Horizontal(g59)
    c: Vertical(g58)
    c: Vertical(g60)
    c: Equal(g56,g60) = 2
    c: Equal(g55,g59) = 0.2
    c: DistanceX(g57,g53) = 2
    c: Coincident(g61,g62)
    c: Coincident(g62,g63)
    c: Coincident(g63,g64)
    c: Coincident(g64,g61)
    c: Horizontal(g61)
    c: Horizontal(g63)
    c: Vertical(g62)
    c: Vertical(g64)
    c: Equal(g59,g63)
    c: Equal(g58,g62)
    c: Horizontal(g49,g53)
    c: Horizontal(g53,g57)
    c: Horizontal(g57,g61)
    c: Coincident(g65,g66)
    c: Coincident(g66,g67)
    c: Coincident(g67,g68)
    c: Coincident(g68,g65)
    c: Horizontal(g65)
    c: Horizontal(g67)
    c: Vertical(g66)
    c: Vertical(g68)
    c: Equal(g52,g68) = 2
    c: Equal(g51,g67) = 0.2
    c: Coincident(g69,g70)
    c: Coincident(g70,g71)
    c: Coincident(g71,g72)
    c: Coincident(g72,g69)
    c: Horizontal(g69)
    c: Horizontal(g71)
    c: Vertical(g70)
    c: Vertical(g72)
    c: Equal(g68,g72) = 2
    c: Equal(g67,g71) = 0.2
    c: Coincident(g73,g74)
    c: Coincident(g74,g75)
    c: Coincident(g75,g76)
    c: Coincident(g76,g73)
    c: Horizontal(g73)
    c: Horizontal(g75)
    c: Vertical(g74)
    c: Vertical(g76)
    c: Equal(g72,g76) = 2
    c: Equal(g71,g75) = 0.2
    c: DistanceX(g73,g69) = 2
    c: Coincident(g77,g78)
    c: Coincident(g78,g79)
    c: Coincident(g79,g80)
    c: Coincident(g80,g77)
    c: Horizontal(g77)
    c: Horizontal(g79)
    c: Vertical(g78)
    c: Vertical(g80)
    c: Equal(g75,g79)
    c: Equal(g74,g78)
    c: Horizontal(g65,g69)
    c: Horizontal(g69,g73)
    c: Horizontal(g73,g77)
    c: Coincident(g81,g82)
    c: Coincident(g82,g83)
    c: Coincident(g83,g84)
    c: Coincident(g84,g81)
    c: Horizontal(g81)
    c: Horizontal(g83)
    c: Vertical(g82)
    c: Vertical(g84)
    c: Coincident(g85,g86)
    c: Coincident(g86,g87)
    c: Coincident(g87,g88)
    c: Coincident(g88,g85)
    c: Horizontal(g85)
    c: Horizontal(g87)
    c: Vertical(g86)
    c: Vertical(g88)
    c: Equal(g84,g88) = 2
    c: Equal(g83,g87) = 0.2
    c: Coincident(g89,g90)
    c: Coincident(g90,g91)
    c: Coincident(g91,g92)
    c: Coincident(g92,g89)
    c: Horizontal(g89)
    c: Horizontal(g91)
    c: Vertical(g90)
    c: Vertical(g92)
    c: Equal(g88,g92) = 2
    c: Equal(g87,g91) = 0.2
    c: DistanceX(g89,g85) = 2
    c: Coincident(g93,g94)
    c: Coincident(g94,g95)
    c: Coincident(g95,g96)
    c: Coincident(g96,g93)
    c: Horizontal(g93)
    c: Horizontal(g95)
    c: Vertical(g94)
    c: Vertical(g96)
    c: Equal(g91,g95)
    c: Equal(g90,g94)
    c: Horizontal(g81,g85)
    c: Horizontal(g85,g89)
    c: Horizontal(g89,g93)
    c: PointOnObject(g49,g-1)
    c: PointOnObject(g65,g-1)
    c: DistanceX(g53,g49) = 2
    c: DistanceX(g69,g65) = 2
    c: PointOnObject(g81,g-1)
    c: DistanceX(g37,g33) = 2
    c: DistanceX(g21,g17) = 2
    c: DistanceX(g5,g1) = 2
    c: Coincident(g97,g98)
    c: Coincident(g98,g99)
    c: Coincident(g99,g100)
    c: Coincident(g100,g97)
    c: Horizontal(g97)
    c: Horizontal(g99)
    c: Vertical(g98)
    c: Vertical(g100)
    c: Equal(g4,g100) = 2
    c: Equal(g3,g99) = 0.2
    c: Coincident(g101,g102)
    c: Coincident(g102,g103)
    c: Coincident(g103,g104)
    c: Coincident(g104,g101)
    c: Horizontal(g101)
    c: Horizontal(g103)
    c: Vertical(g102)
    c: Vertical(g104)
    c: Equal(g100,g104) = 2
    c: Equal(g99,g103) = 0.2
    c: Coincident(g105,g106)
    c: Coincident(g106,g107)
    c: Coincident(g107,g108)
    c: Coincident(g108,g105)
    c: Horizontal(g105)
    c: Horizontal(g107)
    c: Vertical(g106)
    c: Vertical(g108)
    c: Equal(g104,g108) = 2
    c: Equal(g103,g107) = 0.2
    c: DistanceX(g105,g101) = 2
    c: Coincident(g109,g110)
    c: Coincident(g110,g111)
    c: Coincident(g111,g112)
    c: Coincident(g112,g109)
    c: Horizontal(g109)
    c: Horizontal(g111)
    c: Vertical(g110)
    c: Vertical(g112)
    c: Equal(g107,g111)
    c: Equal(g106,g110)
    c: Horizontal(g97,g101)
    c: Horizontal(g101,g105)
    c: Horizontal(g105,g109)
    c: DistanceX(g17,g13) = 4
    c: DistanceX(g13,g9) = 2
    c: DistanceX(g33,g29) = 4
    c: DistanceX(g49,g45) = 4
    c: DistanceX(g45,g41) = 2
    c: DistanceX(g61,g57) = 2
    c: DistanceX(g65,g61) = 4
    c: DistanceX(g77,g73) = 2
    c: DistanceX(g85,g81) = 2
    c: DistanceX(g81,g77) = 4
    c: DistanceX(g93,g89) = 2
    c: PointOnObject(g97,g-1)
    c: DistanceX(g97,g93) = 4
    c: DistanceX(g101,g97) = 2
    c: DistanceX(g109,g105) = 2
    c: DistanceX(g29,g25) = 2
    c: Equal(g31,g35)
    c: Equal(g30,g36)
    c: Equal(g79,g83)
    c: Equal(g78,g84)
    c: Coincident(g113,g114)
    c: Coincident(g114,g115)
    c: Coincident(g115,g116)
    c: Coincident(g116,g113)
    c: Horizontal(g113)
    c: Horizontal(g115)
    c: Vertical(g114)
    c: Vertical(g116)
    c: Equal(g4,g116) = 2
    c: Equal(g3,g115) = 0.2
    c: Coincident(g117,g118)
    c: Coincident(g118,g119)
    c: Coincident(g119,g120)
    c: Coincident(g120,g117)
    c: Horizontal(g117)
    c: Horizontal(g119)
    c: Vertical(g118)
    c: Vertical(g120)
    c: Equal(g116,g120) = 2
    c: Equal(g115,g119) = 0.2
    c: Coincident(g121,g122)
    c: Coincident(g122,g123)
    c: Coincident(g123,g124)
    c: Coincident(g124,g121)
    c: Horizontal(g121)
    c: Horizontal(g123)
    c: Vertical(g122)
    c: Vertical(g124)
    c: Equal(g120,g124) = 2
    c: Equal(g119,g123) = 0.2
    c: DistanceX(g121,g117) = 2
    c: Coincident(g125,g126)
    c: Coincident(g126,g127)
    c: Coincident(g127,g128)
    c: Coincident(g128,g125)
    c: Horizontal(g125)
    c: Horizontal(g127)
    c: Vertical(g126)
    c: Vertical(g128)
    c: Equal(g123,g127)
    c: Equal(g122,g126)
    c: Horizontal(g113,g117)
    c: Horizontal(g117,g121)
    c: Horizontal(g121,g125)
    c: Coincident(g129,g130)
    c: Coincident(g130,g131)
    c: Coincident(g131,g132)
    c: Coincident(g132,g129)
    c: Horizontal(g129)
    c: Horizontal(g131)
    c: Vertical(g130)
    c: Vertical(g132)
    c: Equal(g116,g132) = 2
    c: Equal(g115,g131) = 0.2
    c: Coincident(g133,g134)
    c: Coincident(g134,g135)
    c: Coincident(g135,g136)
    c: Coincident(g136,g133)
    c: Horizontal(g133)
    c: Horizontal(g135)
    c: Vertical(g134)
    c: Vertical(g136)
    c: Equal(g132,g136) = 2
    c: Equal(g131,g135) = 0.2
    c: Coincident(g137,g138)
    c: Coincident(g138,g139)
    c: Coincident(g139,g140)
    c: Coincident(g140,g137)
    c: Horizontal(g137)
    c: Horizontal(g139)
    c: Vertical(g138)
    c: Vertical(g140)
    c: Equal(g136,g140) = 2
    c: Equal(g135,g139) = 0.2
    c: DistanceX(g137,g133) = 2
    c: Coincident(g141,g142)
    c: Coincident(g142,g143)
    c: Coincident(g143,g144)
    c: Coincident(g144,g141)
    c: Horizontal(g141)
    c: Horizontal(g143)
    c: Vertical(g142)
    c: Vertical(g144)
    c: Equal(g139,g143)
    c: Equal(g138,g142)
    c: Horizontal(g129,g133)
    c: Horizontal(g133,g137)
    c: Horizontal(g137,g141)
    c: Coincident(g145,g146)
    c: Coincident(g146,g147)
    c: Coincident(g147,g148)
    c: Coincident(g148,g145)
    c: Horizontal(g145)
    c: Horizontal(g147)
    c: Vertical(g146)
    c: Vertical(g148)
    c: Coincident(g149,g150)
    c: Coincident(g150,g151)
    c: Coincident(g151,g152)
    c: Coincident(g152,g149)
    c: Horizontal(g149)
    c: Horizontal(g151)
    c: Vertical(g150)
    c: Vertical(g152)
    c: Equal(g148,g152) = 2
    c: Equal(g147,g151) = 0.2
    c: Coincident(g153,g154)
    c: Coincident(g154,g155)
    c: Coincident(g155,g156)
    c: Coincident(g156,g153)
    c: Horizontal(g153)
    c: Horizontal(g155)
    c: Vertical(g154)
    c: Vertical(g156)
    c: Equal(g152,g156) = 2
    c: Equal(g151,g155) = 0.2
    c: DistanceX(g153,g149) = 2
    c: Coincident(g157,g158)
    c: Coincident(g158,g159)
    c: Coincident(g159,g160)
    c: Coincident(g160,g157)
    c: Horizontal(g157)
    c: Horizontal(g159)
    c: Vertical(g158)
    c: Vertical(g160)
    c: Equal(g155,g159)
    c: Equal(g154,g158)
    c: Horizontal(g145,g149)
    c: Horizontal(g149,g153)
    c: Horizontal(g153,g157)
    c: Coincident(g161,g162)
    c: Coincident(g162,g163)
    c: Coincident(g163,g164)
    c: Coincident(g164,g161)
    c: Horizontal(g161)
    c: Horizontal(g163)
    c: Vertical(g162)
    c: Vertical(g164)
    c: Equal(g116,g164) = 2
    c: Equal(g115,g163) = 0.2
    c: Coincident(g165,g166)
    c: Coincident(g166,g167)
    c: Coincident(g167,g168)
    c: Coincident(g168,g165)
    c: Horizontal(g165)
    c: Horizontal(g167)
    c: Vertical(g166)
    c: Vertical(g168)
    c: Equal(g164,g168) = 2
    c: Equal(g163,g167) = 0.2
    c: Coincident(g169,g170)
    c: Coincident(g170,g171)
    c: Coincident(g171,g172)
    c: Coincident(g172,g169)
    c: Horizontal(g169)
    c: Horizontal(g171)
    c: Vertical(g170)
    c: Vertical(g172)
    c: Equal(g168,g172) = 2
    c: Equal(g167,g171) = 0.2
    c: DistanceX(g169,g165) = 2
    c: Coincident(g173,g174)
    c: Coincident(g174,g175)
    c: Coincident(g175,g176)
    c: Coincident(g176,g173)
    c: Horizontal(g173)
    c: Horizontal(g175)
    c: Vertical(g174)
    c: Vertical(g176)
    c: Equal(g171,g175)
    c: Equal(g170,g174)
    c: Horizontal(g161,g165)
    c: Horizontal(g165,g169)
    c: Horizontal(g169,g173)
    c: Coincident(g177,g178)
    c: Coincident(g178,g179)
    c: Coincident(g179,g180)
    c: Coincident(g180,g177)
    c: Horizontal(g177)
    c: Horizontal(g179)
    c: Vertical(g178)
    c: Vertical(g180)
    c: Equal(g164,g180) = 2
    c: Equal(g163,g179) = 0.2
    c: Coincident(g181,g182)
    c: Coincident(g182,g183)
    c: Coincident(g183,g184)
    c: Coincident(g184,g181)
    c: Horizontal(g181)
    c: Horizontal(g183)
    c: Vertical(g182)
    c: Vertical(g184)
    c: Equal(g180,g184) = 2
    c: Equal(g179,g183) = 0.2
    c: Coincident(g185,g186)
    c: Coincident(g186,g187)
    c: Coincident(g187,g188)
    c: Coincident(g188,g185)
    c: Horizontal(g185)
    c: Horizontal(g187)
    c: Vertical(g186)
    c: Vertical(g188)
    c: Equal(g184,g188) = 2
    c: Equal(g183,g187) = 0.2
    c: DistanceX(g185,g181) = 2
    c: Coincident(g189,g190)
    c: Coincident(g190,g191)
    c: Coincident(g191,g192)
    c: Coincident(g192,g189)
    c: Horizontal(g189)
    c: Horizontal(g191)
    c: Vertical(g190)
    c: Vertical(g192)
    c: Equal(g187,g191)
    c: Equal(g186,g190)
    c: Horizontal(g177,g181)
    c: Horizontal(g181,g185)
    c: Horizontal(g185,g189)
    c: Coincident(g193,g194)
    c: Coincident(g194,g195)
    c: Coincident(g195,g196)
    c: Coincident(g196,g193)
    c: Horizontal(g193)
    c: Horizontal(g195)
    c: Vertical(g194)
    c: Vertical(g196)
    c: Coincident(g197,g198)
    c: Coincident(g198,g199)
    c: Coincident(g199,g200)
    c: Coincident(g200,g197)
    c: Horizontal(g197)
    c: Horizontal(g199)
    c: Vertical(g198)
    c: Vertical(g200)
    c: Equal(g196,g200) = 2
    c: Equal(g195,g199) = 0.2
    c: Coincident(g201,g202)
    c: Coincident(g202,g203)
    c: Coincident(g203,g204)
    c: Coincident(g204,g201)
    c: Horizontal(g201)
    c: Horizontal(g203)
    c: Vertical(g202)
    c: Vertical(g204)
    c: Equal(g200,g204) = 2
    c: Equal(g199,g203) = 0.2
    c: DistanceX(g201,g197) = 2
    c: Coincident(g205,g206)
    c: Coincident(g206,g207)
    c: Coincident(g207,g208)
    c: Coincident(g208,g205)
    c: Horizontal(g205)
    c: Horizontal(g207)
    c: Vertical(g206)
    c: Vertical(g208)
    c: Equal(g203,g207)
    c: Equal(g202,g206)
    c: Horizontal(g193,g197)
    c: Horizontal(g197,g201)
    c: Horizontal(g201,g205)
    c: DistanceX(g165,g161) = 2
    c: DistanceX(g181,g177) = 2
    c: DistanceX(g149,g145) = 2
    c: DistanceX(g133,g129) = 2
    c: DistanceX(g117,g113) = 2
    c: Coincident(g209,g210)
    c: Coincident(g210,g211)
    c: Coincident(g211,g212)
    c: Coincident(g212,g209)
    c: Horizontal(g209)
    c: Horizontal(g211)
    c: Vertical(g210)
    c: Vertical(g212)
    c: Equal(g116,g212) = 2
    c: Equal(g115,g211) = 0.2
    c: Coincident(g213,g214)
    c: Coincident(g214,g215)
    c: Coincident(g215,g216)
    c: Coincident(g216,g213)
    c: Horizontal(g213)
    c: Horizontal(g215)
    c: Vertical(g214)
    c: Vertical(g216)
    c: Equal(g212,g216) = 2
    c: Equal(g211,g215) = 0.2
    c: Coincident(g217,g218)
    c: Coincident(g218,g219)
    c: Coincident(g219,g220)
    c: Coincident(g220,g217)
    c: Horizontal(g217)
    c: Horizontal(g219)
    c: Vertical(g218)
    c: Vertical(g220)
    c: Equal(g216,g220) = 2
    c: Equal(g215,g219) = 0.2
    c: DistanceX(g217,g213) = 2
    c: Coincident(g221,g222)
    c: Coincident(g222,g223)
    c: Coincident(g223,g224)
    c: Coincident(g224,g221)
    c: Horizontal(g221)
    c: Horizontal(g223)
    c: Vertical(g222)
    c: Vertical(g224)
    c: Equal(g219,g223)
    c: Equal(g218,g222)
    c: Horizontal(g209,g213)
    c: Horizontal(g213,g217)
    c: Horizontal(g217,g221)
    c: DistanceX(g129,g125) = 4
    c: DistanceX(g125,g121) = 2
    c: DistanceX(g145,g141) = 4
    c: DistanceX(g161,g157) = 4
    c: DistanceX(g157,g153) = 2
    c: DistanceX(g173,g169) = 2
    c: DistanceX(g177,g173) = 4
    c: DistanceX(g189,g185) = 2
    c: DistanceX(g197,g193) = 2
    c: DistanceX(g193,g189) = 4
    c: DistanceX(g205,g201) = 2
    c: DistanceX(g209,g205) = 4
    c: DistanceX(g213,g209) = 2
    c: DistanceX(g221,g217) = 2
    c: DistanceX(g141,g137) = 2
    c: Equal(g143,g147)
    c: Equal(g142,g148)
    c: Equal(g191,g195)
    c: Equal(g190,g196)
    c: PointOnObject(g223,g0)
    c: PointOnObject(g207,g0)
    c: PointOnObject(g191,g0)
    c: PointOnObject(g175,g0)
    c: PointOnObject(g159,g0)
    c: PointOnObject(g143,g0)
    c: PointOnObject(g127,g0)
    c: DistanceX(g-1,g111) = 1.8
    c: Vertical(g221,g111)
FEATURE [PartDesign::Pocket] Pocket012
  BaseFeature = -> Pocket011
  Length = 1
  Length2 = 100
  Profile = -> Sketch016
  Reversed = true
  Type = 0
FEATURE [PartDesign::Plane] DatumPlane002
  AttachmentOffset = pos=(0,0,3) rot=(0,0,1;0rad)
  Length = 108.784
  MapMode = 5
  Placement = pos=(0,0,3) rot=(0,0,1;0rad)
  ResizeMode = 0
  Support = -> [XY_Plane002]
  Width = 63.784
FEATURE [Sketcher::SketchObject] Sketch017  label="hz cm003"
  FullyConstrained = true
  MapMode = 5
  Placement = pos=(0,0,3) rot=(0,0,1;0rad)
  Support = -> [DatumPlane002]
  expr: Constraints[9] = Spreadsheet.reticleCmWidth
  expr: Constraints[8] = Spreadsheet.reticleCmHeight
  sketch-geometry (61):
    g0: LineSegment StartX=60.2 StartY=-20 StartZ=0 EndX=60 EndY=-20 EndZ=0
    g1: LineSegment StartX=60 StartY=-20 StartZ=0 EndX=60 EndY=-16 EndZ=0
    g2: LineSegment StartX=60 StartY=-16 StartZ=0 EndX=60.2 EndY=-16 EndZ=0
    g3: LineSegment StartX=60.2 StartY=-16 StartZ=0 EndX=60.2 EndY=-20 EndZ=0
    g4: LineSegment StartX=0 StartY=-20 StartZ=0 EndX=80 EndY=-20 EndZ=0
    g5: LineSegment StartX=50.2 StartY=-20 StartZ=0 EndX=50 EndY=-20 EndZ=0
    g6: LineSegment StartX=50 StartY=-20 StartZ=0 EndX=50 EndY=-16 EndZ=0
    g7: LineSegment StartX=50 StartY=-16 StartZ=0 EndX=50.2 EndY=-16 EndZ=0
    g8: LineSegment StartX=50.2 StartY=-16 StartZ=0 EndX=50.2 EndY=-20 EndZ=0
    g9: LineSegment StartX=60.2 StartY=-20 StartZ=0 EndX=50.2 EndY=-20 EndZ=0
    g10: LineSegment StartX=40.2 StartY=-20 StartZ=0 EndX=40 EndY=-20 EndZ=0
    g11: LineSegment StartX=40 StartY=-20 StartZ=0 EndX=40 EndY=-16 EndZ=0
    g12: LineSegment StartX=40 StartY=-16 StartZ=0 EndX=40.2 EndY=-16 EndZ=0
    g13: LineSegment StartX=40.2 StartY=-16 StartZ=0 EndX=40.2 EndY=-20 EndZ=0
    g14: LineSegment StartX=50.2 StartY=-20 StartZ=0 EndX=40.2 EndY=-20 EndZ=0
    g15: LineSegment StartX=30.2 StartY=-20 StartZ=0 EndX=30 EndY=-20 EndZ=0
    g16: LineSegment StartX=30 StartY=-20 StartZ=0 EndX=30 EndY=-16 EndZ=0
    g17: LineSegment StartX=30 StartY=-16 StartZ=0 EndX=30.2 EndY=-16 EndZ=0
    g18: LineSegment StartX=30.2 StartY=-16 StartZ=0 EndX=30.2 EndY=-20 EndZ=0
    g19: LineSegment StartX=40.2 StartY=-20 StartZ=0 EndX=30.2 EndY=-20 EndZ=0
    g20: LineSegment StartX=20.2 StartY=-20 StartZ=0 EndX=20 EndY=-20 EndZ=0
    g21: LineSegment StartX=20 StartY=-20 StartZ=0 EndX=20 EndY=-16 EndZ=0
    g22: LineSegment StartX=20 StartY=-16 StartZ=0 EndX=20.2 EndY=-16 EndZ=0
    g23: LineSegment StartX=20.2 StartY=-16 StartZ=0 EndX=20.2 EndY=-20 EndZ=0
    g24: LineSegment StartX=30.2 StartY=-20 StartZ=0 EndX=20.2 EndY=-20 EndZ=0
    g25: LineSegment StartX=10.2 StartY=-20 StartZ=0 EndX=10 EndY=-20 EndZ=0
    g26: LineSegment StartX=10 StartY=-20 StartZ=0 EndX=10 EndY=-16 EndZ=0
    g27: LineSegment StartX=10 StartY=-16 StartZ=0 EndX=10.2 EndY=-16 EndZ=0
    g28: LineSegment StartX=10.2 StartY=-16 StartZ=0 EndX=10.2 EndY=-20 EndZ=0
    g29: LineSegment StartX=20.2 StartY=-20 StartZ=0 EndX=10.2 EndY=-20 EndZ=0
    g30: LineSegment StartX=10.2 StartY=-20 StartZ=0 EndX=0.2 EndY=-20 EndZ=0
    g31: LineSegment StartX=60 StartY=-4 StartZ=0 EndX=60.2 EndY=-4 EndZ=0
    g32: LineSegment StartX=60.2 StartY=-4 StartZ=0 EndX=60.2 EndY=0 EndZ=0
    g33: LineSegment StartX=60.2 StartY=0 StartZ=0 EndX=60 EndY=0 EndZ=0
    g34: LineSegment StartX=60 StartY=0 StartZ=0 EndX=60 EndY=-4 EndZ=0
    g35: LineSegment StartX=50 StartY=-4 StartZ=0 EndX=49.8 EndY=-4 EndZ=0
    g36: LineSegment StartX=49.8 StartY=-4 StartZ=0 EndX=49.8 EndY=1.8e-15 EndZ=0
    g37: LineSegment StartX=49.8 StartY=1.8e-15 StartZ=0 EndX=50 EndY=1.8e-15 EndZ=0
    g38: LineSegment StartX=50 StartY=1.8e-15 StartZ=0 EndX=50 EndY=-4 EndZ=0
    g39: LineSegment StartX=60 StartY=-4 StartZ=0 EndX=50 EndY=-4 EndZ=0
    g40: LineSegment StartX=40 StartY=-4 StartZ=0 EndX=39.8 EndY=-4 EndZ=0
    g41: LineSegment StartX=39.8 StartY=-4 StartZ=0 EndX=39.8 EndY=1.8e-15 EndZ=0
    g42: LineSegment StartX=39.8 StartY=1.8e-15 StartZ=0 EndX=40 EndY=1.8e-15 EndZ=0
    g43: LineSegment StartX=40 StartY=1.8e-15 StartZ=0 EndX=40 EndY=-4 EndZ=0
    g44: LineSegment StartX=50 StartY=-4 StartZ=0 EndX=40 EndY=-4 EndZ=0
    g45: LineSegment StartX=30 StartY=-4 StartZ=0 EndX=29.8 EndY=-4 EndZ=0
    g46: LineSegment StartX=29.8 StartY=-4 StartZ=0 EndX=29.8 EndY=3.6e-15 EndZ=0
    g47: LineSegment StartX=29.8 StartY=3.9e-15 StartZ=0 EndX=30 EndY=3.9e-15 EndZ=0
    g48: LineSegment StartX=30 StartY=3.9e-15 StartZ=0 EndX=30 EndY=-4 EndZ=0
    g49: LineSegment StartX=40 StartY=-4 StartZ=0 EndX=30 EndY=-4 EndZ=0
    g50: LineSegment StartX=20 StartY=-4 StartZ=0 EndX=19.8 EndY=-4 EndZ=0
    g51: LineSegment StartX=19.8 StartY=-4 StartZ=0 EndX=19.8 EndY=4.4e-15 EndZ=0
    g52: LineSegment StartX=19.8 StartY=4.5e-15 StartZ=0 EndX=20 EndY=4.5e-15 EndZ=0
    g53: LineSegment StartX=20 StartY=4.5e-15 StartZ=0 EndX=20 EndY=-4 EndZ=0
    g54: LineSegment StartX=30 StartY=-4 StartZ=0 EndX=20 EndY=-4 EndZ=0
    g55: LineSegment StartX=10 StartY=-4 StartZ=0 EndX=9.8 EndY=-4 EndZ=0
    g56: LineSegment StartX=9.8 StartY=-4 StartZ=0 EndX=9.8 EndY=-3.206e-13 EndZ=0
    g57: LineSegment StartX=9.8 StartY=-3.206e-13 StartZ=0 EndX=10 EndY=-3.206e-13 EndZ=0
    g58: LineSegment StartX=10 StartY=-3.206e-13 StartZ=0 EndX=10 EndY=-4 EndZ=0
    g59: LineSegment StartX=20 StartY=-4 StartZ=0 EndX=10 EndY=-4 EndZ=0
    g60: LineSegment StartX=10 StartY=-4 StartZ=0 EndX=0 EndY=-4 EndZ=0
  constraints (174):
    c: Coincident(g0,g1)
    c: Coincident(g1,g2)
    c: Coincident(g2,g3)
    c: Coincident(g3,g0)
    c: Horizontal(g0)
    c: Horizontal(g2)
    c: Vertical(g1)
    c: Vertical(g3)
    c: DistanceY(g3,g3) = 4
    c: DistanceX(g2,g2) = 0.2
    c: Horizontal(g4)
    c: DistanceY(g4,g-1) = 20
    c: PointOnObject(g0,g4)
    c: Coincident(g5,g6)
    c: Coincident(g6,g7)
    c: Coincident(g7,g8)
    c: Coincident(g8,g5)
    c: Horizontal(g5)
    c: Horizontal(g7)
    c: Vertical(g6)
    c: Vertical(g8)
    c: Equal(g3,g8) = 4
    c: Equal(g2,g7) = 0.35
    c: Coincident(g0,g9)
    c: Coincident(g5,g9)
    c: Distance(g9) = 10
    c: Angle(g9) = 3.14159
    c: Coincident(g10,g11)
    c: Coincident(g11,g12)
    c: Coincident(g12,g13)
    c: Coincident(g13,g10)
    c: Horizontal(g10)
    c: Horizontal(g12)
    c: Vertical(g11)
    c: Vertical(g13)
    c: Equal(g3,g13) = 4
    c: Equal(g2,g12) = 0.35
    c: Coincident(g5,g14)
    c: Coincident(g10,g14)
    c: Equal(g9,g14)
    c: Parallel(g14,g9)
    c: Coincident(g15,g16)
    c: Coincident(g16,g17)
    c: Coincident(g17,g18)
    c: Coincident(g18,g15)
    c: Horizontal(g15)
    c: Horizontal(g17)
    c: Vertical(g16)
    c: Vertical(g18)
    c: Equal(g3,g18) = 4
    c: Equal(g2,g17) = 0.35
    c: Coincident(g10,g19)
    c: Coincident(g15,g19)
    c: Equal(g9,g19)
    c: Parallel(g19,g9)
    c: Coincident(g20,g21)
    c: Coincident(g21,g22)
    c: Coincident(g22,g23)
    c: Coincident(g23,g20)
    c: Horizontal(g20)
    c: Horizontal(g22)
    c: Vertical(g21)
    c: Vertical(g23)
    c: Equal(g3,g23) = 4
    c: Equal(g2,g22) = 0.35
    c: Coincident(g15,g24)
    c: Coincident(g20,g24)
    c: Equal(g9,g24)
    c: Parallel(g24,g9)
    c: Coincident(g25,g26)
    c: Coincident(g26,g27)
    c: Coincident(g27,g28)
    c: Coincident(g28,g25)
    c: Horizontal(g25)
    c: Horizontal(g27)
    c: Vertical(g26)
    c: Vertical(g28)
    c: Equal(g3,g28) = 4
    c: Equal(g2,g27) = 0.35
    c: Coincident(g20,g29)
    c: Coincident(g25,g29)
    c: Equal(g9,g29)
    c: Parallel(g29,g9)
    c: Coincident(g25,g30)
    c: Equal(g9,g30)
    c: Parallel(g30,g9)
    c: Coincident(g31,g32)
    c: Coincident(g32,g33)
    c: Coincident(g33,g34)
    c: Coincident(g34,g31)
    c: Horizontal(g31)
    c: Horizontal(g33)
    c: Vertical(g32)
    c: Vertical(g34)
    c: Equal(g3,g34) = 4
    c: Equal(g2,g33) = 0.35
    c: Coincident(g35,g36)
    c: Coincident(g36,g37)
    c: Coincident(g37,g38)
    c: Coincident(g38,g35)
    c: Horizontal(g35)
    c: Horizontal(g37)
    c: Vertical(g36)
    c: Vertical(g38)
    c: Equal(g3,g38) = 4
    c: Equal(g2,g37) = 0.35
    c: Coincident(g31,g39)
    c: Coincident(g35,g39)
    c: Equal(g9,g39)
    c: Parallel(g39,g9)
    c: Coincident(g40,g41)
    c: Coincident(g41,g42)
    c: Coincident(g42,g43)
    c: Coincident(g43,g40)
    c: Horizontal(g40)
    c: Horizontal(g42)
    c: Vertical(g41)
    c: Vertical(g43)
    c: Equal(g3,g43) = 4
    c: Equal(g2,g42) = 0.35
    c: Coincident(g35,g44)
    c: Coincident(g40,g44)
    c: Equal(g9,g44)
    c: Parallel(g44,g9)
    c: Coincident(g45,g46)
    c: Coincident(g46,g47)
    c: Coincident(g47,g48)
    c: Coincident(g48,g45)
    c: Horizontal(g45)
    c: Horizontal(g47)
    c: Vertical(g46)
    c: Vertical(g48)
    c: Equal(g3,g48) = 4
    c: Equal(g2,g47) = 0.35
    c: Coincident(g40,g49)
    c: Coincident(g45,g49)
    c: Equal(g9,g49)
    c: Parallel(g49,g9)
    c: Coincident(g50,g51)
    c: Coincident(g51,g52)
    c: Coincident(g52,g53)
    c: Coincident(g53,g50)
    c: Horizontal(g50)
    c: Horizontal(g52)
    c: Vertical(g51)
    c: Vertical(g53)
    c: Equal(g3,g53) = 4
    c: Equal(g2,g52) = 0.35
    c: Coincident(g45,g54)
    c: Coincident(g50,g54)
    c: Equal(g9,g54)
    c: Parallel(g54,g9)
    c: Coincident(g55,g56)
    c: Coincident(g56,g57)
    c: Coincident(g57,g58)
    c: Coincident(g58,g55)
    c: Horizontal(g55)
    c: Horizontal(g57)
    c: Vertical(g56)
    c: Vertical(g58)
    c: Equal(g3,g58) = 4
    c: Equal(g2,g57) = 0.35
    c: Coincident(g50,g59)
    c: Coincident(g55,g59)
    c: Equal(g9,g59)
    c: Parallel(g59,g9)
    c: Coincident(g55,g60)
    c: Equal(g9,g60)
    c: Parallel(g60,g9)
    c: DistanceY(g-1,g32) = 0
    c: Vertical(g31,g2)
    c: DistanceX(g-1,g56) = 9.8
    c: DistanceX(g4,g4) = 80
    c: PointOnObject(g4,g-2)
FEATURE [PartDesign::Pocket] Pocket013
  BaseFeature = -> Pocket012
  Length = 1
  Length2 = 100
  Profile = -> Sketch017
  Type = 0
FEATURE [Sketcher::SketchObject] Sketch018  label="hz mm003"
  FullyConstrained = true
  MapMode = 5
  Placement = pos=(0,0,3) rot=(0,0,1;0rad)
  Support = -> [DatumPlane002]
  expr: Constraints[13] = Spreadsheet.reticleCmHeight / 2
  expr: Constraints[14] = Spreadsheet.reticleCmWidth
  sketch-geometry (225):
    g0: LineSegment StartX=-30 StartY=-20 StartZ=0 EndX=70 EndY=-20 EndZ=0
    g1: LineSegment StartX=68 StartY=0 StartZ=0 EndX=67.8 EndY=0 EndZ=0
    g2: LineSegment StartX=67.8 StartY=0 StartZ=0 EndX=67.8 EndY=-2 EndZ=0
    g3: LineSegment StartX=67.8 StartY=-2 StartZ=0 EndX=68 EndY=-2 EndZ=0
    g4: LineSegment StartX=68 StartY=-2 StartZ=0 EndX=68 EndY=0 EndZ=0
    g5: LineSegment StartX=66 StartY=0 StartZ=0 EndX=65.8 EndY=0 EndZ=0
    g6: LineSegment StartX=65.8 StartY=0 StartZ=0 EndX=65.8 EndY=-2 EndZ=0
    g7: LineSegment StartX=65.8 StartY=-2 StartZ=0 EndX=66 EndY=-2 EndZ=0
    g8: LineSegment StartX=66 StartY=-2 StartZ=0 EndX=66 EndY=0 EndZ=0
    g9: LineSegment StartX=64 StartY=0 StartZ=0 EndX=63.8 EndY=0 EndZ=0
    g10: LineSegment StartX=63.8 StartY=0 StartZ=0 EndX=63.8 EndY=-2 EndZ=0
    g11: LineSegment StartX=63.8 StartY=-2 StartZ=0 EndX=64 EndY=-2 EndZ=0
    g12: LineSegment StartX=64 StartY=-2 StartZ=0 EndX=64 EndY=0 EndZ=0
    g13: LineSegment StartX=61.8 StartY=0 StartZ=0 EndX=62 EndY=0 EndZ=0
    g14: LineSegment StartX=62 StartY=0 StartZ=0 EndX=62 EndY=-2 EndZ=0
    g15: LineSegment StartX=62 StartY=-2 StartZ=0 EndX=61.8 EndY=-2 EndZ=0
    g16: LineSegment StartX=61.8 StartY=-2 StartZ=0 EndX=61.8 EndY=0 EndZ=0
    g17: LineSegment StartX=57.8 StartY=0 StartZ=0 EndX=58 EndY=0 EndZ=0
    g18: LineSegment StartX=58 StartY=0 StartZ=0 EndX=58 EndY=-2 EndZ=0
    g19: LineSegment StartX=58 StartY=-2 StartZ=0 EndX=57.8 EndY=-2 EndZ=0
    g20: LineSegment StartX=57.8 StartY=-2 StartZ=0 EndX=57.8 EndY=0 EndZ=0
    g21: LineSegment StartX=56 StartY=0 StartZ=0 EndX=55.8 EndY=0 EndZ=0
    g22: LineSegment StartX=55.8 StartY=0 StartZ=0 EndX=55.8 EndY=-2 EndZ=0
    g23: LineSegment StartX=55.8 StartY=-2 StartZ=0 EndX=56 EndY=-2 EndZ=0
    g24: LineSegment StartX=56 StartY=-2 StartZ=0 EndX=56 EndY=0 EndZ=0
    g25: LineSegment StartX=54 StartY=0 StartZ=0 EndX=53.8 EndY=0 EndZ=0
    g26: LineSegment StartX=53.8 StartY=0 StartZ=0 EndX=53.8 EndY=-2 EndZ=0
    g27: LineSegment StartX=53.8 StartY=-2 StartZ=0 EndX=54 EndY=-2 EndZ=0
    g28: LineSegment StartX=54 StartY=-2 StartZ=0 EndX=54 EndY=0 EndZ=0
    g29: LineSegment StartX=51.8 StartY=0 StartZ=0 EndX=52 EndY=0 EndZ=0
    g30: LineSegment StartX=52 StartY=0 StartZ=0 EndX=52 EndY=-2 EndZ=0
    g31: LineSegment StartX=52 StartY=-2 StartZ=0 EndX=51.8 EndY=-2 EndZ=0
    g32: LineSegment StartX=51.8 StartY=-2 StartZ=0 EndX=51.8 EndY=0 EndZ=0
    g33: LineSegment StartX=48 StartY=0 StartZ=0 EndX=47.8 EndY=0 EndZ=0
    g34: LineSegment StartX=47.8 StartY=0 StartZ=0 EndX=47.8 EndY=-2 EndZ=0
    g35: LineSegment StartX=47.8 StartY=-2 StartZ=0 EndX=48 EndY=-2 EndZ=0
    g36: LineSegment StartX=48 StartY=-2 StartZ=0 EndX=48 EndY=0 EndZ=0
    g37: LineSegment StartX=46 StartY=0 StartZ=0 EndX=45.8 EndY=0 EndZ=0
    g38: LineSegment StartX=45.8 StartY=0 StartZ=0 EndX=45.8 EndY=-2 EndZ=0
    g39: LineSegment StartX=45.8 StartY=-2 StartZ=0 EndX=46 EndY=-2 EndZ=0
    g40: LineSegment StartX=46 StartY=-2 StartZ=0 EndX=46 EndY=0 EndZ=0
    g41: LineSegment StartX=44 StartY=0 StartZ=0 EndX=43.8 EndY=0 EndZ=0
    g42: LineSegment StartX=43.8 StartY=0 StartZ=0 EndX=43.8 EndY=-2 EndZ=0
    g43: LineSegment StartX=43.8 StartY=-2 StartZ=0 EndX=44 EndY=-2 EndZ=0
    g44: LineSegment StartX=44 StartY=-2 StartZ=0 EndX=44 EndY=0 EndZ=0
    g45: LineSegment StartX=41.8 StartY=0 StartZ=0 EndX=42 EndY=0 EndZ=0
    g46: LineSegment StartX=42 StartY=0 StartZ=0 EndX=42 EndY=-2 EndZ=0
    g47: LineSegment StartX=42 StartY=-2 StartZ=0 EndX=41.8 EndY=-2 EndZ=0
    g48: LineSegment StartX=41.8 StartY=-2 StartZ=0 EndX=41.8 EndY=0 EndZ=0
    g49: LineSegment StartX=38 StartY=0 StartZ=0 EndX=37.8 EndY=0 EndZ=0
    g50: LineSegment StartX=37.8 StartY=0 StartZ=0 EndX=37.8 EndY=-2 EndZ=0
    g51: LineSegment StartX=37.8 StartY=-2 StartZ=0 EndX=38 EndY=-2 EndZ=0
    g52: LineSegment StartX=38 StartY=-2 StartZ=0 EndX=38 EndY=0 EndZ=0
    g53: LineSegment StartX=36 StartY=0 StartZ=0 EndX=35.8 EndY=0 EndZ=0
    g54: LineSegment StartX=35.8 StartY=0 StartZ=0 EndX=35.8 EndY=-2 EndZ=0
    g55: LineSegment StartX=35.8 StartY=-2 StartZ=0 EndX=36 EndY=-2 EndZ=0
    g56: LineSegment StartX=36 StartY=-2 StartZ=0 EndX=36 EndY=0 EndZ=0
    g57: LineSegment StartX=34 StartY=0 StartZ=0 EndX=33.8 EndY=0 EndZ=0
    g58: LineSegment StartX=33.8 StartY=0 StartZ=0 EndX=33.8 EndY=-2 EndZ=0
    g59: LineSegment StartX=33.8 StartY=-2 StartZ=0 EndX=34 EndY=-2 EndZ=0
    g60: LineSegment StartX=34 StartY=-2 StartZ=0 EndX=34 EndY=0 EndZ=0
    g61: LineSegment StartX=31.8 StartY=0 StartZ=0 EndX=32 EndY=0 EndZ=0
    g62: LineSegment StartX=32 StartY=0 StartZ=0 EndX=32 EndY=-2 EndZ=0
    g63: LineSegment StartX=32 StartY=-2 StartZ=0 EndX=31.8 EndY=-2 EndZ=0
    g64: LineSegment StartX=31.8 StartY=-2 StartZ=0 EndX=31.8 EndY=0 EndZ=0
    g65: LineSegment StartX=27.8 StartY=0 StartZ=0 EndX=28 EndY=0 EndZ=0
    g66: LineSegment StartX=28 StartY=0 StartZ=0 EndX=28 EndY=-2 EndZ=0
    g67: LineSegment StartX=28 StartY=-2 StartZ=0 EndX=27.8 EndY=-2 EndZ=0
    g68: LineSegment StartX=27.8 StartY=-2 StartZ=0 EndX=27.8 EndY=0 EndZ=0
    g69: LineSegment StartX=26 StartY=0 StartZ=0 EndX=25.8 EndY=0 EndZ=0
    g70: LineSegment StartX=25.8 StartY=0 StartZ=0 EndX=25.8 EndY=-2 EndZ=0
    g71: LineSegment StartX=25.8 StartY=-2 StartZ=0 EndX=26 EndY=-2 EndZ=0
    g72: LineSegment StartX=26 StartY=-2 StartZ=0 EndX=26 EndY=0 EndZ=0
    g73: LineSegment StartX=24 StartY=0 StartZ=0 EndX=23.8 EndY=0 EndZ=0
    g74: LineSegment StartX=23.8 StartY=0 StartZ=0 EndX=23.8 EndY=-2 EndZ=0
    g75: LineSegment StartX=23.8 StartY=-2 StartZ=0 EndX=24 EndY=-2 EndZ=0
    g76: LineSegment StartX=24 StartY=-2 StartZ=0 EndX=24 EndY=0 EndZ=0
    g77: LineSegment StartX=21.8 StartY=0 StartZ=0 EndX=22 EndY=0 EndZ=0
    g78: LineSegment StartX=22 StartY=0 StartZ=0 EndX=22 EndY=-2 EndZ=0
    g79: LineSegment StartX=22 StartY=-2 StartZ=0 EndX=21.8 EndY=-2 EndZ=0
    g80: LineSegment StartX=21.8 StartY=-2 StartZ=0 EndX=21.8 EndY=0 EndZ=0
    g81: LineSegment StartX=18 StartY=0 StartZ=0 EndX=17.8 EndY=0 EndZ=0
    g82: LineSegment StartX=17.8 StartY=0 StartZ=0 EndX=17.8 EndY=-2 EndZ=0
    g83: LineSegment StartX=17.8 StartY=-2 StartZ=0 EndX=18 EndY=-2 EndZ=0
    g84: LineSegment StartX=18 StartY=-2 StartZ=0 EndX=18 EndY=0 EndZ=0
    g85: LineSegment StartX=16 StartY=0 StartZ=0 EndX=15.8 EndY=0 EndZ=0
    g86: LineSegment StartX=15.8 StartY=0 StartZ=0 EndX=15.8 EndY=-2 EndZ=0
    g87: LineSegment StartX=15.8 StartY=-2 StartZ=0 EndX=16 EndY=-2 EndZ=0
    g88: LineSegment StartX=16 StartY=-2 StartZ=0 EndX=16 EndY=0 EndZ=0
    g89: LineSegment StartX=14 StartY=0 StartZ=0 EndX=13.8 EndY=0 EndZ=0
    g90: LineSegment StartX=13.8 StartY=0 StartZ=0 EndX=13.8 EndY=-2 EndZ=0
    g91: LineSegment StartX=13.8 StartY=-2 StartZ=0 EndX=14 EndY=-2 EndZ=0
    g92: LineSegment StartX=14 StartY=-2 StartZ=0 EndX=14 EndY=0 EndZ=0
    g93: LineSegment StartX=11.8 StartY=0 StartZ=0 EndX=12 EndY=0 EndZ=0
    g94: LineSegment StartX=12 StartY=0 StartZ=0 EndX=12 EndY=-2 EndZ=0
    g95: LineSegment StartX=12 StartY=-2 StartZ=0 EndX=11.8 EndY=-2 EndZ=0
    g96: LineSegment StartX=11.8 StartY=-2 StartZ=0 EndX=11.8 EndY=0 EndZ=0
    g97: LineSegment StartX=7.8 StartY=0 StartZ=0 EndX=8 EndY=0 EndZ=0
    g98: LineSegment StartX=8 StartY=0 StartZ=0 EndX=8 EndY=-2 EndZ=0
    g99: LineSegment StartX=8 StartY=-2 StartZ=0 EndX=7.8 EndY=-2 EndZ=0
    g100: LineSegment StartX=7.8 StartY=-2 StartZ=0 EndX=7.8 EndY=0 EndZ=0
    g101: LineSegment StartX=6 StartY=0 StartZ=0 EndX=5.8 EndY=0 EndZ=0
    g102: LineSegment StartX=5.8 StartY=0 StartZ=0 EndX=5.8 EndY=-2 EndZ=0
    g103: LineSegment StartX=5.8 StartY=-2 StartZ=0 EndX=6 EndY=-2 EndZ=0
    g104: LineSegment StartX=6 StartY=-2 StartZ=0 EndX=6 EndY=0 EndZ=0
    g105: LineSegment StartX=4 StartY=0 StartZ=0 EndX=3.8 EndY=0 EndZ=0
    g106: LineSegment StartX=3.8 StartY=0 StartZ=0 EndX=3.8 EndY=-2 EndZ=0
    g107: LineSegment StartX=3.8 StartY=-2 StartZ=0 EndX=4 EndY=-2 EndZ=0
    g108: LineSegment StartX=4 StartY=-2 StartZ=0 EndX=4 EndY=0 EndZ=0
    g109: LineSegment StartX=1.8 StartY=0 StartZ=0 EndX=2 EndY=0 EndZ=0
    g110: LineSegment StartX=2 StartY=0 StartZ=0 EndX=2 EndY=-2 EndZ=0
    g111: LineSegment StartX=2 StartY=-2 StartZ=0 EndX=1.8 EndY=-2 EndZ=0
    g112: LineSegment StartX=1.8 StartY=-2 StartZ=0 EndX=1.8 EndY=0 EndZ=0
    g113: LineSegment StartX=68 StartY=-18 StartZ=0 EndX=67.8 EndY=-18 EndZ=0
    g114: LineSegment StartX=67.8 StartY=-18 StartZ=0 EndX=67.8 EndY=-20 EndZ=0
    g115: LineSegment StartX=67.8 StartY=-20 StartZ=0 EndX=68 EndY=-20 EndZ=0
    g116: LineSegment StartX=68 StartY=-20 StartZ=0 EndX=68 EndY=-18 EndZ=0
    g117: LineSegment StartX=66 StartY=-18 StartZ=0 EndX=65.8 EndY=-18 EndZ=0
    g118: LineSegment StartX=65.8 StartY=-18 StartZ=0 EndX=65.8 EndY=-20 EndZ=0
    g119: LineSegment StartX=65.8 StartY=-20 StartZ=0 EndX=66 EndY=-20 EndZ=0
    g120: LineSegment StartX=66 StartY=-20 StartZ=0 EndX=66 EndY=-18 EndZ=0
    g121: LineSegment StartX=64 StartY=-18 StartZ=0 EndX=63.8 EndY=-18 EndZ=0
    g122: LineSegment StartX=63.8 StartY=-18 StartZ=0 EndX=63.8 EndY=-20 EndZ=0
    g123: LineSegment StartX=63.8 StartY=-20 StartZ=0 EndX=64 EndY=-20 EndZ=0
    g124: LineSegment StartX=64 StartY=-20 StartZ=0 EndX=64 EndY=-18 EndZ=0
    g125: LineSegment StartX=61.8 StartY=-18 StartZ=0 EndX=62 EndY=-18 EndZ=0
    g126: LineSegment StartX=62 StartY=-18 StartZ=0 EndX=62 EndY=-20 EndZ=0
    g127: LineSegment StartX=62 StartY=-20 StartZ=0 EndX=61.8 EndY=-20 EndZ=0
    g128: LineSegment StartX=61.8 StartY=-20 StartZ=0 EndX=61.8 EndY=-18 EndZ=0
    g129: LineSegment StartX=57.8 StartY=-18 StartZ=0 EndX=58 EndY=-18 EndZ=0
    g130: LineSegment StartX=58 StartY=-18 StartZ=0 EndX=58 EndY=-20 EndZ=0
    g131: LineSegment StartX=58 StartY=-20 StartZ=0 EndX=57.8 EndY=-20 EndZ=0
    g132: LineSegment StartX=57.8 StartY=-20 StartZ=0 EndX=57.8 EndY=-18 EndZ=0
    g133: LineSegment StartX=56 StartY=-18 StartZ=0 EndX=55.8 EndY=-18 EndZ=0
    g134: LineSegment StartX=55.8 StartY=-18 StartZ=0 EndX=55.8 EndY=-20 EndZ=0
    g135: LineSegment StartX=55.8 StartY=-20 StartZ=0 EndX=56 EndY=-20 EndZ=0
    g136: LineSegment StartX=56 StartY=-20 StartZ=0 EndX=56 EndY=-18 EndZ=0
    g137: LineSegment StartX=54 StartY=-18 StartZ=0 EndX=53.8 EndY=-18 EndZ=0
    g138: LineSegment StartX=53.8 StartY=-18 StartZ=0 EndX=53.8 EndY=-20 EndZ=0
    g139: LineSegment StartX=53.8 StartY=-20 StartZ=0 EndX=54 EndY=-20 EndZ=0
    g140: LineSegment StartX=54 StartY=-20 StartZ=0 EndX=54 EndY=-18 EndZ=0
    g141: LineSegment StartX=51.8 StartY=-18 StartZ=0 EndX=52 EndY=-18 EndZ=0
    g142: LineSegment StartX=52 StartY=-18 StartZ=0 EndX=52 EndY=-20 EndZ=0
    g143: LineSegment StartX=52 StartY=-20 StartZ=0 EndX=51.8 EndY=-20 EndZ=0
    g144: LineSegment StartX=51.8 StartY=-20 StartZ=0 EndX=51.8 EndY=-18 EndZ=0
    g145: LineSegment StartX=48 StartY=-18 StartZ=0 EndX=47.8 EndY=-18 EndZ=0
    g146: LineSegment StartX=47.8 StartY=-18 StartZ=0 EndX=47.8 EndY=-20 EndZ=0
    g147: LineSegment StartX=47.8 StartY=-20 StartZ=0 EndX=48 EndY=-20 EndZ=0
    g148: LineSegment StartX=48 StartY=-20 StartZ=0 EndX=48 EndY=-18 EndZ=0
    g149: LineSegment StartX=46 StartY=-18 StartZ=0 EndX=45.8 EndY=-18 EndZ=0
    g150: LineSegment StartX=45.8 StartY=-18 StartZ=0 EndX=45.8 EndY=-20 EndZ=0
    g151: LineSegment StartX=45.8 StartY=-20 StartZ=0 EndX=46 EndY=-20 EndZ=0
    g152: LineSegment StartX=46 StartY=-20 StartZ=0 EndX=46 EndY=-18 EndZ=0
    g153: LineSegment StartX=44 StartY=-18 StartZ=0 EndX=43.8 EndY=-18 EndZ=0
    g154: LineSegment StartX=43.8 StartY=-18 StartZ=0 EndX=43.8 EndY=-20 EndZ=0
    g155: LineSegment StartX=43.8 StartY=-20 StartZ=0 EndX=44 EndY=-20 EndZ=0
    g156: LineSegment StartX=44 StartY=-20 StartZ=0 EndX=44 EndY=-18 EndZ=0
    g157: LineSegment StartX=41.8 StartY=-18 StartZ=0 EndX=42 EndY=-18 EndZ=0
    g158: LineSegment StartX=42 StartY=-18 StartZ=0 EndX=42 EndY=-20 EndZ=0
    g159: LineSegment StartX=42 StartY=-20 StartZ=0 EndX=41.8 EndY=-20 EndZ=0
    g160: LineSegment StartX=41.8 StartY=-20 StartZ=0 EndX=41.8 EndY=-18 EndZ=0
    g161: LineSegment StartX=38 StartY=-18 StartZ=0 EndX=37.8 EndY=-18 EndZ=0
    g162: LineSegment StartX=37.8 StartY=-18 StartZ=0 EndX=37.8 EndY=-20 EndZ=0
    g163: LineSegment StartX=37.8 StartY=-20 StartZ=0 EndX=38 EndY=-20 EndZ=0
    g164: LineSegment StartX=38 StartY=-20 StartZ=0 EndX=38 EndY=-18 EndZ=0
    g165: LineSegment StartX=36 StartY=-18 StartZ=0 EndX=35.8 EndY=-18 EndZ=0
    g166: LineSegment StartX=35.8 StartY=-18 StartZ=0 EndX=35.8 EndY=-20 EndZ=0
    g167: LineSegment StartX=35.8 StartY=-20 StartZ=0 EndX=36 EndY=-20 EndZ=0
    g168: LineSegment StartX=36 StartY=-20 StartZ=0 EndX=36 EndY=-18 EndZ=0
    g169: LineSegment StartX=34 StartY=-18 StartZ=0 EndX=33.8 EndY=-18 EndZ=0
    g170: LineSegment StartX=33.8 StartY=-18 StartZ=0 EndX=33.8 EndY=-20 EndZ=0
    g171: LineSegment StartX=33.8 StartY=-20 StartZ=0 EndX=34 EndY=-20 EndZ=0
    g172: LineSegment StartX=34 StartY=-20 StartZ=0 EndX=34 EndY=-18 EndZ=0
    g173: LineSegment StartX=31.8 StartY=-18 StartZ=0 EndX=32 EndY=-18 EndZ=0
    g174: LineSegment StartX=32 StartY=-18 StartZ=0 EndX=32 EndY=-20 EndZ=0
    g175: LineSegment StartX=32 StartY=-20 StartZ=0 EndX=31.8 EndY=-20 EndZ=0
    g176: LineSegment StartX=31.8 StartY=-20 StartZ=0 EndX=31.8 EndY=-18 EndZ=0
    g177: LineSegment StartX=27.8 StartY=-18 StartZ=0 EndX=28 EndY=-18 EndZ=0
    g178: LineSegment StartX=28 StartY=-18 StartZ=0 EndX=28 EndY=-20 EndZ=0
    g179: LineSegment StartX=28 StartY=-20 StartZ=0 EndX=27.8 EndY=-20 EndZ=0
    g180: LineSegment StartX=27.8 StartY=-20 StartZ=0 EndX=27.8 EndY=-18 EndZ=0
    g181: LineSegment StartX=26 StartY=-18 StartZ=0 EndX=25.8 EndY=-18 EndZ=0
    g182: LineSegment StartX=25.8 StartY=-18 StartZ=0 EndX=25.8 EndY=-20 EndZ=0
    g183: LineSegment StartX=25.8 StartY=-20 StartZ=0 EndX=26 EndY=-20 EndZ=0
    g184: LineSegment StartX=26 StartY=-20 StartZ=0 EndX=26 EndY=-18 EndZ=0
    g185: LineSegment StartX=24 StartY=-18 StartZ=0 EndX=23.8 EndY=-18 EndZ=0
    g186: LineSegment StartX=23.8 StartY=-18 StartZ=0 EndX=23.8 EndY=-20 EndZ=0
    g187: LineSegment StartX=23.8 StartY=-20 StartZ=0 EndX=24 EndY=-20 EndZ=0
    g188: LineSegment StartX=24 StartY=-20 StartZ=0 EndX=24 EndY=-18 EndZ=0
    g189: LineSegment StartX=21.8 StartY=-18 StartZ=0 EndX=22 EndY=-18 EndZ=0
    g190: LineSegment StartX=22 StartY=-18 StartZ=0 EndX=22 EndY=-20 EndZ=0
    g191: LineSegment StartX=22 StartY=-20 StartZ=0 EndX=21.8 EndY=-20 EndZ=0
    g192: LineSegment StartX=21.8 StartY=-20 StartZ=0 EndX=21.8 EndY=-18 EndZ=0
    g193: LineSegment StartX=18 StartY=-18 StartZ=0 EndX=17.8 EndY=-18 EndZ=0
    g194: LineSegment StartX=17.8 StartY=-18 StartZ=0 EndX=17.8 EndY=-20 EndZ=0
    g195: LineSegment StartX=17.8 StartY=-20 StartZ=0 EndX=18 EndY=-20 EndZ=0
    g196: LineSegment StartX=18 StartY=-20 StartZ=0 EndX=18 EndY=-18 EndZ=0
    g197: LineSegment StartX=16 StartY=-18 StartZ=0 EndX=15.8 EndY=-18 EndZ=0
    g198: LineSegment StartX=15.8 StartY=-18 StartZ=0 EndX=15.8 EndY=-20 EndZ=0
    g199: LineSegment StartX=15.8 StartY=-20 StartZ=0 EndX=16 EndY=-20 EndZ=0
    g200: LineSegment StartX=16 StartY=-20 StartZ=0 EndX=16 EndY=-18 EndZ=0
    g201: LineSegment StartX=14 StartY=-18 StartZ=0 EndX=13.8 EndY=-18 EndZ=0
    g202: LineSegment StartX=13.8 StartY=-18 StartZ=0 EndX=13.8 EndY=-20 EndZ=0
    g203: LineSegment StartX=13.8 StartY=-20 StartZ=0 EndX=14 EndY=-20 EndZ=0
    g204: LineSegment StartX=14 StartY=-20 StartZ=0 EndX=14 EndY=-18 EndZ=0
    g205: LineSegment StartX=11.8 StartY=-18 StartZ=0 EndX=12 EndY=-18 EndZ=0
    g206: LineSegment StartX=12 StartY=-18 StartZ=0 EndX=12 EndY=-20 EndZ=0
    g207: LineSegment StartX=12 StartY=-20 StartZ=0 EndX=11.8 EndY=-20 EndZ=0
    g208: LineSegment StartX=11.8 StartY=-20 StartZ=0 EndX=11.8 EndY=-18 EndZ=0
    g209: LineSegment StartX=7.8 StartY=-18 StartZ=0 EndX=8 EndY=-18 EndZ=0
    g210: LineSegment StartX=8 StartY=-18 StartZ=0 EndX=8 EndY=-20 EndZ=0
    g211: LineSegment StartX=8 StartY=-20 StartZ=0 EndX=7.8 EndY=-20 EndZ=0
    g212: LineSegment StartX=7.8 StartY=-20 StartZ=0 EndX=7.8 EndY=-18 EndZ=0
    g213: LineSegment StartX=6 StartY=-18 StartZ=0 EndX=5.8 EndY=-18 EndZ=0
    g214: LineSegment StartX=5.8 StartY=-18 StartZ=0 EndX=5.8 EndY=-20 EndZ=0
    g215: LineSegment StartX=5.8 StartY=-20 StartZ=0 EndX=6 EndY=-20 EndZ=0
    g216: LineSegment StartX=6 StartY=-20 StartZ=0 EndX=6 EndY=-18 EndZ=0
    g217: LineSegment StartX=4 StartY=-18 StartZ=0 EndX=3.8 EndY=-18 EndZ=0
    g218: LineSegment StartX=3.8 StartY=-18 StartZ=0 EndX=3.8 EndY=-20 EndZ=0
    g219: LineSegment StartX=3.8 StartY=-20 StartZ=0 EndX=4 EndY=-20 EndZ=0
    g220: LineSegment StartX=4 StartY=-20 StartZ=0 EndX=4 EndY=-18 EndZ=0
    g221: LineSegment StartX=1.8 StartY=-18 StartZ=0 EndX=2 EndY=-18 EndZ=0
    g222: LineSegment StartX=2 StartY=-18 StartZ=0 EndX=2 EndY=-20 EndZ=0
    g223: LineSegment StartX=2 StartY=-20 StartZ=0 EndX=1.8 EndY=-20 EndZ=0
    g224: LineSegment StartX=1.8 StartY=-20 StartZ=0 EndX=1.8 EndY=-18 EndZ=0
  constraints (676):
    c: Horizontal(g0)
    c: DistanceY(g0,g-1) = 20
    c: DistanceX(g0,g0) = 100
    c: DistanceX(g0,g-1) = 30
    c: Coincident(g1,g2)
    c: Coincident(g2,g3)
    c: Coincident(g3,g4)
    c: Coincident(g4,g1)
    c: Horizontal(g1)
    c: Horizontal(g3)
    c: Vertical(g2)
    c: Vertical(g4)
    c: PointOnObject(g1,g-1)
    c: DistanceY(g4,g4) = 2
    c: DistanceX(g3,g3) = 0.2
    c: Coincident(g5,g6)
    c: Coincident(g6,g7)
    c: Coincident(g7,g8)
    c: Coincident(g8,g5)
    c: Horizontal(g5)
    c: Horizontal(g7)
    c: Vertical(g6)
    c: Vertical(g8)
    c: Equal(g4,g8) = 2
    c: Equal(g3,g7) = 0.2
    c: Coincident(g9,g10)
    c: Coincident(g10,g11)
    c: Coincident(g11,g12)
    c: Coincident(g12,g9)
    c: Horizontal(g9)
    c: Horizontal(g11)
    c: Vertical(g10)
    c: Vertical(g12)
    c: Equal(g8,g12) = 2
    c: Equal(g7,g11) = 0.2
    c: DistanceX(g9,g5) = 2
    c: Coincident(g13,g14)
    c: Coincident(g14,g15)
    c: Coincident(g15,g16)
    c: Coincident(g16,g13)
    c: Horizontal(g13)
    c: Horizontal(g15)
    c: Vertical(g14)
    c: Vertical(g16)
    c: Equal(g11,g15)
    c: Equal(g10,g14)
    c: Horizontal(g1,g5)
    c: Horizontal(g5,g9)
    c: Horizontal(g9,g13)
    c: Coincident(g17,g18)
    c: Coincident(g18,g19)
    c: Coincident(g19,g20)
    c: Coincident(g20,g17)
    c: Horizontal(g17)
    c: Horizontal(g19)
    c: Vertical(g18)
    c: Vertical(g20)
    c: Equal(g4,g20) = 2
    c: Equal(g3,g19) = 0.2
    c: Coincident(g21,g22)
    c: Coincident(g22,g23)
    c: Coincident(g23,g24)
    c: Coincident(g24,g21)
    c: Horizontal(g21)
    c: Horizontal(g23)
    c: Vertical(g22)
    c: Vertical(g24)
    c: Equal(g20,g24) = 2
    c: Equal(g19,g23) = 0.2
    c: Coincident(g25,g26)
    c: Coincident(g26,g27)
    c: Coincident(g27,g28)
    c: Coincident(g28,g25)
    c: Horizontal(g25)
    c: Horizontal(g27)
    c: Vertical(g26)
    c: Vertical(g28)
    c: Equal(g24,g28) = 2
    c: Equal(g23,g27) = 0.2
    c: DistanceX(g25,g21) = 2
    c: Coincident(g29,g30)
    c: Coincident(g30,g31)
    c: Coincident(g31,g32)
    c: Coincident(g32,g29)
    c: Horizontal(g29)
    c: Horizontal(g31)
    c: Vertical(g30)
    c: Vertical(g32)
    c: Equal(g27,g31)
    c: Equal(g26,g30)
    c: Horizontal(g17,g21)
    c: Horizontal(g21,g25)
    c: Horizontal(g25,g29)
    c: PointOnObject(g17,g-1)
    c: Coincident(g33,g34)
    c: Coincident(g34,g35)
    c: Coincident(g35,g36)
    c: Coincident(g36,g33)
    c: Horizontal(g33)
    c: Horizontal(g35)
    c: Vertical(g34)
    c: Vertical(g36)
    c: Coincident(g37,g38)
    c: Coincident(g38,g39)
    c: Coincident(g39,g40)
    c: Coincident(g40,g37)
    c: Horizontal(g37)
    c: Horizontal(g39)
    c: Vertical(g38)
    c: Vertical(g40)
    c: Equal(g36,g40) = 2
    c: Equal(g35,g39) = 0.2
    c: Coincident(g41,g42)
    c: Coincident(g42,g43)
    c: Coincident(g43,g44)
    c: Coincident(g44,g41)
    c: Horizontal(g41)
    c: Horizontal(g43)
    c: Vertical(g42)
    c: Vertical(g44)
    c: Equal(g40,g44) = 2
    c: Equal(g39,g43) = 0.2
    c: DistanceX(g41,g37) = 2
    c: Coincident(g45,g46)
    c: Coincident(g46,g47)
    c: Coincident(g47,g48)
    c: Coincident(g48,g45)
    c: Horizontal(g45)
    c: Horizontal(g47)
    c: Vertical(g46)
    c: Vertical(g48)
    c: Equal(g43,g47)
    c: Equal(g42,g46)
    c: Horizontal(g33,g37)
    c: Horizontal(g37,g41)
    c: Horizontal(g41,g45)
    c: PointOnObject(g33,g-1)
    c: Coincident(g49,g50)
    c: Coincident(g50,g51)
    c: Coincident(g51,g52)
    c: Coincident(g52,g49)
    c: Horizontal(g49)
    c: Horizontal(g51)
    c: Vertical(g50)
    c: Vertical(g52)
    c: Equal(g4,g52) = 2
    c: Equal(g3,g51) = 0.2
    c: Coincident(g53,g54)
    c: Coincident(g54,g55)
    c: Coincident(g55,g56)
    c: Coincident(g56,g53)
    c: Horizontal(g53)
    c: Horizontal(g55)
    c: Vertical(g54)
    c: Vertical(g56)
    c: Equal(g52,g56) = 2
    c: Equal(g51,g55) = 0.2
    c: Coincident(g57,g58)
    c: Coincident(g58,g59)
    c: Coincident(g59,g60)
    c: Coincident(g60,g57)
    c: Horizontal(g57)
    c: Horizontal(g59)
    c: Vertical(g58)
    c: Vertical(g60)
    c: Equal(g56,g60) = 2
    c: Equal(g55,g59) = 0.2
    c: DistanceX(g57,g53) = 2
    c: Coincident(g61,g62)
    c: Coincident(g62,g63)
    c: Coincident(g63,g64)
    c: Coincident(g64,g61)
    c: Horizontal(g61)
    c: Horizontal(g63)
    c: Vertical(g62)
    c: Vertical(g64)
    c: Equal(g59,g63)
    c: Equal(g58,g62)
    c: Horizontal(g49,g53)
    c: Horizontal(g53,g57)
    c: Horizontal(g57,g61)
    c: Coincident(g65,g66)
    c: Coincident(g66,g67)
    c: Coincident(g67,g68)
    c: Coincident(g68,g65)
    c: Horizontal(g65)
    c: Horizontal(g67)
    c: Vertical(g66)
    c: Vertical(g68)
    c: Equal(g52,g68) = 2
    c: Equal(g51,g67) = 0.2
    c: Coincident(g69,g70)
    c: Coincident(g70,g71)
    c: Coincident(g71,g72)
    c: Coincident(g72,g69)
    c: Horizontal(g69)
    c: Horizontal(g71)
    c: Vertical(g70)
    c: Vertical(g72)
    c: Equal(g68,g72) = 2
    c: Equal(g67,g71) = 0.2
    c: Coincident(g73,g74)
    c: Coincident(g74,g75)
    c: Coincident(g75,g76)
    c: Coincident(g76,g73)
    c: Horizontal(g73)
    c: Horizontal(g75)
    c: Vertical(g74)
    c: Vertical(g76)
    c: Equal(g72,g76) = 2
    c: Equal(g71,g75) = 0.2
    c: DistanceX(g73,g69) = 2
    c: Coincident(g77,g78)
    c: Coincident(g78,g79)
    c: Coincident(g79,g80)
    c: Coincident(g80,g77)
    c: Horizontal(g77)
    c: Horizontal(g79)
    c: Vertical(g78)
    c: Vertical(g80)
    c: Equal(g75,g79)
    c: Equal(g74,g78)
    c: Horizontal(g65,g69)
    c: Horizontal(g69,g73)
    c: Horizontal(g73,g77)
    c: Coincident(g81,g82)
    c: Coincident(g82,g83)
    c: Coincident(g83,g84)
    c: Coincident(g84,g81)
    c: Horizontal(g81)
    c: Horizontal(g83)
    c: Vertical(g82)
    c: Vertical(g84)
    c: Coincident(g85,g86)
    c: Coincident(g86,g87)
    c: Coincident(g87,g88)
    c: Coincident(g88,g85)
    c: Horizontal(g85)
    c: Horizontal(g87)
    c: Vertical(g86)
    c: Vertical(g88)
    c: Equal(g84,g88) = 2
    c: Equal(g83,g87) = 0.2
    c: Coincident(g89,g90)
    c: Coincident(g90,g91)
    c: Coincident(g91,g92)
    c: Coincident(g92,g89)
    c: Horizontal(g89)
    c: Horizontal(g91)
    c: Vertical(g90)
    c: Vertical(g92)
    c: Equal(g88,g92) = 2
    c: Equal(g87,g91) = 0.2
    c: DistanceX(g89,g85) = 2
    c: Coincident(g93,g94)
    c: Coincident(g94,g95)
    c: Coincident(g95,g96)
    c: Coincident(g96,g93)
    c: Horizontal(g93)
    c: Horizontal(g95)
    c: Vertical(g94)
    c: Vertical(g96)
    c: Equal(g91,g95)
    c: Equal(g90,g94)
    c: Horizontal(g81,g85)
    c: Horizontal(g85,g89)
    c: Horizontal(g89,g93)
    c: PointOnObject(g49,g-1)
    c: PointOnObject(g65,g-1)
    c: DistanceX(g53,g49) = 2
    c: DistanceX(g69,g65) = 2
    c: PointOnObject(g81,g-1)
    c: DistanceX(g37,g33) = 2
    c: DistanceX(g21,g17) = 2
    c: DistanceX(g5,g1) = 2
    c: Coincident(g97,g98)
    c: Coincident(g98,g99)
    c: Coincident(g99,g100)
    c: Coincident(g100,g97)
    c: Horizontal(g97)
    c: Horizontal(g99)
    c: Vertical(g98)
    c: Vertical(g100)
    c: Equal(g4,g100) = 2
    c: Equal(g3,g99) = 0.2
    c: Coincident(g101,g102)
    c: Coincident(g102,g103)
    c: Coincident(g103,g104)
    c: Coincident(g104,g101)
    c: Horizontal(g101)
    c: Horizontal(g103)
    c: Vertical(g102)
    c: Vertical(g104)
    c: Equal(g100,g104) = 2
    c: Equal(g99,g103) = 0.2
    c: Coincident(g105,g106)
    c: Coincident(g106,g107)
    c: Coincident(g107,g108)
    c: Coincident(g108,g105)
    c: Horizontal(g105)
    c: Horizontal(g107)
    c: Vertical(g106)
    c: Vertical(g108)
    c: Equal(g104,g108) = 2
    c: Equal(g103,g107) = 0.2
    c: DistanceX(g105,g101) = 2
    c: Coincident(g109,g110)
    c: Coincident(g110,g111)
    c: Coincident(g111,g112)
    c: Coincident(g112,g109)
    c: Horizontal(g109)
    c: Horizontal(g111)
    c: Vertical(g110)
    c: Vertical(g112)
    c: Equal(g107,g111)
    c: Equal(g106,g110)
    c: Horizontal(g97,g101)
    c: Horizontal(g101,g105)
    c: Horizontal(g105,g109)
    c: DistanceX(g17,g13) = 4
    c: DistanceX(g13,g9) = 2
    c: DistanceX(g33,g29) = 4
    c: DistanceX(g49,g45) = 4
    c: DistanceX(g45,g41) = 2
    c: DistanceX(g61,g57) = 2
    c: DistanceX(g65,g61) = 4
    c: DistanceX(g77,g73) = 2
    c: DistanceX(g85,g81) = 2
    c: DistanceX(g81,g77) = 4
    c: DistanceX(g93,g89) = 2
    c: PointOnObject(g97,g-1)
    c: DistanceX(g97,g93) = 4
    c: DistanceX(g101,g97) = 2
    c: DistanceX(g109,g105) = 2
    c: DistanceX(g29,g25) = 2
    c: Equal(g31,g35)
    c: Equal(g30,g36)
    c: Equal(g79,g83)
    c: Equal(g78,g84)
    c: Coincident(g113,g114)
    c: Coincident(g114,g115)
    c: Coincident(g115,g116)
    c: Coincident(g116,g113)
    c: Horizontal(g113)
    c: Horizontal(g115)
    c: Vertical(g114)
    c: Vertical(g116)
    c: Equal(g4,g116) = 2
    c: Equal(g3,g115) = 0.2
    c: Coincident(g117,g118)
    c: Coincident(g118,g119)
    c: Coincident(g119,g120)
    c: Coincident(g120,g117)
    c: Horizontal(g117)
    c: Horizontal(g119)
    c: Vertical(g118)
    c: Vertical(g120)
    c: Equal(g116,g120) = 2
    c: Equal(g115,g119) = 0.2
    c: Coincident(g121,g122)
    c: Coincident(g122,g123)
    c: Coincident(g123,g124)
    c: Coincident(g124,g121)
    c: Horizontal(g121)
    c: Horizontal(g123)
    c: Vertical(g122)
    c: Vertical(g124)
    c: Equal(g120,g124) = 2
    c: Equal(g119,g123) = 0.2
    c: DistanceX(g121,g117) = 2
    c: Coincident(g125,g126)
    c: Coincident(g126,g127)
    c: Coincident(g127,g128)
    c: Coincident(g128,g125)
    c: Horizontal(g125)
    c: Horizontal(g127)
    c: Vertical(g126)
    c: Vertical(g128)
    c: Equal(g123,g127)
    c: Equal(g122,g126)
    c: Horizontal(g113,g117)
    c: Horizontal(g117,g121)
    c: Horizontal(g121,g125)
    c: Coincident(g129,g130)
    c: Coincident(g130,g131)
    c: Coincident(g131,g132)
    c: Coincident(g132,g129)
    c: Horizontal(g129)
    c: Horizontal(g131)
    c: Vertical(g130)
    c: Vertical(g132)
    c: Equal(g116,g132) = 2
    c: Equal(g115,g131) = 0.2
    c: Coincident(g133,g134)
    c: Coincident(g134,g135)
    c: Coincident(g135,g136)
    c: Coincident(g136,g133)
    c: Horizontal(g133)
    c: Horizontal(g135)
    c: Vertical(g134)
    c: Vertical(g136)
    c: Equal(g132,g136) = 2
    c: Equal(g131,g135) = 0.2
    c: Coincident(g137,g138)
    c: Coincident(g138,g139)
    c: Coincident(g139,g140)
    c: Coincident(g140,g137)
    c: Horizontal(g137)
    c: Horizontal(g139)
    c: Vertical(g138)
    c: Vertical(g140)
    c: Equal(g136,g140) = 2
    c: Equal(g135,g139) = 0.2
    c: DistanceX(g137,g133) = 2
    c: Coincident(g141,g142)
    c: Coincident(g142,g143)
    c: Coincident(g143,g144)
    c: Coincident(g144,g141)
    c: Horizontal(g141)
    c: Horizontal(g143)
    c: Vertical(g142)
    c: Vertical(g144)
    c: Equal(g139,g143)
    c: Equal(g138,g142)
    c: Horizontal(g129,g133)
    c: Horizontal(g133,g137)
    c: Horizontal(g137,g141)
    c: Coincident(g145,g146)
    c: Coincident(g146,g147)
    c: Coincident(g147,g148)
    c: Coincident(g148,g145)
    c: Horizontal(g145)
    c: Horizontal(g147)
    c: Vertical(g146)
    c: Vertical(g148)
    c: Coincident(g149,g150)
    c: Coincident(g150,g151)
    c: Coincident(g151,g152)
    c: Coincident(g152,g149)
    c: Horizontal(g149)
    c: Horizontal(g151)
    c: Vertical(g150)
    c: Vertical(g152)
    c: Equal(g148,g152) = 2
    c: Equal(g147,g151) = 0.2
    c: Coincident(g153,g154)
    c: Coincident(g154,g155)
    c: Coincident(g155,g156)
    c: Coincident(g156,g153)
    c: Horizontal(g153)
    c: Horizontal(g155)
    c: Vertical(g154)
    c: Vertical(g156)
    c: Equal(g152,g156) = 2
    c: Equal(g151,g155) = 0.2
    c: DistanceX(g153,g149) = 2
    c: Coincident(g157,g158)
    c: Coincident(g158,g159)
    c: Coincident(g159,g160)
    c: Coincident(g160,g157)
    c: Horizontal(g157)
    c: Horizontal(g159)
    c: Vertical(g158)
    c: Vertical(g160)
    c: Equal(g155,g159)
    c: Equal(g154,g158)
    c: Horizontal(g145,g149)
    c: Horizontal(g149,g153)
    c: Horizontal(g153,g157)
    c: Coincident(g161,g162)
    c: Coincident(g162,g163)
    c: Coincident(g163,g164)
    c: Coincident(g164,g161)
    c: Horizontal(g161)
    c: Horizontal(g163)
    c: Vertical(g162)
    c: Vertical(g164)
    c: Equal(g116,g164) = 2
    c: Equal(g115,g163) = 0.2
    c: Coincident(g165,g166)
    c: Coincident(g166,g167)
    c: Coincident(g167,g168)
    c: Coincident(g168,g165)
    c: Horizontal(g165)
    c: Horizontal(g167)
    c: Vertical(g166)
    c: Vertical(g168)
    c: Equal(g164,g168) = 2
    c: Equal(g163,g167) = 0.2
    c: Coincident(g169,g170)
    c: Coincident(g170,g171)
    c: Coincident(g171,g172)
    c: Coincident(g172,g169)
    c: Horizontal(g169)
    c: Horizontal(g171)
    c: Vertical(g170)
    c: Vertical(g172)
    c: Equal(g168,g172) = 2
    c: Equal(g167,g171) = 0.2
    c: DistanceX(g169,g165) = 2
    c: Coincident(g173,g174)
    c: Coincident(g174,g175)
    c: Coincident(g175,g176)
    c: Coincident(g176,g173)
    c: Horizontal(g173)
    c: Horizontal(g175)
    c: Vertical(g174)
    c: Vertical(g176)
    c: Equal(g171,g175)
    c: Equal(g170,g174)
    c: Horizontal(g161,g165)
    c: Horizontal(g165,g169)
    c: Horizontal(g169,g173)
    c: Coincident(g177,g178)
    c: Coincident(g178,g179)
    c: Coincident(g179,g180)
    c: Coincident(g180,g177)
    c: Horizontal(g177)
    c: Horizontal(g179)
    c: Vertical(g178)
    c: Vertical(g180)
    c: Equal(g164,g180) = 2
    c: Equal(g163,g179) = 0.2
    c: Coincident(g181,g182)
    c: Coincident(g182,g183)
    c: Coincident(g183,g184)
    c: Coincident(g184,g181)
    c: Horizontal(g181)
    c: Horizontal(g183)
    c: Vertical(g182)
    c: Vertical(g184)
    c: Equal(g180,g184) = 2
    c: Equal(g179,g183) = 0.2
    c: Coincident(g185,g186)
    c: Coincident(g186,g187)
    c: Coincident(g187,g188)
    c: Coincident(g188,g185)
    c: Horizontal(g185)
    c: Horizontal(g187)
    c: Vertical(g186)
    c: Vertical(g188)
    c: Equal(g184,g188) = 2
    c: Equal(g183,g187) = 0.2
    c: DistanceX(g185,g181) = 2
    c: Coincident(g189,g190)
    c: Coincident(g190,g191)
    c: Coincident(g191,g192)
    c: Coincident(g192,g189)
    c: Horizontal(g189)
    c: Horizontal(g191)
    c: Vertical(g190)
    c: Vertical(g192)
    c: Equal(g187,g191)
    c: Equal(g186,g190)
    c: Horizontal(g177,g181)
    c: Horizontal(g181,g185)
    c: Horizontal(g185,g189)
    c: Coincident(g193,g194)
    c: Coincident(g194,g195)
    c: Coincident(g195,g196)
    c: Coincident(g196,g193)
    c: Horizontal(g193)
    c: Horizontal(g195)
    c: Vertical(g194)
    c: Vertical(g196)
    c: Coincident(g197,g198)
    c: Coincident(g198,g199)
    c: Coincident(g199,g200)
    c: Coincident(g200,g197)
    c: Horizontal(g197)
    c: Horizontal(g199)
    c: Vertical(g198)
    c: Vertical(g200)
    c: Equal(g196,g200) = 2
    c: Equal(g195,g199) = 0.2
    c: Coincident(g201,g202)
    c: Coincident(g202,g203)
    c: Coincident(g203,g204)
    c: Coincident(g204,g201)
    c: Horizontal(g201)
    c: Horizontal(g203)
    c: Vertical(g202)
    c: Vertical(g204)
    c: Equal(g200,g204) = 2
    c: Equal(g199,g203) = 0.2
    c: DistanceX(g201,g197) = 2
    c: Coincident(g205,g206)
    c: Coincident(g206,g207)
    c: Coincident(g207,g208)
    c: Coincident(g208,g205)
    c: Horizontal(g205)
    c: Horizontal(g207)
    c: Vertical(g206)
    c: Vertical(g208)
    c: Equal(g203,g207)
    c: Equal(g202,g206)
    c: Horizontal(g193,g197)
    c: Horizontal(g197,g201)
    c: Horizontal(g201,g205)
    c: DistanceX(g165,g161) = 2
    c: DistanceX(g181,g177) = 2
    c: DistanceX(g149,g145) = 2
    c: DistanceX(g133,g129) = 2
    c: DistanceX(g117,g113) = 2
    c: Coincident(g209,g210)
    c: Coincident(g210,g211)
    c: Coincident(g211,g212)
    c: Coincident(g212,g209)
    c: Horizontal(g209)
    c: Horizontal(g211)
    c: Vertical(g210)
    c: Vertical(g212)
    c: Equal(g116,g212) = 2
    c: Equal(g115,g211) = 0.2
    c: Coincident(g213,g214)
    c: Coincident(g214,g215)
    c: Coincident(g215,g216)
    c: Coincident(g216,g213)
    c: Horizontal(g213)
    c: Horizontal(g215)
    c: Vertical(g214)
    c: Vertical(g216)
    c: Equal(g212,g216) = 2
    c: Equal(g211,g215) = 0.2
    c: Coincident(g217,g218)
    c: Coincident(g218,g219)
    c: Coincident(g219,g220)
    c: Coincident(g220,g217)
    c: Horizontal(g217)
    c: Horizontal(g219)
    c: Vertical(g218)
    c: Vertical(g220)
    c: Equal(g216,g220) = 2
    c: Equal(g215,g219) = 0.2
    c: DistanceX(g217,g213) = 2
    c: Coincident(g221,g222)
    c: Coincident(g222,g223)
    c: Coincident(g223,g224)
    c: Coincident(g224,g221)
    c: Horizontal(g221)
    c: Horizontal(g223)
    c: Vertical(g222)
    c: Vertical(g224)
    c: Equal(g219,g223)
    c: Equal(g218,g222)
    c: Horizontal(g209,g213)
    c: Horizontal(g213,g217)
    c: Horizontal(g217,g221)
    c: DistanceX(g129,g125) = 4
    c: DistanceX(g125,g121) = 2
    c: DistanceX(g145,g141) = 4
    c: DistanceX(g161,g157) = 4
    c: DistanceX(g157,g153) = 2
    c: DistanceX(g173,g169) = 2
    c: DistanceX(g177,g173) = 4
    c: DistanceX(g189,g185) = 2
    c: DistanceX(g197,g193) = 2
    c: DistanceX(g193,g189) = 4
    c: DistanceX(g205,g201) = 2
    c: DistanceX(g209,g205) = 4
    c: DistanceX(g213,g209) = 2
    c: DistanceX(g221,g217) = 2
    c: DistanceX(g141,g137) = 2
    c: Equal(g143,g147)
    c: Equal(g142,g148)
    c: Equal(g191,g195)
    c: Equal(g190,g196)
    c: PointOnObject(g223,g0)
    c: PointOnObject(g207,g0)
    c: PointOnObject(g191,g0)
    c: PointOnObject(g175,g0)
    c: PointOnObject(g159,g0)
    c: PointOnObject(g143,g0)
    c: PointOnObject(g127,g0)
    c: DistanceX(g-1,g111) = 1.8
    c: Vertical(g221,g111)
FEATURE [PartDesign::Pocket] Pocket014
  BaseFeature = -> Pocket013
  Length = 1
  Length2 = 100
  Profile = -> Sketch018
  Type = 0
FEATURE [Sketcher::SketchObject] Sketch019
  FullyConstrained = true
  MapMode = 5
  Placement = pos=(0,0,0) rot=(0.57735,0.57735,0.57735;2.0944rad)
  Support = -> [YZ_Plane002]
  sketch-geometry (8):
    g0: LineSegment StartX=-9 StartY=2.25 StartZ=0 EndX=-4 EndY=2.25 EndZ=0
    g1: LineSegment StartX=-4 StartY=2.25 StartZ=0 EndX=-4 EndY=0.75 EndZ=0
    g2: LineSegment StartX=-4 StartY=0.75 StartZ=0 EndX=-9 EndY=0.75 EndZ=0
    g3: LineSegment StartX=-9 StartY=0.75 StartZ=0 EndX=-9 EndY=2.25 EndZ=0
    g4: LineSegment StartX=-17.5 StartY=2.25 StartZ=0 EndX=-12.5 EndY=2.25 EndZ=0
    g5: LineSegment StartX=-12.5 StartY=2.25 StartZ=0 EndX=-12.5 EndY=0.75 EndZ=0
    g6: LineSegment StartX=-12.5 StartY=0.75 StartZ=0 EndX=-17.5 EndY=0.75 EndZ=0
    g7: LineSegment StartX=-17.5 StartY=0.75 StartZ=0 EndX=-17.5 EndY=2.25 EndZ=0
  constraints (24):
    c: Coincident(g0,g1)
    c: Coincident(g1,g2)
    c: Coincident(g2,g3)
    c: Coincident(g3,g0)
    c: Horizontal(g0)
    c: Horizontal(g2)
    c: Vertical(g1)
    c: Vertical(g3)
    c: Coincident(g4,g5)
    c: Coincident(g5,g6)
    c: Coincident(g6,g7)
    c: Coincident(g7,g4)
    c: Horizontal(g4)
    c: Horizontal(g6)
    c: Vertical(g5)
    c: Vertical(g7)
    c: Equal(g4,g0)
    c: Equal(g3,g7)
    c: Horizontal(g4,g0)
    c: DistanceY(g1,g1) = 1.5
    c: DistanceX(g4,g0) = 3.5
    c: DistanceX(g0,g0) = 5
    c: DistanceX(g0,g-1) = 4
    c: DistanceY(g-1,g6) = 0.75
FEATURE [PartDesign::Pocket] Pocket015
  BaseFeature = -> Pocket014
  Length = 8
  Length2 = 100
  Profile = -> Sketch019
  Reversed = true
  Type = 0
FEATURE [Part::Part2DObjectPython] ShapeString004  # Draft 2D object (typed FeaturePython)
  FontFile = <path> Squares/AdobeGothicStd-Bold.otf
  Placement = pos=(0,-12.5,2) rot=(0,0,1;0rad)
  Size = 4
  String = 4   25  26  27   28  29   30  
  Support = -> [XY_Plane002]
  Tracking = 0
FEATURE [Part::Part2DObjectPython] ShapeString005  # Draft 2D object (typed FeaturePython)
  FontFile = <path> Squares/AdobeGothicStd-Bold.otf
  Placement = pos=(64,-12,1) rot=(0,1,0;3.14159rad)
  Size = 4
  String = 30   29  28   27  26  25   2
  Support = -> [DatumPlane002]
  Tracking = 0
FEATURE [Sketcher::SketchObject] Sketch020
  FullyConstrained = true
  MapMode = 5
  Support = -> [XY_Plane003]
  sketch-geometry (4):
    g0: LineSegment StartX=0 StartY=0 StartZ=0 EndX=12 EndY=0 EndZ=0
    g1: LineSegment StartX=12 StartY=0 StartZ=0 EndX=12 EndY=-3.25 EndZ=0
    g2: LineSegment StartX=12 StartY=-3.25 StartZ=0 EndX=0 EndY=-3.25 EndZ=0
    g3: LineSegment StartX=0 StartY=-3.25 StartZ=0 EndX=0 EndY=0 EndZ=0
  constraints (11):
    c: Coincident(g0,g1)
    c: Coincident(g1,g2)
    c: Coincident(g2,g3)
    c: Coincident(g3,g0)
    c: Horizontal(g0)
    c: Horizontal(g2)
    c: Vertical(g1)
    c: Vertical(g3)
    c: Coincident(g0,g-1)
    c: DistanceX(g0,g0) = 12
    c: DistanceY(g1,g1) = 3.25
FEATURE [PartDesign::Pad] Pad003
  Direction = (1,1,1)
  Length = 1.4
  Length2 = 100
  Profile = -> Sketch020
  Type = 0
FEATURE [PartDesign::Fillet] Fillet  label="biscuit"
  Base = -> Pad003 [Face6,Face5,Edge2,Edge5,Edge1,Edge8]
  BaseFeature = -> Pad003
  Radius = 0.25
  SupportTransform = false
FEATURE [PartDesign::Body] Body003  label="Biscuit"
  Group = -> [Sketch020,Pad003,Fillet]
  Origin = -> Origin003
  Tip = -> Fillet
FEATURE [Mesh::Feature] Mesh  label="biscuit (Meshed)"
FEATURE [PartDesign::Pocket] Pocket016
  BaseFeature = -> Pocket010
  Length = 1
  Length2 = 100
  Profile = -> ShapeString
  Type = 0
FEATURE [PartDesign::Pocket] Pocket017
  BaseFeature = -> Pocket016
  Length = 1
  Length2 = 100
  Profile = -> ShapeString001
  Type = 0
FEATURE [PartDesign::Pocket] Pocket018
  BaseFeature = -> Pocket017
  Length = 1
  Length2 = 100
  Profile = -> ShapeString002
  Type = 0
FEATURE [PartDesign::Pocket] Pocket020
  BaseFeature = -> Pocket015
  Length = 5
  Length2 = 100
  Profile = -> ShapeString004
  Reversed = true
  Type = 0
FEATURE [PartDesign::Pocket] Pocket021  label="extension"
  BaseFeature = -> Pocket020
  Length = 5
  Length2 = 100
  Profile = -> ShapeString005
  Reversed = true
  Type = 0
FEATURE [PartDesign::Body] Body002  label="Extension"
  Group = -> [Sketch013,Pad002,Sketch015,Pocket011,Sketch016,Pocket012,DatumPlane002,Sketch017,Pocket013,Sketch018,Pocket014,Pocket015,ShapeString004,ShapeString005,Pocket020,Sketch019,Pocket021]
  Origin = -> Origin002
  Tip = -> Pocket021
FEATURE [Mesh::Feature] Mesh006  label="extension (Meshed)"
FEATURE [PartDesign::Pocket] Pocket022
  BaseFeature = -> Pocket018
  Length = 1
  Length2 = 100
  Profile = -> ShapeString003
  Type = 0
FEATURE [PartDesign::Body] Body  label="T Square"
  Group = -> [Sketch,Pad,Sketch001,Pocket,Sketch002,Pocket001,Sketch003,Pocket002,Sketch004,Pocket003,Sketch006,Pocket004,Sketch007,Pocket005,DatumPlane,Sketch008,Pocket006,Sketch009,Pocket007,Sketch010,Sketch011,Pocket008,Pocket009,DatumPlane001,Sketch012,Pocket010,ShapeString,Pocket016,ShapeString001,Pocket017,ShapeString002,Pocket018,ShapeString003,Pocket022]
  Origin = -> Origin
  Tip = -> Pocket022
FEATURE [Mesh::Feature] Mesh007  label="T Square (Meshed)"
FEATURE [Mesh::Feature] Mesh008  label="Clip (Meshed)"
note: 6 file-system paths scrubbed to <path> (originals preserved in the JSON sidecar)
